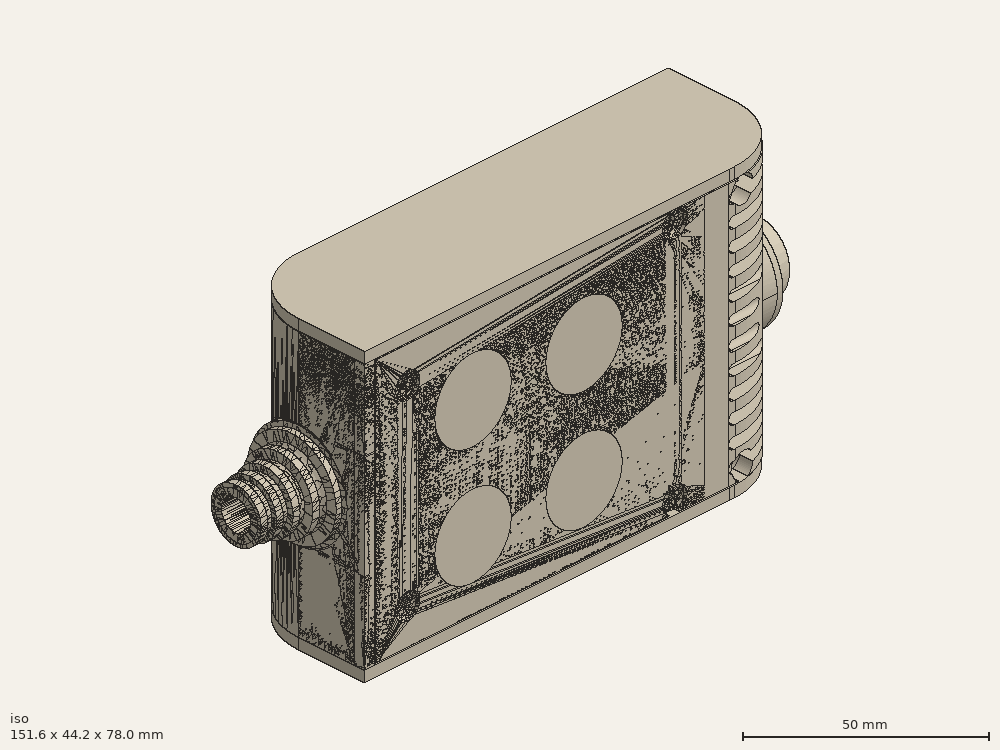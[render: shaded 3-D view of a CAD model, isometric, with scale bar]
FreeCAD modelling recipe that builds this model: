
FCSTD DOCUMENT  (FreeCAD 0.19R0.19.2)
Label: enclosure_187FCStd
License: All rights reserved
LicenseURL: http://en.wikipedia.org/wiki/All_rights_reserved
objects: Part::Revolution×152, Part::MultiFuse×146, Part::Feature×146, Sketcher::SketchObject×84, Part::Cut×70, Part::Cylinder×70, Part::Extrusion×67, Part::Fillet×58, Part::Box×36, App::MeasureDistance×4, PartDesign::Body×2, Image::ImagePlane×1
note: 831 computed .brp shape members not serialized (recipe doc carries the construction recipe); baked Part::Feature solids carry a one-line shape summary decoded from their .brp

FEATURE [Sketcher::SketchObject] Sketch  label="topSketch"
  FullyConstrained = true
  sketch-geometry (20):
    g0: LineSegment StartX=5.21097e-06 StartY=3 StartZ=0 EndX=5.21097e-06 EndY=19 EndZ=0
    g1: ArcOfCircle CenterX=19 CenterY=19 CenterZ=0 NormalX=0 NormalY=0 NormalZ=1 AngleXU=0 Radius=19 StartAngle=1.5708 EndAngle=3.14159
    g2: ArcOfCircle CenterX=19 CenterY=19 CenterZ=0 NormalX=0 NormalY=0 NormalZ=1 AngleXU=0 Radius=16 StartAngle=1.5708 EndAngle=3.14159
    g3: LineSegment StartX=114 StartY=35 StartZ=0 EndX=19 EndY=35 EndZ=0
    g4: LineSegment StartX=5.21097e-06 StartY=3 StartZ=0 EndX=5.21097e-06 EndY=0 EndZ=0
    g5: LineSegment StartX=3 StartY=0 StartZ=0 EndX=5.21097e-06 EndY=0 EndZ=0
    g6: LineSegment StartX=3 StartY=19 StartZ=0 EndX=3 EndY=0 EndZ=0
    g7: LineSegment StartX=19 StartY=38 StartZ=0 EndX=124 EndY=38 EndZ=0
    g8: Circle CenterX=119 CenterY=35 CenterZ=0 NormalX=0 NormalY=0 NormalZ=1 AngleXU=0 Radius=1
    g9: Circle CenterX=121 CenterY=35 CenterZ=0 NormalX=0 NormalY=0 NormalZ=1 AngleXU=0 Radius=1
    g10: Circle CenterX=121 CenterY=33 CenterZ=0 NormalX=0 NormalY=0 NormalZ=1 AngleXU=0 Radius=1
    g11: BSplineCurve PolesCount=3 KnotsCount=2 Degree=2 IsPeriodic=0
    g12: GeomPoint X=119 Y=35 Z=0
    g13: GeomPoint X=121 Y=33 Z=0
    g14: LineSegment StartX=119 StartY=35 StartZ=0 EndX=114 EndY=35 EndZ=0
    g15: ArcOfCircle CenterX=105 CenterY=19 CenterZ=0 NormalX=0 NormalY=0 NormalZ=1 AngleXU=0 Radius=19 StartAngle=5.7297 EndAngle=6.28319
    g16: ArcOfCircle CenterX=105 CenterY=19 CenterZ=0 NormalX=0 NormalY=0 NormalZ=1 AngleXU=0 Radius=16 StartAngle=5.60905 EndAngle=6.28319
    g17: LineSegment StartX=121 StartY=33 StartZ=0 EndX=121 EndY=19 EndZ=0
    g18: LineSegment StartX=124 StartY=38 StartZ=0 EndX=124 EndY=19 EndZ=0
    g19: LineSegment StartX=117.5 StartY=9.01251 StartZ=0 EndX=121.163 EndY=9.0125 EndZ=0
  constraints (46):
    c: Vertical(g0)
    c: Block(g0)
    c: Coincident(g1,g0)
    c: Block(g1)
    c: Coincident(g2,g1)
    c: Block(g2)
    c: Coincident(g3,g2)
    c: Horizontal(g3)
    c: Tangent(g3,g2)
    c: Coincident(g4,g0)
    c: Distance(g4) = 3
    c: Vertical(g4)
    c: Coincident(g5,g4)
    c: Horizontal(g5)
    c: Coincident(g6,g2)
    c: Coincident(g6,g5)
    c: Vertical(g6)
    c: Horizontal(g7)
    c: Distance(g7) = 105
    c: Coincident(g7,g1)
    c: Block(g3)
    c: Weight(g8) = 1
    c: Equal(g8,g9)
    c: Equal(g8,g10)
    c: InternalAlignment(g8,g11)
    c: InternalAlignment(g9,g11)
    c: InternalAlignment(g10,g11)
    c: InternalAlignment(g12,g11)
    c: InternalAlignment(g13,g11)
    c: Block(g11)
    c: Coincident(g14,g11)
    c: Coincident(g14,g3)
    c: Horizontal(g14)
    c: Block(g15)
    c: Coincident(g16,g15)
    c: Block(g16)
    c: Coincident(g17,g11)
    c: Coincident(g17,g16)
    c: Vertical(g17)
    c: Distance(g17) = 14
    c: Coincident(g18,g7)
    c: Coincident(g18,g15)
    c: Vertical(g18)
    c: Distance(g18) = 19
    c: Coincident(g19,g16)
    c: Coincident(g19,g15)
FEATURE [Sketcher::SketchObject] Sketch001  label="bottomSketch"
  FullyConstrained = true
  sketch-geometry (32):
    g0: LineSegment StartX=3.3 StartY=-6.03275e-07 StartZ=0 EndX=98 EndY=-6.03275e-07 EndZ=0
    g1: ArcOfCircle CenterX=98 CenterY=19 CenterZ=0 NormalX=0 NormalY=0 NormalZ=1 AngleXU=0 Radius=19 StartAngle=4.71239 EndAngle=5.71103
    g2: LineSegment StartX=6.3 StartY=8 StartZ=0 EndX=3.3 EndY=8 EndZ=0
    g3: LineSegment StartX=3.3 StartY=8 StartZ=0 EndX=3.3 EndY=-6.03275e-07 EndZ=0
    g4: ArcOfCircle CenterX=8.3 CenterY=5 CenterZ=0 NormalX=0 NormalY=0 NormalZ=1 AngleXU=0 Radius=2 StartAngle=3.14159 EndAngle=4.71239
    g5: LineSegment StartX=6.3 StartY=8 StartZ=0 EndX=6.3 EndY=5 EndZ=0
    g6: ArcOfCircle CenterX=98 CenterY=19 CenterZ=0 NormalX=0 NormalY=0 NormalZ=1 AngleXU=0 Radius=12.7 StartAngle=4.71239 EndAngle=6.28319
    g7: LineSegment StartX=94.7 StartY=3 StartZ=0 EndX=8.3 EndY=3 EndZ=0
    g8-g12: Circle x5 (B-spline internal-alignment scaffolding for g13; pole/knot coordinates omitted)
    g13: BSplineCurve PolesCount=5 KnotsCount=3 Degree=3 IsPeriodic=0
    g14: GeomPoint X=98 Y=6.3 Z=0
    g15: GeomPoint X=96.3938 Y=4.71946 Z=0
    g16: GeomPoint X=94.7 Y=3 Z=0
    g17-g23: Circle x7 (B-spline internal-alignment scaffolding for g24; pole/knot coordinates omitted)
    g24: BSplineCurve PolesCount=7 KnotsCount=5 Degree=3 IsPeriodic=0
    g25-g29: GeomPoint x5 (B-spline internal-alignment scaffolding for g24; pole/knot coordinates omitted)
    g30: ArcOfCircle CenterX=98 CenterY=19 CenterZ=0 NormalX=0 NormalY=0 NormalZ=1 AngleXU=0 Radius=15.7 StartAngle=5.81226 EndAngle=6.28319
    g31: LineSegment StartX=110.7 StartY=19 StartZ=0 EndX=113.7 EndY=19 EndZ=0
  constraints (41):
    c: Horizontal(g0)
    c: Coincident(g1,g0)
    c: Block(g1)
    c: Horizontal(g2)
    c: Distance(g2) = 3
    c: Coincident(g3,g2)
    c: Vertical(g3)
    c: Coincident(g3,g0)
    c: Block(g4)
    c: Block(g2)
    c: Coincident(g5,g2)
    c: Coincident(g5,g4)
    c: Vertical(g5)
    c: Coincident(g6,g1)
    c: Block(g6)
    c: Coincident(g7,g4)
    c: Horizontal(g7)
    c: Block(g0)
    c: Block(g7)
    c: Block(g3)
    c: Coincident(g13,g6)
    c: Weight(g8) = 1
    c: Equal(g8, g9-g12) x4
    c: Coincident(g13,g7)
    c: InternalAlignment(g8-g12 -> g13) x5
    c: InternalAlignment(g14,g13)
    c: InternalAlignment(g15,g13)
    c: InternalAlignment(g16,g13)
    c: Block(g13)
    c: Weight(g17) = 1
    c: Equal(g17, g18-g23) x6
    c: Coincident(g24,g1)
    c: InternalAlignment(g17-g23 -> g24) x7
    c: InternalAlignment(g25-g29 -> g24) x5
    c: Block(g24)
    c: Coincident(g30,g24)
    c: Coincident(g31,g6)
    c: Coincident(g31,g30)
    c: Horizontal(g31)
    c: Block(g31)
    c: Block(g30)
FEATURE [Part::Extrusion] Extrude  label="top"
  Base = -> Sketch
  Dir = (0,0,1)
  DirMode = 2
  FaceMakerClass = Part::FaceMakerBullseye
  LengthFwd = 72
  LengthRev = 0
  Solid = true
  Symmetric = false
FEATURE [Part::Extrusion] Extrude001  label="bottom"
  Base = -> Sketch001
  Dir = (0,0,1)
  DirMode = 2
  FaceMakerClass = Part::FaceMakerBullseye
  LengthFwd = 71.4
  LengthRev = 0
  Placement = pos=(0,0,0.3) rot=(0,0,1;0rad)
  Solid = true
  Symmetric = false
FEATURE [Sketcher::SketchObject] Sketch002  label="topSketch001"
  FullyConstrained = true
  sketch-geometry (8):
    g0: ArcOfCircle CenterX=19 CenterY=19.0975 CenterZ=0 NormalX=0 NormalY=0 NormalZ=1 AngleXU=0 Radius=18.9025 StartAngle=1.5708 EndAngle=3.14674
    g1: LineSegment StartX=0.0977805 StartY=19.0003 StartZ=0 EndX=0.0977805 EndY=0.000251602 EndZ=0
    g2: LineSegment StartX=19 StartY=38 StartZ=0 EndX=124 EndY=38 EndZ=0
    g3: LineSegment StartX=0.0977805 StartY=0.000251602 StartZ=0 EndX=105.098 EndY=0.000251602 EndZ=0
    g4: LineSegment StartX=124 StartY=38 StartZ=0 EndX=125.616 EndY=38 EndZ=0
    g5: LineSegment StartX=105.098 StartY=0.000251602 StartZ=0 EndX=106.713 EndY=0.000251602 EndZ=0
    g6: ArcOfCircle CenterX=106.616 CenterY=19 CenterZ=0 NormalX=0 NormalY=0 NormalZ=1 AngleXU=0 Radius=19 StartAngle=4.71754 EndAngle=6.28319
    g7: LineSegment StartX=125.616 StartY=38 StartZ=0 EndX=125.616 EndY=19 EndZ=0
  constraints (21):
    c: Block(g0)
    c: Coincident(g1,g0)
    c: Vertical(g1)
    c: Horizontal(g2)
    c: Distance(g2) = 105
    c: Coincident(g2,g0)
    c: Distance(g1) = 19
    c: Coincident(g3,g1)
    c: Horizontal(g3)
    c: Distance(g3) = 105
    c: Coincident(g4,g2)
    c: Horizontal(g4)
    c: Distance(g4) = 1.61553
    c: Horizontal(g5)
    c: Equal(g4,g5) = 1.61553
    c: Coincident(g5,g3)
    c: Block(g6)
    c: Coincident(g6,g5)
    c: Coincident(g7,g4)
    c: Coincident(g7,g6)
    c: Vertical(g7)
FEATURE [Part::Extrusion] Extrude002  label="sideA"
  Base = -> Sketch002
  Dir = (0,0,1)
  DirMode = 2
  FaceMakerClass = Part::FaceMakerBullseye
  LengthFwd = 3
  LengthRev = 0
  Placement = pos=(0,0,-3) rot=(0,0,1;0rad)
  Solid = true
  Symmetric = false
FEATURE [Sketcher::SketchObject] Sketch003  label="topSketch002"
  FullyConstrained = true
  sketch-geometry (6):
    g0: LineSegment StartX=19 StartY=38 StartZ=0 EndX=117 EndY=38 EndZ=0
    g1: ArcOfCircle CenterX=19 CenterY=19 CenterZ=0 NormalX=0 NormalY=0 NormalZ=1 AngleXU=0 Radius=19 StartAngle=1.5708 EndAngle=3.14159
    g2: LineSegment StartX=117 StartY=38 StartZ=0 EndX=117 EndY=19 EndZ=0
    g3: LineSegment StartX=98 StartY=1.0161e-12 StartZ=0 EndX=5.22862e-06 EndY=1.0161e-12 EndZ=0
    g4: LineSegment StartX=5.22862e-06 StartY=19 StartZ=0 EndX=5.22862e-06 EndY=1.0161e-12 EndZ=0
    g5: ArcOfCircle CenterX=98 CenterY=19 CenterZ=0 NormalX=0 NormalY=0 NormalZ=1 AngleXU=0 Radius=19 StartAngle=4.71239 EndAngle=6.28319
  constraints (16):
    c: Horizontal(g0)
    c: Distance(g0) = 98
    c: Coincident(g1,g0)
    c: Block(g1)
    c: Coincident(g2,g0)
    c: Vertical(g2)
    c: Distance(g2) = 19
    c: Horizontal(g3)
    c: Coincident(g4,g1)
    c: Vertical(g4)
    c: Coincident(g3,g4)
    c: Block(g3)
    c: Coincident(g5,g2)
    c: Coincident(g5,g3)
    c: Block(g0)
    c: Block(g5)
FEATURE [Sketcher::SketchObject] Sketch004
  FullyConstrained = true
  MapMode = 3
  Placement = pos=(0,0,0) rot=(1,0,0;1.5708rad)
  Support = -> [Extrude]
  sketch-geometry (8):
    g0: Circle CenterX=80.351 CenterY=-67.6202 CenterZ=0 NormalX=0 NormalY=0 NormalZ=1 AngleXU=0 Radius=2
    g1: Circle CenterX=80.351 CenterY=-67.6202 CenterZ=0 NormalX=0 NormalY=0 NormalZ=1 AngleXU=0 Radius=3
    g2: Circle CenterX=80.351 CenterY=-4.92017 CenterZ=0 NormalX=0 NormalY=0 NormalZ=1 AngleXU=0 Radius=2
    g3: Circle CenterX=80.351 CenterY=-4.92017 CenterZ=0 NormalX=0 NormalY=0 NormalZ=1 AngleXU=0 Radius=3
    g4: Circle CenterX=23.851 CenterY=-4.92017 CenterZ=0 NormalX=0 NormalY=0 NormalZ=1 AngleXU=0 Radius=2
    g5: Circle CenterX=23.851 CenterY=-4.92017 CenterZ=0 NormalX=0 NormalY=0 NormalZ=1 AngleXU=0 Radius=3
    g6: Circle CenterX=23.851 CenterY=-67.6202 CenterZ=0 NormalX=0 NormalY=0 NormalZ=1 AngleXU=0 Radius=2
    g7: Circle CenterX=23.851 CenterY=-67.6202 CenterZ=0 NormalX=0 NormalY=0 NormalZ=1 AngleXU=0 Radius=3
  constraints (8):
    c: Block(g3)
    c: Block(g2)
    c: Block(g1)
    c: Block(g0)
    c: Block(g6)
    c: Block(g7)
    c: Block(g4)
    c: Block(g5)
FEATURE [Part::Extrusion] Extrude004
  Base = -> Sketch004
  Dir = (0,-1,2e-16)
  DirMode = 2
  FaceMakerClass = Part::FaceMakerBullseye
  LengthFwd = 6
  LengthRev = 0
  Placement = pos=(0,9,0) rot=(0,0,1;0rad)
  Solid = true
  Symmetric = false
FEATURE [Sketcher::SketchObject] Sketch005
  FullyConstrained = true
  MapMode = 3
  Placement = pos=(0,0,0) rot=(1,0,0;1.5708rad)
  Support = -> [Extrude]
  sketch-geometry (8):
    g0: Circle CenterX=80.351 CenterY=-67.6202 CenterZ=0 NormalX=0 NormalY=0 NormalZ=1 AngleXU=0 Radius=3
    g1: Circle CenterX=80.351 CenterY=-4.92017 CenterZ=0 NormalX=0 NormalY=0 NormalZ=1 AngleXU=0 Radius=3
    g2: Circle CenterX=23.851 CenterY=-4.92017 CenterZ=0 NormalX=0 NormalY=0 NormalZ=1 AngleXU=0 Radius=3
    g3: Circle CenterX=23.851 CenterY=-67.6202 CenterZ=0 NormalX=0 NormalY=0 NormalZ=1 AngleXU=0 Radius=3
    g4: Circle CenterX=23.851 CenterY=-67.6202 CenterZ=0 NormalX=0 NormalY=0 NormalZ=1 AngleXU=0 Radius=5
    g5: Circle CenterX=80.351 CenterY=-67.6202 CenterZ=0 NormalX=0 NormalY=0 NormalZ=1 AngleXU=0 Radius=5
    g6: Circle CenterX=23.851 CenterY=-4.92017 CenterZ=0 NormalX=0 NormalY=0 NormalZ=1 AngleXU=0 Radius=5
    g7: Circle CenterX=80.351 CenterY=-4.92017 CenterZ=0 NormalX=0 NormalY=0 NormalZ=1 AngleXU=0 Radius=5
  constraints (8):
    c: Block(g1)
    c: Block(g0)
    c: Block(g3)
    c: Block(g2)
    c: Block(g5)
    c: Block(g4)
    c: Block(g6)
    c: Block(g7)
FEATURE [Part::Extrusion] Extrude005
  Base = -> Sketch005
  Dir = (0,-1,2e-16)
  DirMode = 2
  FaceMakerClass = Part::FaceMakerBullseye
  LengthFwd = 2
  LengthRev = 0
  Solid = true
  Symmetric = false
FEATURE [Sketcher::SketchObject] Sketch006
  FullyConstrained = true
  MapMode = 3
  Placement = pos=(0,0,0) rot=(1,0,0;1.5708rad)
  sketch-geometry (8):
    g0: Circle CenterX=80.351 CenterY=-67.6202 CenterZ=0 NormalX=0 NormalY=0 NormalZ=1 AngleXU=0 Radius=3
    g1: Circle CenterX=80.351 CenterY=-4.92017 CenterZ=0 NormalX=0 NormalY=0 NormalZ=1 AngleXU=0 Radius=3
    g2: Circle CenterX=23.851 CenterY=-4.92017 CenterZ=0 NormalX=0 NormalY=0 NormalZ=1 AngleXU=0 Radius=3
    g3: Circle CenterX=23.851 CenterY=-67.6202 CenterZ=0 NormalX=0 NormalY=0 NormalZ=1 AngleXU=0 Radius=3
    g4: Circle CenterX=23.851 CenterY=-67.6202 CenterZ=0 NormalX=0 NormalY=0 NormalZ=1 AngleXU=0 Radius=5
    g5: Circle CenterX=80.351 CenterY=-67.6202 CenterZ=0 NormalX=0 NormalY=0 NormalZ=1 AngleXU=0 Radius=5
    g6: Circle CenterX=23.851 CenterY=-4.92017 CenterZ=0 NormalX=0 NormalY=0 NormalZ=1 AngleXU=0 Radius=5
    g7: Circle CenterX=80.351 CenterY=-4.92017 CenterZ=0 NormalX=0 NormalY=0 NormalZ=1 AngleXU=0 Radius=5
  constraints (8):
    c: Block(g1)
    c: Block(g0)
    c: Block(g3)
    c: Block(g2)
    c: Block(g5)
    c: Block(g4)
    c: Block(g6)
    c: Block(g7)
FEATURE [Part::Extrusion] Extrude007
  Base = -> Sketch006
  Dir = (0,-1,2e-16)
  DirMode = 2
  FaceMakerClass = Part::FaceMakerBullseye
  LengthFwd = 2
  LengthRev = 0
  Solid = true
  Symmetric = false
FEATURE [Part::Fillet] Fillet
  Base = -> Extrude007
  Edges = 4 edges r=1.99: [Edge6,Edge12,Edge18,Edge24]
FEATURE [Part::Cut] Cut
  Base = -> Extrude005
  Placement = pos=(0,5,0) rot=(0,0,1;0rad)
  Tool = -> Fillet
FEATURE [Part::MultiFuse] Fusion  label="pCBScrews"
  Placement = pos=(-2.5,0,72.3) rot=(0,0,1;0rad)
  Shapes = -> [Extrude004,Cut]
FEATURE [App::MeasureDistance] Distance  label="Distance: 0.69 mm"
  Distance = 0.685967
  P1 = (24.0138,2.9647,0.3)
  P2 = (23.8901,3,-0.373787)
FEATURE [App::MeasureDistance] Distance001  label="Distance: 0.53 mm"
  Distance = 0.533607
  P1 = (80.2939,3,72.2334)
  P2 = (80.281,2.99661,71.7)
FEATURE [Part::Fillet] Fillet001
  Base = -> Extrude001
  Edges = 1 edges r=2.4: [Edge17]
FEATURE [Part::Fillet] Fillet002  label="bottom001"
  Base = -> Fillet001
  Edges = 1 edges r=2.4: [Edge36]
FEATURE [Part::Fillet] Fillet003  label="top001"
  Base = -> Extrude
  Edges = 1 edges r=2: [Edge1]
FEATURE [Sketcher::SketchObject] Sketch007
  FullyConstrained = true
  sketch-geometry (16):
    g0: LineSegment StartX=4 StartY=0 StartZ=0 EndX=4 EndY=2.4 EndZ=0
    g1: LineSegment StartX=4 StartY=2.4 StartZ=0 EndX=7 EndY=2.4 EndZ=0
    g2: LineSegment StartX=4 StartY=0 StartZ=0 EndX=5.7 EndY=0 EndZ=0
    g3: LineSegment StartX=5.7 StartY=0 StartZ=0 EndX=5.7 EndY=-5.6 EndZ=0
    g4-g8: Circle x5 (B-spline internal-alignment scaffolding for g9; pole/knot coordinates omitted)
    g9: BSplineCurve PolesCount=5 KnotsCount=3 Degree=3 IsPeriodic=0
    g10: GeomPoint X=7 Y=2.4 Z=0
    g11: GeomPoint X=10.4582 Y=-1.55472 Z=0
    g12: GeomPoint X=14 Y=-5.6 Z=0
    g13: LineSegment StartX=14 StartY=-5.6 StartZ=0 EndX=14 EndY=-14.1 EndZ=0
    g14: LineSegment StartX=14 StartY=-14.1 StartZ=0 EndX=6.5 EndY=-14.1 EndZ=0
    g15: LineSegment StartX=5.7 StartY=-5.6 StartZ=0 EndX=6.5 EndY=-14.1 EndZ=0
  constraints (28):
    c: Distance(g0) = 2.4
    c: Vertical(g0)
    c: Block(g0)
    c: Coincident(g1,g0)
    c: Horizontal(g1)
    c: Distance(g1) = 3
    c: Coincident(g2,g0)
    c: Horizontal(g2)
    c: Distance(g2) = 1.7
    c: Coincident(g3,g2)
    c: Vertical(g3)
    c: Distance(g3) = 5.6
    c: Coincident(g9,g1)
    c: Weight(g4) = 1
    c: Equal(g4, g5-g8) x4
    c: InternalAlignment(g4-g8 -> g9) x5
    c: InternalAlignment(g10,g9)
    c: InternalAlignment(g11,g9)
    c: InternalAlignment(g12,g9)
    c: Block(g9)
    c: Coincident(g13,g9)
    c: Vertical(g13)
    c: Distance(g13) = 8.5
    c: Coincident(g14,g13)
    c: Horizontal(g14)
    c: Distance(g14) = 7.5
    c: Coincident(g15,g3)
    c: Coincident(g15,g14)
FEATURE [Part::Feature] Face
  shape: bbox 10 x 16.5 x 2e-07 mm, 1 faces, 0 solids (baked)
FEATURE [Part::Revolution] Revolve  label="plugHousing"
  Angle = 360
  Axis = (0,1,0)
  Base = (0,0,0)
  FaceMakerClass = Part::FaceMakerBullseye
  Placement = pos=(0,0,36.15) rot=(0,0,1;0rad)
  Solid = false
  Source = -> Face
  Symmetric = false
FEATURE [Part::Feature] Face001
  shape: bbox 10 x 16.5 x 2e-07 mm, 1 faces, 0 solids (baked)
FEATURE [Part::Revolution] Revolve001  label="plugHousing001"
  Angle = 360
  Axis = (0,1,0)
  Base = (0,0,0)
  FaceMakerClass = Part::FaceMakerBullseye
  Placement = pos=(0,0,36.15) rot=(0,0,1;0rad)
  Solid = false
  Source = -> Face001
  Symmetric = false
FEATURE [Part::MultiFuse] Fusion001  label="plugHousing002"
  Placement = pos=(0,0,0) rot=(0,0,1;1.5708rad)
  Shapes = -> [Revolve001,Revolve]
FEATURE [Part::Feature] Face002
  shape: bbox 10 x 16.5 x 2e-07 mm, 1 faces, 0 solids (baked)
FEATURE [Part::Revolution] Revolve003  label="plugHousing005"
  Angle = 360
  Axis = (0,1,0)
  Base = (0,0,0)
  FaceMakerClass = Part::FaceMakerBullseye
  Placement = pos=(0,0,36.15) rot=(0,0,1;0rad)
  Solid = false
  Source = -> Face002
  Symmetric = false
FEATURE [Part::Feature] Face003
  shape: bbox 10 x 16.5 x 2e-07 mm, 1 faces, 0 solids (baked)
FEATURE [Part::Revolution] Revolve002  label="plugHousing003"
  Angle = 360
  Axis = (0,1,0)
  Base = (0,0,0)
  FaceMakerClass = Part::FaceMakerBullseye
  Placement = pos=(0,0,36.15) rot=(0,0,1;0rad)
  Solid = false
  Source = -> Face003
  Symmetric = false
FEATURE [Part::MultiFuse] Fusion002  label="plugHousing004"
  Placement = pos=(0,0,0) rot=(0,0,1;1.5708rad)
  Shapes = -> [Revolve002,Revolve003]
FEATURE [Part::MultiFuse] Fusion003  label="plugHousing006"
  Placement = pos=(0,19,0) rot=(0,0,1;3.14159rad)
  Shapes = -> [Fusion002,Fusion001]
FEATURE [Part::Feature] Face004
  shape: bbox 10 x 16.5 x 2e-07 mm, 1 faces, 0 solids (baked)
FEATURE [Part::Revolution] Revolve006  label="plugHousing010"
  Angle = 360
  Axis = (0,1,0)
  Base = (0,0,0)
  FaceMakerClass = Part::FaceMakerBullseye
  Placement = pos=(0,0,36.15) rot=(0,0,1;0rad)
  Solid = false
  Source = -> Face004
  Symmetric = false
FEATURE [Part::Feature] Face005
  shape: bbox 10 x 16.5 x 2e-07 mm, 1 faces, 0 solids (baked)
FEATURE [Part::Revolution] Revolve007  label="plugHousing011"
  Angle = 360
  Axis = (0,1,0)
  Base = (0,0,0)
  FaceMakerClass = Part::FaceMakerBullseye
  Placement = pos=(0,0,36.15) rot=(0,0,1;0rad)
  Solid = false
  Source = -> Face005
  Symmetric = false
FEATURE [Part::Feature] Face006
  shape: bbox 10 x 16.5 x 2e-07 mm, 1 faces, 0 solids (baked)
FEATURE [Part::Revolution] Revolve004  label="plugHousing007"
  Angle = 360
  Axis = (0,1,0)
  Base = (0,0,0)
  FaceMakerClass = Part::FaceMakerBullseye
  Placement = pos=(0,0,36.15) rot=(0,0,1;0rad)
  Solid = false
  Source = -> Face006
  Symmetric = false
FEATURE [Part::MultiFuse] Fusion004  label="plugHousing009"
  Placement = pos=(0,0,0) rot=(0,0,1;1.5708rad)
  Shapes = -> [Revolve004,Revolve007]
FEATURE [Part::Feature] Face007
  shape: bbox 10 x 16.5 x 2e-07 mm, 1 faces, 0 solids (baked)
FEATURE [Part::Revolution] Revolve005  label="plugHousing008"
  Angle = 360
  Axis = (0,1,0)
  Base = (0,0,0)
  FaceMakerClass = Part::FaceMakerBullseye
  Placement = pos=(0,0,36.15) rot=(0,0,1;0rad)
  Solid = false
  Source = -> Face007
  Symmetric = false
FEATURE [Part::MultiFuse] Fusion005  label="plugHousing012"
  Placement = pos=(0,0,0) rot=(0,0,1;1.5708rad)
  Shapes = -> [Revolve006,Revolve005]
FEATURE [Part::MultiFuse] Fusion006  label="plugHousing013"
  Placement = pos=(0,19,0) rot=(0,0,1;3.14159rad)
  Shapes = -> [Fusion005,Fusion004]
FEATURE [Part::MultiFuse] Fusion007  label="plugHousing014"
  Placement = pos=(122.621,0,-0.15) rot=(0,0,1;0rad)
  Shapes = -> [Fusion003,Fusion006]
FEATURE [Part::Cylinder] Cylinder002
  Angle = 360
  AttacherType = Attacher::AttachEngine3D
  Height = 20
  Placement = pos=(0,0,36.15) rot=(0,0,1;0rad)
  Radius = 4
FEATURE [Part::Cylinder] Cylinder003
  Angle = 360
  AttacherType = Attacher::AttachEngine3D
  Height = 10
  Placement = pos=(0,0,36.15) rot=(0,0,1;0rad)
  Radius = 4
FEATURE [Part::MultiFuse] Fusion009  label="removeToCreateHoleForPlugHousing"
  Placement = pos=(70,19,36.15) rot=(0,1,0;1.5708rad)
  Shapes = -> [Cylinder002,Cylinder003]
FEATURE [Part::Cylinder] Cylinder004
  Angle = 360
  AttacherType = Attacher::AttachEngine3D
  Height = 20
  Placement = pos=(0,0,36.15) rot=(0,0,1;0rad)
  Radius = 4
FEATURE [Part::Cylinder] Cylinder005
  Angle = 360
  AttacherType = Attacher::AttachEngine3D
  Height = 10
  Placement = pos=(0,0,36.15) rot=(0,0,1;0rad)
  Radius = 4
FEATURE [Part::MultiFuse] Fusion010  label="removeToCreateHoleForPlugHousing001"
  Placement = pos=(70,19,36.15) rot=(0,1,0;1.5708rad)
  Shapes = -> [Cylinder004,Cylinder005]
FEATURE [Part::Cut] Cut001
  Base = -> Fillet003
  Tool = -> Fusion010
FEATURE [Part::Cut] Cut002  label="Bottom"
  Base = -> Fillet002
  Tool = -> Fusion009
FEATURE [Part::Feature] Face008
  shape: bbox 10 x 16.5 x 2e-07 mm, 1 faces, 0 solids (baked)
FEATURE [Part::Revolution] Revolve011  label="plugHousing021"
  Angle = 360
  Axis = (0,1,0)
  Base = (0,0,0)
  FaceMakerClass = Part::FaceMakerBullseye
  Placement = pos=(0,0,36.15) rot=(0,0,1;0rad)
  Solid = false
  Source = -> Face008
  Symmetric = false
FEATURE [Part::Feature] Face009
  shape: bbox 10 x 16.5 x 2e-07 mm, 1 faces, 0 solids (baked)
FEATURE [Part::Revolution] Revolve012  label="plugHousing022"
  Angle = 360
  Axis = (0,1,0)
  Base = (0,0,0)
  FaceMakerClass = Part::FaceMakerBullseye
  Placement = pos=(0,0,36.15) rot=(0,0,1;0rad)
  Solid = false
  Source = -> Face009
  Symmetric = false
FEATURE [Part::Feature] Face010 .. Face013  x4 (patterned run collapsed; names and placements below)
  shape: bbox 10 x 16.5 x 2e-07 mm, 1 faces, 0 solids (baked)
FEATURE [Part::Revolution] Revolve015  label="plugHousing027"
  Angle = 360
  Axis = (0,1,0)
  Base = (0,0,0)
  FaceMakerClass = Part::FaceMakerBullseye
  Placement = pos=(0,0,36.15) rot=(0,0,1;0rad)
  Solid = false
  Source = -> Face013
  Symmetric = false
FEATURE [Part::Feature] Face014
  shape: bbox 10 x 16.5 x 2e-07 mm, 1 faces, 0 solids (baked)
FEATURE [Part::Feature] Face015
  shape: bbox 10 x 16.5 x 2e-07 mm, 1 faces, 0 solids (baked)
FEATURE [Part::Feature] Face016
  shape: bbox 10 x 16.5 x 2e-07 mm, 1 faces, 0 solids (baked)
FEATURE [Part::Revolution] Revolve019  label="plugHousing033"
  Angle = 360
  Axis = (0,1,0)
  Base = (0,0,0)
  FaceMakerClass = Part::FaceMakerBullseye
  Placement = pos=(0,0,36.15) rot=(0,0,1;0rad)
  Solid = false
  Source = -> Face016
  Symmetric = false
FEATURE [Part::Feature] Face017
  shape: bbox 10 x 16.5 x 2e-07 mm, 1 faces, 0 solids (baked)
FEATURE [Part::Revolution] Revolve020  label="plugHousing034"
  Angle = 360
  Axis = (0,1,0)
  Base = (0,0,0)
  FaceMakerClass = Part::FaceMakerBullseye
  Placement = pos=(0,0,36.15) rot=(0,0,1;0rad)
  Solid = false
  Source = -> Face017
  Symmetric = false
FEATURE [Part::Feature] Face018
  shape: bbox 10 x 16.5 x 2e-07 mm, 1 faces, 0 solids (baked)
FEATURE [Part::Revolution] Revolve016  label="plugHousing030"
  Angle = 360
  Axis = (0,1,0)
  Base = (0,0,0)
  FaceMakerClass = Part::FaceMakerBullseye
  Placement = pos=(0,0,36.15) rot=(0,0,1;0rad)
  Solid = false
  Source = -> Face018
  Symmetric = false
FEATURE [Part::MultiFuse] Fusion020  label="plugHousing038"
  Placement = pos=(0,0,0) rot=(0,0,1;1.5708rad)
  Shapes = -> [Revolve016,Revolve020]
FEATURE [Part::Feature] Face019
  shape: bbox 10 x 16.5 x 2e-07 mm, 1 faces, 0 solids (baked)
FEATURE [Part::Feature] Face020
  shape: bbox 10 x 16.5 x 2e-07 mm, 1 faces, 0 solids (baked)
FEATURE [Part::Revolution] Revolve017  label="plugHousing031"
  Angle = 360
  Axis = (0,1,0)
  Base = (0,0,0)
  FaceMakerClass = Part::FaceMakerBullseye
  Placement = pos=(0,0,36.15) rot=(0,0,1;0rad)
  Solid = false
  Source = -> Face020
  Symmetric = false
FEATURE [Part::MultiFuse] Fusion021  label="plugHousing039"
  Placement = pos=(0,0,0) rot=(0,0,1;1.5708rad)
  Shapes = -> [Revolve019,Revolve017]
FEATURE [Part::MultiFuse] Fusion023  label="plugHousing041"
  Placement = pos=(0,19,0) rot=(0,0,1;3.14159rad)
  Shapes = -> [Fusion021,Fusion020]
FEATURE [Part::Revolution] Revolve022  label="plugHousing043"
  Angle = 360
  Axis = (0,1,0)
  Base = (0,0,0)
  FaceMakerClass = Part::FaceMakerBullseye
  Placement = pos=(0,0,36.15) rot=(0,0,1;0rad)
  Solid = false
  Source = -> Face019
  Symmetric = false
FEATURE [Part::Feature] Face021
  shape: bbox 10 x 16.5 x 2e-07 mm, 1 faces, 0 solids (baked)
FEATURE [Part::Revolution] Revolve023  label="plugHousing044"
  Angle = 360
  Axis = (0,1,0)
  Base = (0,0,0)
  FaceMakerClass = Part::FaceMakerBullseye
  Placement = pos=(0,0,36.15) rot=(0,0,1;0rad)
  Solid = false
  Source = -> Face021
  Symmetric = false
FEATURE [Part::Feature] Face022
  shape: bbox 10 x 16.5 x 2e-07 mm, 1 faces, 0 solids (baked)
FEATURE [Part::Revolution] Revolve018  label="plugHousing032"
  Angle = 360
  Axis = (0,1,0)
  Base = (0,0,0)
  FaceMakerClass = Part::FaceMakerBullseye
  Placement = pos=(0,0,36.15) rot=(0,0,1;0rad)
  Solid = false
  Source = -> Face022
  Symmetric = false
FEATURE [Part::MultiFuse] Fusion022  label="plugHousing040"
  Placement = pos=(0,0,0) rot=(0,0,1;1.5708rad)
  Shapes = -> [Revolve018,Revolve023]
FEATURE [Part::Feature] Face023
  shape: bbox 10 x 16.5 x 2e-07 mm, 1 faces, 0 solids (baked)
FEATURE [Part::Revolution] Revolve021  label="plugHousing035"
  Angle = 360
  Axis = (0,1,0)
  Base = (0,0,0)
  FaceMakerClass = Part::FaceMakerBullseye
  Placement = pos=(0,0,36.15) rot=(0,0,1;0rad)
  Solid = false
  Source = -> Face023
  Symmetric = false
FEATURE [Part::MultiFuse] Fusion018  label="plugHousing036"
  Placement = pos=(0,0,0) rot=(0,0,1;1.5708rad)
  Shapes = -> [Revolve022,Revolve021]
FEATURE [Part::MultiFuse] Fusion019  label="plugHousing037"
  Placement = pos=(0,19,0) rot=(0,0,1;3.14159rad)
  Shapes = -> [Fusion018,Fusion022]
FEATURE [Part::MultiFuse] Fusion024  label="plugHousing042"
  Placement = pos=(122.621,0,-0.15) rot=(0,0,1;0rad)
  Shapes = -> [Fusion023,Fusion019]
FEATURE [Part::Cylinder] Cylinder006
  Angle = 360
  AttacherType = Attacher::AttachEngine3D
  Height = 20
  Placement = pos=(0,0,36.15) rot=(0,0,1;0rad)
  Radius = 14.3
FEATURE [Part::Cylinder] Cylinder007
  Angle = 360
  AttacherType = Attacher::AttachEngine3D
  Height = 10
  Placement = pos=(0,0,36.15) rot=(0,0,1;0rad)
  Radius = 4
FEATURE [Part::MultiFuse] Fusion026  label="removeToCreteHoleForPlugHousing"
  Placement = pos=(70,19,36) rot=(0,1,0;1.5708rad)
  Shapes = -> [Cylinder006,Cylinder007]
FEATURE [Part::Box] Box001  label="Cube001"
  AttacherType = Attacher::AttachEngine3D
  Height = 28
  Length = 3
  Placement = pos=(110.7,19,22) rot=(0,0,1;0rad)
  Width = 15.7
FEATURE [Part::Cut] Cut003  label="top002"
  Base = -> Cut001
  Tool = -> Fusion007
FEATURE [Part::Revolution] Revolve008  label="plugHousing015"
  Angle = 360
  Axis = (0,1,0)
  Base = (0,0,0)
  FaceMakerClass = Part::FaceMakerBullseye
  Placement = pos=(0,0,36.15) rot=(0,0,1;0rad)
  Solid = false
  Source = -> Face010
  Symmetric = false
FEATURE [Part::MultiFuse] Fusion013  label="plugHousing020"
  Placement = pos=(0,0,0) rot=(0,0,1;1.5708rad)
  Shapes = -> [Revolve008,Revolve012]
FEATURE [Part::Cut] Cut004  label="top003"
  Base = -> Cut003
  Placement = pos=(1,0,0) rot=(0,0,1;0rad)
  Tool = -> Fusion026
FEATURE [Part::Cylinder] Cylinder008
  Angle = 360
  AttacherType = Attacher::AttachEngine3D
  Height = 20
  Placement = pos=(0,0,36.15) rot=(0,0,1;0rad)
  Radius = 10.3
FEATURE [Part::Cylinder] Cylinder009
  Angle = 360
  AttacherType = Attacher::AttachEngine3D
  Height = 10
  Placement = pos=(0,0,36.15) rot=(0,0,1;0rad)
  Radius = 4
FEATURE [Part::MultiFuse] Fusion027  label="removeToCreteHoleForPlugHousing001"
  Placement = pos=(70,19,36) rot=(0,1,0;1.5708rad)
  Shapes = -> [Cylinder008,Cylinder009]
FEATURE [Part::Cut] Cut005  label="plugHousingTab"
  Base = -> Box001
  Tool = -> Fusion027
FEATURE [Part::MultiFuse] Fusion028  label="plugHousing045"
  Shapes = -> [Fusion024,Cut005]
FEATURE [Part::Box] Box002  label="Cube002"
  AttacherType = Attacher::AttachEngine3D
  Height = 28.8
  Length = 3
  Placement = pos=(107.3,28,21.6) rot=(0,0,1;0rad)
  Width = 7
FEATURE [Part::Box] Box003  label="Cube003"
  AttacherType = Attacher::AttachEngine3D
  Height = 3
  Length = 6.4
  Placement = pos=(107.3,28,18.6) rot=(0,0,1;0rad)
  Width = 7
FEATURE [Part::Box] Box004  label="Cube004"
  AttacherType = Attacher::AttachEngine3D
  Height = 3
  Length = 6.4
  Placement = pos=(107.3,28,50.4) rot=(0,0,1;0rad)
  Width = 7
FEATURE [Part::MultiFuse] Fusion029  label="plugHousingBracketHolder"
  Shapes = -> [Box004,Box002,Box003]
FEATURE [Part::Cylinder] Cylinder010
  Angle = 360
  AttacherType = Attacher::AttachEngine3D
  Height = 20
  Placement = pos=(0,0,36.15) rot=(0,0,1;0rad)
  Radius = 14.3
FEATURE [Part::Cylinder] Cylinder011
  Angle = 360
  AttacherType = Attacher::AttachEngine3D
  Height = 10
  Placement = pos=(0,0,36.15) rot=(0,0,1;0rad)
  Radius = 4
FEATURE [Part::MultiFuse] Fusion030  label="removeToCreteHoleForPlugHousing002"
  Placement = pos=(70,19,36) rot=(0,1,0;1.5708rad)
  Shapes = -> [Cylinder010,Cylinder011]
FEATURE [Part::Cut] Cut006  label="plugHousingBracketHolder001"
  Base = -> Fusion029
  Tool = -> Fusion030
FEATURE [Part::Cylinder] Cylinder012
  Angle = 360
  AttacherType = Attacher::AttachEngine3D
  Height = 20
  Placement = pos=(0,0,36.15) rot=(0,0,1;0rad)
  Radius = 7
FEATURE [Part::Cylinder] Cylinder013
  Angle = 360
  AttacherType = Attacher::AttachEngine3D
  Height = 10
  Placement = pos=(0,0,36.15) rot=(0,0,1;0rad)
  Radius = 4
FEATURE [Part::MultiFuse] Fusion032  label="removeToCreteHoleForPlugHousing003"
  Placement = pos=(70,19,36) rot=(0,1,0;1.5708rad)
  Shapes = -> [Cylinder012,Cylinder013]
FEATURE [Part::Cut] Cut007  label="bottom002"
  Base = -> Cut002
  Tool = -> Fusion032
FEATURE [Sketcher::SketchObject] Sketch008
  FullyConstrained = true
  sketch-geometry (54):
    g0: LineSegment StartX=-4.2 StartY=0 StartZ=0 EndX=-6.2 EndY=0 EndZ=0
    g1: LineSegment StartX=-14 StartY=-18 StartZ=0 EndX=-14 EndY=-26.5 EndZ=0
    g2: LineSegment StartX=-4.2 StartY=0 StartZ=0 EndX=-4.2 EndY=-13.4877 EndZ=0
    g3: Circle CenterX=-4.2 CenterY=-13.4877 CenterZ=0 NormalX=0 NormalY=0 NormalZ=1 AngleXU=0 Radius=1
    g4: Circle CenterX=-4.2 CenterY=-26.5 CenterZ=0 NormalX=0 NormalY=0 NormalZ=1 AngleXU=0 Radius=1
    g5: Circle CenterX=-8.2 CenterY=-26.5 CenterZ=0 NormalX=0 NormalY=0 NormalZ=1 AngleXU=0 Radius=1
    g6: BSplineCurve PolesCount=3 KnotsCount=2 Degree=2 IsPeriodic=0
    g7: GeomPoint X=-4.2 Y=-13.4877 Z=0
    g8: GeomPoint X=-8.2 Y=-26.5 Z=0
    g9: LineSegment StartX=-14 StartY=-26.5 StartZ=0 EndX=-8.2 EndY=-26.5 EndZ=0
    g10: LineSegment StartX=-10.15 StartY=-12 StartZ=0 EndX=-10.15 EndY=-14 EndZ=0
    g11: LineSegment StartX=-12.8401 StartY=-16 StartZ=0 EndX=-10.1571 EndY=-16 EndZ=0
    g12: LineSegment StartX=-10.15 StartY=-14 StartZ=0 EndX=-8.70761 EndY=-14 EndZ=0
    g13: LineSegment StartX=-12.8401 StartY=-16 StartZ=0 EndX=-12.8401 EndY=-17.6958 EndZ=0
    g14: LineSegment StartX=-10.15 StartY=-12 StartZ=0 EndX=-7.79258 EndY=-12 EndZ=0
    g15: Circle CenterX=-6.2215 CenterY=-2 CenterZ=0 NormalX=0 NormalY=0 NormalZ=1 AngleXU=0 Radius=1
    g16: Circle CenterX=-6.22762 CenterY=-2.58724 CenterZ=0 NormalX=0 NormalY=0 NormalZ=1 AngleXU=0 Radius=1
    g17: Circle CenterX=-6.32538 CenterY=-4 CenterZ=0 NormalX=0 NormalY=0 NormalZ=1 AngleXU=0 Radius=1
    g18: BSplineCurve PolesCount=3 KnotsCount=2 Degree=2 IsPeriodic=0
    g19: GeomPoint X=-6.2215 Y=-2 Z=0
    g20: GeomPoint X=-6.32538 Y=-4 Z=0
    g21: Circle CenterX=-6.48644 CenterY=-5.99526 CenterZ=0 NormalX=0 NormalY=0 NormalZ=1 AngleXU=0 Radius=1
    g22: Circle CenterX=-6.58486 CenterY=-6.99526 CenterZ=0 NormalX=0 NormalY=0 NormalZ=1 AngleXU=0 Radius=1
    g23: Circle CenterX=-6.77343 CenterY=-8 CenterZ=0 NormalX=0 NormalY=0 NormalZ=1 AngleXU=0 Radius=1
    g24: BSplineCurve PolesCount=3 KnotsCount=2 Degree=2 IsPeriodic=0
    g25: GeomPoint X=-6.48644 Y=-5.99526 Z=0
    g26: GeomPoint X=-6.77343 Y=-8 Z=0
    g27: Circle CenterX=-7.19003 CenterY=-10 CenterZ=0 NormalX=0 NormalY=0 NormalZ=1 AngleXU=0 Radius=1
    g28: Circle CenterX=-7.44407 CenterY=-11.0915 CenterZ=0 NormalX=0 NormalY=0 NormalZ=1 AngleXU=0 Radius=1
    g29: Circle CenterX=-7.79258 CenterY=-12 CenterZ=0 NormalX=0 NormalY=0 NormalZ=1 AngleXU=0 Radius=1
    g30: BSplineCurve PolesCount=3 KnotsCount=2 Degree=2 IsPeriodic=0
    g31: GeomPoint X=-7.19003 Y=-10 Z=0
    g32: GeomPoint X=-7.79258 Y=-12 Z=0
    g33: Circle CenterX=-8.70761 CenterY=-14 CenterZ=0 NormalX=0 NormalY=0 NormalZ=1 AngleXU=0 Radius=1
    g34: Circle CenterX=-9.33087 CenterY=-15.1837 CenterZ=0 NormalX=0 NormalY=0 NormalZ=1 AngleXU=0 Radius=1
    g35: Circle CenterX=-10.1571 CenterY=-16 CenterZ=0 NormalX=0 NormalY=0 NormalZ=1 AngleXU=0 Radius=1
    g36: BSplineCurve PolesCount=3 KnotsCount=2 Degree=2 IsPeriodic=0
    g37: GeomPoint X=-8.70761 Y=-14 Z=0
    g38: GeomPoint X=-10.1571 Y=-16 Z=0
    g39: Circle CenterX=-12.8401 CenterY=-17.6958 CenterZ=0 NormalX=0 NormalY=0 NormalZ=1 AngleXU=0 Radius=1
    g40: Circle CenterX=-13.3521 CenterY=-17.9027 CenterZ=0 NormalX=0 NormalY=0 NormalZ=1 AngleXU=0 Radius=1
    g41: Circle CenterX=-14 CenterY=-18 CenterZ=0 NormalX=0 NormalY=0 NormalZ=1 AngleXU=0 Radius=1
    g42: BSplineCurve PolesCount=3 KnotsCount=2 Degree=2 IsPeriodic=0
    g43: GeomPoint X=-12.8401 Y=-17.6958 Z=0
    g44: GeomPoint X=-14 Y=-18 Z=0
    g45: LineSegment StartX=-6.2 StartY=0 StartZ=0 EndX=-7.2 EndY=0 EndZ=0
    g46: LineSegment StartX=-7.2 StartY=0 StartZ=0 EndX=-7.2 EndY=-2 EndZ=0
    g47: LineSegment StartX=-7.2 StartY=-2 StartZ=0 EndX=-6.2215 EndY=-2 EndZ=0
    g48: LineSegment StartX=-6.32538 StartY=-4 StartZ=0 EndX=-7.65538 EndY=-4 EndZ=0
    g49: LineSegment StartX=-7.65538 StartY=-4 StartZ=0 EndX=-7.65538 EndY=-5.99526 EndZ=0
    g50: LineSegment StartX=-7.65538 StartY=-5.99526 StartZ=0 EndX=-6.48644 EndY=-5.99526 EndZ=0
    g51: LineSegment StartX=-6.77343 StartY=-8 StartZ=0 EndX=-8.43343 EndY=-8 EndZ=0
    g52: LineSegment StartX=-8.43343 StartY=-8 StartZ=0 EndX=-8.43343 EndY=-10 EndZ=0
    g53: LineSegment StartX=-8.43343 StartY=-10 StartZ=0 EndX=-7.19003 EndY=-10 EndZ=0
  constraints (112):
    c: Horizontal(g0)
    c: Distance(g0) = 2
    c: Block(g0)
    c: Vertical(g1)
    c: Coincident(g2,g0)
    c: Vertical(g2)
    c: Block(g2)
    c: Coincident(g6,g2)
    c: Weight(g3) = 1
    c: Equal(g3,g4)
    c: Equal(g3,g5)
    c: InternalAlignment(g3,g6)
    c: InternalAlignment(g4,g6)
    c: InternalAlignment(g5,g6)
    c: InternalAlignment(g7,g6)
    c: InternalAlignment(g8,g6)
    c: Block(g6)
    c: Coincident(g9,g1)
    c: Coincident(g9,g6)
    c: Horizontal(g9)
    c: Vertical(g10)
    c: Block(g10)
    c: Horizontal(g11)
    c: Block(g11)
    c: Coincident(g12,g10)
    c: Horizontal(g12)
    c: Block(g12)
    c: Coincident(g13,g11)
    c: Vertical(g13)
    c: Block(g13)
    c: Coincident(g14,g10)
    c: Horizontal(g14)
    c: Block(g14)
    c: Block(g9)
    c: Block(g1)
    c: Weight(g15) = 1
    c: Equal(g15,g16)
    c: Equal(g15,g17)
    c: InternalAlignment(g15,g18)
    c: InternalAlignment(g16,g18)
    c: InternalAlignment(g17,g18)
    c: InternalAlignment(g19,g18)
    c: InternalAlignment(g20,g18)
    c: Weight(g21) = 1
    c: Equal(g21,g22)
    c: Equal(g21,g23)
    c: InternalAlignment(g21,g24)
    c: InternalAlignment(g22,g24)
    c: InternalAlignment(g23,g24)
    c: InternalAlignment(g25,g24)
    c: InternalAlignment(g26,g24)
    c: Weight(g27) = 1
    c: Equal(g27,g28)
    c: Equal(g27,g29)
    c: Coincident(g30,g14)
    c: InternalAlignment(g27,g30)
    c: InternalAlignment(g28,g30)
    c: InternalAlignment(g29,g30)
    c: InternalAlignment(g31,g30)
    c: InternalAlignment(g32,g30)
    c: Coincident(g36,g12)
    c: Weight(g33) = 1
    c: Equal(g33,g34)
    c: Equal(g33,g35)
    c: Coincident(g36,g11)
    c: InternalAlignment(g33,g36)
    c: InternalAlignment(g34,g36)
    c: InternalAlignment(g35,g36)
    c: InternalAlignment(g37,g36)
    c: InternalAlignment(g38,g36)
    c: Coincident(g42,g13)
    c: Weight(g39) = 1
    c: Equal(g39,g40)
    c: Equal(g39,g41)
    c: Coincident(g42,g1)
    c: InternalAlignment(g39,g42)
    c: InternalAlignment(g40,g42)
    c: InternalAlignment(g41,g42)
    c: InternalAlignment(g43,g42)
    c: InternalAlignment(g44,g42)
    c: Block(g18)
    c: Block(g24)
    c: Block(g30)
    c: Block(g36)
    c: Block(g42)
    c: Horizontal(g45)
    c: Coincident(g45,g0)
    c: Vertical(g46)
    c: Coincident(g46,g45)
    c: Coincident(g47,g46)
    c: Coincident(g47,g18)
    c: Horizontal(g47)
    c: Block(g46)
    c: Coincident(g48,g18)
    c: Horizontal(g48)
    c: Distance(g48) = 1.33
    c: Vertical(g49)
    c: Coincident(g49,g48)
    c: Coincident(g50,g49)
    c: Coincident(g50,g24)
    c: Horizontal(g50)
    c: Tangent(g50,g22)
    c: Horizontal(g51)
    c: Coincident(g51,g24)
    c: Block(g51)
    c: Vertical(g52)
    c: Block(g52)
    c: Coincident(g52,g51)
    c: Coincident(g53,g52)
    c: Coincident(g53,g30)
    c: Horizontal(g53)
    c: Distance(g1) = 8.5
FEATURE [Part::Feature] Face024
  shape: bbox 9.8 x 26.5 x 2e-07 mm, 1 faces, 0 solids (baked)
FEATURE [Part::Revolution] Revolve024
  Angle = 360
  Axis = (0,1,0)
  Base = (0,0,0)
  FaceMakerClass = Part::FaceMakerBullseye
  Placement = pos=(0,0,0) rot=(0,0,1;1.5708rad)
  Solid = false
  Source = -> Face024
  Symmetric = false
FEATURE [Part::Feature] Face025
  shape: bbox 9.8 x 26.5 x 2e-07 mm, 1 faces, 0 solids (baked)
FEATURE [Part::Revolution] Revolve025
  Angle = 360
  Axis = (0,1,0)
  Base = (0,0,0)
  FaceMakerClass = Part::FaceMakerBullseye
  Placement = pos=(0,0,0) rot=(0,0,1;1.5708rad)
  Solid = false
  Source = -> Face025
  Symmetric = false
FEATURE [Part::MultiFuse] Fusion033
  Placement = pos=(-18,19,36) rot=(0,0,1;0rad)
  Shapes = -> [Revolve025,Revolve024]
FEATURE [Part::Cylinder] Cylinder014
  Angle = 360
  AttacherType = Attacher::AttachEngine3D
  Height = 20
  Placement = pos=(0,0,36.15) rot=(0,0,1;0rad)
  Radius = 14.3
FEATURE [Part::Cylinder] Cylinder015
  Angle = 360
  AttacherType = Attacher::AttachEngine3D
  Height = 10
  Placement = pos=(0,0,36.15) rot=(0,0,1;0rad)
  Radius = 4
FEATURE [Part::MultiFuse] Fusion034  label="removeToCreteHoleForPlugHousing004"
  Placement = pos=(-42,19,36) rot=(0,1,0;1.5708rad)
  Shapes = -> [Cylinder014,Cylinder015]
FEATURE [Part::Cut] Cut008  label="top004"
  Base = -> Cut004
  Placement = pos=(-1,0,0) rot=(0,0,1;0rad)
  Tool = -> Fusion034
FEATURE [Part::Box] Box005  label="Cube005"
  AttacherType = Attacher::AttachEngine3D
  Height = 28
  Length = 3
  Placement = pos=(110.7,19,22) rot=(0,0,1;0rad)
  Width = 15.7
FEATURE [Part::Cylinder] Cylinder016
  Angle = 360
  AttacherType = Attacher::AttachEngine3D
  Height = 10
  Placement = pos=(0,0,36.15) rot=(0,0,1;0rad)
  Radius = 4
FEATURE [Part::Cylinder] Cylinder017
  Angle = 360
  AttacherType = Attacher::AttachEngine3D
  Height = 20
  Placement = pos=(0,0,36.15) rot=(0,0,1;0rad)
  Radius = 10.3
FEATURE [Part::MultiFuse] Fusion035  label="removeToCreteHoleForPlugHousing005"
  Placement = pos=(70,19,36) rot=(0,1,0;1.5708rad)
  Shapes = -> [Cylinder017,Cylinder016]
FEATURE [Part::Cut] Cut009  label="plugHousingTab001"
  Base = -> Box005
  Placement = pos=(-107.4,-14,0) rot=(0,0,1;0rad)
  Tool = -> Fusion035
FEATURE [Part::Box] Box006  label="Cube006"
  AttacherType = Attacher::AttachEngine3D
  Height = 28
  Length = 3
  Placement = pos=(110.7,19,22) rot=(0,0,1;0rad)
  Width = 15.7
FEATURE [Part::Cylinder] Cylinder018
  Angle = 360
  AttacherType = Attacher::AttachEngine3D
  Height = 10
  Placement = pos=(0,0,36.15) rot=(0,0,1;0rad)
  Radius = 4
FEATURE [Part::Cylinder] Cylinder019
  Angle = 360
  AttacherType = Attacher::AttachEngine3D
  Height = 20
  Placement = pos=(0,0,36.15) rot=(0,0,1;0rad)
  Radius = 10.3
FEATURE [Part::MultiFuse] Fusion036  label="removeToCreteHoleForPlugHousing006"
  Placement = pos=(70,19,36) rot=(0,1,0;1.5708rad)
  Shapes = -> [Cylinder019,Cylinder018]
FEATURE [Part::Cut] Cut010  label="plugHousingTab002"
  Base = -> Box006
  Placement = pos=(-107.4,-14,0) rot=(0,0,1;0rad)
  Tool = -> Fusion036
FEATURE [Part::MultiFuse] Fusion037
  Placement = pos=(9.6,23,0) rot=(0,0,1;3.14159rad)
  Shapes = -> [Cut009,Cut010]
FEATURE [Part::Box] Box  label="Cube"
  AttacherType = Attacher::AttachEngine3D
  Height = 10
  Length = 3
  Placement = pos=(3.3,4,12) rot=(0,0,1;0rad)
  Width = 10
FEATURE [Part::Fillet] Fillet004
  Base = -> Fusion028
  Edges = 1 edges r=2: [Edge25]
FEATURE [Part::Fillet] Fillet005  label="plugHousing046"
  Base = -> Fillet004
  Edges = 1 edges r=2: [Edge8]
FEATURE [Part::Fillet] Fillet006
  Base = -> Box
  Edges = 1 edges r=2: [Edge11]
FEATURE [Part::Box] Box007  label="Cube007"
  AttacherType = Attacher::AttachEngine3D
  Height = 10
  Length = 3
  Placement = pos=(3.3,4,50) rot=(0,0,1;0rad)
  Width = 10
FEATURE [Part::Fillet] Fillet007
  Base = -> Box007
  Edges = 1 edges r=2: [Edge12]
FEATURE [Part::Box] Box008  label="Cube008"
  AttacherType = Attacher::AttachEngine3D
  Height = 28
  Length = 4
  Placement = pos=(5,0,22) rot=(0,0,1;0rad)
  Width = 10
FEATURE [Part::Fillet] Fillet008
  Base = -> Box008
  Edges = 1 edges r=1: [Edge7]
FEATURE [Part::Fillet] Fillet009
  Base = -> Fillet008
  Edges = 1 edges r=2: [Edge5]
FEATURE [Part::Fillet] Fillet010
  Base = -> Fillet009
  Edges = 1 edges r=2: [Edge2]
FEATURE [Sketcher::SketchObject] Sketch009  label="topSketch003"
  FullyConstrained = true
  sketch-geometry (4):
    g0: LineSegment StartX=16.8446 StartY=31.512 StartZ=0 EndX=16.3251 EndY=34.4666 EndZ=0
    g1: ArcOfCircle CenterX=19 CenterY=19.2524 CenterZ=0 NormalX=0 NormalY=0 NormalZ=1 AngleXU=0 Radius=15.4476 StartAngle=1.74483 EndAngle=2.72717
    g2: ArcOfCircle CenterX=19 CenterY=19.2524 CenterZ=0 NormalX=0 NormalY=0 NormalZ=1 AngleXU=0 Radius=12.4476 StartAngle=1.74483 EndAngle=2.73189
    g3: LineSegment StartX=4.86004 StartY=25.4725 StartZ=0 EndX=7.58253 EndY=24.2107 EndZ=0
  constraints (7):
    c: Block(g0)
    c: Coincident(g1,g0)
    c: Coincident(g2,g0)
    c: Coincident(g3,g1)
    c: Coincident(g3,g2)
    c: Block(g1)
    c: Block(g2)
FEATURE [Part::Extrusion] Extrude008
  Base = -> Sketch009
  Dir = (0,0,1)
  DirMode = 2
  FaceMakerClass = Part::FaceMakerBullseye
  LengthFwd = 10
  LengthRev = 0
  Placement = pos=(0,0,31) rot=(0,0,1;0rad)
  Solid = true
  Symmetric = false
FEATURE [Part::Cylinder] Cylinder020
  Angle = 360
  AttacherType = Attacher::AttachEngine3D
  Height = 20
  Placement = pos=(0,0,36.15) rot=(0,0,1;0rad)
  Radius = 8.2
FEATURE [Part::Cylinder] Cylinder021
  Angle = 360
  AttacherType = Attacher::AttachEngine3D
  Height = 10
  Placement = pos=(0,0,36.15) rot=(0,0,1;0rad)
  Radius = 4
FEATURE [Part::MultiFuse] Fusion038  label="removeToCreteHoleForPlugHousing007"
  Placement = pos=(-42,19,36) rot=(0,1,0;1.5708rad)
  Shapes = -> [Cylinder020,Cylinder021]
FEATURE [Part::Cut] Cut011
  Base = -> Extrude008
  Tool = -> Fusion038
FEATURE [Part::Fillet] Fillet011
  Base = -> Cut011
  Edges = 1 edges r=2: [Edge1]
FEATURE [Part::Fillet] Fillet012
  Base = -> Fillet011
  Edges = 1 edges r=2.5: [Edge1]
FEATURE [Part::Fillet] Fillet013
  Base = -> Fillet012
  Edges = 1 edges r=2.5: [Edge2]
FEATURE [Part::Box] Box010  label="Cube010"
  AttacherType = Attacher::AttachEngine3D
  Height = 16
  Length = 8
  Placement = pos=(12.7,31.52,28) rot=(0,0,1;0rad)
  Width = 4
FEATURE [Sketcher::SketchObject] Sketch010  label="topSketch004"
  FullyConstrained = true
  sketch-geometry (4):
    g0: LineSegment StartX=16.8446 StartY=31.512 StartZ=0 EndX=16.3251 EndY=34.4666 EndZ=0
    g1: ArcOfCircle CenterX=19 CenterY=19.2524 CenterZ=0 NormalX=0 NormalY=0 NormalZ=1 AngleXU=0 Radius=15.4476 StartAngle=1.74483 EndAngle=2.72717
    g2: ArcOfCircle CenterX=19 CenterY=19.2524 CenterZ=0 NormalX=0 NormalY=0 NormalZ=1 AngleXU=0 Radius=12.4476 StartAngle=1.74483 EndAngle=2.73189
    g3: LineSegment StartX=4.86004 StartY=25.4725 StartZ=0 EndX=7.58253 EndY=24.2107 EndZ=0
  constraints (7):
    c: Block(g0)
    c: Coincident(g1,g0)
    c: Coincident(g2,g0)
    c: Coincident(g3,g1)
    c: Coincident(g3,g2)
    c: Block(g1)
    c: Block(g2)
FEATURE [Part::Cylinder] Cylinder022
  Angle = 360
  AttacherType = Attacher::AttachEngine3D
  Height = 10
  Placement = pos=(0,0,36.15) rot=(0,0,1;0rad)
  Radius = 4
FEATURE [Sketcher::SketchObject] Sketch011  label="topSketch005"
  FullyConstrained = true
  sketch-geometry (4):
    g0: LineSegment StartX=16.8446 StartY=31.512 StartZ=0 EndX=16.3251 EndY=34.4666 EndZ=0
    g1: ArcOfCircle CenterX=19 CenterY=19.2524 CenterZ=0 NormalX=0 NormalY=0 NormalZ=1 AngleXU=0 Radius=15.4476 StartAngle=1.74483 EndAngle=2.72717
    g2: ArcOfCircle CenterX=19 CenterY=19.2524 CenterZ=0 NormalX=0 NormalY=0 NormalZ=1 AngleXU=0 Radius=12.4476 StartAngle=1.74483 EndAngle=2.73189
    g3: LineSegment StartX=4.86004 StartY=25.4725 StartZ=0 EndX=7.58253 EndY=24.2107 EndZ=0
  constraints (7):
    c: Block(g0)
    c: Coincident(g1,g0)
    c: Coincident(g2,g0)
    c: Coincident(g3,g1)
    c: Coincident(g3,g2)
    c: Block(g1)
    c: Block(g2)
FEATURE [Part::Extrusion] Extrude010
  Base = -> Sketch011
  Dir = (0,0,1)
  DirMode = 2
  FaceMakerClass = Part::FaceMakerBullseye
  LengthFwd = 10.6
  LengthRev = 0
  Placement = pos=(0,0,31) rot=(0,0,1;0rad)
  Solid = true
  Symmetric = false
FEATURE [Part::Cylinder] Cylinder023
  Angle = 360
  AttacherType = Attacher::AttachEngine3D
  Height = 20
  Placement = pos=(0,0,36.15) rot=(0,0,1;0rad)
  Radius = 8.2
FEATURE [Part::MultiFuse] Fusion039  label="removeToCreteHoleForPlugHousing008"
  Placement = pos=(-42,19,36) rot=(0,1,0;1.5708rad)
  Shapes = -> [Cylinder023,Cylinder022]
FEATURE [Part::Cut] Cut012
  Base = -> Extrude010
  Placement = pos=(0,0,-0.3) rot=(0,0,1;0rad)
  Tool = -> Fusion039
FEATURE [Part::Cut] Cut013
  Base = -> Box010
  Tool = -> Cut012
FEATURE [Part::Fillet] Fillet014
  Base = -> Cut013
  Edges = 1 edges r=0.7: [Edge13]
FEATURE [Part::Fillet] Fillet015
  Base = -> Fillet014
  Edges = 1 edges r=0.7: [Edge13]
FEATURE [Part::Fillet] Fillet016
  Base = -> Fillet015
  Edges = 1 edges r=0.7: [Edge16]
FEATURE [Part::Fillet] Fillet017
  Base = -> Fillet016
  Edges = 1 edges r=0.7: [Edge11]
FEATURE [Part::Fillet] Fillet018
  Base = -> Fillet017
  Edges = 1 edges r=0.7: [Edge10]
FEATURE [Part::Fillet] Fillet019
  Base = -> Fillet018
  Edges = 1 edges r=1.2: [Edge5]
FEATURE [Part::Fillet] Fillet020
  Base = -> Fillet019
  Edges = 1 edges r=1.2: [Edge12]
FEATURE [Part::Fillet] Fillet021
  Base = -> Fillet020
  Edges = 1 edges r=2: [Edge1]
  Placement = pos=(0.3,0,0) rot=(0,0,1;0rad)
FEATURE [Part::MultiFuse] Fusion040  label="top005"
  Shapes = -> [Cut008,Fillet021]
FEATURE [Part::MultiFuse] Fusion041  label="wireHolder"
  Shapes = -> [Fusion033,Fillet013]
FEATURE [Part::MultiFuse] Fusion042
  Shapes = -> [Fillet007,Fusion041]
FEATURE [Part::MultiFuse] Fusion043  label="wireHolder001"
  Shapes = -> [Fusion042,Fillet010]
FEATURE [Part::MultiFuse] Fusion044  label="wireHolder002"
  Shapes = -> [Fillet006,Fusion037,Fusion043]
FEATURE [Part::Feature] Face026
  shape: bbox 11 x 6 x 2e-07 mm, 1 faces, 0 solids (baked)
FEATURE [Part::Revolution] Revolve026
  Angle = 360
  Axis = (0,1,0)
  Base = (0,0,0)
  FaceMakerClass = Part::FaceMakerBullseye
  Placement = pos=(30.3,-1,19.7) rot=(0,0,1;0rad)
  Solid = false
  Source = -> Face026
  Symmetric = false
FEATURE [Sketcher::SketchObject] Sketch013  label="topSketch006"
  FullyConstrained = true
  sketch-geometry (13):
    g0: LineSegment StartX=117 StartY=19 StartZ=0 EndX=117 EndY=38 EndZ=0
    g1: ArcOfCircle CenterX=98 CenterY=19 CenterZ=0 NormalX=0 NormalY=0 NormalZ=1 AngleXU=0 Radius=19 StartAngle=5.7297 EndAngle=6.28319
    g2: LineSegment StartX=0 StartY=3 StartZ=0 EndX=0 EndY=19 EndZ=0
    g3: LineSegment StartX=19 StartY=38 StartZ=0 EndX=117 EndY=38 EndZ=0
    g4: ArcOfCircle CenterX=19 CenterY=19 CenterZ=0 NormalX=0 NormalY=0 NormalZ=1 AngleXU=0 Radius=19 StartAngle=1.5708 EndAngle=3.14159
    g5: ArcOfCircle CenterX=19 CenterY=19 CenterZ=0 NormalX=0 NormalY=0 NormalZ=1 AngleXU=0 Radius=16 StartAngle=1.5708 EndAngle=3.14159
    g6: ArcOfCircle CenterX=98 CenterY=19 CenterZ=0 NormalX=0 NormalY=0 NormalZ=1 AngleXU=0 Radius=16 StartAngle=5.60905 EndAngle=6.28319
    g7: LineSegment StartX=114 StartY=19 StartZ=0 EndX=114 EndY=35 EndZ=0
    g8: LineSegment StartX=110.5 StartY=9.01251 StartZ=0 EndX=114.163 EndY=9.01251 EndZ=0
    g9: LineSegment StartX=114 StartY=35 StartZ=0 EndX=19 EndY=35 EndZ=0
    g10: LineSegment StartX=0 StartY=3 StartZ=0 EndX=0 EndY=0 EndZ=0
    g11: LineSegment StartX=3 StartY=0 StartZ=0 EndX=0 EndY=0 EndZ=0
    g12: LineSegment StartX=3 StartY=19 StartZ=0 EndX=3 EndY=0 EndZ=0
  constraints (33):
    c: Vertical(g0)
    c: Distance(g0) = 19
    c: Block(g0)
    c: Coincident(g1,g0)
    c: Block(g1)
    c: Vertical(g2)
    c: Block(g2)
    c: Coincident(g3,g0)
    c: Horizontal(g3)
    c: Distance(g3) = 98
    c: Coincident(g4,g3)
    c: Coincident(g4,g2)
    c: Block(g4)
    c: Coincident(g5,g4)
    c: Coincident(g6,g1)
    c: Block(g6)
    c: Block(g5)
    c: Coincident(g7,g6)
    c: Vertical(g7)
    c: Coincident(g8,g6)
    c: Coincident(g8,g1)
    c: Coincident(g9,g7)
    c: Coincident(g9,g5)
    c: Horizontal(g9)
    c: Tangent(g9,g5)
    c: Coincident(g10,g2)
    c: Distance(g10) = 3
    c: Vertical(g10)
    c: Coincident(g11,g10)
    c: Horizontal(g11)
    c: Coincident(g12,g5)
    c: Coincident(g12,g11)
    c: Vertical(g12)
FEATURE [Part::Extrusion] Extrude011  label="top006"
  Base = -> Sketch013
  Dir = (0,0,1)
  DirMode = 2
  FaceMakerClass = Part::FaceMakerBullseye
  LengthFwd = 72
  LengthRev = 0
  Solid = true
  Symmetric = false
FEATURE [Sketcher::SketchObject] Sketch014
  FullyConstrained = true
  MapMode = 3
  Placement = pos=(0,0,0) rot=(1,0,0;1.5708rad)
  Support = -> [Extrude011]
  sketch-geometry (8):
    g0: Circle CenterX=80.351 CenterY=-67.6202 CenterZ=0 NormalX=0 NormalY=0 NormalZ=1 AngleXU=0 Radius=2
    g1: Circle CenterX=80.351 CenterY=-67.6202 CenterZ=0 NormalX=0 NormalY=0 NormalZ=1 AngleXU=0 Radius=3
    g2: Circle CenterX=80.351 CenterY=-4.92017 CenterZ=0 NormalX=0 NormalY=0 NormalZ=1 AngleXU=0 Radius=2
    g3: Circle CenterX=80.351 CenterY=-4.92017 CenterZ=0 NormalX=0 NormalY=0 NormalZ=1 AngleXU=0 Radius=3
    g4: Circle CenterX=23.851 CenterY=-4.92017 CenterZ=0 NormalX=0 NormalY=0 NormalZ=1 AngleXU=0 Radius=2
    g5: Circle CenterX=23.851 CenterY=-4.92017 CenterZ=0 NormalX=0 NormalY=0 NormalZ=1 AngleXU=0 Radius=3
    g6: Circle CenterX=23.851 CenterY=-67.6202 CenterZ=0 NormalX=0 NormalY=0 NormalZ=1 AngleXU=0 Radius=2
    g7: Circle CenterX=23.851 CenterY=-67.6202 CenterZ=0 NormalX=0 NormalY=0 NormalZ=1 AngleXU=0 Radius=3
  constraints (8):
    c: Block(g3)
    c: Block(g2)
    c: Block(g1)
    c: Block(g0)
    c: Block(g6)
    c: Block(g7)
    c: Block(g4)
    c: Block(g5)
FEATURE [Part::Feature] Face027
  shape: bbox 11 x 6 x 2e-07 mm, 1 faces, 0 solids (baked)
FEATURE [Part::Revolution] Revolve027
  Angle = 360
  Axis = (0,1,0)
  Base = (0,0,0)
  FaceMakerClass = Part::FaceMakerBullseye
  Placement = pos=(30.3,-1,51.7) rot=(0,0,1;0rad)
  Solid = false
  Source = -> Face027
  Symmetric = false
FEATURE [Part::Feature] Face028
  shape: bbox 11 x 6 x 2e-07 mm, 1 faces, 0 solids (baked)
FEATURE [Part::Revolution] Revolve028
  Angle = 360
  Axis = (0,1,0)
  Base = (0,0,0)
  FaceMakerClass = Part::FaceMakerBullseye
  Placement = pos=(62.3,-1,19.7) rot=(0,0,1;0rad)
  Solid = false
  Source = -> Face028
  Symmetric = false
FEATURE [Part::Feature] Face029
  shape: bbox 11 x 6 x 2e-07 mm, 1 faces, 0 solids (baked)
FEATURE [Part::Revolution] Revolve029
  Angle = 360
  Axis = (0,1,0)
  Base = (0,0,0)
  FaceMakerClass = Part::FaceMakerBullseye
  Placement = pos=(62.3,-1,51.7) rot=(0,0,1;0rad)
  Solid = false
  Source = -> Face029
  Symmetric = false
FEATURE [Part::Feature] Wire
  shape: bbox 11 x 5.2 x 2e-07 mm, 0 faces, 0 solids (baked)
FEATURE [Part::Revolution] Revolve030
  Angle = 360
  Axis = (0,1,0)
  Base = (0,0,0)
  FaceMakerClass = Part::FaceMakerBullseye
  Placement = pos=(30.3,38,19.7) rot=(0,0,1;0rad)
  Solid = true
  Source = -> Wire
  Symmetric = false
FEATURE [Part::Feature] Wire001
  shape: bbox 11 x 5.2 x 2e-07 mm, 0 faces, 0 solids (baked)
FEATURE [Part::Revolution] Revolve031
  Angle = 360
  Axis = (0,1,0)
  Base = (0,0,0)
  FaceMakerClass = Part::FaceMakerBullseye
  Placement = pos=(30.3,38,51.7) rot=(0,0,1;0rad)
  Solid = true
  Source = -> Wire001
  Symmetric = false
FEATURE [Part::Feature] Wire002
  shape: bbox 11 x 5.2 x 2e-07 mm, 0 faces, 0 solids (baked)
FEATURE [Part::Revolution] Revolve032
  Angle = 360
  Axis = (0,1,0)
  Base = (0,0,0)
  FaceMakerClass = Part::FaceMakerBullseye
  Placement = pos=(62.3,38,51.7) rot=(0,0,1;0rad)
  Solid = true
  Source = -> Wire002
  Symmetric = false
FEATURE [Part::Feature] Wire003
  shape: bbox 11 x 5.2 x 2e-07 mm, 0 faces, 0 solids (baked)
FEATURE [Part::Revolution] Revolve033
  Angle = 360
  Axis = (0,1,0)
  Base = (0,0,0)
  FaceMakerClass = Part::FaceMakerBullseye
  Placement = pos=(62.3,38,19.7) rot=(0,0,1;0rad)
  Solid = true
  Source = -> Wire003
  Symmetric = false
FEATURE [Part::MultiFuse] Fusion045  label="altRandScrewHousing"
  Shapes = -> [Revolve029,Revolve027,Revolve028,Revolve026]
FEATURE [Part::MultiFuse] Fusion046  label="fanScrewHousing"
  Shapes = -> [Revolve033,Revolve032,Revolve031,Revolve030]
FEATURE [Sketcher::SketchObject] Sketch015
  FullyConstrained = true
  sketch-geometry (17):
    g0: Circle CenterX=-3.5 CenterY=23.5 CenterZ=0 NormalX=0 NormalY=0 NormalZ=1 AngleXU=0 Radius=1
    g1: Circle CenterX=-1 CenterY=15.25 CenterZ=0 NormalX=0 NormalY=0 NormalZ=1 AngleXU=0 Radius=1
    g2: Circle CenterX=-3.5 CenterY=7 CenterZ=0 NormalX=0 NormalY=0 NormalZ=1 AngleXU=0 Radius=1
    g3: BSplineCurve PolesCount=3 KnotsCount=2 Degree=2 IsPeriodic=0
    g4: GeomPoint X=-3.5 Y=23.5 Z=0
    g5: GeomPoint X=-3.5 Y=7 Z=0
    g6: Circle CenterX=-4.8 CenterY=30.5 CenterZ=0 NormalX=0 NormalY=0 NormalZ=1 AngleXU=0 Radius=1
    g7: Circle CenterX=-3.5 CenterY=30.5 CenterZ=0 NormalX=0 NormalY=0 NormalZ=1 AngleXU=0 Radius=1
    g8: Circle CenterX=-3.5 CenterY=29.2 CenterZ=0 NormalX=0 NormalY=0 NormalZ=1 AngleXU=0 Radius=1
    g9: BSplineCurve PolesCount=3 KnotsCount=2 Degree=2 IsPeriodic=0
    g10: GeomPoint X=-4.8 Y=30.5 Z=0
    g11: GeomPoint X=-3.5 Y=29.2 Z=0
    g12: LineSegment StartX=-3.5 StartY=29.2 StartZ=0 EndX=-3.5 EndY=23.5 EndZ=0
    g13: LineSegment StartX=-4.8 StartY=30.5 StartZ=0 EndX=0 EndY=30.5 EndZ=0
    g14: LineSegment StartX=-3.5 StartY=0.3 StartZ=0 EndX=0 EndY=0.3 EndZ=0
    g15: LineSegment StartX=-3.5 StartY=0.3 StartZ=0 EndX=-3.5 EndY=7 EndZ=0
    g16: LineSegment StartX=0 StartY=0.3 StartZ=0 EndX=0 EndY=30.5 EndZ=0
  constraints (33):
    c: Weight(g0) = 1
    c: Equal(g0,g1)
    c: Equal(g0,g2)
    c: InternalAlignment(g0,g3)
    c: InternalAlignment(g1,g3)
    c: InternalAlignment(g2,g3)
    c: InternalAlignment(g4,g3)
    c: InternalAlignment(g5,g3)
    c: Block(g3)
    c: Weight(g6) = 1
    c: Equal(g6,g7)
    c: Equal(g6,g8)
    c: InternalAlignment(g6,g9)
    c: InternalAlignment(g7,g9)
    c: InternalAlignment(g8,g9)
    c: InternalAlignment(g10,g9)
    c: InternalAlignment(g11,g9)
    c: Block(g9)
    c: Coincident(g12,g9)
    c: Coincident(g12,g3)
    c: Vertical(g12)
    c: Coincident(g13,g9)
    c: Horizontal(g13)
    c: Distance(g13) = 4.8
    c: Horizontal(g14)
    c: Block(g14)
    c: Coincident(g15,g14)
    c: Coincident(g15,g3)
    c: Vertical(g15)
    c: Coincident(g16,g14)
    c: Coincident(g16,g13)
    c: Vertical(g16)
    c: Tangent(g16,g1)
FEATURE [Sketcher::SketchObject] Sketch016
  FullyConstrained = true
  sketch-geometry (16):
    g0: Circle CenterX=-3.5 CenterY=23.5 CenterZ=0 NormalX=0 NormalY=0 NormalZ=1 AngleXU=0 Radius=1
    g1: Circle CenterX=-1 CenterY=15.25 CenterZ=0 NormalX=0 NormalY=0 NormalZ=1 AngleXU=0 Radius=1
    g2: Circle CenterX=-3.5 CenterY=7 CenterZ=0 NormalX=0 NormalY=0 NormalZ=1 AngleXU=0 Radius=1
    g3: BSplineCurve PolesCount=3 KnotsCount=2 Degree=2 IsPeriodic=0
    g4: GeomPoint X=-3.5 Y=23.5 Z=0
    g5: GeomPoint X=-3.5 Y=7 Z=0
    g6: LineSegment StartX=-3.5 StartY=28.2 StartZ=0 EndX=-3.5 EndY=23.5 EndZ=0
    g7: LineSegment StartX=0 StartY=29.5 StartZ=0 EndX=0 EndY=30 EndZ=0
    g8: LineSegment StartX=-3.5 StartY=28.2 StartZ=0 EndX=-3.5 EndY=30 EndZ=0
    g9: LineSegment StartX=0 StartY=30 StartZ=0 EndX=0 EndY=30.5 EndZ=0
    g10: LineSegment StartX=0 StartY=30.5 StartZ=0 EndX=-3.5 EndY=30.5 EndZ=0
    g11: LineSegment StartX=-3.5 StartY=30.5 StartZ=0 EndX=-3.5 EndY=30 EndZ=0
    g12: LineSegment StartX=0 StartY=29.5 StartZ=0 EndX=0 EndY=5 EndZ=0
    g13: LineSegment StartX=-3.5 StartY=0.3 StartZ=0 EndX=-3.5 EndY=7 EndZ=0
    g14: LineSegment StartX=-3.5 StartY=0.3 StartZ=0 EndX=0 EndY=0.3 EndZ=0
    g15: LineSegment StartX=0 StartY=5 StartZ=0 EndX=0 EndY=0.3 EndZ=0
  constraints (39):
    c: Weight(g0) = 1
    c: Equal(g0,g1)
    c: Equal(g0,g2)
    c: InternalAlignment(g0,g3)
    c: InternalAlignment(g1,g3)
    c: InternalAlignment(g2,g3)
    c: InternalAlignment(g4,g3)
    c: InternalAlignment(g5,g3)
    c: Block(g3)
    c: Coincident(g6,g3)
    c: Vertical(g6)
    c: Vertical(g7)
    c: Distance(g7) = 0.5
    c: Coincident(g8,g6)
    c: Vertical(g8)
    c: Block(g6)
    c: Block(g7)
    c: Vertical(g9)
    c: Equal(g7,g9) = 0.5
    c: Block(g9)
    c: Coincident(g9,g7)
    c: Horizontal(g10)
    c: Coincident(g10,g9)
    c: Coincident(g11,g10)
    c: Coincident(g11,g8)
    c: Vertical(g11)
    c: Block(g11)
    c: Coincident(g12,g7)
    c: Vertical(g12)
    c: Coincident(g13,g3)
    c: Vertical(g13)
    c: Distance(g13) = 6.7
    c: Coincident(g14,g13)
    c: Horizontal(g14)
    c: Block(g14)
    c: Coincident(g15,g12)
    c: Coincident(g15,g14)
    c: Vertical(g15)
    c: Block(g15)
FEATURE [Sketcher::SketchObject] Sketch017
  FullyConstrained = true
  sketch-geometry (11):
    g0: LineSegment StartX=-3.5 StartY=1e-16 StartZ=0 EndX=-1.6 EndY=1e-16 EndZ=0
    g1: LineSegment StartX=-1.6 StartY=1e-16 StartZ=0 EndX=-1.6 EndY=1.5 EndZ=0
    g2: LineSegment StartX=-3.5 StartY=1.5 StartZ=0 EndX=-1.6 EndY=1.5 EndZ=0
    g3: LineSegment StartX=-3.5 StartY=1e-16 StartZ=0 EndX=-4.8 EndY=1e-16 EndZ=0
    g4: Circle CenterX=-3.5 CenterY=1.3 CenterZ=0 NormalX=0 NormalY=0 NormalZ=1 AngleXU=0 Radius=1
    g5: Circle CenterX=-3.5 CenterY=1e-16 CenterZ=0 NormalX=0 NormalY=0 NormalZ=1 AngleXU=0 Radius=1
    g6: Circle CenterX=-4.8 CenterY=1e-16 CenterZ=0 NormalX=0 NormalY=0 NormalZ=1 AngleXU=0 Radius=1
    g7: BSplineCurve PolesCount=3 KnotsCount=2 Degree=2 IsPeriodic=0
    g8: GeomPoint X=-3.5 Y=1.3 Z=0
    g9: GeomPoint X=-4.8 Y=1e-16 Z=0
    g10: LineSegment StartX=-3.5 StartY=1.3 StartZ=0 EndX=-3.5 EndY=1.5 EndZ=0
  constraints (24):
    c: Horizontal(g0)
    c: Distance(g0) = 1.9
    c: Block(g0)
    c: Coincident(g1,g0)
    c: Vertical(g1)
    c: Coincident(g2,g1)
    c: Horizontal(g2)
    c: Coincident(g3,g0)
    c: Horizontal(g3)
    c: Distance(g3) = 1.3
    c: Weight(g4) = 1
    c: Equal(g4,g5)
    c: Coincident(g5,g0)
    c: Equal(g4,g6)
    c: Coincident(g7,g3)
    c: InternalAlignment(g4,g7)
    c: InternalAlignment(g5,g7)
    c: InternalAlignment(g6,g7)
    c: InternalAlignment(g8,g7)
    c: InternalAlignment(g9,g7)
    c: Coincident(g10,g7)
    c: Coincident(g10,g2)
    c: Vertical(g10)
    c: Block(g10)
FEATURE [Part::Feature] Face035
  shape: bbox 3.2 x 1.5 x 2e-07 mm, 1 faces, 0 solids (baked)
FEATURE [Part::Revolution] Revolve039  label="backCaseScrewRetainer"
  Angle = 360
  Axis = (0,1,0)
  Base = (0,0,0)
  FaceMakerClass = Part::FaceMakerBullseye
  Placement = pos=(12.5,3,62) rot=(0,0,1;0rad)
  Solid = false
  Source = -> Face035
  Symmetric = false
FEATURE [Part::Feature] Face036
  shape: bbox 3.2 x 1.5 x 2e-07 mm, 1 faces, 0 solids (baked)
FEATURE [Part::Feature] Face039
  shape: bbox 4.8 x 30.2 x 2e-07 mm, 1 faces, 0 solids (baked)
FEATURE [Part::Revolution] Revolve043  label="frontCaseScrewPost002"
  Angle = 360
  Axis = (0,1,0)
  Base = (0,0,0)
  FaceMakerClass = Part::FaceMakerBullseye
  Placement = pos=(89.5,4.5,3.5) rot=(0,0,1;0rad)
  Solid = false
  Source = -> Face039
  Symmetric = false
FEATURE [Part::Feature] Face042
  shape: bbox 4.8 x 30.2 x 2e-07 mm, 1 faces, 0 solids (baked)
FEATURE [Part::Revolution] Revolve046  label="frontCaseScrewPost003"
  Angle = 360
  Axis = (0,1,0)
  Base = (0,0,0)
  FaceMakerClass = Part::FaceMakerBullseye
  Placement = pos=(89.5,4.5,68.5) rot=(0,0,1;0rad)
  Solid = false
  Source = -> Face042
  Symmetric = false
FEATURE [Part::Feature] Face043
  shape: bbox 3.2 x 1.5 x 2e-07 mm, 1 faces, 0 solids (baked)
FEATURE [Part::Revolution] Revolve047  label="frontCaseScrewRetainer002"
  Angle = 360
  Axis = (0,1,0)
  Base = (0,0,0)
  FaceMakerClass = Part::FaceMakerBullseye
  Placement = pos=(89.5,3,68.5) rot=(0,0,1;0rad)
  Solid = false
  Source = -> Face043
  Symmetric = false
FEATURE [Part::Feature] Face044
  shape: bbox 3.2 x 1.5 x 2e-07 mm, 1 faces, 0 solids (baked)
FEATURE [Part::Revolution] Revolve048  label="frontCaseScrewRetainer003"
  Angle = 360
  Axis = (0,1,0)
  Base = (0,0,0)
  FaceMakerClass = Part::FaceMakerBullseye
  Placement = pos=(89.5,3,3.5) rot=(0,0,1;0rad)
  Solid = false
  Source = -> Face044
  Symmetric = false
FEATURE [App::MeasureDistance] Distance002  label="Distance: 1.67 mm"
  Distance = 1.66921
  P1 = (99.2361,4.7524,71.7)
  P2 = (99.2347,6.42161,71.7)
FEATURE [Sketcher::SketchObject] Sketch018
  FullyConstrained = true
  sketch-geometry (7):
    g0: LineSegment StartX=0 StartY=0 StartZ=0 EndX=0 EndY=6 EndZ=0
    g1: Circle CenterX=0 CenterY=0 CenterZ=0 NormalX=0 NormalY=0 NormalZ=1 AngleXU=0 Radius=1
    g2: Circle CenterX=8 CenterY=6 CenterZ=0 NormalX=0 NormalY=0 NormalZ=1 AngleXU=0 Radius=1
    g3: BSplineCurve PolesCount=3 KnotsCount=2 Degree=2 IsPeriodic=0
    g4: GeomPoint X=0 Y=0 Z=0
    g5: GeomPoint X=8 Y=6 Z=0
    g6: LineSegment StartX=0 StartY=6 StartZ=0 EndX=8 EndY=6 EndZ=0
  constraints (14):
    c: Coincident(g0,g-1)
    c: Distance(g0) = 6
    c: Vertical(g0)
    c: Coincident(g3,g0)
    c: Weight(g1) = 1
    c: Equal(g1,g2)
    c: InternalAlignment(g1,g3)
    c: InternalAlignment(g2,g3)
    c: InternalAlignment(g4,g3)
    c: InternalAlignment(g5,g3)
    c: Block(g3)
    c: Coincident(g6,g0)
    c: Coincident(g6,g3)
    c: Horizontal(g6)
FEATURE [Part::Extrusion] Extrude012  label="caseScrewPillarBracket"
  Base = -> Sketch018
  Dir = (0,0,1)
  DirMode = 2
  FaceMakerClass = Part::FaceMakerBullseye
  LengthFwd = 2.4
  LengthRev = 0
  Placement = pos=(15.76,29,8.8) rot=(0,1,0;0rad)
  Solid = true
  Symmetric = false
FEATURE [Sketcher::SketchObject] Sketch019
  FullyConstrained = true
  sketch-geometry (7):
    g0: LineSegment StartX=0 StartY=0 StartZ=0 EndX=0 EndY=6 EndZ=0
    g1: Circle CenterX=0 CenterY=0 CenterZ=0 NormalX=0 NormalY=0 NormalZ=1 AngleXU=0 Radius=1
    g2: Circle CenterX=8 CenterY=6 CenterZ=0 NormalX=0 NormalY=0 NormalZ=1 AngleXU=0 Radius=1
    g3: BSplineCurve PolesCount=3 KnotsCount=2 Degree=2 IsPeriodic=0
    g4: GeomPoint X=0 Y=0 Z=0
    g5: GeomPoint X=8 Y=6 Z=0
    g6: LineSegment StartX=0 StartY=6 StartZ=0 EndX=8 EndY=6 EndZ=0
  constraints (14):
    c: Coincident(g0,g-1)
    c: Distance(g0) = 6
    c: Vertical(g0)
    c: Coincident(g3,g0)
    c: Weight(g1) = 1
    c: Equal(g1,g2)
    c: InternalAlignment(g1,g3)
    c: InternalAlignment(g2,g3)
    c: InternalAlignment(g4,g3)
    c: InternalAlignment(g5,g3)
    c: Block(g3)
    c: Coincident(g6,g0)
    c: Coincident(g6,g3)
    c: Horizontal(g6)
FEATURE [Part::Extrusion] Extrude013  label="caseScrewPillarBracket001"
  Base = -> Sketch019
  Dir = (0,0,1)
  DirMode = 2
  FaceMakerClass = Part::FaceMakerBullseye
  LengthFwd = 2.4
  LengthRev = 0
  Placement = pos=(15.76,29,60.8) rot=(0,0,1;0rad)
  Solid = true
  Symmetric = false
FEATURE [Sketcher::SketchObject] Sketch020
  FullyConstrained = true
  sketch-geometry (7):
    g0: LineSegment StartX=0 StartY=0 StartZ=0 EndX=0 EndY=6 EndZ=0
    g1: Circle CenterX=0 CenterY=0 CenterZ=0 NormalX=0 NormalY=0 NormalZ=1 AngleXU=0 Radius=1
    g2: Circle CenterX=8 CenterY=6 CenterZ=0 NormalX=0 NormalY=0 NormalZ=1 AngleXU=0 Radius=1
    g3: BSplineCurve PolesCount=3 KnotsCount=2 Degree=2 IsPeriodic=0
    g4: GeomPoint X=0 Y=0 Z=0
    g5: GeomPoint X=8 Y=6 Z=0
    g6: LineSegment StartX=0 StartY=6 StartZ=0 EndX=8 EndY=6 EndZ=0
  constraints (14):
    c: Coincident(g0,g-1)
    c: Distance(g0) = 6
    c: Vertical(g0)
    c: Coincident(g3,g0)
    c: Weight(g1) = 1
    c: Equal(g1,g2)
    c: InternalAlignment(g1,g3)
    c: InternalAlignment(g2,g3)
    c: InternalAlignment(g4,g3)
    c: InternalAlignment(g5,g3)
    c: Block(g3)
    c: Coincident(g6,g0)
    c: Coincident(g6,g3)
    c: Horizontal(g6)
FEATURE [Part::Extrusion] Extrude014  label="caseScrewPillarBracket002"
  Base = -> Sketch020
  Dir = (0,0,1)
  DirMode = 2
  FaceMakerClass = Part::FaceMakerBullseye
  LengthFwd = 2.4
  LengthRev = 0
  Placement = pos=(13.7,29,13.26) rot=(0,-1,0;1.5708rad)
  Solid = true
  Symmetric = false
FEATURE [Sketcher::SketchObject] Sketch021
  FullyConstrained = true
  sketch-geometry (7):
    g0: LineSegment StartX=0 StartY=0 StartZ=0 EndX=0 EndY=6 EndZ=0
    g1: Circle CenterX=0 CenterY=0 CenterZ=0 NormalX=0 NormalY=0 NormalZ=1 AngleXU=0 Radius=1
    g2: Circle CenterX=8 CenterY=6 CenterZ=0 NormalX=0 NormalY=0 NormalZ=1 AngleXU=0 Radius=1
    g3: BSplineCurve PolesCount=3 KnotsCount=2 Degree=2 IsPeriodic=0
    g4: GeomPoint X=0 Y=0 Z=0
    g5: GeomPoint X=8 Y=6 Z=0
    g6: LineSegment StartX=0 StartY=6 StartZ=0 EndX=8 EndY=6 EndZ=0
  constraints (14):
    c: Coincident(g0,g-1)
    c: Distance(g0) = 6
    c: Vertical(g0)
    c: Coincident(g3,g0)
    c: Weight(g1) = 1
    c: Equal(g1,g2)
    c: InternalAlignment(g1,g3)
    c: InternalAlignment(g2,g3)
    c: InternalAlignment(g4,g3)
    c: InternalAlignment(g5,g3)
    c: Block(g3)
    c: Coincident(g6,g0)
    c: Coincident(g6,g3)
    c: Horizontal(g6)
FEATURE [Part::Extrusion] Extrude015  label="caseScrewPillarBracket003"
  Base = -> Sketch021
  Dir = (0,0,1)
  DirMode = 2
  FaceMakerClass = Part::FaceMakerBullseye
  LengthFwd = 2.4
  LengthRev = 0
  Placement = pos=(11.3,29,58.74) rot=(0,1,0;1.5708rad)
  Solid = true
  Symmetric = false
FEATURE [Sketcher::SketchObject] Sketch022
  FullyConstrained = true
  sketch-geometry (7):
    g0: LineSegment StartX=0 StartY=0 StartZ=0 EndX=0 EndY=6 EndZ=0
    g1: Circle CenterX=0 CenterY=0 CenterZ=0 NormalX=0 NormalY=0 NormalZ=1 AngleXU=0 Radius=1
    g2: Circle CenterX=8 CenterY=6 CenterZ=0 NormalX=0 NormalY=0 NormalZ=1 AngleXU=0 Radius=1
    g3: BSplineCurve PolesCount=3 KnotsCount=2 Degree=2 IsPeriodic=0
    g4: GeomPoint X=0 Y=0 Z=0
    g5: GeomPoint X=8 Y=6 Z=0
    g6: LineSegment StartX=0 StartY=6 StartZ=0 EndX=8 EndY=6 EndZ=0
  constraints (14):
    c: Coincident(g0,g-1)
    c: Distance(g0) = 6
    c: Vertical(g0)
    c: Coincident(g3,g0)
    c: Weight(g1) = 1
    c: Equal(g1,g2)
    c: InternalAlignment(g1,g3)
    c: InternalAlignment(g2,g3)
    c: InternalAlignment(g4,g3)
    c: InternalAlignment(g5,g3)
    c: Block(g3)
    c: Coincident(g6,g0)
    c: Coincident(g6,g3)
    c: Horizontal(g6)
FEATURE [Part::Extrusion] Extrude016  label="caseScrewPillarBracket004"
  Base = -> Sketch022
  Dir = (0,0,1)
  DirMode = 2
  FaceMakerClass = Part::FaceMakerBullseye
  LengthFwd = 2.4
  LengthRev = 0
  Placement = pos=(88.3,29,65.23) rot=(0,1,0;1.5708rad)
  Solid = true
  Symmetric = false
FEATURE [Sketcher::SketchObject] Sketch023
  FullyConstrained = true
  sketch-geometry (7):
    g0: LineSegment StartX=0 StartY=0 StartZ=0 EndX=0 EndY=6 EndZ=0
    g1: Circle CenterX=0 CenterY=0 CenterZ=0 NormalX=0 NormalY=0 NormalZ=1 AngleXU=0 Radius=1
    g2: Circle CenterX=8 CenterY=6 CenterZ=0 NormalX=0 NormalY=0 NormalZ=1 AngleXU=0 Radius=1
    g3: BSplineCurve PolesCount=3 KnotsCount=2 Degree=2 IsPeriodic=0
    g4: GeomPoint X=0 Y=0 Z=0
    g5: GeomPoint X=8 Y=6 Z=0
    g6: LineSegment StartX=0 StartY=6 StartZ=0 EndX=8 EndY=6 EndZ=0
  constraints (14):
    c: Coincident(g0,g-1)
    c: Distance(g0) = 6
    c: Vertical(g0)
    c: Coincident(g3,g0)
    c: Weight(g1) = 1
    c: Equal(g1,g2)
    c: InternalAlignment(g1,g3)
    c: InternalAlignment(g2,g3)
    c: InternalAlignment(g4,g3)
    c: InternalAlignment(g5,g3)
    c: Block(g3)
    c: Coincident(g6,g0)
    c: Coincident(g6,g3)
    c: Horizontal(g6)
FEATURE [Part::Extrusion] Extrude017  label="caseScrewPillarBracket005"
  Base = -> Sketch023
  Dir = (0,0,1)
  DirMode = 2
  FaceMakerClass = Part::FaceMakerBullseye
  LengthFwd = 2.4
  LengthRev = 0
  Placement = pos=(90.7,29,6.77) rot=(0,-1,0;1.5708rad)
  Solid = true
  Symmetric = false
FEATURE [Sketcher::SketchObject] Sketch024
  FullyConstrained = true
  sketch-geometry (7):
    g0: LineSegment StartX=0 StartY=0 StartZ=0 EndX=0 EndY=6 EndZ=0
    g1: Circle CenterX=0 CenterY=0 CenterZ=0 NormalX=0 NormalY=0 NormalZ=1 AngleXU=0 Radius=1
    g2: Circle CenterX=8 CenterY=6 CenterZ=0 NormalX=0 NormalY=0 NormalZ=1 AngleXU=0 Radius=1
    g3: BSplineCurve PolesCount=3 KnotsCount=2 Degree=2 IsPeriodic=0
    g4: GeomPoint X=0 Y=0 Z=0
    g5: GeomPoint X=8 Y=6 Z=0
    g6: LineSegment StartX=0 StartY=6 StartZ=0 EndX=8 EndY=6 EndZ=0
  constraints (14):
    c: Coincident(g0,g-1)
    c: Distance(g0) = 6
    c: Vertical(g0)
    c: Coincident(g3,g0)
    c: Weight(g1) = 1
    c: Equal(g1,g2)
    c: InternalAlignment(g1,g3)
    c: InternalAlignment(g2,g3)
    c: InternalAlignment(g4,g3)
    c: InternalAlignment(g5,g3)
    c: Block(g3)
    c: Coincident(g6,g0)
    c: Coincident(g6,g3)
    c: Horizontal(g6)
FEATURE [Part::Extrusion] Extrude018  label="caseScrewPillarBracket006"
  Base = -> Sketch024
  Dir = (0,0,1)
  DirMode = 2
  FaceMakerClass = Part::FaceMakerBullseye
  LengthFwd = 2.4
  LengthRev = 0
  Placement = pos=(103.7,29,6.77) rot=(0,-1,0;1.5708rad)
  Solid = true
  Symmetric = false
FEATURE [Sketcher::SketchObject] Sketch025
  FullyConstrained = true
  sketch-geometry (7):
    g0: LineSegment StartX=0 StartY=0 StartZ=0 EndX=0 EndY=6 EndZ=0
    g1: Circle CenterX=0 CenterY=0 CenterZ=0 NormalX=0 NormalY=0 NormalZ=1 AngleXU=0 Radius=1
    g2: Circle CenterX=8 CenterY=6 CenterZ=0 NormalX=0 NormalY=0 NormalZ=1 AngleXU=0 Radius=1
    g3: BSplineCurve PolesCount=3 KnotsCount=2 Degree=2 IsPeriodic=0
    g4: GeomPoint X=0 Y=0 Z=0
    g5: GeomPoint X=8 Y=6 Z=0
    g6: LineSegment StartX=0 StartY=6 StartZ=0 EndX=8 EndY=6 EndZ=0
  constraints (14):
    c: Coincident(g0,g-1)
    c: Distance(g0) = 6
    c: Vertical(g0)
    c: Coincident(g3,g0)
    c: Weight(g1) = 1
    c: Equal(g1,g2)
    c: InternalAlignment(g1,g3)
    c: InternalAlignment(g2,g3)
    c: InternalAlignment(g4,g3)
    c: InternalAlignment(g5,g3)
    c: Block(g3)
    c: Coincident(g6,g0)
    c: Coincident(g6,g3)
    c: Horizontal(g6)
FEATURE [Part::Extrusion] Extrude019  label="caseScrewPillarBracket007"
  Base = -> Sketch025
  Dir = (0,0,1)
  DirMode = 2
  FaceMakerClass = Part::FaceMakerBullseye
  LengthFwd = 2.4
  LengthRev = 0
  Placement = pos=(101.3,29,65.23) rot=(0,1,0;1.5708rad)
  Solid = true
  Symmetric = false
FEATURE [Part::Box] Box011  label="frontCaseScrewPillarBracket"
  AttacherType = Attacher::AttachEngine3D
  Height = 2.4
  Length = 16
  Placement = pos=(87,28,2.3) rot=(0,0,1;0rad)
  Width = 7
FEATURE [Part::Box] Box012  label="frontCaseScrewPillarBracket001"
  AttacherType = Attacher::AttachEngine3D
  Height = 2.4
  Length = 16
  Placement = pos=(87,28,67.3) rot=(0,0,1;0rad)
  Width = 7
FEATURE [Sketcher::SketchObject] Sketch026
  FullyConstrained = true
  sketch-geometry (17):
    g0: Circle CenterX=-3.5 CenterY=23.5 CenterZ=0 NormalX=0 NormalY=0 NormalZ=1 AngleXU=0 Radius=1
    g1: Circle CenterX=-1 CenterY=15.25 CenterZ=0 NormalX=0 NormalY=0 NormalZ=1 AngleXU=0 Radius=1
    g2: Circle CenterX=-3.5 CenterY=7 CenterZ=0 NormalX=0 NormalY=0 NormalZ=1 AngleXU=0 Radius=1
    g3: BSplineCurve PolesCount=3 KnotsCount=2 Degree=2 IsPeriodic=0
    g4: GeomPoint X=-3.5 Y=23.5 Z=0
    g5: GeomPoint X=-3.5 Y=7 Z=0
    g6: Circle CenterX=-4.8 CenterY=30.5 CenterZ=0 NormalX=0 NormalY=0 NormalZ=1 AngleXU=0 Radius=1
    g7: Circle CenterX=-3.5 CenterY=30.5 CenterZ=0 NormalX=0 NormalY=0 NormalZ=1 AngleXU=0 Radius=1
    g8: Circle CenterX=-3.5 CenterY=29.2 CenterZ=0 NormalX=0 NormalY=0 NormalZ=1 AngleXU=0 Radius=1
    g9: BSplineCurve PolesCount=3 KnotsCount=2 Degree=2 IsPeriodic=0
    g10: GeomPoint X=-4.8 Y=30.5 Z=0
    g11: GeomPoint X=-3.5 Y=29.2 Z=0
    g12: LineSegment StartX=-3.5 StartY=29.2 StartZ=0 EndX=-3.5 EndY=23.5 EndZ=0
    g13: LineSegment StartX=-4.8 StartY=30.5 StartZ=0 EndX=0 EndY=30.5 EndZ=0
    g14: LineSegment StartX=-3.5 StartY=5 StartZ=0 EndX=-3.5 EndY=7 EndZ=0
    g15: LineSegment StartX=0 StartY=5 StartZ=0 EndX=0 EndY=30.5 EndZ=0
    g16: LineSegment StartX=-3.5 StartY=5 StartZ=0 EndX=0 EndY=5 EndZ=0
  constraints (33):
    c: Weight(g0) = 1
    c: Equal(g0,g1)
    c: Equal(g0,g2)
    c: InternalAlignment(g0,g3)
    c: InternalAlignment(g1,g3)
    c: InternalAlignment(g2,g3)
    c: InternalAlignment(g4,g3)
    c: InternalAlignment(g5,g3)
    c: Block(g3)
    c: Weight(g6) = 1
    c: Equal(g6,g7)
    c: Equal(g6,g8)
    c: InternalAlignment(g6,g9)
    c: InternalAlignment(g7,g9)
    c: InternalAlignment(g8,g9)
    c: InternalAlignment(g10,g9)
    c: InternalAlignment(g11,g9)
    c: Block(g9)
    c: Coincident(g12,g9)
    c: Coincident(g12,g3)
    c: Vertical(g12)
    c: Coincident(g13,g9)
    c: Horizontal(g13)
    c: Distance(g13) = 4.8
    c: Coincident(g14,g3)
    c: Vertical(g14)
    c: Coincident(g15,g13)
    c: Vertical(g15)
    c: Tangent(g15,g1)
    c: Distance(g14) = 2
    c: Coincident(g16,g14)
    c: Horizontal(g16)
    c: Coincident(g15,g16)
FEATURE [Part::Feature] Face050
  shape: bbox 4.8 x 25.5 x 2e-07 mm, 1 faces, 0 solids (baked)
FEATURE [Part::Revolution] Revolve054  label="moreFrontCaseScrewPost001"
  Angle = 360
  Axis = (0,1,0)
  Base = (0,0,0)
  FaceMakerClass = Part::FaceMakerBullseye
  Placement = pos=(102.5,4.5,3.5) rot=(0,0,1;0rad)
  Solid = false
  Source = -> Face050
  Symmetric = false
FEATURE [Part::Feature] Face051
  shape: bbox 4.8 x 25.5 x 2e-07 mm, 1 faces, 0 solids (baked)
FEATURE [Part::Revolution] Revolve055  label="moreFrontCaseScrewPost002"
  Angle = 360
  Axis = (0,1,0)
  Base = (0,0,0)
  FaceMakerClass = Part::FaceMakerBullseye
  Placement = pos=(102.5,4.5,68.5) rot=(0,0,1;0rad)
  Solid = false
  Source = -> Face051
  Symmetric = false
FEATURE [Sketcher::SketchObject] Sketch027
  FullyConstrained = true
  sketch-geometry (10):
    g0: LineSegment StartX=-1.6 StartY=4.7 StartZ=0 EndX=-1.6 EndY=1.7 EndZ=0
    g1: LineSegment StartX=-3.5 StartY=4.7 StartZ=0 EndX=-1.6 EndY=4.7 EndZ=0
    g2: LineSegment StartX=-1.6 StartY=1.7 StartZ=0 EndX=-1.6 EndY=1.5 EndZ=0
    g3: LineSegment StartX=-1.6 StartY=1.5 StartZ=0 EndX=-5.2 EndY=1.5 EndZ=0
    g4: Circle CenterX=-3.5 CenterY=4.7 CenterZ=0 NormalX=0 NormalY=0 NormalZ=1 AngleXU=0 Radius=1
    g5: Circle CenterX=-3.59627 CenterY=2.99743 CenterZ=0 NormalX=0 NormalY=0 NormalZ=1 AngleXU=0 Radius=1
    g6: Circle CenterX=-5.2 CenterY=1.5 CenterZ=0 NormalX=0 NormalY=0 NormalZ=1 AngleXU=0 Radius=1
    g7: BSplineCurve PolesCount=3 KnotsCount=2 Degree=2 IsPeriodic=0
    g8: GeomPoint X=-3.5 Y=4.7 Z=0
    g9: GeomPoint X=-5.2 Y=1.5 Z=0
  constraints (23):
    c: Vertical(g0)
    c: Distance(g0) = 3
    c: Coincident(g1,g0)
    c: Horizontal(g1)
    c: Block(g0)
    c: Block(g1)
    c: Coincident(g2,g0)
    c: Vertical(g2)
    c: Distance(g2) = 0.2
    c: Coincident(g3,g2)
    c: Horizontal(g3)
    c: Block(g3)
    c: Coincident(g7,g1)
    c: Weight(g4) = 1
    c: Equal(g4,g5)
    c: Equal(g4,g6)
    c: Coincident(g7,g3)
    c: InternalAlignment(g4,g7)
    c: InternalAlignment(g5,g7)
    c: InternalAlignment(g6,g7)
    c: InternalAlignment(g8,g7)
    c: InternalAlignment(g9,g7)
    c: Block(g7)
FEATURE [Sketcher::SketchObject] Sketch028
  FullyConstrained = true
  sketch-geometry (18):
    g0: LineSegment StartX=0 StartY=3e-16 StartZ=0 EndX=0 EndY=1.7 EndZ=0
    g1: LineSegment StartX=-3.5 StartY=0 StartZ=0 EndX=-3.5 EndY=0.9 EndZ=0
    g2: Circle CenterX=-2.7 CenterY=1.7 CenterZ=0 NormalX=0 NormalY=0 NormalZ=1 AngleXU=0 Radius=1
    g3: Circle CenterX=-3.5 CenterY=1.7 CenterZ=0 NormalX=0 NormalY=0 NormalZ=1 AngleXU=0 Radius=1
    g4: Circle CenterX=-3.5 CenterY=0.9 CenterZ=0 NormalX=0 NormalY=0 NormalZ=1 AngleXU=0 Radius=1
    g5: BSplineCurve PolesCount=3 KnotsCount=2 Degree=2 IsPeriodic=0
    g6: GeomPoint X=-2.7 Y=1.7 Z=0
    g7: GeomPoint X=-3.5 Y=0.9 Z=0
    g8: LineSegment StartX=-3.5 StartY=0 StartZ=0 EndX=-3.5 EndY=-7 EndZ=0
    g9: LineSegment StartX=0 StartY=3e-16 StartZ=0 EndX=0 EndY=-7 EndZ=0
    g10: LineSegment StartX=-3.5 StartY=-7 StartZ=0 EndX=0 EndY=-7 EndZ=0
    g11: LineSegment StartX=-2.7 StartY=1.7 StartZ=0 EndX=-1.6 EndY=1.7 EndZ=0
    g12: LineSegment StartX=0 StartY=1.7 StartZ=0 EndX=0 EndY=4.5 EndZ=0
    g13: LineSegment StartX=0 StartY=4.5 StartZ=0 EndX=0 EndY=10.8 EndZ=0
    g14: LineSegment StartX=0 StartY=10.8 StartZ=0 EndX=-2 EndY=10.8 EndZ=0
    g15: LineSegment StartX=-1.6 StartY=4.7 StartZ=0 EndX=-1.6 EndY=1.7 EndZ=0
    g16: LineSegment StartX=-1.6 StartY=4.7 StartZ=0 EndX=-2 EndY=4.7 EndZ=0
    g17: LineSegment StartX=-2 StartY=4.7 StartZ=0 EndX=-2 EndY=10.8 EndZ=0
  constraints (44):
    c: Vertical(g0)
    c: Vertical(g1)
    c: Distance(g1) = 0.9
    c: Block(g0)
    c: Distance(g0) = 1.7
    c: Weight(g2) = 1
    c: Equal(g2,g3)
    c: Equal(g2,g4)
    c: Coincident(g5,g1)
    c: InternalAlignment(g2,g5)
    c: InternalAlignment(g3,g5)
    c: InternalAlignment(g4,g5)
    c: InternalAlignment(g6,g5)
    c: InternalAlignment(g7,g5)
    c: Block(g5)
    c: Coincident(g8,g1)
    c: Vertical(g8)
    c: Distance(g8) = 7
    c: Vertical(g9)
    c: Equal(g8,g9) = 7
    c: Coincident(g9,g0)
    c: Coincident(g10,g8)
    c: Coincident(g10,g9)
    c: Horizontal(g10)
    c: Coincident(g11,g5)
    c: Horizontal(g11)
    c: Coincident(g12,g0)
    c: Vertical(g12)
    c: Distance(g12) = 2.8
    c: Coincident(g13,g12)
    c: Vertical(g13)
    c: Distance(g13) = 6.3
    c: Coincident(g14,g13)
    c: Horizontal(g14)
    c: Distance(g14) = 2
    c: Vertical(g15)
    c: Distance(g15) = 3
    c: Block(g11)
    c: Coincident(g15,g11)
    c: Coincident(g16,g15)
    c: Horizontal(g16)
    c: Coincident(g17,g16)
    c: Coincident(g17,g14)
    c: Vertical(g17)
FEATURE [Part::Revolution] Revolve040  label="backCaseScrewRetainer001"
  Angle = 360
  Axis = (0,1,0)
  Base = (0,0,0)
  FaceMakerClass = Part::FaceMakerBullseye
  Placement = pos=(12.5,3,10) rot=(0,0,1;0rad)
  Solid = false
  Source = -> Face036
  Symmetric = false
FEATURE [Part::Feature] Face055
  shape: bbox 3.5 x 30.2 x 2e-07 mm, 1 faces, 0 solids (baked)
FEATURE [Part::Revolution] Revolve059  label="backCaseScrewPost"
  Angle = 360
  Axis = (0,1,0)
  Base = (0,0,0)
  FaceMakerClass = Part::FaceMakerBullseye
  Placement = pos=(12.5,4.5,10) rot=(0,0,1;0rad)
  Solid = false
  Source = -> Face055
  Symmetric = false
FEATURE [Part::Feature] Face056
  shape: bbox 3.5 x 30.2 x 2e-07 mm, 1 faces, 0 solids (baked)
FEATURE [Part::Revolution] Revolve060  label="backCaseScrewPost001"
  Angle = 360
  Axis = (0,1,0)
  Base = (0,0,0)
  FaceMakerClass = Part::FaceMakerBullseye
  Placement = pos=(12.5,4.5,62) rot=(0,0,1;0rad)
  Solid = false
  Source = -> Face056
  Symmetric = false
FEATURE [Part::Feature] Face057
  shape: bbox 3.5 x 17.8 x 2e-07 mm, 1 faces, 0 solids (baked)
FEATURE [Part::Revolution] Revolve061  label="removeToCreateScrewAndThreadedInsertHole"
  Angle = 360
  Axis = (0,1,0)
  Base = (0,0,0)
  FaceMakerClass = Part::FaceMakerBullseye
  Placement = pos=(12.5,0,10) rot=(0,0,1;0rad)
  Solid = false
  Source = -> Face057
  Symmetric = false
FEATURE [Part::Feature] Face058
  shape: bbox 3.5 x 17.8 x 2e-07 mm, 1 faces, 0 solids (baked)
FEATURE [Part::Revolution] Revolve062  label="removeToCreateScrewAndThreadedInsertHole001"
  Angle = 360
  Axis = (0,1,0)
  Base = (0,0,0)
  FaceMakerClass = Part::FaceMakerBullseye
  Placement = pos=(12.5,0,62) rot=(0,0,1;0rad)
  Solid = false
  Source = -> Face058
  Symmetric = false
FEATURE [Part::Feature] Face059
  shape: bbox 3.5 x 17.8 x 2e-07 mm, 1 faces, 0 solids (baked)
FEATURE [Part::Revolution] Revolve063  label="removeToCreateScrewAndThreadedInsertHole002"
  Angle = 360
  Axis = (0,1,0)
  Base = (0,0,0)
  FaceMakerClass = Part::FaceMakerBullseye
  Placement = pos=(89.5,0,68.5) rot=(0,0,1;0rad)
  Solid = false
  Source = -> Face059
  Symmetric = false
FEATURE [Part::Feature] Face060
  shape: bbox 3.5 x 17.8 x 2e-07 mm, 1 faces, 0 solids (baked)
FEATURE [Part::Revolution] Revolve064  label="removeToCreateScrewAndThreadedInsertHole003"
  Angle = 360
  Axis = (0,1,0)
  Base = (0,0,0)
  FaceMakerClass = Part::FaceMakerBullseye
  Placement = pos=(89.5,0,3.5) rot=(0,0,1;0rad)
  Solid = false
  Source = -> Face060
  Symmetric = false
FEATURE [Part::Feature] Face061
  shape: bbox 3.5 x 17.8 x 2e-07 mm, 1 faces, 0 solids (baked)
FEATURE [Part::Revolution] Revolve065  label="removeToCreateScrewAndThreadedInsertHole004"
  Angle = 360
  Axis = (0,1,0)
  Base = (0,0,0)
  FaceMakerClass = Part::FaceMakerBullseye
  Placement = pos=(102.5,4.7,3.5) rot=(0,0,1;0rad)
  Solid = false
  Source = -> Face061
  Symmetric = false
FEATURE [Part::Feature] Face062
  shape: bbox 3.5 x 17.8 x 2e-07 mm, 1 faces, 0 solids (baked)
FEATURE [Part::Revolution] Revolve066  label="removeToCreateScrewAndThreadedInsertHole005"
  Angle = 360
  Axis = (0,1,0)
  Base = (0,0,0)
  FaceMakerClass = Part::FaceMakerBullseye
  Placement = pos=(102.5,4.7,68.5) rot=(0,0,1;0rad)
  Solid = false
  Source = -> Face062
  Symmetric = false
FEATURE [Part::MultiFuse] Fusion047  label="makeHoles"
  Shapes = -> [Revolve066,Revolve065,Revolve064,Revolve063,Revolve062,Revolve061]
FEATURE [Part::Feature] Face063
  shape: bbox 3.6 x 3.2 x 2e-07 mm, 1 faces, 0 solids (baked)
FEATURE [Part::Revolution] Revolve067  label="moreFrontCaseScrewRetainer002"
  Angle = 360
  Axis = (0,1,0)
  Base = (0,0,0)
  FaceMakerClass = Part::FaceMakerBullseye
  Placement = pos=(102.5,4.5,68.5) rot=(0,0,1;0rad)
  Solid = false
  Source = -> Face063
  Symmetric = false
FEATURE [Part::Feature] Face064
  shape: bbox 3.6 x 3.2 x 2e-07 mm, 1 faces, 0 solids (baked)
FEATURE [Part::Revolution] Revolve068  label="moreFrontCaseScrewRetainer003"
  Angle = 360
  Axis = (0,1,0)
  Base = (0,0,0)
  FaceMakerClass = Part::FaceMakerBullseye
  Placement = pos=(102.5,4.5,3.5) rot=(0,0,1;0rad)
  Solid = false
  Source = -> Face064
  Symmetric = false
FEATURE [Part::Feature] Face065
  shape: bbox 3.5 x 17.8 x 2e-07 mm, 1 faces, 0 solids (baked)
FEATURE [Part::Revolution] Revolve069  label="removeToCreateScrewAndThreadedInsertHole006"
  Angle = 360
  Axis = (0,1,0)
  Base = (0,0,0)
  FaceMakerClass = Part::FaceMakerBullseye
  Placement = pos=(12.5,0,10) rot=(0,0,1;0rad)
  Solid = false
  Source = -> Face065
  Symmetric = false
FEATURE [Part::Feature] Face066
  shape: bbox 3.5 x 17.8 x 2e-07 mm, 1 faces, 0 solids (baked)
FEATURE [Part::Revolution] Revolve070  label="removeToCreateScrewAndThreadedInsertHole007"
  Angle = 360
  Axis = (0,1,0)
  Base = (0,0,0)
  FaceMakerClass = Part::FaceMakerBullseye
  Placement = pos=(12.5,0,62) rot=(0,0,1;0rad)
  Solid = false
  Source = -> Face066
  Symmetric = false
FEATURE [Part::Feature] Face067
  shape: bbox 3.5 x 17.8 x 2e-07 mm, 1 faces, 0 solids (baked)
FEATURE [Part::Revolution] Revolve071  label="removeToCreateScrewAndThreadedInsertHole008"
  Angle = 360
  Axis = (0,1,0)
  Base = (0,0,0)
  FaceMakerClass = Part::FaceMakerBullseye
  Placement = pos=(89.5,0,68.5) rot=(0,0,1;0rad)
  Solid = false
  Source = -> Face067
  Symmetric = false
FEATURE [Part::Feature] Face068
  shape: bbox 3.5 x 17.8 x 2e-07 mm, 1 faces, 0 solids (baked)
FEATURE [Part::Revolution] Revolve072  label="removeToCreateScrewAndThreadedInsertHole009"
  Angle = 360
  Axis = (0,1,0)
  Base = (0,0,0)
  FaceMakerClass = Part::FaceMakerBullseye
  Placement = pos=(89.5,0,3.5) rot=(0,0,1;0rad)
  Solid = false
  Source = -> Face068
  Symmetric = false
FEATURE [Part::Feature] Face069
  shape: bbox 3.5 x 17.8 x 2e-07 mm, 1 faces, 0 solids (baked)
FEATURE [Part::Feature] Face070
  shape: bbox 3.5 x 17.8 x 2e-07 mm, 1 faces, 0 solids (baked)
FEATURE [Part::Revolution] Revolve073  label="removeToCreateScrewAndThreadedInsertHole010"
  Angle = 360
  Axis = (0,1,0)
  Base = (0,0,0)
  FaceMakerClass = Part::FaceMakerBullseye
  Placement = pos=(102.5,4.7,3.5) rot=(0,0,1;0rad)
  Solid = false
  Source = -> Face069
  Symmetric = false
FEATURE [Part::Revolution] Revolve074  label="removeToCreateScrewAndThreadedInsertHole011"
  Angle = 360
  Axis = (0,1,0)
  Base = (0,0,0)
  FaceMakerClass = Part::FaceMakerBullseye
  Placement = pos=(102.5,4.7,68.5) rot=(0,0,1;0rad)
  Solid = false
  Source = -> Face070
  Symmetric = false
FEATURE [Part::MultiFuse] Fusion048  label="makeHoles001"
  Shapes = -> [Revolve074,Revolve073,Revolve072,Revolve071,Revolve070,Revolve069]
FEATURE [Part::MultiFuse] Fusion049  label="caseScrewRetainers"
  Shapes = -> [Revolve067,Revolve068,Revolve048,Revolve047,Revolve039,Revolve040]
FEATURE [Part::Cut] Cut015  label="caseScrewRetainers001"
  Base = -> Fusion049
  Tool = -> Fusion048
FEATURE [Part::MultiFuse] Fusion050  label="casePillars"
  Shapes = -> [Revolve055,Revolve054,Revolve043,Revolve046,Revolve059,Revolve060]
FEATURE [Part::Feature] Face071 .. Face076  x6 (patterned run collapsed; names and placements below)
  shape: bbox 3.5 x 17.8 x 2e-07 mm, 1 faces, 0 solids (baked)
FEATURE [Part::Revolution] Revolve075  label="removeToCreateScrewAndThreadedInsertHole012"
  Angle = 360
  Axis = (0,1,0)
  Base = (0,0,0)
  FaceMakerClass = Part::FaceMakerBullseye
  Placement = pos=(12.5,0,10) rot=(0,0,1;0rad)
  Solid = false
  Source = -> Face071
  Symmetric = false
FEATURE [Part::Revolution] Revolve076  label="removeToCreateScrewAndThreadedInsertHole013"
  Angle = 360
  Axis = (0,1,0)
  Base = (0,0,0)
  FaceMakerClass = Part::FaceMakerBullseye
  Placement = pos=(12.5,0,62) rot=(0,0,1;0rad)
  Solid = false
  Source = -> Face072
  Symmetric = false
FEATURE [Part::Revolution] Revolve077  label="removeToCreateScrewAndThreadedInsertHole014"
  Angle = 360
  Axis = (0,1,0)
  Base = (0,0,0)
  FaceMakerClass = Part::FaceMakerBullseye
  Placement = pos=(89.5,0,68.5) rot=(0,0,1;0rad)
  Solid = false
  Source = -> Face073
  Symmetric = false
FEATURE [Part::Revolution] Revolve078  label="removeToCreateScrewAndThreadedInsertHole015"
  Angle = 360
  Axis = (0,1,0)
  Base = (0,0,0)
  FaceMakerClass = Part::FaceMakerBullseye
  Placement = pos=(89.5,0,3.5) rot=(0,0,1;0rad)
  Solid = false
  Source = -> Face074
  Symmetric = false
FEATURE [Part::Revolution] Revolve079  label="removeToCreateScrewAndThreadedInsertHole016"
  Angle = 360
  Axis = (0,1,0)
  Base = (0,0,0)
  FaceMakerClass = Part::FaceMakerBullseye
  Placement = pos=(102.5,4.7,3.5) rot=(0,0,1;0rad)
  Solid = false
  Source = -> Face075
  Symmetric = false
FEATURE [Part::Revolution] Revolve080  label="removeToCreateScrewAndThreadedInsertHole017"
  Angle = 360
  Axis = (0,1,0)
  Base = (0,0,0)
  FaceMakerClass = Part::FaceMakerBullseye
  Placement = pos=(102.5,4.7,68.5) rot=(0,0,1;0rad)
  Solid = false
  Source = -> Face076
  Symmetric = false
FEATURE [Part::MultiFuse] Fusion051  label="makeHoles002"
  Shapes = -> [Revolve080,Revolve079,Revolve078,Revolve077,Revolve076,Revolve075]
FEATURE [Part::Cut] Cut016  label="caesPillars"
  Base = -> Fusion050
  Tool = -> Fusion051
FEATURE [Part::Revolution] Revolve009  label="plugHousing016"
  Angle = 360
  Axis = (0,1,0)
  Base = (0,0,0)
  FaceMakerClass = Part::FaceMakerBullseye
  Placement = pos=(0,0,36.15) rot=(0,0,1;0rad)
  Solid = false
  Source = -> Face012
  Symmetric = false
FEATURE [Part::MultiFuse] Fusion014  label="plugHousing023"
  Placement = pos=(0,0,0) rot=(0,0,1;1.5708rad)
  Shapes = -> [Revolve011,Revolve009]
FEATURE [Part::Revolution] Revolve010  label="plugHousing017"
  Angle = 360
  Axis = (0,1,0)
  Base = (0,0,0)
  FaceMakerClass = Part::FaceMakerBullseye
  Placement = pos=(0,0,36.15) rot=(0,0,1;0rad)
  Solid = false
  Source = -> Face014
  Symmetric = false
FEATURE [Part::MultiFuse] Fusion015  label="plugHousing024"
  Placement = pos=(0,0,0) rot=(0,0,1;1.5708rad)
  Shapes = -> [Revolve010,Revolve015]
FEATURE [Part::Revolution] Revolve014  label="plugHousing026"
  Angle = 360
  Axis = (0,1,0)
  Base = (0,0,0)
  FaceMakerClass = Part::FaceMakerBullseye
  Placement = pos=(0,0,36.15) rot=(0,0,1;0rad)
  Solid = false
  Source = -> Face011
  Symmetric = false
FEATURE [Part::Revolution] Revolve013  label="plugHousing025"
  Angle = 360
  Axis = (0,1,0)
  Base = (0,0,0)
  FaceMakerClass = Part::FaceMakerBullseye
  Placement = pos=(0,0,36.15) rot=(0,0,1;0rad)
  Solid = false
  Source = -> Face015
  Symmetric = false
FEATURE [Part::MultiFuse] Fusion016  label="plugHousing028"
  Placement = pos=(0,19,0) rot=(0,0,1;3.14159rad)
  Shapes = -> [Fusion014,Fusion013]
FEATURE [Part::MultiFuse] Fusion011  label="plugHousing018"
  Placement = pos=(0,0,0) rot=(0,0,1;1.5708rad)
  Shapes = -> [Revolve014,Revolve013]
FEATURE [Part::MultiFuse] Fusion012  label="plugHousing019"
  Placement = pos=(0,19,0) rot=(0,0,1;3.14159rad)
  Shapes = -> [Fusion011,Fusion015]
FEATURE [Part::MultiFuse] Fusion017  label="plugHousing029"
  Placement = pos=(122.621,0,-0.15) rot=(0,0,1;0rad)
  Shapes = -> [Fusion016,Fusion012]
FEATURE [Part::MultiFuse] Fusion052  label="casePillarRetainers"
  Shapes = -> [Extrude012,Extrude013,Extrude014,Extrude015,Extrude016,Extrude017,Extrude018,Extrude019,Box011,Box012]
FEATURE [Part::Feature] Face077
  shape: bbox 3.5 x 17.8 x 2e-07 mm, 1 faces, 0 solids (baked)
FEATURE [Part::Revolution] Revolve081  label="removeToCreateScrewAndThreadedInsertHole018"
  Angle = 360
  Axis = (0,1,0)
  Base = (0,0,0)
  FaceMakerClass = Part::FaceMakerBullseye
  Placement = pos=(62.3,30.3,19.7) rot=(0,0,1;0rad)
  Solid = false
  Source = -> Face077
  Symmetric = false
FEATURE [Part::Feature] Face078
  shape: bbox 3.5 x 17.8 x 2e-07 mm, 1 faces, 0 solids (baked)
FEATURE [Part::Revolution] Revolve082  label="removeToCreateScrewAndThreadedInsertHole019"
  Angle = 360
  Axis = (0,1,0)
  Base = (0,0,0)
  FaceMakerClass = Part::FaceMakerBullseye
  Placement = pos=(62.3,30.3,51.7) rot=(0,0,1;0rad)
  Solid = false
  Source = -> Face078
  Symmetric = false
FEATURE [Part::Feature] Face079
  shape: bbox 3.5 x 17.8 x 2e-07 mm, 1 faces, 0 solids (baked)
FEATURE [Part::Revolution] Revolve083  label="removeToCreateScrewAndThreadedInsertHole020"
  Angle = 360
  Axis = (0,1,0)
  Base = (0,0,0)
  FaceMakerClass = Part::FaceMakerBullseye
  Placement = pos=(30.3,30.3,19.7) rot=(0,0,1;0rad)
  Solid = false
  Source = -> Face079
  Symmetric = false
FEATURE [Part::Feature] Face080
  shape: bbox 3.5 x 17.8 x 2e-07 mm, 1 faces, 0 solids (baked)
FEATURE [Part::Revolution] Revolve084  label="removeToCreateScrewAndThreadedInsertHole021"
  Angle = 360
  Axis = (0,1,0)
  Base = (0,0,0)
  FaceMakerClass = Part::FaceMakerBullseye
  Placement = pos=(30.3,30.3,51.7) rot=(0,0,1;0rad)
  Solid = false
  Source = -> Face080
  Symmetric = false
FEATURE [Part::MultiFuse] Fusion053  label="createThreadedInsertHolesForFan"
  Shapes = -> [Revolve081,Revolve082,Revolve083,Revolve084]
FEATURE [Part::Cut] Cut017  label="fanScrewHousing001"
  Base = -> Fusion046
  Tool = -> Fusion053
FEATURE [Part::Feature] Face081
  shape: bbox 3.5 x 17.8 x 2e-07 mm, 1 faces, 0 solids (baked)
FEATURE [Part::Revolution] Revolve085  label="removeToCreateScrewAndThreadedInsertHole022"
  Angle = 360
  Axis = (0,1,0)
  Base = (0,0,0)
  FaceMakerClass = Part::FaceMakerBullseye
  Placement = pos=(62.3,30.3,19.7) rot=(0,0,1;0rad)
  Solid = false
  Source = -> Face081
  Symmetric = false
FEATURE [Part::Feature] Face082
  shape: bbox 3.5 x 17.8 x 2e-07 mm, 1 faces, 0 solids (baked)
FEATURE [Part::Revolution] Revolve086  label="removeToCreateScrewAndThreadedInsertHole023"
  Angle = 360
  Axis = (0,1,0)
  Base = (0,0,0)
  FaceMakerClass = Part::FaceMakerBullseye
  Placement = pos=(62.3,30.3,51.7) rot=(0,0,1;0rad)
  Solid = false
  Source = -> Face082
  Symmetric = false
FEATURE [Part::Feature] Face083
  shape: bbox 3.5 x 17.8 x 2e-07 mm, 1 faces, 0 solids (baked)
FEATURE [Part::Revolution] Revolve087  label="removeToCreateScrewAndThreadedInsertHole024"
  Angle = 360
  Axis = (0,1,0)
  Base = (0,0,0)
  FaceMakerClass = Part::FaceMakerBullseye
  Placement = pos=(30.3,30.3,19.7) rot=(0,0,1;0rad)
  Solid = false
  Source = -> Face083
  Symmetric = false
FEATURE [Part::Feature] Face084
  shape: bbox 3.5 x 17.8 x 2e-07 mm, 1 faces, 0 solids (baked)
FEATURE [Part::Revolution] Revolve088  label="removeToCreateScrewAndThreadedInsertHole025"
  Angle = 360
  Axis = (0,1,0)
  Base = (0,0,0)
  FaceMakerClass = Part::FaceMakerBullseye
  Placement = pos=(30.3,30.3,51.7) rot=(0,0,1;0rad)
  Solid = false
  Source = -> Face084
  Symmetric = false
FEATURE [Part::MultiFuse] Fusion054  label="createThreadedInsertHolesForFan001"
  Shapes = -> [Revolve085,Revolve086,Revolve087,Revolve088]
FEATURE [Part::Cut] Cut018  label="top007"
  Base = -> Fusion040
  Tool = -> Fusion054
FEATURE [Sketcher::SketchObject] Sketch029
  FullyConstrained = false
  Placement = pos=(0,0,0) rot=(1,0,0;1.5708rad)
  sketch-geometry (24):
    g0: ArcOfCircle CenterX=-4 CenterY=-10.5 CenterZ=0 NormalX=0 NormalY=0 NormalZ=1 AngleXU=0 Radius=1.5 StartAngle=6e-16 EndAngle=3.14159
    g1: ArcOfCircle CenterX=-34.2 CenterY=-10.5 CenterZ=0 NormalX=0 NormalY=0 NormalZ=1 AngleXU=0 Radius=1.5 StartAngle=0 EndAngle=3.14159
    g2: ArcOfCircle CenterX=-34.2 CenterY=-27.7 CenterZ=0 NormalX=0 NormalY=0 NormalZ=1 AngleXU=0 Radius=1.5 StartAngle=3.14159 EndAngle=6.28319
    g3: ArcOfCircle CenterX=-4 CenterY=-27.7 CenterZ=0 NormalX=0 NormalY=0 NormalZ=1 AngleXU=0 Radius=1.5 StartAngle=3.1416 EndAngle=6.28319
    g4: ArcOfCircle CenterX=-10 CenterY=-4.3 CenterZ=0 NormalX=0 NormalY=0 NormalZ=1 AngleXU=0 Radius=1.5 StartAngle=2e-16 EndAngle=3.14159
    g5: ArcOfCircle CenterX=-16.1 CenterY=-1.8 CenterZ=0 NormalX=0 NormalY=0 NormalZ=1 AngleXU=0 Radius=1.5 StartAngle=5e-16 EndAngle=3.14159
    g6: ArcOfCircle CenterX=-22.1 CenterY=-1.8 CenterZ=0 NormalX=0 NormalY=0 NormalZ=1 AngleXU=0 Radius=1.5 StartAngle=5e-16 EndAngle=3.14159
    g7: ArcOfCircle CenterX=-28.2 CenterY=-4.3 CenterZ=0 NormalX=0 NormalY=0 NormalZ=1 AngleXU=0 Radius=1.5 StartAngle=2e-16 EndAngle=3.14159
    g8: ArcOfCircle CenterX=-10 CenterY=-33.9 CenterZ=0 NormalX=0 NormalY=0 NormalZ=1 AngleXU=0 Radius=1.5 StartAngle=3.14159 EndAngle=6.28319
    g9: ArcOfCircle CenterX=-16.1 CenterY=-36.4 CenterZ=0 NormalX=0 NormalY=0 NormalZ=1 AngleXU=0 Radius=1.5 StartAngle=3.14159 EndAngle=6.28319
    g10: ArcOfCircle CenterX=-22.1 CenterY=-36.4 CenterZ=0 NormalX=0 NormalY=0 NormalZ=1 AngleXU=0 Radius=1.5 StartAngle=3.14159 EndAngle=6.28319
    g11: ArcOfCircle CenterX=-28.2 CenterY=-33.9 CenterZ=0 NormalX=0 NormalY=0 NormalZ=1 AngleXU=0 Radius=1.5 StartAngle=3.14159 EndAngle=6.28319
    g12: LineSegment StartX=-35.7 StartY=-10.5 StartZ=0 EndX=-35.7 EndY=-27.7 EndZ=0
    g13: LineSegment StartX=-32.7 StartY=-10.5 StartZ=0 EndX=-32.7 EndY=-27.7 EndZ=0
    g14: LineSegment StartX=-29.7 StartY=-33.9 StartZ=0 EndX=-29.7 EndY=-4.3 EndZ=0
    g15: LineSegment StartX=-26.7 StartY=-33.9 StartZ=0 EndX=-26.7 EndY=-4.3 EndZ=0
    g16: LineSegment StartX=-2.5 StartY=-10.5 StartZ=0 EndX=-2.5 EndY=-27.7 EndZ=0
    g17: LineSegment StartX=-8.5 StartY=-4.3 StartZ=0 EndX=-8.5 EndY=-33.9 EndZ=0
    g18: LineSegment StartX=-5.5 StartY=-10.5 StartZ=0 EndX=-5.5 EndY=-27.7 EndZ=0
    g19: LineSegment StartX=-11.5 StartY=-4.3 StartZ=0 EndX=-11.5 EndY=-33.9 EndZ=0
    g20: LineSegment StartX=-14.6 StartY=-1.8 StartZ=0 EndX=-14.6 EndY=-36.4 EndZ=0
    g21: LineSegment StartX=-17.6 StartY=-1.8 StartZ=0 EndX=-17.6 EndY=-36.4 EndZ=0
    g22: LineSegment StartX=-20.6 StartY=-36.4 StartZ=0 EndX=-20.6 EndY=-1.8 EndZ=0
    g23: LineSegment StartX=-23.6 StartY=-1.8 StartZ=0 EndX=-23.6 EndY=-36.4 EndZ=0
  constraints (48):
    c: Block(g0)
    c: Block(g1)
    c: Block(g2)
    c: Block(g3)
    c: Block(g4)
    c: Block(g5)
    c: Block(g6)
    c: Block(g7)
    c: Block(g8)
    c: Block(g9)
    c: Block(g10)
    c: Block(g11)
    c: Coincident(g12,g1)
    c: Coincident(g12,g2)
    c: Vertical(g12)
    c: Coincident(g13,g1)
    c: Coincident(g13,g2)
    c: Vertical(g13)
    c: Coincident(g14,g11)
    c: Coincident(g14,g7)
    c: Vertical(g14)
    c: Coincident(g15,g11)
    c: Coincident(g15,g7)
    c: Vertical(g15)
    c: Coincident(g16,g0)
    c: Coincident(g16,g3)
    c: Vertical(g16)
    c: Coincident(g17,g4)
    c: Coincident(g17,g8)
    c: Vertical(g17)
    c: Coincident(g18,g0)
    c: Coincident(g18,g3)
    c: Vertical(g18)
    c: Coincident(g19,g4)
    c: Coincident(g19,g8)
    c: Vertical(g19)
    c: Coincident(g20,g5)
    c: Coincident(g20,g9)
    c: Vertical(g20)
    c: Coincident(g21,g5)
    c: Coincident(g21,g9)
    c: Vertical(g21)
    c: Coincident(g22,g10)
    c: Coincident(g22,g6)
    c: Vertical(g22)
    c: Coincident(g23,g6)
    c: Coincident(g23,g10)
    c: Vertical(g23)
FEATURE [Part::Extrusion] Extrude020  label="removeToCreateFanGrillHoles"
  Base = -> Sketch029
  Dir = (0,-1,6e-16)
  DirMode = 2
  FaceMakerClass = Part::FaceMakerBullseye
  LengthFwd = 10
  LengthRev = 0
  Placement = pos=(65.4,44,54.82) rot=(0,0,1;0rad)
  Solid = true
  Symmetric = false
FEATURE [Part::MultiFuse] Fusion055  label="top008"
  Shapes = -> [Cut017,Cut018]
FEATURE [Part::Cut] Cut019  label="top009"
  Base = -> Fusion055
  Tool = -> Extrude020
FEATURE [App::MeasureDistance] Distance003  label="Distance: 71.95 mm"
  Distance = 71.9513
  P1 = (117,38,72)
  P2 = (117,38,0.0487319)
FEATURE [Sketcher::SketchObject] Sketch030
  FullyConstrained = true
  Placement = pos=(117,19,0) rot=(0.57735,0.57735,0.57735;2.0944rad)
  sketch-geometry (48):
    g0: LineSegment StartX=-49.19 StartY=69.25 StartZ=0 EndX=-49.19 EndY=66.25 EndZ=0
    g1: LineSegment StartX=-49.19 StartY=63.5 StartZ=0 EndX=-49.19 EndY=60.5 EndZ=0
    g2: LineSegment StartX=-49.19 StartY=57.75 StartZ=0 EndX=-49.19 EndY=54.75 EndZ=0
    g3: LineSegment StartX=-49.19 StartY=52 StartZ=0 EndX=-49.19 EndY=49 EndZ=0
    g4: LineSegment StartX=-49.19 StartY=46.25 StartZ=0 EndX=-49.19 EndY=43.25 EndZ=0
    g5: LineSegment StartX=-49.19 StartY=40.5 StartZ=0 EndX=-49.19 EndY=37.5 EndZ=0
    g6: LineSegment StartX=-49.19 StartY=34.5 StartZ=0 EndX=-49.19 EndY=31.5 EndZ=0
    g7: LineSegment StartX=-49.19 StartY=28.75 StartZ=0 EndX=-49.19 EndY=25.75 EndZ=0
    g8: LineSegment StartX=-49.19 StartY=23 StartZ=0 EndX=-49.19 EndY=20 EndZ=0
    g9: LineSegment StartX=-49.19 StartY=17.25 StartZ=0 EndX=-49.19 EndY=14.25 EndZ=0
    g10: LineSegment StartX=-49.19 StartY=11.5 StartZ=0 EndX=-49.19 EndY=8.5 EndZ=0
    g11: LineSegment StartX=-49.19 StartY=5.75 StartZ=0 EndX=-49.19 EndY=2.75 EndZ=0
    g12: ArcOfCircle CenterX=-1.5 CenterY=67.75 CenterZ=0 NormalX=0 NormalY=0 NormalZ=1 AngleXU=0 Radius=1.5 StartAngle=4.71239 EndAngle=7.85398
    g13: ArcOfCircle CenterX=-1.5 CenterY=62 CenterZ=0 NormalX=0 NormalY=0 NormalZ=1 AngleXU=0 Radius=1.5 StartAngle=4.71239 EndAngle=7.85398
    g14: ArcOfCircle CenterX=-1.5 CenterY=56.25 CenterZ=0 NormalX=0 NormalY=0 NormalZ=1 AngleXU=0 Radius=1.5 StartAngle=4.71239 EndAngle=7.85398
    g15: ArcOfCircle CenterX=-11.49 CenterY=50.5 CenterZ=0 NormalX=0 NormalY=0 NormalZ=1 AngleXU=0 Radius=1.5 StartAngle=4.71239 EndAngle=7.85398
    g16: ArcOfCircle CenterX=-16.28 CenterY=44.75 CenterZ=0 NormalX=0 NormalY=0 NormalZ=1 AngleXU=0 Radius=1.5 StartAngle=4.71239 EndAngle=7.85398
    g17: ArcOfCircle CenterX=-18.2337 CenterY=39 CenterZ=0 NormalX=0 NormalY=0 NormalZ=1 AngleXU=0 Radius=1.5 StartAngle=4.71485 EndAngle=7.85398
    g18: ArcOfCircle CenterX=-16.2837 CenterY=27.25 CenterZ=0 NormalX=0 NormalY=0 NormalZ=1 AngleXU=0 Radius=1.5 StartAngle=4.71485 EndAngle=7.85398
    g19: ArcOfCircle CenterX=-18.2337 CenterY=33 CenterZ=0 NormalX=0 NormalY=0 NormalZ=1 AngleXU=0 Radius=1.5 StartAngle=4.71485 EndAngle=7.85398
    g20: ArcOfCircle CenterX=-11.49 CenterY=21.5 CenterZ=0 NormalX=0 NormalY=0 NormalZ=1 AngleXU=0 Radius=1.5 StartAngle=4.71239 EndAngle=7.85398
    g21: ArcOfCircle CenterX=-1.5 CenterY=4.25 CenterZ=0 NormalX=0 NormalY=0 NormalZ=1 AngleXU=0 Radius=1.5 StartAngle=4.71239 EndAngle=7.85398
    g22: ArcOfCircle CenterX=-1.5 CenterY=10 CenterZ=0 NormalX=0 NormalY=0 NormalZ=1 AngleXU=0 Radius=1.5 StartAngle=4.71239 EndAngle=7.85398
    g23: ArcOfCircle CenterX=-1.5 CenterY=15.75 CenterZ=0 NormalX=0 NormalY=0 NormalZ=1 AngleXU=0 Radius=1.5 StartAngle=4.71239 EndAngle=7.85398
    g24: LineSegment StartX=-49.19 StartY=69.25 StartZ=0 EndX=-1.5 EndY=69.25 EndZ=0
    g25: LineSegment StartX=-49.19 StartY=66.25 StartZ=0 EndX=-1.5 EndY=66.25 EndZ=0
    g26: LineSegment StartX=-49.19 StartY=63.5 StartZ=0 EndX=-1.5 EndY=63.5 EndZ=0
    g27: LineSegment StartX=-49.19 StartY=60.5 StartZ=0 EndX=-1.5 EndY=60.5 EndZ=0
    g28: LineSegment StartX=-49.19 StartY=57.75 StartZ=0 EndX=-1.5 EndY=57.75 EndZ=0
    g29: LineSegment StartX=-49.19 StartY=54.75 StartZ=0 EndX=-1.5 EndY=54.75 EndZ=0
    g30: LineSegment StartX=-49.19 StartY=52 StartZ=0 EndX=-11.49 EndY=52 EndZ=0
    g31: LineSegment StartX=-49.19 StartY=49 StartZ=0 EndX=-11.49 EndY=49 EndZ=0
    g32: LineSegment StartX=-49.19 StartY=46.25 StartZ=0 EndX=-16.28 EndY=46.25 EndZ=0
    g33: LineSegment StartX=-49.19 StartY=43.25 StartZ=0 EndX=-16.28 EndY=43.25 EndZ=0
    g34: LineSegment StartX=-49.19 StartY=40.5 StartZ=0 EndX=-18.2337 EndY=40.5 EndZ=0
    g35: LineSegment StartX=-49.19 StartY=37.5 StartZ=0 EndX=-18.23 EndY=37.5 EndZ=0
    g36: LineSegment StartX=-49.19 StartY=34.5 StartZ=0 EndX=-18.2337 EndY=34.5 EndZ=0
    g37: LineSegment StartX=-49.19 StartY=31.5 StartZ=0 EndX=-18.23 EndY=31.5 EndZ=0
    g38: LineSegment StartX=-49.19 StartY=28.75 StartZ=0 EndX=-16.2837 EndY=28.75 EndZ=0
    g39: LineSegment StartX=-49.19 StartY=25.75 StartZ=0 EndX=-16.28 EndY=25.75 EndZ=0
    g40: LineSegment StartX=-49.19 StartY=23 StartZ=0 EndX=-11.49 EndY=23 EndZ=0
    g41: LineSegment StartX=-49.19 StartY=20 StartZ=0 EndX=-11.49 EndY=20 EndZ=0
    g42: LineSegment StartX=-49.19 StartY=17.25 StartZ=0 EndX=-1.5 EndY=17.25 EndZ=0
    g43: LineSegment StartX=-49.19 StartY=14.25 StartZ=0 EndX=-1.5 EndY=14.25 EndZ=0
    g44: LineSegment StartX=-49.19 StartY=11.5 StartZ=0 EndX=-1.5 EndY=11.5 EndZ=0
    g45: LineSegment StartX=-49.19 StartY=8.5 StartZ=0 EndX=-1.5 EndY=8.5 EndZ=0
    g46: LineSegment StartX=-49.19 StartY=5.75 StartZ=0 EndX=-1.5 EndY=5.75 EndZ=0
    g47: LineSegment StartX=-49.19 StartY=2.75 StartZ=0 EndX=-1.5 EndY=2.75 EndZ=0
  constraints (120):
    c: Vertical(g0)
    c: Distance(g0) = 3
    c: Block(g0)
    c: Vertical(g1)
    c: Distance(g1) = 3
    c: Vertical(g2)
    c: Equal(g0,g2) = 3
    c: Block(g2)
    c: Vertical(g3)
    c: Equal(g1,g3) = 3
    c: Vertical(g4)
    c: Equal(g0,g4) = 3
    c: Block(g4)
    c: Vertical(g5)
    c: Equal(g1,g5) = 3
    c: Vertical(g6)
    c: Equal(g0,g6) = 3
    c: Block(g6)
    c: Vertical(g7)
    c: Equal(g1,g7) = 3
    c: Vertical(g8)
    c: Equal(g0,g8) = 3
    c: Block(g8)
    c: Vertical(g9)
    c: Equal(g1,g9) = 3
    c: Vertical(g10)
    c: Equal(g0,g10) = 3
    c: Block(g10)
    c: Vertical(g11)
    c: Equal(g1,g11) = 3
    c: Block(g12)
    c: Block(g13)
    c: Block(g14)
    c: Block(g15)
    c: Block(g16)
    c: Block(g17)
    c: Block(g18)
    c: Block(g19)
    c: Block(g20)
    c: Block(g21)
    c: Block(g22)
    c: Block(g23)
    c: Block(g11)
    c: Block(g9)
    c: Block(g7)
    c: Block(g5)
    c: Block(g3)
    c: Block(g1)
    c: Coincident(g24,g0)
    c: Coincident(g24,g12)
    c: Horizontal(g24)
    c: Coincident(g25,g0)
    c: Coincident(g25,g12)
    c: Horizontal(g25)
    c: Coincident(g26,g1)
    c: Coincident(g26,g13)
    c: Horizontal(g26)
    c: Coincident(g27,g1)
    c: Coincident(g27,g13)
    c: Horizontal(g27)
    c: Coincident(g28,g2)
    c: Coincident(g28,g14)
    c: Horizontal(g28)
    c: Coincident(g29,g2)
    c: Coincident(g29,g14)
    c: Horizontal(g29)
    c: Coincident(g30,g3)
    c: Coincident(g30,g15)
    c: Horizontal(g30)
    c: Coincident(g31,g3)
    c: Coincident(g31,g15)
    c: Horizontal(g31)
    c: Coincident(g32,g4)
    c: Coincident(g32,g16)
    c: Horizontal(g32)
    c: Coincident(g33,g4)
    c: Coincident(g33,g16)
    c: Horizontal(g33)
    c: Coincident(g34,g5)
    c: Coincident(g34,g17)
    c: Horizontal(g34)
    c: Coincident(g35,g5)
    c: Coincident(g35,g17)
    c: Horizontal(g35)
    c: Coincident(g36,g6)
    c: Coincident(g36,g19)
    c: Horizontal(g36)
    c: Coincident(g37,g6)
    c: Coincident(g37,g19)
    c: Horizontal(g37)
    c: Coincident(g38,g7)
    c: Coincident(g38,g18)
    c: Horizontal(g38)
    c: Coincident(g39,g7)
    c: Coincident(g39,g18)
    c: Horizontal(g39)
    c: Coincident(g40,g8)
    c: Coincident(g40,g20)
    c: Horizontal(g40)
    c: Coincident(g41,g8)
    c: Coincident(g41,g20)
    c: Horizontal(g41)
    c: Coincident(g42,g9)
    c: Coincident(g42,g23)
    c: Horizontal(g42)
    c: Coincident(g43,g9)
    c: Coincident(g43,g23)
    c: Horizontal(g43)
    c: Coincident(g44,g10)
    c: Coincident(g44,g22)
    c: Horizontal(g44)
    c: Coincident(g45,g10)
    c: Coincident(g45,g22)
    c: Horizontal(g45)
    c: Coincident(g46,g11)
    c: Coincident(g46,g21)
    c: Horizontal(g46)
    c: Coincident(g47,g11)
    c: Coincident(g47,g21)
    c: Horizontal(g47)
FEATURE [Sketcher::SketchObject] Sketch031
  FullyConstrained = true
  Placement = pos=(117,19,0) rot=(0.57735,0.57735,0.57735;2.0944rad)
  sketch-geometry (24):
    g0: ArcOfCircle CenterX=-49.19 CenterY=67.75 CenterZ=0 NormalX=0 NormalY=0 NormalZ=1 AngleXU=0 Radius=1.5 StartAngle=1.5708 EndAngle=4.71239
    g1: ArcOfCircle CenterX=-49.19 CenterY=62 CenterZ=0 NormalX=0 NormalY=0 NormalZ=1 AngleXU=0 Radius=1.5 StartAngle=1.5708 EndAngle=4.71239
    g2: ArcOfCircle CenterX=-49.19 CenterY=56.25 CenterZ=0 NormalX=0 NormalY=0 NormalZ=1 AngleXU=0 Radius=1.5 StartAngle=1.5708 EndAngle=4.71239
    g3: ArcOfCircle CenterX=-49.19 CenterY=50.5 CenterZ=0 NormalX=0 NormalY=0 NormalZ=1 AngleXU=0 Radius=1.5 StartAngle=1.5708 EndAngle=4.71239
    g4: ArcOfCircle CenterX=-49.19 CenterY=44.75 CenterZ=0 NormalX=0 NormalY=0 NormalZ=1 AngleXU=0 Radius=1.5 StartAngle=1.5708 EndAngle=4.71239
    g5: ArcOfCircle CenterX=-49.19 CenterY=39 CenterZ=0 NormalX=0 NormalY=0 NormalZ=1 AngleXU=0 Radius=1.5 StartAngle=1.5708 EndAngle=4.71239
    g6: ArcOfCircle CenterX=-49.19 CenterY=33 CenterZ=0 NormalX=0 NormalY=0 NormalZ=1 AngleXU=0 Radius=1.5 StartAngle=1.5708 EndAngle=4.71239
    g7: ArcOfCircle CenterX=-49.19 CenterY=27.25 CenterZ=0 NormalX=0 NormalY=0 NormalZ=1 AngleXU=0 Radius=1.5 StartAngle=1.5708 EndAngle=4.71239
    g8: ArcOfCircle CenterX=-49.19 CenterY=21.5 CenterZ=0 NormalX=0 NormalY=0 NormalZ=1 AngleXU=0 Radius=1.5 StartAngle=1.5708 EndAngle=4.71239
    g9: ArcOfCircle CenterX=-49.19 CenterY=15.75 CenterZ=0 NormalX=0 NormalY=0 NormalZ=1 AngleXU=0 Radius=1.5 StartAngle=1.5708 EndAngle=4.71239
    g10: ArcOfCircle CenterX=-49.19 CenterY=10 CenterZ=0 NormalX=0 NormalY=0 NormalZ=1 AngleXU=0 Radius=1.5 StartAngle=1.5708 EndAngle=4.71239
    g11: ArcOfCircle CenterX=-49.19 CenterY=4.25 CenterZ=0 NormalX=0 NormalY=0 NormalZ=1 AngleXU=0 Radius=1.5 StartAngle=1.5708 EndAngle=4.71239
    g12: LineSegment StartX=-49.19 StartY=69.25 StartZ=0 EndX=-49.19 EndY=66.25 EndZ=0
    g13: LineSegment StartX=-49.19 StartY=63.5 StartZ=0 EndX=-49.19 EndY=60.5 EndZ=0
    g14: LineSegment StartX=-49.19 StartY=57.75 StartZ=0 EndX=-49.19 EndY=54.75 EndZ=0
    g15: LineSegment StartX=-49.19 StartY=52 StartZ=0 EndX=-49.19 EndY=49 EndZ=0
    g16: LineSegment StartX=-49.19 StartY=46.25 StartZ=0 EndX=-49.19 EndY=43.25 EndZ=0
    g17: LineSegment StartX=-49.19 StartY=40.5 StartZ=0 EndX=-49.19 EndY=37.5 EndZ=0
    g18: LineSegment StartX=-49.19 StartY=34.5 StartZ=0 EndX=-49.19 EndY=31.5 EndZ=0
    g19: LineSegment StartX=-49.19 StartY=28.75 StartZ=0 EndX=-49.19 EndY=25.75 EndZ=0
    g20: LineSegment StartX=-49.19 StartY=23 StartZ=0 EndX=-49.19 EndY=20 EndZ=0
    g21: LineSegment StartX=-49.19 StartY=17.25 StartZ=0 EndX=-49.19 EndY=14.25 EndZ=0
    g22: LineSegment StartX=-49.19 StartY=11.5 StartZ=0 EndX=-49.19 EndY=8.5 EndZ=0
    g23: LineSegment StartX=-49.19 StartY=5.75 StartZ=0 EndX=-49.19 EndY=2.75 EndZ=0
  constraints (48):
    c: Block(g0)
    c: Block(g1)
    c: Block(g2)
    c: Block(g3)
    c: Block(g4)
    c: Block(g5)
    c: Block(g6)
    c: Block(g7)
    c: Block(g8)
    c: Block(g9)
    c: Block(g10)
    c: Block(g11)
    c: Coincident(g12,g0)
    c: Coincident(g12,g0)
    c: Vertical(g12)
    c: Vertical(g13)
    c: Coincident(g13,g1)
    c: Vertical(g14)
    c: Coincident(g14,g2)
    c: Vertical(g15)
    c: Coincident(g15,g3)
    c: Vertical(g16)
    c: Coincident(g16,g4)
    c: Vertical(g17)
    c: Coincident(g17,g5)
    c: Vertical(g18)
    c: Coincident(g18,g6)
    c: Vertical(g19)
    c: Coincident(g19,g7)
    c: Vertical(g20)
    c: Coincident(g20,g8)
    c: Vertical(g21)
    c: Coincident(g21,g9)
    c: Vertical(g22)
    c: Coincident(g22,g10)
    c: Vertical(g23)
    c: Coincident(g23,g11)
    c: Block(g23)
    c: Block(g22)
    c: Block(g21)
    c: Block(g20)
    c: Block(g13)
    c: Block(g14)
    c: Block(g15)
    c: Block(g16)
    c: Block(g17)
    c: Block(g18)
    c: Block(g19)
FEATURE [Part::Extrusion] Extrude022
  Base = -> Sketch030
  Dir = (1,-2e-16,2e-16)
  DirMode = 2
  FaceMakerClass = Part::FaceMakerBullseye
  LengthFwd = 19
  LengthRev = 0
  Placement = pos=(-19,0,0) rot=(0,0,1;0rad)
  Solid = true
  Symmetric = false
FEATURE [Part::Fillet] Fillet022
  Base = -> Extrude022
  Edges = 24 edges r=1.49: [Edge6,Edge11,Edge18,Edge23,Edge30,Edge35,Edge42,Edge47,Edge54,Edge59,Edge66,Edge71,Edge78,Edge83,Edge90,Edge95,Edge102,Edge107,Edge114,Edge119,Edge126,Edge131,Edge138,Edge143]
FEATURE [Part::Cut] Cut020  label="top010"
  Base = -> Cut019
  Tool = -> Fillet022
FEATURE [Sketcher::SketchObject] Sketch032
  FullyConstrained = true
  Placement = pos=(117,19,0) rot=(0.57735,0.57735,0.57735;2.0944rad)
  sketch-geometry (48):
    g0: LineSegment StartX=-49.19 StartY=69.25 StartZ=0 EndX=-49.19 EndY=66.25 EndZ=0
    g1: LineSegment StartX=-49.19 StartY=63.5 StartZ=0 EndX=-49.19 EndY=60.5 EndZ=0
    g2: LineSegment StartX=-49.19 StartY=57.75 StartZ=0 EndX=-49.19 EndY=54.75 EndZ=0
    g3: LineSegment StartX=-49.19 StartY=52 StartZ=0 EndX=-49.19 EndY=49 EndZ=0
    g4: LineSegment StartX=-49.19 StartY=46.25 StartZ=0 EndX=-49.19 EndY=43.25 EndZ=0
    g5: LineSegment StartX=-49.19 StartY=40.5 StartZ=0 EndX=-49.19 EndY=37.5 EndZ=0
    g6: LineSegment StartX=-49.19 StartY=34.5 StartZ=0 EndX=-49.19 EndY=31.5 EndZ=0
    g7: LineSegment StartX=-49.19 StartY=28.75 StartZ=0 EndX=-49.19 EndY=25.75 EndZ=0
    g8: LineSegment StartX=-49.19 StartY=23 StartZ=0 EndX=-49.19 EndY=20 EndZ=0
    g9: LineSegment StartX=-49.19 StartY=17.25 StartZ=0 EndX=-49.19 EndY=14.25 EndZ=0
    g10: LineSegment StartX=-49.19 StartY=11.5 StartZ=0 EndX=-49.19 EndY=8.5 EndZ=0
    g11: LineSegment StartX=-49.19 StartY=5.75 StartZ=0 EndX=-49.19 EndY=2.75 EndZ=0
    g12: ArcOfCircle CenterX=-1.5 CenterY=67.75 CenterZ=0 NormalX=0 NormalY=0 NormalZ=1 AngleXU=0 Radius=1.5 StartAngle=4.71239 EndAngle=7.85398
    g13: ArcOfCircle CenterX=-1.5 CenterY=62 CenterZ=0 NormalX=0 NormalY=0 NormalZ=1 AngleXU=0 Radius=1.5 StartAngle=4.71239 EndAngle=7.85398
    g14: ArcOfCircle CenterX=-1.5 CenterY=56.25 CenterZ=0 NormalX=0 NormalY=0 NormalZ=1 AngleXU=0 Radius=1.5 StartAngle=4.71239 EndAngle=7.85398
    g15: ArcOfCircle CenterX=-11.49 CenterY=50.5 CenterZ=0 NormalX=0 NormalY=0 NormalZ=1 AngleXU=0 Radius=1.5 StartAngle=4.71239 EndAngle=7.85398
    g16: ArcOfCircle CenterX=-16.28 CenterY=44.75 CenterZ=0 NormalX=0 NormalY=0 NormalZ=1 AngleXU=0 Radius=1.5 StartAngle=4.71239 EndAngle=7.85398
    g17: ArcOfCircle CenterX=-18.2337 CenterY=39 CenterZ=0 NormalX=0 NormalY=0 NormalZ=1 AngleXU=0 Radius=1.5 StartAngle=4.71485 EndAngle=7.85398
    g18: ArcOfCircle CenterX=-16.2837 CenterY=27.25 CenterZ=0 NormalX=0 NormalY=0 NormalZ=1 AngleXU=0 Radius=1.5 StartAngle=4.71485 EndAngle=7.85398
    g19: ArcOfCircle CenterX=-18.2337 CenterY=33 CenterZ=0 NormalX=0 NormalY=0 NormalZ=1 AngleXU=0 Radius=1.5 StartAngle=4.71485 EndAngle=7.85398
    g20: ArcOfCircle CenterX=-11.49 CenterY=21.5 CenterZ=0 NormalX=0 NormalY=0 NormalZ=1 AngleXU=0 Radius=1.5 StartAngle=4.71239 EndAngle=7.85398
    g21: ArcOfCircle CenterX=-1.5 CenterY=4.25 CenterZ=0 NormalX=0 NormalY=0 NormalZ=1 AngleXU=0 Radius=1.5 StartAngle=4.71239 EndAngle=7.85398
    g22: ArcOfCircle CenterX=-1.5 CenterY=10 CenterZ=0 NormalX=0 NormalY=0 NormalZ=1 AngleXU=0 Radius=1.5 StartAngle=4.71239 EndAngle=7.85398
    g23: ArcOfCircle CenterX=-1.5 CenterY=15.75 CenterZ=0 NormalX=0 NormalY=0 NormalZ=1 AngleXU=0 Radius=1.5 StartAngle=4.71239 EndAngle=7.85398
    g24: LineSegment StartX=-49.19 StartY=69.25 StartZ=0 EndX=-1.5 EndY=69.25 EndZ=0
    g25: LineSegment StartX=-49.19 StartY=66.25 StartZ=0 EndX=-1.5 EndY=66.25 EndZ=0
    g26: LineSegment StartX=-49.19 StartY=63.5 StartZ=0 EndX=-1.5 EndY=63.5 EndZ=0
    g27: LineSegment StartX=-49.19 StartY=60.5 StartZ=0 EndX=-1.5 EndY=60.5 EndZ=0
    g28: LineSegment StartX=-49.19 StartY=57.75 StartZ=0 EndX=-1.5 EndY=57.75 EndZ=0
    g29: LineSegment StartX=-49.19 StartY=54.75 StartZ=0 EndX=-1.5 EndY=54.75 EndZ=0
    g30: LineSegment StartX=-49.19 StartY=52 StartZ=0 EndX=-11.49 EndY=52 EndZ=0
    g31: LineSegment StartX=-49.19 StartY=49 StartZ=0 EndX=-11.49 EndY=49 EndZ=0
    g32: LineSegment StartX=-49.19 StartY=46.25 StartZ=0 EndX=-16.28 EndY=46.25 EndZ=0
    g33: LineSegment StartX=-49.19 StartY=43.25 StartZ=0 EndX=-16.28 EndY=43.25 EndZ=0
    g34: LineSegment StartX=-49.19 StartY=40.5 StartZ=0 EndX=-18.2337 EndY=40.5 EndZ=0
    g35: LineSegment StartX=-49.19 StartY=37.5 StartZ=0 EndX=-18.23 EndY=37.5 EndZ=0
    g36: LineSegment StartX=-49.19 StartY=34.5 StartZ=0 EndX=-18.2337 EndY=34.5 EndZ=0
    g37: LineSegment StartX=-49.19 StartY=31.5 StartZ=0 EndX=-18.23 EndY=31.5 EndZ=0
    g38: LineSegment StartX=-49.19 StartY=28.75 StartZ=0 EndX=-16.2837 EndY=28.75 EndZ=0
    g39: LineSegment StartX=-49.19 StartY=25.75 StartZ=0 EndX=-16.28 EndY=25.75 EndZ=0
    g40: LineSegment StartX=-49.19 StartY=23 StartZ=0 EndX=-11.49 EndY=23 EndZ=0
    g41: LineSegment StartX=-49.19 StartY=20 StartZ=0 EndX=-11.49 EndY=20 EndZ=0
    g42: LineSegment StartX=-49.19 StartY=17.25 StartZ=0 EndX=-1.5 EndY=17.25 EndZ=0
    g43: LineSegment StartX=-49.19 StartY=14.25 StartZ=0 EndX=-1.5 EndY=14.25 EndZ=0
    g44: LineSegment StartX=-49.19 StartY=11.5 StartZ=0 EndX=-1.5 EndY=11.5 EndZ=0
    g45: LineSegment StartX=-49.19 StartY=8.5 StartZ=0 EndX=-1.5 EndY=8.5 EndZ=0
    g46: LineSegment StartX=-49.19 StartY=5.75 StartZ=0 EndX=-1.5 EndY=5.75 EndZ=0
    g47: LineSegment StartX=-49.19 StartY=2.75 StartZ=0 EndX=-1.5 EndY=2.75 EndZ=0
  constraints (120):
    c: Vertical(g0)
    c: Distance(g0) = 3
    c: Block(g0)
    c: Vertical(g1)
    c: Distance(g1) = 3
    c: Vertical(g2)
    c: Equal(g0,g2) = 3
    c: Block(g2)
    c: Vertical(g3)
    c: Equal(g1,g3) = 3
    c: Vertical(g4)
    c: Equal(g0,g4) = 3
    c: Block(g4)
    c: Vertical(g5)
    c: Equal(g1,g5) = 3
    c: Vertical(g6)
    c: Equal(g0,g6) = 3
    c: Block(g6)
    c: Vertical(g7)
    c: Equal(g1,g7) = 3
    c: Vertical(g8)
    c: Equal(g0,g8) = 3
    c: Block(g8)
    c: Vertical(g9)
    c: Equal(g1,g9) = 3
    c: Vertical(g10)
    c: Equal(g0,g10) = 3
    c: Block(g10)
    c: Vertical(g11)
    c: Equal(g1,g11) = 3
    c: Block(g12)
    c: Block(g13)
    c: Block(g14)
    c: Block(g15)
    c: Block(g16)
    c: Block(g17)
    c: Block(g18)
    c: Block(g19)
    c: Block(g20)
    c: Block(g21)
    c: Block(g22)
    c: Block(g23)
    c: Block(g11)
    c: Block(g9)
    c: Block(g7)
    c: Block(g5)
    c: Block(g3)
    c: Block(g1)
    c: Coincident(g24,g0)
    c: Coincident(g24,g12)
    c: Horizontal(g24)
    c: Coincident(g25,g0)
    c: Coincident(g25,g12)
    c: Horizontal(g25)
    c: Coincident(g26,g1)
    c: Coincident(g26,g13)
    c: Horizontal(g26)
    c: Coincident(g27,g1)
    c: Coincident(g27,g13)
    c: Horizontal(g27)
    c: Coincident(g28,g2)
    c: Coincident(g28,g14)
    c: Horizontal(g28)
    c: Coincident(g29,g2)
    c: Coincident(g29,g14)
    c: Horizontal(g29)
    c: Coincident(g30,g3)
    c: Coincident(g30,g15)
    c: Horizontal(g30)
    c: Coincident(g31,g3)
    c: Coincident(g31,g15)
    c: Horizontal(g31)
    c: Coincident(g32,g4)
    c: Coincident(g32,g16)
    c: Horizontal(g32)
    c: Coincident(g33,g4)
    c: Coincident(g33,g16)
    c: Horizontal(g33)
    c: Coincident(g34,g5)
    c: Coincident(g34,g17)
    c: Horizontal(g34)
    c: Coincident(g35,g5)
    c: Coincident(g35,g17)
    c: Horizontal(g35)
    c: Coincident(g36,g6)
    c: Coincident(g36,g19)
    c: Horizontal(g36)
    c: Coincident(g37,g6)
    c: Coincident(g37,g19)
    c: Horizontal(g37)
    c: Coincident(g38,g7)
    c: Coincident(g38,g18)
    c: Horizontal(g38)
    c: Coincident(g39,g7)
    c: Coincident(g39,g18)
    c: Horizontal(g39)
    c: Coincident(g40,g8)
    c: Coincident(g40,g20)
    c: Horizontal(g40)
    c: Coincident(g41,g8)
    c: Coincident(g41,g20)
    c: Horizontal(g41)
    c: Coincident(g42,g9)
    c: Coincident(g42,g23)
    c: Horizontal(g42)
    c: Coincident(g43,g9)
    c: Coincident(g43,g23)
    c: Horizontal(g43)
    c: Coincident(g44,g10)
    c: Coincident(g44,g22)
    c: Horizontal(g44)
    c: Coincident(g45,g10)
    c: Coincident(g45,g22)
    c: Horizontal(g45)
    c: Coincident(g46,g11)
    c: Coincident(g46,g21)
    c: Horizontal(g46)
    c: Coincident(g47,g11)
    c: Coincident(g47,g21)
    c: Horizontal(g47)
FEATURE [Part::Extrusion] Extrude023
  Base = -> Sketch032
  Dir = (1,-2e-16,2e-16)
  DirMode = 2
  FaceMakerClass = Part::FaceMakerBullseye
  LengthFwd = 19
  LengthRev = 0
  Placement = pos=(-19,0,0) rot=(0,0,1;0rad)
  Solid = true
  Symmetric = false
FEATURE [Part::Fillet] Fillet023
  Base = -> Extrude023
  Edges = <same value as first occurrence — deduplicated (x6 in doc)>
  Placement = pos=(0,0.05,0) rot=(0,0,1;0rad)
FEATURE [Part::Cut] Cut014  label="bottom003"
  Base = -> Cut007
  Tool = -> Fusion047
FEATURE [Part::Cut] Cut021  label="bottom004"
  Base = -> Cut014
  Tool = -> Fillet023
FEATURE [Sketcher::SketchObject] Sketch033
  FullyConstrained = true
  Placement = pos=(117,19,0) rot=(0.57735,0.57735,0.57735;2.0944rad)
  sketch-geometry (8):
    g0: LineSegment StartX=-49.19 StartY=69.25 StartZ=0 EndX=-49.19 EndY=66.25 EndZ=0
    g1: LineSegment StartX=-49.19 StartY=5.75 StartZ=0 EndX=-49.19 EndY=2.75 EndZ=0
    g2: ArcOfCircle CenterX=-1.5 CenterY=67.75 CenterZ=0 NormalX=0 NormalY=0 NormalZ=1 AngleXU=0 Radius=1.5 StartAngle=4.71239 EndAngle=7.85398
    g3: ArcOfCircle CenterX=-1.5 CenterY=4.25 CenterZ=0 NormalX=0 NormalY=0 NormalZ=1 AngleXU=0 Radius=1.5 StartAngle=4.71239 EndAngle=7.85398
    g4: LineSegment StartX=-49.19 StartY=69.25 StartZ=0 EndX=-1.5 EndY=69.25 EndZ=0
    g5: LineSegment StartX=-49.19 StartY=66.25 StartZ=0 EndX=-1.5 EndY=66.25 EndZ=0
    g6: LineSegment StartX=-49.19 StartY=5.75 StartZ=0 EndX=-1.5 EndY=5.75 EndZ=0
    g7: LineSegment StartX=-49.19 StartY=2.75 StartZ=0 EndX=-1.5 EndY=2.75 EndZ=0
  constraints (19):
    c: Vertical(g0)
    c: Distance(g0) = 3
    c: Block(g0)
    c: Vertical(g1)
    c: Block(g2)
    c: Block(g3)
    c: Block(g1)
    c: Coincident(g4,g0)
    c: Coincident(g4,g2)
    c: Horizontal(g4)
    c: Coincident(g5,g0)
    c: Coincident(g5,g2)
    c: Horizontal(g5)
    c: Coincident(g6,g1)
    c: Coincident(g6,g3)
    c: Horizontal(g6)
    c: Coincident(g7,g1)
    c: Coincident(g7,g3)
    c: Horizontal(g7)
FEATURE [Sketcher::SketchObject] Sketch034
  FullyConstrained = true
  Placement = pos=(117,19,0) rot=(0.57735,0.57735,0.57735;2.0944rad)
  sketch-geometry (8):
    g0: LineSegment StartX=-49.19 StartY=63.5 StartZ=0 EndX=-49.19 EndY=60.5 EndZ=0
    g1: LineSegment StartX=-49.19 StartY=11.5 StartZ=0 EndX=-49.19 EndY=8.5 EndZ=0
    g2: ArcOfCircle CenterX=-1.5 CenterY=62 CenterZ=0 NormalX=0 NormalY=0 NormalZ=1 AngleXU=0 Radius=1.5 StartAngle=4.71239 EndAngle=7.85398
    g3: ArcOfCircle CenterX=-1.5 CenterY=10 CenterZ=0 NormalX=0 NormalY=0 NormalZ=1 AngleXU=0 Radius=1.5 StartAngle=4.71239 EndAngle=7.85398
    g4: LineSegment StartX=-49.19 StartY=63.5 StartZ=0 EndX=-1.5 EndY=63.5 EndZ=0
    g5: LineSegment StartX=-49.19 StartY=60.5 StartZ=0 EndX=-1.5 EndY=60.5 EndZ=0
    g6: LineSegment StartX=-49.19 StartY=11.5 StartZ=0 EndX=-1.5 EndY=11.5 EndZ=0
    g7: LineSegment StartX=-49.19 StartY=8.5 StartZ=0 EndX=-1.5 EndY=8.5 EndZ=0
  constraints (19):
    c: Vertical(g0)
    c: Distance(g0) = 3
    c: Vertical(g1)
    c: Block(g1)
    c: Block(g2)
    c: Block(g3)
    c: Block(g0)
    c: Coincident(g4,g0)
    c: Coincident(g4,g2)
    c: Horizontal(g4)
    c: Coincident(g5,g0)
    c: Coincident(g5,g2)
    c: Horizontal(g5)
    c: Coincident(g6,g1)
    c: Coincident(g6,g3)
    c: Horizontal(g6)
    c: Coincident(g7,g1)
    c: Coincident(g7,g3)
    c: Horizontal(g7)
FEATURE [Part::Extrusion] Extrude024
  Base = -> Sketch033
  Dir = (1,0,0)
  DirMode = 2
  FaceMakerClass = Part::FaceMakerBullseye
  LengthFwd = 10
  LengthRev = 0
  Solid = true
  Symmetric = false
FEATURE [Part::Extrusion] Extrude025
  Base = -> Sketch034
  Dir = (1,0,0)
  DirMode = 2
  FaceMakerClass = Part::FaceMakerBullseye
  LengthFwd = 10
  LengthRev = 0
  Solid = true
  Symmetric = false
FEATURE [Part::Fillet] Fillet024  label="removeFromtMoreFrontCaseScrewRetainers"
  Base = -> Extrude024
  Edges = 4 edges r=1.49: [Edge6,Edge11,Edge18,Edge23]
  Placement = pos=(-11,0,0) rot=(0,0,1;0rad)
FEATURE [Part::Fillet] Fillet025  label="removeFromtMoreFrontCaseScrewRetainers001"
  Base = -> Extrude025
  Edges = 4 edges r=1.49: [Edge6,Edge11,Edge18,Edge23]
  Placement = pos=(-19,0,0) rot=(0,0,1;0rad)
FEATURE [Part::Cut] Cut022
  Base = -> Cut015
  Tool = -> Fillet025
FEATURE [Part::Cut] Cut023  label="screwRetainers"
  Base = -> Cut022
  Tool = -> Fillet024
FEATURE [Part::MultiFuse] Fusion056  label="bottom005"
  Shapes = -> [Fusion044,Cut021]
FEATURE [Part::MultiFuse] Fusion057  label="casePillars001"
  Shapes = -> [Cut016,Fusion052]
FEATURE [Part::MultiFuse] Fusion058  label="bottom006"
  Shapes = -> [Fusion056,Cut023]
FEATURE [Part::MultiFuse] Fusion059  label="bottom007"
  Shapes = -> [Fusion058,Fillet005]
FEATURE [Part::MultiFuse] Fusion060  label="bottom008"
  Shapes = -> [Fusion059,Fusion]
FEATURE [Part::MultiFuse] Fusion061  label="top011"
  Shapes = -> [Cut006,Cut020]
FEATURE [Part::MultiFuse] Fusion062  label="top012"
  Shapes = -> [Fusion057,Fusion061]
FEATURE [Sketcher::SketchObject] Sketch035  label="topSketch007"
  FullyConstrained = true
  sketch-geometry (6):
    g0: LineSegment StartX=19 StartY=38 StartZ=0 EndX=117 EndY=38 EndZ=0
    g1: ArcOfCircle CenterX=19 CenterY=19 CenterZ=0 NormalX=0 NormalY=0 NormalZ=1 AngleXU=0 Radius=19 StartAngle=1.5708 EndAngle=3.14159
    g2: LineSegment StartX=117 StartY=38 StartZ=0 EndX=117 EndY=19 EndZ=0
    g3: LineSegment StartX=98 StartY=1.0161e-12 StartZ=0 EndX=5.22862e-06 EndY=1.0161e-12 EndZ=0
    g4: LineSegment StartX=5.22862e-06 StartY=19 StartZ=0 EndX=5.22862e-06 EndY=1.0161e-12 EndZ=0
    g5: ArcOfCircle CenterX=98 CenterY=19 CenterZ=0 NormalX=0 NormalY=0 NormalZ=1 AngleXU=0 Radius=19 StartAngle=4.71239 EndAngle=6.28319
  constraints (16):
    c: Horizontal(g0)
    c: Distance(g0) = 98
    c: Coincident(g1,g0)
    c: Block(g1)
    c: Coincident(g2,g0)
    c: Vertical(g2)
    c: Distance(g2) = 19
    c: Horizontal(g3)
    c: Coincident(g4,g1)
    c: Vertical(g4)
    c: Coincident(g3,g4)
    c: Block(g3)
    c: Coincident(g5,g2)
    c: Coincident(g5,g3)
    c: Block(g0)
    c: Block(g5)
FEATURE [Part::Extrusion] Extrude026  label="sideA001"
  Base = -> Sketch035
  Dir = (0,0,1)
  DirMode = 2
  FaceMakerClass = Part::FaceMakerBullseye
  LengthFwd = 3
  LengthRev = 0
  Placement = pos=(0,0,-2.7) rot=(0,0,1;0rad)
  Solid = true
  Symmetric = false
FEATURE [Sketcher::SketchObject] Sketch036  label="topSketch008"
  FullyConstrained = true
  sketch-geometry (6):
    g0: LineSegment StartX=19 StartY=38 StartZ=0 EndX=117 EndY=38 EndZ=0
    g1: ArcOfCircle CenterX=19 CenterY=19 CenterZ=0 NormalX=0 NormalY=0 NormalZ=1 AngleXU=0 Radius=19 StartAngle=1.5708 EndAngle=3.14159
    g2: LineSegment StartX=117 StartY=38 StartZ=0 EndX=117 EndY=19 EndZ=0
    g3: LineSegment StartX=98 StartY=1.0161e-12 StartZ=0 EndX=5.22862e-06 EndY=1.0161e-12 EndZ=0
    g4: LineSegment StartX=5.22862e-06 StartY=19 StartZ=0 EndX=5.22862e-06 EndY=1.0161e-12 EndZ=0
    g5: ArcOfCircle CenterX=98 CenterY=19 CenterZ=0 NormalX=0 NormalY=0 NormalZ=1 AngleXU=0 Radius=19 StartAngle=4.71239 EndAngle=6.28319
  constraints (16):
    c: Horizontal(g0)
    c: Distance(g0) = 98
    c: Coincident(g1,g0)
    c: Block(g1)
    c: Coincident(g2,g0)
    c: Vertical(g2)
    c: Distance(g2) = 19
    c: Horizontal(g3)
    c: Coincident(g4,g1)
    c: Vertical(g4)
    c: Coincident(g3,g4)
    c: Block(g3)
    c: Coincident(g5,g2)
    c: Coincident(g5,g3)
    c: Block(g0)
    c: Block(g5)
FEATURE [Part::Extrusion] Extrude027  label="sideB001"
  Base = -> Sketch036
  Dir = (0,0,1)
  DirMode = 2
  FaceMakerClass = Part::FaceMakerBullseye
  LengthFwd = 3
  LengthRev = 0
  Placement = pos=(0,0,71.7) rot=(0,0,1;0rad)
  Solid = true
  Symmetric = false
FEATURE [Part::MultiFuse] Fusion064  label="removeFromBottom"
  Shapes = -> [Extrude026,Extrude027]
FEATURE [Part::Cut] Cut024  label="bottom009"
  Base = -> Fusion060
  Tool = -> Fusion064
FEATURE [Sketcher::SketchObject] Sketch037  label="topSketch009"
  FullyConstrained = true
  sketch-geometry (8):
    g0: ArcOfCircle CenterX=19 CenterY=19.1201 CenterZ=0 NormalX=0 NormalY=0 NormalZ=1 AngleXU=0 Radius=18.8799 StartAngle=1.5708 EndAngle=3.14793
    g1: LineSegment StartX=0.120501 StartY=19.0004 StartZ=0 EndX=0.120501 EndY=0.000382114 EndZ=0
    g2: LineSegment StartX=19 StartY=38 StartZ=0 EndX=124 EndY=38 EndZ=0
    g3: LineSegment StartX=0.120501 StartY=0.000382114 StartZ=0 EndX=105.121 EndY=0.000382114 EndZ=0
    g4: LineSegment StartX=124 StartY=38 StartZ=0 EndX=125.616 EndY=38 EndZ=0
    g5: LineSegment StartX=105.121 StartY=0.000382114 StartZ=0 EndX=106.736 EndY=0.000382114 EndZ=0
    g6: ArcOfCircle CenterX=106.616 CenterY=19 CenterZ=0 NormalX=0 NormalY=0 NormalZ=1 AngleXU=0 Radius=19 StartAngle=4.71873 EndAngle=6.28319
    g7: LineSegment StartX=125.616 StartY=38 StartZ=0 EndX=125.616 EndY=19 EndZ=0
  constraints (21):
    c: Block(g0)
    c: Coincident(g1,g0)
    c: Vertical(g1)
    c: Horizontal(g2)
    c: Distance(g2) = 105
    c: Coincident(g2,g0)
    c: Distance(g1) = 19
    c: Coincident(g3,g1)
    c: Horizontal(g3)
    c: Distance(g3) = 105
    c: Coincident(g4,g2)
    c: Horizontal(g4)
    c: Distance(g4) = 1.61553
    c: Horizontal(g5)
    c: Equal(g4,g5) = 1.61553
    c: Coincident(g5,g3)
    c: Block(g6)
    c: Coincident(g6,g5)
    c: Coincident(g7,g4)
    c: Coincident(g7,g6)
    c: Vertical(g7)
FEATURE [Part::Extrusion] Extrude028  label="sideB"
  Base = -> Sketch037
  Dir = (0,0,1)
  DirMode = 2
  FaceMakerClass = Part::FaceMakerBullseye
  LengthFwd = 3
  LengthRev = 0
  Placement = pos=(0,0,72) rot=(0,0,1;0rad)
  Solid = true
  Symmetric = false
FEATURE [Sketcher::SketchObject] Sketch038  label="topSketch010"
  FullyConstrained = true
  sketch-geometry (22):
    g0: LineSegment StartX=5.21097e-06 StartY=3 StartZ=0 EndX=5.21097e-06 EndY=19 EndZ=0
    g1: ArcOfCircle CenterX=19 CenterY=19 CenterZ=0 NormalX=0 NormalY=0 NormalZ=1 AngleXU=0 Radius=19 StartAngle=1.5708 EndAngle=3.14159
    g2: ArcOfCircle CenterX=19 CenterY=19 CenterZ=0 NormalX=0 NormalY=0 NormalZ=1 AngleXU=0 Radius=16 StartAngle=1.5708 EndAngle=3.14159
    g3: LineSegment StartX=114 StartY=35 StartZ=0 EndX=19 EndY=35 EndZ=0
    g4: LineSegment StartX=5.21097e-06 StartY=3 StartZ=0 EndX=5.21097e-06 EndY=0 EndZ=0
    g5: LineSegment StartX=3 StartY=0 StartZ=0 EndX=5.21097e-06 EndY=0 EndZ=0
    g6: LineSegment StartX=3 StartY=19 StartZ=0 EndX=3 EndY=0 EndZ=0
    g7: LineSegment StartX=19 StartY=38 StartZ=0 EndX=124 EndY=38 EndZ=0
    g8: Circle CenterX=119 CenterY=35 CenterZ=0 NormalX=0 NormalY=0 NormalZ=1 AngleXU=0 Radius=1
    g9: Circle CenterX=121 CenterY=35 CenterZ=0 NormalX=0 NormalY=0 NormalZ=1 AngleXU=0 Radius=1
    g10: Circle CenterX=121 CenterY=33 CenterZ=0 NormalX=0 NormalY=0 NormalZ=1 AngleXU=0 Radius=1
    g11: BSplineCurve PolesCount=3 KnotsCount=2 Degree=2 IsPeriodic=0
    g12: GeomPoint X=119 Y=35 Z=0
    g13: GeomPoint X=121 Y=33 Z=0
    g14: LineSegment StartX=119 StartY=35 StartZ=0 EndX=114 EndY=35 EndZ=0
    g15: ArcOfCircle CenterX=105 CenterY=19 CenterZ=0 NormalX=0 NormalY=0 NormalZ=1 AngleXU=0 Radius=16 StartAngle=5.60905 EndAngle=6.28319
    g16: LineSegment StartX=121 StartY=33 StartZ=0 EndX=121 EndY=19 EndZ=0
    g17: LineSegment StartX=117.5 StartY=9.01251 StartZ=0 EndX=121.163 EndY=9.0125 EndZ=0
    g18: ArcOfCircle CenterX=105 CenterY=19 CenterZ=0 NormalX=0 NormalY=0 NormalZ=1 AngleXU=0 Radius=20.6155 StartAngle=5.7297 EndAngle=6.28319
    g19: LineSegment StartX=121.163 StartY=9.0125 StartZ=0 EndX=122.538 EndY=8.16329 EndZ=0
    g20: LineSegment StartX=124 StartY=38 StartZ=0 EndX=125.616 EndY=38 EndZ=0
    g21: LineSegment StartX=125.616 StartY=19 StartZ=0 EndX=125.616 EndY=38 EndZ=0
  constraints (49):
    c: Vertical(g0)
    c: Block(g0)
    c: Coincident(g1,g0)
    c: Block(g1)
    c: Coincident(g2,g1)
    c: Block(g2)
    c: Coincident(g3,g2)
    c: Horizontal(g3)
    c: Tangent(g3,g2)
    c: Coincident(g4,g0)
    c: Distance(g4) = 3
    c: Vertical(g4)
    c: Coincident(g5,g4)
    c: Horizontal(g5)
    c: Coincident(g6,g2)
    c: Coincident(g6,g5)
    c: Vertical(g6)
    c: Horizontal(g7)
    c: Distance(g7) = 105
    c: Coincident(g7,g1)
    c: Block(g3)
    c: Weight(g8) = 1
    c: Equal(g8,g9)
    c: Equal(g8,g10)
    c: InternalAlignment(g8,g11)
    c: InternalAlignment(g9,g11)
    c: InternalAlignment(g10,g11)
    c: InternalAlignment(g12,g11)
    c: InternalAlignment(g13,g11)
    c: Block(g11)
    c: Coincident(g14,g11)
    c: Coincident(g14,g3)
    c: Horizontal(g14)
    c: Block(g15)
    c: Coincident(g16,g11)
    c: Coincident(g16,g15)
    c: Vertical(g16)
    c: Distance(g16) = 14
    c: Coincident(g17,g15)
    c: Block(g18)
    c: Coincident(g19,g18)
    c: Coincident(g20,g7)
    c: Horizontal(g20)
    c: Vertical(g21)
    c: Coincident(g20,g21)
    c: Block(g20)
    c: Block(g21)
    c: Block(g19)
    c: Block(g17)
FEATURE [Part::Extrusion] Extrude029
  Base = -> Sketch038
  Dir = (0,0,1)
  DirMode = 2
  FaceMakerClass = Part::FaceMakerBullseye
  LengthFwd = 72
  LengthRev = 0
  Solid = true
  Symmetric = false
FEATURE [Part::Feature] Face085
  shape: bbox 4.8 x 25.5 x 2e-07 mm, 1 faces, 0 solids (baked)
FEATURE [Part::Revolution] Revolve089  label="moreFrontCaseScrewPost003"
  Angle = 360
  Axis = (0,1,0)
  Base = (0,0,0)
  FaceMakerClass = Part::FaceMakerBullseye
  Placement = pos=(109.5,4.5,3.5) rot=(0,0,1;0rad)
  Solid = false
  Source = -> Face085
  Symmetric = false
FEATURE [Part::Feature] Face086
  shape: bbox 4.8 x 25.5 x 2e-07 mm, 1 faces, 0 solids (baked)
FEATURE [Part::Revolution] Revolve090  label="moreFrontCaseScrewPost004"
  Angle = 360
  Axis = (0,1,0)
  Base = (0,0,0)
  FaceMakerClass = Part::FaceMakerBullseye
  Placement = pos=(109.5,4.5,68.5) rot=(0,0,1;0rad)
  Solid = false
  Source = -> Face086
  Symmetric = false
FEATURE [Part::Fillet] Fillet026  label="top013"
  Base = -> Extrude029
  Edges = 1 edges r=2: [Edge35]
FEATURE [Sketcher::SketchObject] Sketch039
  FullyConstrained = true
  sketch-geometry (7):
    g0: LineSegment StartX=0 StartY=0 StartZ=0 EndX=0 EndY=6 EndZ=0
    g1: Circle CenterX=0 CenterY=0 CenterZ=0 NormalX=0 NormalY=0 NormalZ=1 AngleXU=0 Radius=1
    g2: Circle CenterX=8 CenterY=6 CenterZ=0 NormalX=0 NormalY=0 NormalZ=1 AngleXU=0 Radius=1
    g3: BSplineCurve PolesCount=3 KnotsCount=2 Degree=2 IsPeriodic=0
    g4: GeomPoint X=0 Y=0 Z=0
    g5: GeomPoint X=8 Y=6 Z=0
    g6: LineSegment StartX=0 StartY=6 StartZ=0 EndX=8 EndY=6 EndZ=0
  constraints (14):
    c: Coincident(g0,g-1)
    c: Distance(g0) = 6
    c: Vertical(g0)
    c: Coincident(g3,g0)
    c: Weight(g1) = 1
    c: Equal(g1,g2)
    c: InternalAlignment(g1,g3)
    c: InternalAlignment(g2,g3)
    c: InternalAlignment(g4,g3)
    c: InternalAlignment(g5,g3)
    c: Block(g3)
    c: Coincident(g6,g0)
    c: Coincident(g6,g3)
    c: Horizontal(g6)
FEATURE [Sketcher::SketchObject] Sketch040
  FullyConstrained = true
  sketch-geometry (7):
    g0: LineSegment StartX=0 StartY=0 StartZ=0 EndX=0 EndY=6 EndZ=0
    g1: Circle CenterX=0 CenterY=0 CenterZ=0 NormalX=0 NormalY=0 NormalZ=1 AngleXU=0 Radius=1
    g2: Circle CenterX=8 CenterY=6 CenterZ=0 NormalX=0 NormalY=0 NormalZ=1 AngleXU=0 Radius=1
    g3: BSplineCurve PolesCount=3 KnotsCount=2 Degree=2 IsPeriodic=0
    g4: GeomPoint X=0 Y=0 Z=0
    g5: GeomPoint X=8 Y=6 Z=0
    g6: LineSegment StartX=0 StartY=6 StartZ=0 EndX=8 EndY=6 EndZ=0
  constraints (14):
    c: Coincident(g0,g-1)
    c: Distance(g0) = 6
    c: Vertical(g0)
    c: Coincident(g3,g0)
    c: Weight(g1) = 1
    c: Equal(g1,g2)
    c: InternalAlignment(g1,g3)
    c: InternalAlignment(g2,g3)
    c: InternalAlignment(g4,g3)
    c: InternalAlignment(g5,g3)
    c: Block(g3)
    c: Coincident(g6,g0)
    c: Coincident(g6,g3)
    c: Horizontal(g6)
FEATURE [Sketcher::SketchObject] Sketch041
  FullyConstrained = true
  sketch-geometry (7):
    g0: LineSegment StartX=0 StartY=0 StartZ=0 EndX=0 EndY=6 EndZ=0
    g1: Circle CenterX=0 CenterY=0 CenterZ=0 NormalX=0 NormalY=0 NormalZ=1 AngleXU=0 Radius=1
    g2: Circle CenterX=8 CenterY=6 CenterZ=0 NormalX=0 NormalY=0 NormalZ=1 AngleXU=0 Radius=1
    g3: BSplineCurve PolesCount=3 KnotsCount=2 Degree=2 IsPeriodic=0
    g4: GeomPoint X=0 Y=0 Z=0
    g5: GeomPoint X=8 Y=6 Z=0
    g6: LineSegment StartX=0 StartY=6 StartZ=0 EndX=8 EndY=6 EndZ=0
  constraints (14):
    c: Coincident(g0,g-1)
    c: Distance(g0) = 6
    c: Vertical(g0)
    c: Coincident(g3,g0)
    c: Weight(g1) = 1
    c: Equal(g1,g2)
    c: InternalAlignment(g1,g3)
    c: InternalAlignment(g2,g3)
    c: InternalAlignment(g4,g3)
    c: InternalAlignment(g5,g3)
    c: Block(g3)
    c: Coincident(g6,g0)
    c: Coincident(g6,g3)
    c: Horizontal(g6)
FEATURE [Sketcher::SketchObject] Sketch042
  FullyConstrained = true
  sketch-geometry (7):
    g0: LineSegment StartX=0 StartY=0 StartZ=0 EndX=0 EndY=6 EndZ=0
    g1: Circle CenterX=0 CenterY=0 CenterZ=0 NormalX=0 NormalY=0 NormalZ=1 AngleXU=0 Radius=1
    g2: Circle CenterX=8 CenterY=6 CenterZ=0 NormalX=0 NormalY=0 NormalZ=1 AngleXU=0 Radius=1
    g3: BSplineCurve PolesCount=3 KnotsCount=2 Degree=2 IsPeriodic=0
    g4: GeomPoint X=0 Y=0 Z=0
    g5: GeomPoint X=8 Y=6 Z=0
    g6: LineSegment StartX=0 StartY=6 StartZ=0 EndX=8 EndY=6 EndZ=0
  constraints (14):
    c: Coincident(g0,g-1)
    c: Distance(g0) = 6
    c: Vertical(g0)
    c: Coincident(g3,g0)
    c: Weight(g1) = 1
    c: Equal(g1,g2)
    c: InternalAlignment(g1,g3)
    c: InternalAlignment(g2,g3)
    c: InternalAlignment(g4,g3)
    c: InternalAlignment(g5,g3)
    c: Block(g3)
    c: Coincident(g6,g0)
    c: Coincident(g6,g3)
    c: Horizontal(g6)
FEATURE [Part::Extrusion] Extrude030  label="caseScrewPillarBracket008"
  Base = -> Sketch039
  Dir = (0,0,1)
  DirMode = 2
  FaceMakerClass = Part::FaceMakerBullseye
  LengthFwd = 2.4
  LengthRev = 0
  Placement = pos=(15.76,29,8.8) rot=(0,1,0;0rad)
  Solid = true
  Symmetric = false
FEATURE [Part::Extrusion] Extrude031  label="caseScrewPillarBracket009"
  Base = -> Sketch040
  Dir = (0,0,1)
  DirMode = 2
  FaceMakerClass = Part::FaceMakerBullseye
  LengthFwd = 2.4
  LengthRev = 0
  Placement = pos=(15.76,29,60.8) rot=(0,0,1;0rad)
  Solid = true
  Symmetric = false
FEATURE [Part::Extrusion] Extrude032  label="caseScrewPillarBracket010"
  Base = -> Sketch041
  Dir = (0,0,1)
  DirMode = 2
  FaceMakerClass = Part::FaceMakerBullseye
  LengthFwd = 2.4
  LengthRev = 0
  Placement = pos=(13.7,29,13.26) rot=(0,-1,0;1.5708rad)
  Solid = true
  Symmetric = false
FEATURE [Part::Extrusion] Extrude033  label="caseScrewPillarBracket011"
  Base = -> Sketch042
  Dir = (0,0,1)
  DirMode = 2
  FaceMakerClass = Part::FaceMakerBullseye
  LengthFwd = 2.4
  LengthRev = 0
  Placement = pos=(11.3,29,58.74) rot=(0,1,0;1.5708rad)
  Solid = true
  Symmetric = false
FEATURE [Sketcher::SketchObject] Sketch043
  FullyConstrained = true
  sketch-geometry (7):
    g0: LineSegment StartX=0 StartY=0 StartZ=0 EndX=0 EndY=6 EndZ=0
    g1: Circle CenterX=0 CenterY=0 CenterZ=0 NormalX=0 NormalY=0 NormalZ=1 AngleXU=0 Radius=1
    g2: Circle CenterX=8 CenterY=6 CenterZ=0 NormalX=0 NormalY=0 NormalZ=1 AngleXU=0 Radius=1
    g3: BSplineCurve PolesCount=3 KnotsCount=2 Degree=2 IsPeriodic=0
    g4: GeomPoint X=0 Y=0 Z=0
    g5: GeomPoint X=8 Y=6 Z=0
    g6: LineSegment StartX=0 StartY=6 StartZ=0 EndX=8 EndY=6 EndZ=0
  constraints (14):
    c: Coincident(g0,g-1)
    c: Distance(g0) = 6
    c: Vertical(g0)
    c: Coincident(g3,g0)
    c: Weight(g1) = 1
    c: Equal(g1,g2)
    c: InternalAlignment(g1,g3)
    c: InternalAlignment(g2,g3)
    c: InternalAlignment(g4,g3)
    c: InternalAlignment(g5,g3)
    c: Block(g3)
    c: Coincident(g6,g0)
    c: Coincident(g6,g3)
    c: Horizontal(g6)
FEATURE [Part::Extrusion] Extrude034  label="caseScrewPillarBracket012"
  Base = -> Sketch043
  Dir = (0,0,1)
  DirMode = 2
  FaceMakerClass = Part::FaceMakerBullseye
  LengthFwd = 2.4
  LengthRev = 0
  Placement = pos=(88.3,29,65.23) rot=(0,1,0;1.5708rad)
  Solid = true
  Symmetric = false
FEATURE [Sketcher::SketchObject] Sketch044
  FullyConstrained = true
  sketch-geometry (7):
    g0: LineSegment StartX=0 StartY=0 StartZ=0 EndX=0 EndY=6 EndZ=0
    g1: Circle CenterX=0 CenterY=0 CenterZ=0 NormalX=0 NormalY=0 NormalZ=1 AngleXU=0 Radius=1
    g2: Circle CenterX=8 CenterY=6 CenterZ=0 NormalX=0 NormalY=0 NormalZ=1 AngleXU=0 Radius=1
    g3: BSplineCurve PolesCount=3 KnotsCount=2 Degree=2 IsPeriodic=0
    g4: GeomPoint X=0 Y=0 Z=0
    g5: GeomPoint X=8 Y=6 Z=0
    g6: LineSegment StartX=0 StartY=6 StartZ=0 EndX=8 EndY=6 EndZ=0
  constraints (14):
    c: Coincident(g0,g-1)
    c: Distance(g0) = 6
    c: Vertical(g0)
    c: Coincident(g3,g0)
    c: Weight(g1) = 1
    c: Equal(g1,g2)
    c: InternalAlignment(g1,g3)
    c: InternalAlignment(g2,g3)
    c: InternalAlignment(g4,g3)
    c: InternalAlignment(g5,g3)
    c: Block(g3)
    c: Coincident(g6,g0)
    c: Coincident(g6,g3)
    c: Horizontal(g6)
FEATURE [Part::Extrusion] Extrude035  label="caseScrewPillarBracket013"
  Base = -> Sketch044
  Dir = (0,0,1)
  DirMode = 2
  FaceMakerClass = Part::FaceMakerBullseye
  LengthFwd = 2.4
  LengthRev = 0
  Placement = pos=(90.7,29,6.77) rot=(0,-1,0;1.5708rad)
  Solid = true
  Symmetric = false
FEATURE [Sketcher::SketchObject] Sketch045
  FullyConstrained = true
  sketch-geometry (7):
    g0: LineSegment StartX=0 StartY=0 StartZ=0 EndX=0 EndY=6 EndZ=0
    g1: Circle CenterX=0 CenterY=0 CenterZ=0 NormalX=0 NormalY=0 NormalZ=1 AngleXU=0 Radius=1
    g2: Circle CenterX=8 CenterY=6 CenterZ=0 NormalX=0 NormalY=0 NormalZ=1 AngleXU=0 Radius=1
    g3: BSplineCurve PolesCount=3 KnotsCount=2 Degree=2 IsPeriodic=0
    g4: GeomPoint X=0 Y=0 Z=0
    g5: GeomPoint X=8 Y=6 Z=0
    g6: LineSegment StartX=0 StartY=6 StartZ=0 EndX=8 EndY=6 EndZ=0
  constraints (14):
    c: Coincident(g0,g-1)
    c: Distance(g0) = 6
    c: Vertical(g0)
    c: Coincident(g3,g0)
    c: Weight(g1) = 1
    c: Equal(g1,g2)
    c: InternalAlignment(g1,g3)
    c: InternalAlignment(g2,g3)
    c: InternalAlignment(g4,g3)
    c: InternalAlignment(g5,g3)
    c: Block(g3)
    c: Coincident(g6,g0)
    c: Coincident(g6,g3)
    c: Horizontal(g6)
FEATURE [Sketcher::SketchObject] Sketch046
  FullyConstrained = true
  sketch-geometry (7):
    g0: LineSegment StartX=0 StartY=0 StartZ=0 EndX=0 EndY=6 EndZ=0
    g1: Circle CenterX=0 CenterY=0 CenterZ=0 NormalX=0 NormalY=0 NormalZ=1 AngleXU=0 Radius=1
    g2: Circle CenterX=8 CenterY=6 CenterZ=0 NormalX=0 NormalY=0 NormalZ=1 AngleXU=0 Radius=1
    g3: BSplineCurve PolesCount=3 KnotsCount=2 Degree=2 IsPeriodic=0
    g4: GeomPoint X=0 Y=0 Z=0
    g5: GeomPoint X=8 Y=6 Z=0
    g6: LineSegment StartX=0 StartY=6 StartZ=0 EndX=8 EndY=6 EndZ=0
  constraints (14):
    c: Coincident(g0,g-1)
    c: Distance(g0) = 6
    c: Vertical(g0)
    c: Coincident(g3,g0)
    c: Weight(g1) = 1
    c: Equal(g1,g2)
    c: InternalAlignment(g1,g3)
    c: InternalAlignment(g2,g3)
    c: InternalAlignment(g4,g3)
    c: InternalAlignment(g5,g3)
    c: Block(g3)
    c: Coincident(g6,g0)
    c: Coincident(g6,g3)
    c: Horizontal(g6)
FEATURE [Part::Extrusion] Extrude036  label="caseScrewPillarBracket014"
  Base = -> Sketch045
  Dir = (0,0,1)
  DirMode = 2
  FaceMakerClass = Part::FaceMakerBullseye
  LengthFwd = 2.4
  LengthRev = 0
  Placement = pos=(110.7,29,6.77) rot=(0,-1,0;1.5708rad)
  Solid = true
  Symmetric = false
FEATURE [Part::Extrusion] Extrude037  label="caseScrewPillarBracket015"
  Base = -> Sketch046
  Dir = (0,0,1)
  DirMode = 2
  FaceMakerClass = Part::FaceMakerBullseye
  LengthFwd = 2.4
  LengthRev = 0
  Placement = pos=(108.3,29,65.23) rot=(0,1,0;1.5708rad)
  Solid = true
  Symmetric = false
FEATURE [Part::Box] Box013  label="frontCaseScrewPillarBracket002"
  AttacherType = Attacher::AttachEngine3D
  Height = 2.4
  Length = 22
  Placement = pos=(87,28,2.3) rot=(0,0,1;0rad)
  Width = 7
FEATURE [Part::Box] Box014  label="frontCaseScrewPillarBracket003"
  AttacherType = Attacher::AttachEngine3D
  Height = 2.4
  Length = 22
  Placement = pos=(87,28,67.3) rot=(0,0,1;0rad)
  Width = 7
FEATURE [Part::Feature] Face087
  shape: bbox 4.8 x 30.2 x 2e-07 mm, 1 faces, 0 solids (baked)
FEATURE [Part::Revolution] Revolve091  label="frontCaseScrewPost004"
  Angle = 360
  Axis = (0,1,0)
  Base = (0,0,0)
  FaceMakerClass = Part::FaceMakerBullseye
  Placement = pos=(89.5,4.5,3.5) rot=(0,0,1;0rad)
  Solid = false
  Source = -> Face087
  Symmetric = false
FEATURE [Part::Feature] Face088
  shape: bbox 4.8 x 30.2 x 2e-07 mm, 1 faces, 0 solids (baked)
FEATURE [Part::Revolution] Revolve092  label="frontCaseScrewPost005"
  Angle = 360
  Axis = (0,1,0)
  Base = (0,0,0)
  FaceMakerClass = Part::FaceMakerBullseye
  Placement = pos=(89.5,4.5,68.5) rot=(0,0,1;0rad)
  Solid = false
  Source = -> Face088
  Symmetric = false
FEATURE [Part::Feature] Face089
  shape: bbox 3.5 x 30.2 x 2e-07 mm, 1 faces, 0 solids (baked)
FEATURE [Part::Revolution] Revolve093  label="backCaseScrewPost002"
  Angle = 360
  Axis = (0,1,0)
  Base = (0,0,0)
  FaceMakerClass = Part::FaceMakerBullseye
  Placement = pos=(12.5,4.5,10) rot=(0,0,1;0rad)
  Solid = false
  Source = -> Face089
  Symmetric = false
FEATURE [Part::Feature] Face090
  shape: bbox 3.5 x 30.2 x 2e-07 mm, 1 faces, 0 solids (baked)
FEATURE [Part::Revolution] Revolve094  label="backCaseScrewPost003"
  Angle = 360
  Axis = (0,1,0)
  Base = (0,0,0)
  FaceMakerClass = Part::FaceMakerBullseye
  Placement = pos=(12.5,4.5,62) rot=(0,0,1;0rad)
  Solid = false
  Source = -> Face090
  Symmetric = false
FEATURE [Part::Box] Box015  label="Cube011"
  AttacherType = Attacher::AttachEngine3D
  Height = 28.8
  Length = 3
  Placement = pos=(107.3,28,21.6) rot=(0,0,1;0rad)
  Width = 7
FEATURE [Part::Box] Box016  label="Cube012"
  AttacherType = Attacher::AttachEngine3D
  Height = 3
  Length = 7.4
  Placement = pos=(107.3,28,18.6) rot=(0,0,1;0rad)
  Width = 7
FEATURE [Part::Box] Box017  label="Cube013"
  AttacherType = Attacher::AttachEngine3D
  Height = 3
  Length = 7.4
  Placement = pos=(107.3,28,50.4) rot=(0,0,1;0rad)
  Width = 7
FEATURE [Part::Cylinder] Cylinder024
  Angle = 360
  AttacherType = Attacher::AttachEngine3D
  Height = 20
  Placement = pos=(0,0,36.15) rot=(0,0,1;0rad)
  Radius = 14.3
FEATURE [Part::Cylinder] Cylinder025
  Angle = 360
  AttacherType = Attacher::AttachEngine3D
  Height = 10
  Placement = pos=(0,0,36.15) rot=(0,0,1;0rad)
  Radius = 4
FEATURE [Part::MultiFuse] Fusion066  label="removeToCreteHoleForPlugHousing009"
  Placement = pos=(70,19,36) rot=(0,1,0;1.5708rad)
  Shapes = -> [Cylinder024,Cylinder025]
FEATURE [Part::MultiFuse] Fusion065  label="plugHousingBracketHolder002"
  Shapes = -> [Box017,Box015,Box016]
FEATURE [Part::Cut] Cut025  label="plugHousingBracketHolder003"
  Base = -> Fusion065
  Placement = pos=(7,0,0) rot=(0,0,1;0rad)
  Tool = -> Fusion066
FEATURE [Sketcher::SketchObject] Sketch047
  FullyConstrained = false
  Placement = pos=(0,0,0) rot=(1,0,0;1.5708rad)
  sketch-geometry (24):
    g0: ArcOfCircle CenterX=-4 CenterY=-10.5 CenterZ=0 NormalX=0 NormalY=0 NormalZ=1 AngleXU=0 Radius=1.5 StartAngle=6e-16 EndAngle=3.14159
    g1: ArcOfCircle CenterX=-34.2 CenterY=-10.5 CenterZ=0 NormalX=0 NormalY=0 NormalZ=1 AngleXU=0 Radius=1.5 StartAngle=0 EndAngle=3.14159
    g2: ArcOfCircle CenterX=-34.2 CenterY=-27.7 CenterZ=0 NormalX=0 NormalY=0 NormalZ=1 AngleXU=0 Radius=1.5 StartAngle=3.14159 EndAngle=6.28319
    g3: ArcOfCircle CenterX=-4 CenterY=-27.7 CenterZ=0 NormalX=0 NormalY=0 NormalZ=1 AngleXU=0 Radius=1.5 StartAngle=3.1416 EndAngle=6.28319
    g4: ArcOfCircle CenterX=-10 CenterY=-4.3 CenterZ=0 NormalX=0 NormalY=0 NormalZ=1 AngleXU=0 Radius=1.5 StartAngle=2e-16 EndAngle=3.14159
    g5: ArcOfCircle CenterX=-16.1 CenterY=-1.8 CenterZ=0 NormalX=0 NormalY=0 NormalZ=1 AngleXU=0 Radius=1.5 StartAngle=5e-16 EndAngle=3.14159
    g6: ArcOfCircle CenterX=-22.1 CenterY=-1.8 CenterZ=0 NormalX=0 NormalY=0 NormalZ=1 AngleXU=0 Radius=1.5 StartAngle=5e-16 EndAngle=3.14159
    g7: ArcOfCircle CenterX=-28.2 CenterY=-4.3 CenterZ=0 NormalX=0 NormalY=0 NormalZ=1 AngleXU=0 Radius=1.5 StartAngle=2e-16 EndAngle=3.14159
    g8: ArcOfCircle CenterX=-10 CenterY=-33.9 CenterZ=0 NormalX=0 NormalY=0 NormalZ=1 AngleXU=0 Radius=1.5 StartAngle=3.14159 EndAngle=6.28319
    g9: ArcOfCircle CenterX=-16.1 CenterY=-36.4 CenterZ=0 NormalX=0 NormalY=0 NormalZ=1 AngleXU=0 Radius=1.5 StartAngle=3.14159 EndAngle=6.28319
    g10: ArcOfCircle CenterX=-22.1 CenterY=-36.4 CenterZ=0 NormalX=0 NormalY=0 NormalZ=1 AngleXU=0 Radius=1.5 StartAngle=3.14159 EndAngle=6.28319
    g11: ArcOfCircle CenterX=-28.2 CenterY=-33.9 CenterZ=0 NormalX=0 NormalY=0 NormalZ=1 AngleXU=0 Radius=1.5 StartAngle=3.14159 EndAngle=6.28319
    g12: LineSegment StartX=-35.7 StartY=-10.5 StartZ=0 EndX=-35.7 EndY=-27.7 EndZ=0
    g13: LineSegment StartX=-32.7 StartY=-10.5 StartZ=0 EndX=-32.7 EndY=-27.7 EndZ=0
    g14: LineSegment StartX=-29.7 StartY=-33.9 StartZ=0 EndX=-29.7 EndY=-4.3 EndZ=0
    g15: LineSegment StartX=-26.7 StartY=-33.9 StartZ=0 EndX=-26.7 EndY=-4.3 EndZ=0
    g16: LineSegment StartX=-2.5 StartY=-10.5 StartZ=0 EndX=-2.5 EndY=-27.7 EndZ=0
    g17: LineSegment StartX=-8.5 StartY=-4.3 StartZ=0 EndX=-8.5 EndY=-33.9 EndZ=0
    g18: LineSegment StartX=-5.5 StartY=-10.5 StartZ=0 EndX=-5.5 EndY=-27.7 EndZ=0
    g19: LineSegment StartX=-11.5 StartY=-4.3 StartZ=0 EndX=-11.5 EndY=-33.9 EndZ=0
    g20: LineSegment StartX=-14.6 StartY=-1.8 StartZ=0 EndX=-14.6 EndY=-36.4 EndZ=0
    g21: LineSegment StartX=-17.6 StartY=-1.8 StartZ=0 EndX=-17.6 EndY=-36.4 EndZ=0
    g22: LineSegment StartX=-20.6 StartY=-36.4 StartZ=0 EndX=-20.6 EndY=-1.8 EndZ=0
    g23: LineSegment StartX=-23.6 StartY=-1.8 StartZ=0 EndX=-23.6 EndY=-36.4 EndZ=0
  constraints (48):
    c: Block(g0)
    c: Block(g1)
    c: Block(g2)
    c: Block(g3)
    c: Block(g4)
    c: Block(g5)
    c: Block(g6)
    c: Block(g7)
    c: Block(g8)
    c: Block(g9)
    c: Block(g10)
    c: Block(g11)
    c: Coincident(g12,g1)
    c: Coincident(g12,g2)
    c: Vertical(g12)
    c: Coincident(g13,g1)
    c: Coincident(g13,g2)
    c: Vertical(g13)
    c: Coincident(g14,g11)
    c: Coincident(g14,g7)
    c: Vertical(g14)
    c: Coincident(g15,g11)
    c: Coincident(g15,g7)
    c: Vertical(g15)
    c: Coincident(g16,g0)
    c: Coincident(g16,g3)
    c: Vertical(g16)
    c: Coincident(g17,g4)
    c: Coincident(g17,g8)
    c: Vertical(g17)
    c: Coincident(g18,g0)
    c: Coincident(g18,g3)
    c: Vertical(g18)
    c: Coincident(g19,g4)
    c: Coincident(g19,g8)
    c: Vertical(g19)
    c: Coincident(g20,g5)
    c: Coincident(g20,g9)
    c: Vertical(g20)
    c: Coincident(g21,g5)
    c: Coincident(g21,g9)
    c: Vertical(g21)
    c: Coincident(g22,g10)
    c: Coincident(g22,g6)
    c: Vertical(g22)
    c: Coincident(g23,g6)
    c: Coincident(g23,g10)
    c: Vertical(g23)
FEATURE [Part::Extrusion] Extrude038  label="removeToCreateFanGrillHoles001"
  Base = -> Sketch047
  Dir = (0,-1,6e-16)
  DirMode = 2
  FaceMakerClass = Part::FaceMakerBullseye
  LengthFwd = 10
  LengthRev = 0
  Placement = pos=(65.4,44,54.82) rot=(0,0,1;0rad)
  Solid = true
  Symmetric = false
FEATURE [Part::Feature] Wire004
  shape: bbox 11 x 5.2 x 2e-07 mm, 0 faces, 0 solids (baked)
FEATURE [Part::Revolution] Revolve095
  Angle = 360
  Axis = (0,1,0)
  Base = (0,0,0)
  FaceMakerClass = Part::FaceMakerBullseye
  Placement = pos=(30.3,38,19.7) rot=(0,0,1;0rad)
  Solid = true
  Source = -> Wire004
  Symmetric = false
FEATURE [Part::Feature] Wire005
  shape: bbox 11 x 5.2 x 2e-07 mm, 0 faces, 0 solids (baked)
FEATURE [Part::Revolution] Revolve096
  Angle = 360
  Axis = (0,1,0)
  Base = (0,0,0)
  FaceMakerClass = Part::FaceMakerBullseye
  Placement = pos=(30.3,38,51.7) rot=(0,0,1;0rad)
  Solid = true
  Source = -> Wire005
  Symmetric = false
FEATURE [Part::Feature] Wire006
  shape: bbox 11 x 5.2 x 2e-07 mm, 0 faces, 0 solids (baked)
FEATURE [Part::Revolution] Revolve097
  Angle = 360
  Axis = (0,1,0)
  Base = (0,0,0)
  FaceMakerClass = Part::FaceMakerBullseye
  Placement = pos=(62.3,38,51.7) rot=(0,0,1;0rad)
  Solid = true
  Source = -> Wire006
  Symmetric = false
FEATURE [Part::Feature] Wire007
  shape: bbox 11 x 5.2 x 2e-07 mm, 0 faces, 0 solids (baked)
FEATURE [Part::Revolution] Revolve098
  Angle = 360
  Axis = (0,1,0)
  Base = (0,0,0)
  FaceMakerClass = Part::FaceMakerBullseye
  Placement = pos=(62.3,38,19.7) rot=(0,0,1;0rad)
  Solid = true
  Source = -> Wire007
  Symmetric = false
FEATURE [Part::MultiFuse] Fusion067  label="fanScrewHousing002"
  Shapes = -> [Revolve098,Revolve097,Revolve096,Revolve095]
FEATURE [Part::Feature] Face091 .. Face094  x4 (patterned run collapsed; names and placements below)
  shape: bbox 3.5 x 17.8 x 2e-07 mm, 1 faces, 0 solids (baked)
FEATURE [Part::Revolution] Revolve099  label="removeToCreateScrewAndThreadedInsertHole026"
  Angle = 360
  Axis = (0,1,0)
  Base = (0,0,0)
  FaceMakerClass = Part::FaceMakerBullseye
  Placement = pos=(62.3,30.3,19.7) rot=(0,0,1;0rad)
  Solid = false
  Source = -> Face091
  Symmetric = false
FEATURE [Part::Revolution] Revolve100  label="removeToCreateScrewAndThreadedInsertHole027"
  Angle = 360
  Axis = (0,1,0)
  Base = (0,0,0)
  FaceMakerClass = Part::FaceMakerBullseye
  Placement = pos=(62.3,30.3,51.7) rot=(0,0,1;0rad)
  Solid = false
  Source = -> Face092
  Symmetric = false
FEATURE [Part::Revolution] Revolve101  label="removeToCreateScrewAndThreadedInsertHole028"
  Angle = 360
  Axis = (0,1,0)
  Base = (0,0,0)
  FaceMakerClass = Part::FaceMakerBullseye
  Placement = pos=(30.3,30.3,19.7) rot=(0,0,1;0rad)
  Solid = false
  Source = -> Face093
  Symmetric = false
FEATURE [Part::Revolution] Revolve102  label="removeToCreateScrewAndThreadedInsertHole029"
  Angle = 360
  Axis = (0,1,0)
  Base = (0,0,0)
  FaceMakerClass = Part::FaceMakerBullseye
  Placement = pos=(30.3,30.3,51.7) rot=(0,0,1;0rad)
  Solid = false
  Source = -> Face094
  Symmetric = false
FEATURE [Part::MultiFuse] Fusion068  label="createThreadedInsertHolesForFan002"
  Shapes = -> [Revolve099,Revolve100,Revolve101,Revolve102]
FEATURE [Part::Cut] Cut026  label="fanScrewHousing003"
  Base = -> Fusion067
  Tool = -> Fusion068
FEATURE [Sketcher::SketchObject] Sketch048
  FullyConstrained = false
  Placement = pos=(0,0,0) rot=(1,0,0;1.5708rad)
  sketch-geometry (24):
    g0: ArcOfCircle CenterX=-4 CenterY=-10.5 CenterZ=0 NormalX=0 NormalY=0 NormalZ=1 AngleXU=0 Radius=1.5 StartAngle=6e-16 EndAngle=3.14159
    g1: ArcOfCircle CenterX=-34.2 CenterY=-10.5 CenterZ=0 NormalX=0 NormalY=0 NormalZ=1 AngleXU=0 Radius=1.5 StartAngle=0 EndAngle=3.14159
    g2: ArcOfCircle CenterX=-34.2 CenterY=-27.7 CenterZ=0 NormalX=0 NormalY=0 NormalZ=1 AngleXU=0 Radius=1.5 StartAngle=3.14159 EndAngle=6.28319
    g3: ArcOfCircle CenterX=-4 CenterY=-27.7 CenterZ=0 NormalX=0 NormalY=0 NormalZ=1 AngleXU=0 Radius=1.5 StartAngle=3.1416 EndAngle=6.28319
    g4: ArcOfCircle CenterX=-10 CenterY=-4.3 CenterZ=0 NormalX=0 NormalY=0 NormalZ=1 AngleXU=0 Radius=1.5 StartAngle=2e-16 EndAngle=3.14159
    g5: ArcOfCircle CenterX=-16.1 CenterY=-1.8 CenterZ=0 NormalX=0 NormalY=0 NormalZ=1 AngleXU=0 Radius=1.5 StartAngle=5e-16 EndAngle=3.14159
    g6: ArcOfCircle CenterX=-22.1 CenterY=-1.8 CenterZ=0 NormalX=0 NormalY=0 NormalZ=1 AngleXU=0 Radius=1.5 StartAngle=5e-16 EndAngle=3.14159
    g7: ArcOfCircle CenterX=-28.2 CenterY=-4.3 CenterZ=0 NormalX=0 NormalY=0 NormalZ=1 AngleXU=0 Radius=1.5 StartAngle=2e-16 EndAngle=3.14159
    g8: ArcOfCircle CenterX=-10 CenterY=-33.9 CenterZ=0 NormalX=0 NormalY=0 NormalZ=1 AngleXU=0 Radius=1.5 StartAngle=3.14159 EndAngle=6.28319
    g9: ArcOfCircle CenterX=-16.1 CenterY=-36.4 CenterZ=0 NormalX=0 NormalY=0 NormalZ=1 AngleXU=0 Radius=1.5 StartAngle=3.14159 EndAngle=6.28319
    g10: ArcOfCircle CenterX=-22.1 CenterY=-36.4 CenterZ=0 NormalX=0 NormalY=0 NormalZ=1 AngleXU=0 Radius=1.5 StartAngle=3.14159 EndAngle=6.28319
    g11: ArcOfCircle CenterX=-28.2 CenterY=-33.9 CenterZ=0 NormalX=0 NormalY=0 NormalZ=1 AngleXU=0 Radius=1.5 StartAngle=3.14159 EndAngle=6.28319
    g12: LineSegment StartX=-35.7 StartY=-10.5 StartZ=0 EndX=-35.7 EndY=-27.7 EndZ=0
    g13: LineSegment StartX=-32.7 StartY=-10.5 StartZ=0 EndX=-32.7 EndY=-27.7 EndZ=0
    g14: LineSegment StartX=-29.7 StartY=-33.9 StartZ=0 EndX=-29.7 EndY=-4.3 EndZ=0
    g15: LineSegment StartX=-26.7 StartY=-33.9 StartZ=0 EndX=-26.7 EndY=-4.3 EndZ=0
    g16: LineSegment StartX=-2.5 StartY=-10.5 StartZ=0 EndX=-2.5 EndY=-27.7 EndZ=0
    g17: LineSegment StartX=-8.5 StartY=-4.3 StartZ=0 EndX=-8.5 EndY=-33.9 EndZ=0
    g18: LineSegment StartX=-5.5 StartY=-10.5 StartZ=0 EndX=-5.5 EndY=-27.7 EndZ=0
    g19: LineSegment StartX=-11.5 StartY=-4.3 StartZ=0 EndX=-11.5 EndY=-33.9 EndZ=0
    g20: LineSegment StartX=-14.6 StartY=-1.8 StartZ=0 EndX=-14.6 EndY=-36.4 EndZ=0
    g21: LineSegment StartX=-17.6 StartY=-1.8 StartZ=0 EndX=-17.6 EndY=-36.4 EndZ=0
    g22: LineSegment StartX=-20.6 StartY=-36.4 StartZ=0 EndX=-20.6 EndY=-1.8 EndZ=0
    g23: LineSegment StartX=-23.6 StartY=-1.8 StartZ=0 EndX=-23.6 EndY=-36.4 EndZ=0
  constraints (48):
    c: Block(g0)
    c: Block(g1)
    c: Block(g2)
    c: Block(g3)
    c: Block(g4)
    c: Block(g5)
    c: Block(g6)
    c: Block(g7)
    c: Block(g8)
    c: Block(g9)
    c: Block(g10)
    c: Block(g11)
    c: Coincident(g12,g1)
    c: Coincident(g12,g2)
    c: Vertical(g12)
    c: Coincident(g13,g1)
    c: Coincident(g13,g2)
    c: Vertical(g13)
    c: Coincident(g14,g11)
    c: Coincident(g14,g7)
    c: Vertical(g14)
    c: Coincident(g15,g11)
    c: Coincident(g15,g7)
    c: Vertical(g15)
    c: Coincident(g16,g0)
    c: Coincident(g16,g3)
    c: Vertical(g16)
    c: Coincident(g17,g4)
    c: Coincident(g17,g8)
    c: Vertical(g17)
    c: Coincident(g18,g0)
    c: Coincident(g18,g3)
    c: Vertical(g18)
    c: Coincident(g19,g4)
    c: Coincident(g19,g8)
    c: Vertical(g19)
    c: Coincident(g20,g5)
    c: Coincident(g20,g9)
    c: Vertical(g20)
    c: Coincident(g21,g5)
    c: Coincident(g21,g9)
    c: Vertical(g21)
    c: Coincident(g22,g10)
    c: Coincident(g22,g6)
    c: Vertical(g22)
    c: Coincident(g23,g6)
    c: Coincident(g23,g10)
    c: Vertical(g23)
FEATURE [Part::Extrusion] Extrude039  label="removeToCreateFanGrillHoles002"
  Base = -> Sketch048
  Dir = (0,-1,6e-16)
  DirMode = 2
  FaceMakerClass = Part::FaceMakerBullseye
  LengthFwd = 10
  LengthRev = 0
  Placement = pos=(65.4,44,54.82) rot=(0,0,1;0rad)
  Solid = true
  Symmetric = false
FEATURE [Part::Cut] Cut027  label="fanScrewHousing004"
  Base = -> Cut026
  Tool = -> Extrude038
FEATURE [Part::Cut] Cut028  label="top014"
  Base = -> Fillet026
  Tool = -> Extrude039
FEATURE [Part::Feature] Face095 .. Face098  x4 (patterned run collapsed; names and placements below)
  shape: bbox 3.5 x 17.8 x 2e-07 mm, 1 faces, 0 solids (baked)
FEATURE [Part::Revolution] Revolve103  label="removeToCreateScrewAndThreadedInsertHole030"
  Angle = 360
  Axis = (0,1,0)
  Base = (0,0,0)
  FaceMakerClass = Part::FaceMakerBullseye
  Placement = pos=(62.3,30.3,19.7) rot=(0,0,1;0rad)
  Solid = false
  Source = -> Face095
  Symmetric = false
FEATURE [Part::Revolution] Revolve104  label="removeToCreateScrewAndThreadedInsertHole031"
  Angle = 360
  Axis = (0,1,0)
  Base = (0,0,0)
  FaceMakerClass = Part::FaceMakerBullseye
  Placement = pos=(62.3,30.3,51.7) rot=(0,0,1;0rad)
  Solid = false
  Source = -> Face096
  Symmetric = false
FEATURE [Part::Revolution] Revolve105  label="removeToCreateScrewAndThreadedInsertHole032"
  Angle = 360
  Axis = (0,1,0)
  Base = (0,0,0)
  FaceMakerClass = Part::FaceMakerBullseye
  Placement = pos=(30.3,30.3,19.7) rot=(0,0,1;0rad)
  Solid = false
  Source = -> Face097
  Symmetric = false
FEATURE [Part::Revolution] Revolve106  label="removeToCreateScrewAndThreadedInsertHole033"
  Angle = 360
  Axis = (0,1,0)
  Base = (0,0,0)
  FaceMakerClass = Part::FaceMakerBullseye
  Placement = pos=(30.3,30.3,51.7) rot=(0,0,1;0rad)
  Solid = false
  Source = -> Face098
  Symmetric = false
FEATURE [Part::MultiFuse] Fusion069  label="createThreadedInsertHolesForFan003"
  Shapes = -> [Revolve103,Revolve104,Revolve105,Revolve106]
FEATURE [Part::Cut] Cut029  label="top015"
  Base = -> Cut028
  Tool = -> Fusion054
FEATURE [Part::Cut] Cut030  label="fanScrewHousing005"
  Base = -> Cut027
  Tool = -> Fusion069
FEATURE [Part::Cylinder] Cylinder026  label="removeToCreteHoleForPlugHousing010"
  Angle = 360
  AttacherType = Attacher::AttachEngine3D
  Height = 20
  Placement = pos=(-2,19,36) rot=(0,1,0;1.5708rad)
  Radius = 14.3
FEATURE [Part::Box] Box018  label="removeToCreteHoleForPlugHousing011"
  AttacherType = Attacher::AttachEngine3D
  Height = 28.6
  Length = 10
  Placement = pos=(-2,0,21.7) rot=(0,0,1;0rad)
  Width = 19
FEATURE [Part::Box] Box019  label="wireHolderBottomCaseBit"
  AttacherType = Attacher::AttachEngine3D
  Height = 28
  Length = 3
  Placement = pos=(0,0,22) rot=(0,0,1;0rad)
  Width = 21
FEATURE [Part::Cylinder] Cylinder027  label="removeToCreteHoleForPlugHousing012"
  Angle = 360
  AttacherType = Attacher::AttachEngine3D
  Height = 20
  Placement = pos=(-2,19,36) rot=(0,1,0;1.5708rad)
  Radius = 14.3
FEATURE [Part::Cut] Cut031  label="wireHolderBottomCaseBit001"
  Base = -> Box019
  Tool = -> Cylinder027
FEATURE [Part::MultiFuse] Fusion070  label="removeToCreteHoleForPlugHousing013"
  Shapes = -> [Box018,Cylinder026]
FEATURE [Part::Cut] Cut032  label="top016"
  Base = -> Cut029
  Tool = -> Fusion070
FEATURE [Part::Cylinder] Cylinder028
  Angle = 360
  AttacherType = Attacher::AttachEngine3D
  Height = 20
  Placement = pos=(0,0,36.15) rot=(0,0,1;0rad)
  Radius = 14.3
FEATURE [Part::Cylinder] Cylinder029
  Angle = 360
  AttacherType = Attacher::AttachEngine3D
  Height = 10
  Placement = pos=(0,0,36.15) rot=(0,0,1;0rad)
  Radius = 4
FEATURE [Part::MultiFuse] Fusion071  label="removeToCreteHoleForPlugHousing014"
  Placement = pos=(70,19,36) rot=(0,1,0;1.5708rad)
  Shapes = -> [Cylinder028,Cylinder029]
FEATURE [Sketcher::SketchObject] Sketch049  label="topSketch011"
  FullyConstrained = true
  sketch-geometry (4):
    g0: ArcOfCircle CenterX=105 CenterY=19 CenterZ=0 NormalX=0 NormalY=0 NormalZ=1 AngleXU=0 Radius=20.6155 StartAngle=5.54125 EndAngle=6.28319
    g1: ArcOfCircle CenterX=105 CenterY=19 CenterZ=0 NormalX=0 NormalY=0 NormalZ=1 AngleXU=0 Radius=13 StartAngle=5.54125 EndAngle=6.28319
    g2: LineSegment StartX=118 StartY=19 StartZ=0 EndX=125.616 EndY=19 EndZ=0
    g3: LineSegment StartX=114.583 StartY=10.2157 StartZ=0 EndX=120.197 EndY=5.06982 EndZ=0
  constraints (7):
    c: Block(g0)
    c: Block(g1)
    c: Coincident(g2,g1)
    c: Coincident(g2,g0)
    c: Horizontal(g2)
    c: Coincident(g3,g1)
    c: Coincident(g3,g0)
FEATURE [Part::Box] Box020  label="removeToCreteHoleForPlugHousing015"
  AttacherType = Attacher::AttachEngine3D
  Height = 28.6
  Length = 20
  Placement = pos=(106.15,0,21.7) rot=(0,0,1;0rad)
  Width = 19
FEATURE [Part::MultiFuse] Fusion072  label="removeToCreteHoleForPlugHousing016"
  Shapes = -> [Box020,Fusion071]
FEATURE [Part::Cut] Cut033  label="removeToCreteHoleForPlugHousing017"
  Base = -> Cut032
  Tool = -> Fusion072
FEATURE [Part::Cylinder] Cylinder030
  Angle = 360
  AttacherType = Attacher::AttachEngine3D
  Height = 20
  Placement = pos=(0,0,36.15) rot=(0,0,1;0rad)
  Radius = 14.3
FEATURE [Part::Cylinder] Cylinder031
  Angle = 360
  AttacherType = Attacher::AttachEngine3D
  Height = 10
  Placement = pos=(0,0,36.15) rot=(0,0,1;0rad)
  Radius = 4
FEATURE [Part::Box] Box021  label="removeToCreteHoleForPlugHousing019"
  AttacherType = Attacher::AttachEngine3D
  Height = 28.6
  Length = 20
  Placement = pos=(106.15,0,21.7) rot=(0,0,1;0rad)
  Width = 19
FEATURE [Part::MultiFuse] Fusion074  label="removeToCreteHoleForPlugHousing020"
  Placement = pos=(70,19,36) rot=(0,1,0;1.5708rad)
  Shapes = -> [Cylinder030,Cylinder031]
FEATURE [Part::MultiFuse] Fusion073  label="removeToCreteHoleForPlugHousing018"
  Placement = pos=(0,0,28.3) rot=(0,0,1;0rad)
  Shapes = -> [Box021,Fusion074]
FEATURE [Part::Cylinder] Cylinder032
  Angle = 360
  AttacherType = Attacher::AttachEngine3D
  Height = 20
  Placement = pos=(0,0,36.15) rot=(0,0,1;0rad)
  Radius = 14.3
FEATURE [Part::Cylinder] Cylinder033
  Angle = 360
  AttacherType = Attacher::AttachEngine3D
  Height = 10
  Placement = pos=(0,0,36.15) rot=(0,0,1;0rad)
  Radius = 4
FEATURE [Part::Box] Box022  label="removeToCreteHoleForPlugHousing021"
  AttacherType = Attacher::AttachEngine3D
  Height = 28.6
  Length = 20
  Placement = pos=(106.15,0,21.7) rot=(0,0,1;0rad)
  Width = 19
FEATURE [Part::MultiFuse] Fusion076  label="removeToCreteHoleForPlugHousing023"
  Placement = pos=(70,19,36) rot=(0,1,0;1.5708rad)
  Shapes = -> [Cylinder032,Cylinder033]
FEATURE [Part::MultiFuse] Fusion075  label="removeToCreteHoleForPlugHousing022"
  Placement = pos=(0,0,-28.3) rot=(0,0,1;0rad)
  Shapes = -> [Box022,Fusion076]
FEATURE [Part::MultiFuse] Fusion077  label="removeToCreatePlugHousingBottomBit"
  Shapes = -> [Fusion075,Fusion073]
FEATURE [Part::Cylinder] Cylinder034
  Angle = 360
  AttacherType = Attacher::AttachEngine3D
  Height = 20
  Placement = pos=(0,0,36.15) rot=(0,0,1;0rad)
  Radius = 14
FEATURE [Part::Cylinder] Cylinder035
  Angle = 360
  AttacherType = Attacher::AttachEngine3D
  Height = 10
  Placement = pos=(0,0,36.15) rot=(0,0,1;0rad)
  Radius = 4
FEATURE [Part::MultiFuse] Fusion078  label="removeToCreteHoleForPlugHousing024"
  Placement = pos=(70,19,36) rot=(0,1,0;1.5708rad)
  Shapes = -> [Cylinder034,Cylinder035]
FEATURE [Part::MultiFuse] Fusion079  label="removeToCreatePlugHousingBottomBit001"
  Shapes = -> [Fusion078,Fusion077]
FEATURE [Part::Extrusion] Extrude040  label="bottomPlugHousingBit"
  Base = -> Sketch049
  Dir = (0,0,1)
  DirMode = 2
  FaceMakerClass = Part::FaceMakerBullseye
  LengthFwd = 72
  LengthRev = 0
  Solid = true
  Symmetric = false
FEATURE [Part::Cut] Cut034  label="bottomPlugHousingBit001"
  Base = -> Extrude040
  Placement = pos=(-0.09,0,0) rot=(0,0,1;0rad)
  Tool = -> Fusion079
FEATURE [Part::Box] Box023  label="Cube014"
  AttacherType = Attacher::AttachEngine3D
  Height = 16
  Length = 8
  Placement = pos=(12.7,31.52,28) rot=(0,0,1;0rad)
  Width = 4
FEATURE [Part::Cylinder] Cylinder036
  Angle = 360
  AttacherType = Attacher::AttachEngine3D
  Height = 10
  Placement = pos=(0,0,36.15) rot=(0,0,1;0rad)
  Radius = 4
FEATURE [Part::Cylinder] Cylinder037
  Angle = 360
  AttacherType = Attacher::AttachEngine3D
  Height = 20
  Placement = pos=(0,0,36.15) rot=(0,0,1;0rad)
  Radius = 8.2
FEATURE [Part::MultiFuse] Fusion080  label="removeToCreteHoleForPlugHousing025"
  Placement = pos=(-42,19,36) rot=(0,1,0;1.5708rad)
  Shapes = -> [Cylinder037,Cylinder036]
FEATURE [Sketcher::SketchObject] Sketch050  label="topSketch012"
  FullyConstrained = true
  sketch-geometry (4):
    g0: LineSegment StartX=16.8446 StartY=31.512 StartZ=0 EndX=16.3251 EndY=34.4666 EndZ=0
    g1: ArcOfCircle CenterX=19 CenterY=19.2524 CenterZ=0 NormalX=0 NormalY=0 NormalZ=1 AngleXU=0 Radius=15.4476 StartAngle=1.74483 EndAngle=2.72717
    g2: ArcOfCircle CenterX=19 CenterY=19.2524 CenterZ=0 NormalX=0 NormalY=0 NormalZ=1 AngleXU=0 Radius=12.4476 StartAngle=1.74483 EndAngle=2.73189
    g3: LineSegment StartX=4.86004 StartY=25.4725 StartZ=0 EndX=7.58253 EndY=24.2107 EndZ=0
  constraints (7):
    c: Block(g0)
    c: Coincident(g1,g0)
    c: Coincident(g2,g0)
    c: Coincident(g3,g1)
    c: Coincident(g3,g2)
    c: Block(g1)
    c: Block(g2)
FEATURE [Part::Extrusion] Extrude041
  Base = -> Sketch050
  Dir = (0,0,1)
  DirMode = 2
  FaceMakerClass = Part::FaceMakerBullseye
  LengthFwd = 10.6
  LengthRev = 0
  Placement = pos=(0,0,31) rot=(0,0,1;0rad)
  Solid = true
  Symmetric = false
FEATURE [Part::Cut] Cut035
  Base = -> Extrude041
  Placement = pos=(0,0,-0.3) rot=(0,0,1;0rad)
  Tool = -> Fusion080
FEATURE [Part::Cut] Cut036
  Base = -> Box023
  Tool = -> Cut035
FEATURE [Part::Fillet] Fillet027
  Base = -> Cut036
  Edges = 1 edges r=0.7: [Edge13]
FEATURE [Part::Fillet] Fillet028
  Base = -> Fillet027
  Edges = 1 edges r=0.7: [Edge13]
FEATURE [Part::Fillet] Fillet029
  Base = -> Fillet028
  Edges = 1 edges r=0.7: [Edge16]
FEATURE [Part::Fillet] Fillet030
  Base = -> Fillet029
  Edges = 1 edges r=0.7: [Edge11]
FEATURE [Part::Fillet] Fillet031
  Base = -> Fillet030
  Edges = 1 edges r=0.7: [Edge10]
FEATURE [Part::Fillet] Fillet032
  Base = -> Fillet031
  Edges = 1 edges r=1.2: [Edge5]
FEATURE [Part::Fillet] Fillet033
  Base = -> Fillet032
  Edges = 1 edges r=1.2: [Edge12]
FEATURE [Part::Fillet] Fillet034  label="wireHousingRetainer"
  Base = -> Fillet033
  Edges = 1 edges r=2: [Edge1]
  Placement = pos=(0.3,0,0) rot=(0,0,1;0rad)
FEATURE [Part::Feature] Face099
  shape: bbox 3.5 x 17.8 x 2e-07 mm, 1 faces, 0 solids (baked)
FEATURE [Part::Revolution] Revolve107  label="removeToCreateScrewAndThreadedInsertHole034"
  Angle = 360
  Axis = (0,1,0)
  Base = (0,0,0)
  FaceMakerClass = Part::FaceMakerBullseye
  Placement = pos=(12.5,0,10) rot=(0,0,1;0rad)
  Solid = false
  Source = -> Face099
  Symmetric = false
FEATURE [Part::Feature] Face100
  shape: bbox 3.5 x 17.8 x 2e-07 mm, 1 faces, 0 solids (baked)
FEATURE [Part::Revolution] Revolve108  label="removeToCreateScrewAndThreadedInsertHole035"
  Angle = 360
  Axis = (0,1,0)
  Base = (0,0,0)
  FaceMakerClass = Part::FaceMakerBullseye
  Placement = pos=(12.5,0,62) rot=(0,0,1;0rad)
  Solid = false
  Source = -> Face100
  Symmetric = false
FEATURE [Part::Feature] Face101
  shape: bbox 3.5 x 17.8 x 2e-07 mm, 1 faces, 0 solids (baked)
FEATURE [Part::Revolution] Revolve109  label="removeToCreateScrewAndThreadedInsertHole036"
  Angle = 360
  Axis = (0,1,0)
  Base = (0,0,0)
  FaceMakerClass = Part::FaceMakerBullseye
  Placement = pos=(89.5,0,68.5) rot=(0,0,1;0rad)
  Solid = false
  Source = -> Face101
  Symmetric = false
FEATURE [Part::Feature] Face102
  shape: bbox 3.5 x 17.8 x 2e-07 mm, 1 faces, 0 solids (baked)
FEATURE [Part::Revolution] Revolve110  label="removeToCreateScrewAndThreadedInsertHole037"
  Angle = 360
  Axis = (0,1,0)
  Base = (0,0,0)
  FaceMakerClass = Part::FaceMakerBullseye
  Placement = pos=(89.5,0,3.5) rot=(0,0,1;0rad)
  Solid = false
  Source = -> Face102
  Symmetric = false
FEATURE [Part::Feature] Face103
  shape: bbox 3.5 x 17.8 x 2e-07 mm, 1 faces, 0 solids (baked)
FEATURE [Part::Revolution] Revolve111  label="removeToCreateScrewAndThreadedInsertHole038"
  Angle = 360
  Axis = (0,1,0)
  Base = (0,0,0)
  FaceMakerClass = Part::FaceMakerBullseye
  Placement = pos=(109.5,4.7,3.5) rot=(0,0,1;0rad)
  Solid = false
  Source = -> Face103
  Symmetric = false
FEATURE [Part::Feature] Face104
  shape: bbox 3.5 x 17.8 x 2e-07 mm, 1 faces, 0 solids (baked)
FEATURE [Part::Revolution] Revolve112  label="removeToCreateScrewAndThreadedInsertHole039"
  Angle = 360
  Axis = (0,1,0)
  Base = (0,0,0)
  FaceMakerClass = Part::FaceMakerBullseye
  Placement = pos=(109.5,4.7,68.5) rot=(0,0,1;0rad)
  Solid = false
  Source = -> Face104
  Symmetric = false
FEATURE [Part::MultiFuse] Fusion081  label="removeToCreateScrewAndThreadedInsertHole040"
  Shapes = -> [Revolve107,Revolve108,Revolve109,Revolve110,Revolve111,Revolve112]
FEATURE [Part::MultiFuse] Fusion082  label="casePillars002"
  Shapes = -> [Revolve094,Revolve092,Revolve090,Revolve089,Revolve091,Revolve093]
FEATURE [Part::Cut] Cut037  label="casePillars003"
  Base = -> Fusion082
  Tool = -> Fusion081
FEATURE [Sketcher::SketchObject] Sketch051
  FullyConstrained = true
  Placement = pos=(117,19,0) rot=(0.57735,0.57735,0.57735;2.0944rad)
  sketch-geometry (48):
    g0: LineSegment StartX=-49.19 StartY=69.25 StartZ=0 EndX=-49.19 EndY=66.25 EndZ=0
    g1: LineSegment StartX=-49.19 StartY=63.5 StartZ=0 EndX=-49.19 EndY=60.5 EndZ=0
    g2: LineSegment StartX=-49.19 StartY=57.75 StartZ=0 EndX=-49.19 EndY=54.75 EndZ=0
    g3: LineSegment StartX=-49.19 StartY=52 StartZ=0 EndX=-49.19 EndY=49 EndZ=0
    g4: LineSegment StartX=-49.19 StartY=46.25 StartZ=0 EndX=-49.19 EndY=43.25 EndZ=0
    g5: LineSegment StartX=-49.19 StartY=40.5 StartZ=0 EndX=-49.19 EndY=37.5 EndZ=0
    g6: LineSegment StartX=-49.19 StartY=34.5 StartZ=0 EndX=-49.19 EndY=31.5 EndZ=0
    g7: LineSegment StartX=-49.19 StartY=28.75 StartZ=0 EndX=-49.19 EndY=25.75 EndZ=0
    g8: LineSegment StartX=-49.19 StartY=23 StartZ=0 EndX=-49.19 EndY=20 EndZ=0
    g9: LineSegment StartX=-49.19 StartY=17.25 StartZ=0 EndX=-49.19 EndY=14.25 EndZ=0
    g10: LineSegment StartX=-49.19 StartY=11.5 StartZ=0 EndX=-49.19 EndY=8.5 EndZ=0
    g11: LineSegment StartX=-49.19 StartY=5.75 StartZ=0 EndX=-49.19 EndY=2.75 EndZ=0
    g12: ArcOfCircle CenterX=-1.5 CenterY=67.75 CenterZ=0 NormalX=0 NormalY=0 NormalZ=1 AngleXU=0 Radius=1.5 StartAngle=4.71239 EndAngle=7.85398
    g13: ArcOfCircle CenterX=-1.5 CenterY=62 CenterZ=0 NormalX=0 NormalY=0 NormalZ=1 AngleXU=0 Radius=1.5 StartAngle=4.71239 EndAngle=7.85398
    g14: ArcOfCircle CenterX=-1.5 CenterY=56.25 CenterZ=0 NormalX=0 NormalY=0 NormalZ=1 AngleXU=0 Radius=1.5 StartAngle=4.71239 EndAngle=7.85398
    g15: ArcOfCircle CenterX=-11.49 CenterY=50.5 CenterZ=0 NormalX=0 NormalY=0 NormalZ=1 AngleXU=0 Radius=1.5 StartAngle=4.71239 EndAngle=7.85398
    g16: ArcOfCircle CenterX=-16.28 CenterY=44.75 CenterZ=0 NormalX=0 NormalY=0 NormalZ=1 AngleXU=0 Radius=1.5 StartAngle=4.71239 EndAngle=7.85398
    g17: ArcOfCircle CenterX=-18.2337 CenterY=39 CenterZ=0 NormalX=0 NormalY=0 NormalZ=1 AngleXU=0 Radius=1.5 StartAngle=4.71485 EndAngle=7.85398
    g18: ArcOfCircle CenterX=-16.2837 CenterY=27.25 CenterZ=0 NormalX=0 NormalY=0 NormalZ=1 AngleXU=0 Radius=1.5 StartAngle=4.71485 EndAngle=7.85398
    g19: ArcOfCircle CenterX=-18.2337 CenterY=33 CenterZ=0 NormalX=0 NormalY=0 NormalZ=1 AngleXU=0 Radius=1.5 StartAngle=4.71485 EndAngle=7.85398
    g20: ArcOfCircle CenterX=-11.49 CenterY=21.5 CenterZ=0 NormalX=0 NormalY=0 NormalZ=1 AngleXU=0 Radius=1.5 StartAngle=4.71239 EndAngle=7.85398
    g21: ArcOfCircle CenterX=-1.5 CenterY=4.25 CenterZ=0 NormalX=0 NormalY=0 NormalZ=1 AngleXU=0 Radius=1.5 StartAngle=4.71239 EndAngle=7.85398
    g22: ArcOfCircle CenterX=-1.5 CenterY=10 CenterZ=0 NormalX=0 NormalY=0 NormalZ=1 AngleXU=0 Radius=1.5 StartAngle=4.71239 EndAngle=7.85398
    g23: ArcOfCircle CenterX=-1.5 CenterY=15.75 CenterZ=0 NormalX=0 NormalY=0 NormalZ=1 AngleXU=0 Radius=1.5 StartAngle=4.71239 EndAngle=7.85398
    g24: LineSegment StartX=-49.19 StartY=69.25 StartZ=0 EndX=-1.5 EndY=69.25 EndZ=0
    g25: LineSegment StartX=-49.19 StartY=66.25 StartZ=0 EndX=-1.5 EndY=66.25 EndZ=0
    g26: LineSegment StartX=-49.19 StartY=63.5 StartZ=0 EndX=-1.5 EndY=63.5 EndZ=0
    g27: LineSegment StartX=-49.19 StartY=60.5 StartZ=0 EndX=-1.5 EndY=60.5 EndZ=0
    g28: LineSegment StartX=-49.19 StartY=57.75 StartZ=0 EndX=-1.5 EndY=57.75 EndZ=0
    g29: LineSegment StartX=-49.19 StartY=54.75 StartZ=0 EndX=-1.5 EndY=54.75 EndZ=0
    g30: LineSegment StartX=-49.19 StartY=52 StartZ=0 EndX=-11.49 EndY=52 EndZ=0
    g31: LineSegment StartX=-49.19 StartY=49 StartZ=0 EndX=-11.49 EndY=49 EndZ=0
    g32: LineSegment StartX=-49.19 StartY=46.25 StartZ=0 EndX=-16.28 EndY=46.25 EndZ=0
    g33: LineSegment StartX=-49.19 StartY=43.25 StartZ=0 EndX=-16.28 EndY=43.25 EndZ=0
    g34: LineSegment StartX=-49.19 StartY=40.5 StartZ=0 EndX=-18.2337 EndY=40.5 EndZ=0
    g35: LineSegment StartX=-49.19 StartY=37.5 StartZ=0 EndX=-18.23 EndY=37.5 EndZ=0
    g36: LineSegment StartX=-49.19 StartY=34.5 StartZ=0 EndX=-18.2337 EndY=34.5 EndZ=0
    g37: LineSegment StartX=-49.19 StartY=31.5 StartZ=0 EndX=-18.23 EndY=31.5 EndZ=0
    g38: LineSegment StartX=-49.19 StartY=28.75 StartZ=0 EndX=-16.2837 EndY=28.75 EndZ=0
    g39: LineSegment StartX=-49.19 StartY=25.75 StartZ=0 EndX=-16.28 EndY=25.75 EndZ=0
    g40: LineSegment StartX=-49.19 StartY=23 StartZ=0 EndX=-11.49 EndY=23 EndZ=0
    g41: LineSegment StartX=-49.19 StartY=20 StartZ=0 EndX=-11.49 EndY=20 EndZ=0
    g42: LineSegment StartX=-49.19 StartY=17.25 StartZ=0 EndX=-1.5 EndY=17.25 EndZ=0
    g43: LineSegment StartX=-49.19 StartY=14.25 StartZ=0 EndX=-1.5 EndY=14.25 EndZ=0
    g44: LineSegment StartX=-49.19 StartY=11.5 StartZ=0 EndX=-1.5 EndY=11.5 EndZ=0
    g45: LineSegment StartX=-49.19 StartY=8.5 StartZ=0 EndX=-1.5 EndY=8.5 EndZ=0
    g46: LineSegment StartX=-49.19 StartY=5.75 StartZ=0 EndX=-1.5 EndY=5.75 EndZ=0
    g47: LineSegment StartX=-49.19 StartY=2.75 StartZ=0 EndX=-1.5 EndY=2.75 EndZ=0
  constraints (120):
    c: Vertical(g0)
    c: Distance(g0) = 3
    c: Block(g0)
    c: Vertical(g1)
    c: Distance(g1) = 3
    c: Vertical(g2)
    c: Equal(g0,g2) = 3
    c: Block(g2)
    c: Vertical(g3)
    c: Equal(g1,g3) = 3
    c: Vertical(g4)
    c: Equal(g0,g4) = 3
    c: Block(g4)
    c: Vertical(g5)
    c: Equal(g1,g5) = 3
    c: Vertical(g6)
    c: Equal(g0,g6) = 3
    c: Block(g6)
    c: Vertical(g7)
    c: Equal(g1,g7) = 3
    c: Vertical(g8)
    c: Equal(g0,g8) = 3
    c: Block(g8)
    c: Vertical(g9)
    c: Equal(g1,g9) = 3
    c: Vertical(g10)
    c: Equal(g0,g10) = 3
    c: Block(g10)
    c: Vertical(g11)
    c: Equal(g1,g11) = 3
    c: Block(g12)
    c: Block(g13)
    c: Block(g14)
    c: Block(g15)
    c: Block(g16)
    c: Block(g17)
    c: Block(g18)
    c: Block(g19)
    c: Block(g20)
    c: Block(g21)
    c: Block(g22)
    c: Block(g23)
    c: Block(g11)
    c: Block(g9)
    c: Block(g7)
    c: Block(g5)
    c: Block(g3)
    c: Block(g1)
    c: Coincident(g24,g0)
    c: Coincident(g24,g12)
    c: Horizontal(g24)
    c: Coincident(g25,g0)
    c: Coincident(g25,g12)
    c: Horizontal(g25)
    c: Coincident(g26,g1)
    c: Coincident(g26,g13)
    c: Horizontal(g26)
    c: Coincident(g27,g1)
    c: Coincident(g27,g13)
    c: Horizontal(g27)
    c: Coincident(g28,g2)
    c: Coincident(g28,g14)
    c: Horizontal(g28)
    c: Coincident(g29,g2)
    c: Coincident(g29,g14)
    c: Horizontal(g29)
    c: Coincident(g30,g3)
    c: Coincident(g30,g15)
    c: Horizontal(g30)
    c: Coincident(g31,g3)
    c: Coincident(g31,g15)
    c: Horizontal(g31)
    c: Coincident(g32,g4)
    c: Coincident(g32,g16)
    c: Horizontal(g32)
    c: Coincident(g33,g4)
    c: Coincident(g33,g16)
    c: Horizontal(g33)
    c: Coincident(g34,g5)
    c: Coincident(g34,g17)
    c: Horizontal(g34)
    c: Coincident(g35,g5)
    c: Coincident(g35,g17)
    c: Horizontal(g35)
    c: Coincident(g36,g6)
    c: Coincident(g36,g19)
    c: Horizontal(g36)
    c: Coincident(g37,g6)
    c: Coincident(g37,g19)
    c: Horizontal(g37)
    c: Coincident(g38,g7)
    c: Coincident(g38,g18)
    c: Horizontal(g38)
    c: Coincident(g39,g7)
    c: Coincident(g39,g18)
    c: Horizontal(g39)
    c: Coincident(g40,g8)
    c: Coincident(g40,g20)
    c: Horizontal(g40)
    c: Coincident(g41,g8)
    c: Coincident(g41,g20)
    c: Horizontal(g41)
    c: Coincident(g42,g9)
    c: Coincident(g42,g23)
    c: Horizontal(g42)
    c: Coincident(g43,g9)
    c: Coincident(g43,g23)
    c: Horizontal(g43)
    c: Coincident(g44,g10)
    c: Coincident(g44,g22)
    c: Horizontal(g44)
    c: Coincident(g45,g10)
    c: Coincident(g45,g22)
    c: Horizontal(g45)
    c: Coincident(g46,g11)
    c: Coincident(g46,g21)
    c: Horizontal(g46)
    c: Coincident(g47,g11)
    c: Coincident(g47,g21)
    c: Horizontal(g47)
FEATURE [Part::Extrusion] Extrude042
  Base = -> Sketch051
  Dir = (1,-2e-16,2e-16)
  DirMode = 2
  FaceMakerClass = Part::FaceMakerBullseye
  LengthFwd = 19
  LengthRev = 0
  Placement = pos=(-19,0,0) rot=(0,0,1;0rad)
  Solid = true
  Symmetric = false
FEATURE [Part::Fillet] Fillet035  label="removeToCreateVentalationHoles"
  Base = -> Extrude042
  Edges = <same value as first occurrence — deduplicated (x6 in doc)>
  Placement = pos=(7,0,0) rot=(0,0,1;0rad)
FEATURE [Part::Cut] Cut038  label="top017"
  Base = -> Cut033
  Tool = -> Fillet035
FEATURE [Sketcher::SketchObject] Sketch052  label="bottomSketch001"
  FullyConstrained = true
  sketch-geometry (45):
    g0: LineSegment StartX=6.29999 StartY=8 StartZ=0 EndX=3.29999 EndY=8 EndZ=0
    g1: LineSegment StartX=3.29999 StartY=8 StartZ=0 EndX=3.29999 EndY=-6.03275e-07 EndZ=0
    g2: ArcOfCircle CenterX=8.29999 CenterY=5 CenterZ=0 NormalX=0 NormalY=0 NormalZ=1 AngleXU=0 Radius=2 StartAngle=3.14159 EndAngle=4.71239
    g3: LineSegment StartX=6.29999 StartY=8 StartZ=0 EndX=6.29999 EndY=5 EndZ=0
    g4: ArcOfCircle CenterX=105 CenterY=19 CenterZ=0 NormalX=0 NormalY=0 NormalZ=1 AngleXU=0 Radius=12.7 StartAngle=4.71239 EndAngle=5.94289
    g5-g11: Circle x7 (B-spline internal-alignment scaffolding for g12; pole/knot coordinates omitted)
    g12: BSplineCurve PolesCount=7 KnotsCount=5 Degree=3 IsPeriodic=0
    g13-g17: GeomPoint x5 (B-spline internal-alignment scaffolding for g12; pole/knot coordinates omitted)
    g18: ArcOfCircle CenterX=105 CenterY=19 CenterZ=0 NormalX=0 NormalY=0 NormalZ=1 AngleXU=0 Radius=15.7 StartAngle=5.81226 EndAngle=6.28319
    g19: BSplineCurve PolesCount=5 KnotsCount=3 Degree=3 IsPeriodic=0
    g20: LineSegment StartX=8.29999 StartY=3 StartZ=0 EndX=101.7 EndY=3 EndZ=0
    g21: LineSegment StartX=3.29999 StartY=-6.03275e-07 StartZ=0 EndX=105 EndY=-6.03275e-07 EndZ=0
    g22: LineSegment StartX=120.974 StartY=8.71251 StartZ=0 EndX=122.332 EndY=7.83778 EndZ=0
    g23: LineSegment StartX=105 StartY=-6.03274e-07 StartZ=0 EndX=113 EndY=-6.03274e-07 EndZ=0
    g24: ArcOfCircle CenterX=105 CenterY=19 CenterZ=0 NormalX=0 NormalY=0 NormalZ=1 AngleXU=0 Radius=20.6155 StartAngle=5.11091 EndAngle=5.71103
    g25: ArcOfCircle CenterX=117.7 CenterY=19 CenterZ=0 NormalX=0 NormalY=0 NormalZ=1 AngleXU=0 Radius=3 StartAngle=1.2e-15 EndAngle=2.10468
    g26: Circle CenterX=116.345 CenterY=16.3232 CenterZ=0 NormalX=0 NormalY=0 NormalZ=1 AngleXU=0 Radius=1
    g27: Circle CenterX=117.24 CenterY=15.7584 CenterZ=0 NormalX=0 NormalY=0 NormalZ=1 AngleXU=0 Radius=1
    g28: Circle CenterX=116.972 CenterY=14.7612 CenterZ=0 NormalX=0 NormalY=0 NormalZ=1 AngleXU=0 Radius=1
    g29: BSplineCurve PolesCount=3 KnotsCount=2 Degree=2 IsPeriodic=0
    g30: GeomPoint X=116.345 Y=16.3232 Z=0
    g31: GeomPoint X=116.972 Y=14.7612 Z=0
    g32: Circle CenterX=115.828 CenterY=17.157 CenterZ=0 NormalX=0 NormalY=0 NormalZ=1 AngleXU=0 Radius=1
    g33: Circle CenterX=115.841 CenterY=16.639 CenterZ=0 NormalX=0 NormalY=0 NormalZ=1 AngleXU=0 Radius=1
    g34: Circle CenterX=116.345 CenterY=16.3232 CenterZ=0 NormalX=0 NormalY=0 NormalZ=1 AngleXU=0 Radius=1
    g35: BSplineCurve PolesCount=3 KnotsCount=2 Degree=2 IsPeriodic=0
    g36: GeomPoint X=115.828 Y=17.157 Z=0
    g37: GeomPoint X=116.345 Y=16.3232 Z=0
    g38: LineSegment StartX=115.828 StartY=17.157 StartZ=0 EndX=115.828 EndY=20.8307 EndZ=0
    g39: Circle CenterX=115.828 CenterY=20.8307 CenterZ=0 NormalX=0 NormalY=0 NormalZ=1 AngleXU=0 Radius=1
    g40: Circle CenterX=115.831 CenterY=21.3396 CenterZ=0 NormalX=0 NormalY=0 NormalZ=1 AngleXU=0 Radius=1
    g41: Circle CenterX=116.173 CenterY=21.5825 CenterZ=0 NormalX=0 NormalY=0 NormalZ=1 AngleXU=0 Radius=1
    g42: BSplineCurve PolesCount=3 KnotsCount=2 Degree=2 IsPeriodic=0
    g43: GeomPoint X=115.828 Y=20.8307 Z=0
    g44: GeomPoint X=116.173 Y=21.5825 Z=0
  constraints (70):
    c: Horizontal(g0)
    c: Distance(g0) = 3
    c: Coincident(g1,g0)
    c: Vertical(g1)
    c: Block(g2)
    c: Block(g0)
    c: Coincident(g3,g0)
    c: Coincident(g3,g2)
    c: Vertical(g3)
    c: Block(g1)
    c: Block(g4)
    c: Coincident(g19,g4)
    c: Block(g19)
    c: Equal(g5, g6-g11) x6
    c: InternalAlignment(g5-g11 -> g12) x7
    c: InternalAlignment(g13-g17 -> g12) x5
    c: Block(g12)
    c: Coincident(g18,g12)
    c: Block(g18)
    c: Coincident(g20,g2)
    c: Coincident(g20,g19)
    c: Horizontal(g20)
    c: Distance(g20) = 93.4
    c: Coincident(g21,g1)
    c: Horizontal(g21)
    c: Distance(g21) = 101.7
    c: Horizontal(g23)
    c: Distance(g23) = 8
    c: Coincident(g24,g23)
    c: Block(g23)
    c: Coincident(g22,g24)
    c: Block(g24)
    c: Block(g22)
    c: Distance(g22) = 1.61553
    c: Coincident(g25,g18)
    c: Block(g25)
    c: Weight(g26) = 1
    c: Equal(g26,g27)
    c: Equal(g26,g28)
    c: Coincident(g29,g4)
    c: InternalAlignment(g26,g29)
    c: InternalAlignment(g27,g29)
    c: InternalAlignment(g28,g29)
    c: InternalAlignment(g30,g29)
    c: InternalAlignment(g31,g29)
    c: Block(g29)
    c: Weight(g32) = 1
    c: Equal(g32,g33)
    c: Equal(g32,g34)
    c: Coincident(g35,g29)
    c: InternalAlignment(g32,g35)
    c: InternalAlignment(g33,g35)
    c: InternalAlignment(g34,g35)
    c: InternalAlignment(g36,g35)
    c: InternalAlignment(g37,g35)
    c: Block(g35)
    c: Coincident(g38,g35)
    c: Vertical(g38)
    c: Block(g38)
    c: Coincident(g42,g38)
    c: Weight(g39) = 1
    c: Equal(g39,g40)
    c: Equal(g39,g41)
    c: Coincident(g42,g25)
    c: InternalAlignment(g39,g42)
    c: InternalAlignment(g40,g42)
    c: InternalAlignment(g41,g42)
    c: InternalAlignment(g43,g42)
    c: InternalAlignment(g44,g42)
    c: Block(g42)
FEATURE [Part::Extrusion] Extrude043  label="bottom010"
  Base = -> Sketch052
  Dir = (0,0,1)
  DirMode = 2
  FaceMakerClass = Part::FaceMakerBullseye
  LengthFwd = 71.4
  LengthRev = 0
  Placement = pos=(0,0,0.3) rot=(0,0,1;0rad)
  Solid = true
  Symmetric = false
FEATURE [Sketcher::SketchObject] Sketch053  label="topSketch013"
  FullyConstrained = true
  sketch-geometry (22):
    g0: LineSegment StartX=5.21097e-06 StartY=3 StartZ=0 EndX=5.21097e-06 EndY=19 EndZ=0
    g1: ArcOfCircle CenterX=19 CenterY=19 CenterZ=0 NormalX=0 NormalY=0 NormalZ=1 AngleXU=0 Radius=19 StartAngle=1.5708 EndAngle=3.14159
    g2: ArcOfCircle CenterX=19 CenterY=19 CenterZ=0 NormalX=0 NormalY=0 NormalZ=1 AngleXU=0 Radius=16 StartAngle=1.5708 EndAngle=3.14159
    g3: LineSegment StartX=114 StartY=35 StartZ=0 EndX=19 EndY=35 EndZ=0
    g4: LineSegment StartX=5.21097e-06 StartY=3 StartZ=0 EndX=5.21097e-06 EndY=0 EndZ=0
    g5: LineSegment StartX=3 StartY=0 StartZ=0 EndX=5.21097e-06 EndY=0 EndZ=0
    g6: LineSegment StartX=3 StartY=19 StartZ=0 EndX=3 EndY=0 EndZ=0
    g7: LineSegment StartX=19 StartY=38 StartZ=0 EndX=124 EndY=38 EndZ=0
    g8: Circle CenterX=119 CenterY=35 CenterZ=0 NormalX=0 NormalY=0 NormalZ=1 AngleXU=0 Radius=1
    g9: Circle CenterX=121 CenterY=35 CenterZ=0 NormalX=0 NormalY=0 NormalZ=1 AngleXU=0 Radius=1
    g10: Circle CenterX=121 CenterY=33 CenterZ=0 NormalX=0 NormalY=0 NormalZ=1 AngleXU=0 Radius=1
    g11: BSplineCurve PolesCount=3 KnotsCount=2 Degree=2 IsPeriodic=0
    g12: GeomPoint X=119 Y=35 Z=0
    g13: GeomPoint X=121 Y=33 Z=0
    g14: LineSegment StartX=119 StartY=35 StartZ=0 EndX=114 EndY=35 EndZ=0
    g15: ArcOfCircle CenterX=105 CenterY=19 CenterZ=0 NormalX=0 NormalY=0 NormalZ=1 AngleXU=0 Radius=16 StartAngle=5.60905 EndAngle=6.28319
    g16: LineSegment StartX=121 StartY=33 StartZ=0 EndX=121 EndY=19 EndZ=0
    g17: LineSegment StartX=117.5 StartY=9.01251 StartZ=0 EndX=121.163 EndY=9.0125 EndZ=0
    g18: ArcOfCircle CenterX=105 CenterY=19 CenterZ=0 NormalX=0 NormalY=0 NormalZ=1 AngleXU=0 Radius=20.6155 StartAngle=5.7297 EndAngle=6.28319
    g19: LineSegment StartX=121.163 StartY=9.0125 StartZ=0 EndX=122.538 EndY=8.16329 EndZ=0
    g20: LineSegment StartX=124 StartY=38 StartZ=0 EndX=125.616 EndY=38 EndZ=0
    g21: LineSegment StartX=125.616 StartY=19 StartZ=0 EndX=125.616 EndY=38 EndZ=0
  constraints (50):
    c: Vertical(g0)
    c: Block(g0)
    c: Coincident(g1,g0)
    c: Block(g1)
    c: Coincident(g2,g1)
    c: Block(g2)
    c: Coincident(g3,g2)
    c: Horizontal(g3)
    c: Tangent(g3,g2)
    c: Coincident(g4,g0)
    c: Distance(g4) = 3
    c: Vertical(g4)
    c: Coincident(g5,g4)
    c: Horizontal(g5)
    c: Coincident(g6,g2)
    c: Coincident(g6,g5)
    c: Vertical(g6)
    c: Horizontal(g7)
    c: Distance(g7) = 105
    c: Coincident(g7,g1)
    c: Block(g3)
    c: Weight(g8) = 1
    c: Equal(g8,g9)
    c: Equal(g8,g10)
    c: InternalAlignment(g8,g11)
    c: InternalAlignment(g9,g11)
    c: InternalAlignment(g10,g11)
    c: InternalAlignment(g12,g11)
    c: InternalAlignment(g13,g11)
    c: Block(g11)
    c: Coincident(g14,g11)
    c: Coincident(g14,g3)
    c: Horizontal(g14)
    c: Block(g15)
    c: Coincident(g16,g11)
    c: Coincident(g16,g15)
    c: Vertical(g16)
    c: Distance(g16) = 14
    c: Coincident(g17,g15)
    c: Block(g18)
    c: Coincident(g19,g18)
    c: Coincident(g20,g7)
    c: Horizontal(g20)
    c: Vertical(g21)
    c: Coincident(g20,g21)
    c: Block(g20)
    c: Block(g21)
    c: Block(g19)
    c: Block(g17)
    c: Distance(g20) = 1.61553
FEATURE [Part::Extrusion] Extrude044
  Base = -> Sketch053
  Dir = (0,0,1)
  DirMode = 2
  FaceMakerClass = Part::FaceMakerBullseye
  LengthFwd = 72
  LengthRev = 0
  Solid = true
  Symmetric = false
FEATURE [Part::Fillet] Fillet036  label="top018"
  Base = -> Extrude044
  Edges = 1 edges r=2: [Edge41]
FEATURE [Sketcher::SketchObject] Sketch054
  FullyConstrained = false
  Placement = pos=(0,0,0) rot=(1,0,0;1.5708rad)
  sketch-geometry (24):
    g0: ArcOfCircle CenterX=-4 CenterY=-10.5 CenterZ=0 NormalX=0 NormalY=0 NormalZ=1 AngleXU=0 Radius=1.5 StartAngle=6e-16 EndAngle=3.14159
    g1: ArcOfCircle CenterX=-34.2 CenterY=-10.5 CenterZ=0 NormalX=0 NormalY=0 NormalZ=1 AngleXU=0 Radius=1.5 StartAngle=0 EndAngle=3.14159
    g2: ArcOfCircle CenterX=-34.2 CenterY=-27.7 CenterZ=0 NormalX=0 NormalY=0 NormalZ=1 AngleXU=0 Radius=1.5 StartAngle=3.14159 EndAngle=6.28319
    g3: ArcOfCircle CenterX=-4 CenterY=-27.7 CenterZ=0 NormalX=0 NormalY=0 NormalZ=1 AngleXU=0 Radius=1.5 StartAngle=3.1416 EndAngle=6.28319
    g4: ArcOfCircle CenterX=-10 CenterY=-4.3 CenterZ=0 NormalX=0 NormalY=0 NormalZ=1 AngleXU=0 Radius=1.5 StartAngle=2e-16 EndAngle=3.14159
    g5: ArcOfCircle CenterX=-16.1 CenterY=-1.8 CenterZ=0 NormalX=0 NormalY=0 NormalZ=1 AngleXU=0 Radius=1.5 StartAngle=5e-16 EndAngle=3.14159
    g6: ArcOfCircle CenterX=-22.1 CenterY=-1.8 CenterZ=0 NormalX=0 NormalY=0 NormalZ=1 AngleXU=0 Radius=1.5 StartAngle=5e-16 EndAngle=3.14159
    g7: ArcOfCircle CenterX=-28.2 CenterY=-4.3 CenterZ=0 NormalX=0 NormalY=0 NormalZ=1 AngleXU=0 Radius=1.5 StartAngle=2e-16 EndAngle=3.14159
    g8: ArcOfCircle CenterX=-10 CenterY=-33.9 CenterZ=0 NormalX=0 NormalY=0 NormalZ=1 AngleXU=0 Radius=1.5 StartAngle=3.14159 EndAngle=6.28319
    g9: ArcOfCircle CenterX=-16.1 CenterY=-36.4 CenterZ=0 NormalX=0 NormalY=0 NormalZ=1 AngleXU=0 Radius=1.5 StartAngle=3.14159 EndAngle=6.28319
    g10: ArcOfCircle CenterX=-22.1 CenterY=-36.4 CenterZ=0 NormalX=0 NormalY=0 NormalZ=1 AngleXU=0 Radius=1.5 StartAngle=3.14159 EndAngle=6.28319
    g11: ArcOfCircle CenterX=-28.2 CenterY=-33.9 CenterZ=0 NormalX=0 NormalY=0 NormalZ=1 AngleXU=0 Radius=1.5 StartAngle=3.14159 EndAngle=6.28319
    g12: LineSegment StartX=-35.7 StartY=-10.5 StartZ=0 EndX=-35.7 EndY=-27.7 EndZ=0
    g13: LineSegment StartX=-32.7 StartY=-10.5 StartZ=0 EndX=-32.7 EndY=-27.7 EndZ=0
    g14: LineSegment StartX=-29.7 StartY=-33.9 StartZ=0 EndX=-29.7 EndY=-4.3 EndZ=0
    g15: LineSegment StartX=-26.7 StartY=-33.9 StartZ=0 EndX=-26.7 EndY=-4.3 EndZ=0
    g16: LineSegment StartX=-2.5 StartY=-10.5 StartZ=0 EndX=-2.5 EndY=-27.7 EndZ=0
    g17: LineSegment StartX=-8.5 StartY=-4.3 StartZ=0 EndX=-8.5 EndY=-33.9 EndZ=0
    g18: LineSegment StartX=-5.5 StartY=-10.5 StartZ=0 EndX=-5.5 EndY=-27.7 EndZ=0
    g19: LineSegment StartX=-11.5 StartY=-4.3 StartZ=0 EndX=-11.5 EndY=-33.9 EndZ=0
    g20: LineSegment StartX=-14.6 StartY=-1.8 StartZ=0 EndX=-14.6 EndY=-36.4 EndZ=0
    g21: LineSegment StartX=-17.6 StartY=-1.8 StartZ=0 EndX=-17.6 EndY=-36.4 EndZ=0
    g22: LineSegment StartX=-20.6 StartY=-36.4 StartZ=0 EndX=-20.6 EndY=-1.8 EndZ=0
    g23: LineSegment StartX=-23.6 StartY=-1.8 StartZ=0 EndX=-23.6 EndY=-36.4 EndZ=0
  constraints (48):
    c: Block(g0)
    c: Block(g1)
    c: Block(g2)
    c: Block(g3)
    c: Block(g4)
    c: Block(g5)
    c: Block(g6)
    c: Block(g7)
    c: Block(g8)
    c: Block(g9)
    c: Block(g10)
    c: Block(g11)
    c: Coincident(g12,g1)
    c: Coincident(g12,g2)
    c: Vertical(g12)
    c: Coincident(g13,g1)
    c: Coincident(g13,g2)
    c: Vertical(g13)
    c: Coincident(g14,g11)
    c: Coincident(g14,g7)
    c: Vertical(g14)
    c: Coincident(g15,g11)
    c: Coincident(g15,g7)
    c: Vertical(g15)
    c: Coincident(g16,g0)
    c: Coincident(g16,g3)
    c: Vertical(g16)
    c: Coincident(g17,g4)
    c: Coincident(g17,g8)
    c: Vertical(g17)
    c: Coincident(g18,g0)
    c: Coincident(g18,g3)
    c: Vertical(g18)
    c: Coincident(g19,g4)
    c: Coincident(g19,g8)
    c: Vertical(g19)
    c: Coincident(g20,g5)
    c: Coincident(g20,g9)
    c: Vertical(g20)
    c: Coincident(g21,g5)
    c: Coincident(g21,g9)
    c: Vertical(g21)
    c: Coincident(g22,g10)
    c: Coincident(g22,g6)
    c: Vertical(g22)
    c: Coincident(g23,g6)
    c: Coincident(g23,g10)
    c: Vertical(g23)
FEATURE [Part::Extrusion] Extrude045  label="removeToCreateFanGrillHoles003"
  Base = -> Sketch054
  Dir = (0,-1,6e-16)
  DirMode = 2
  FaceMakerClass = Part::FaceMakerBullseye
  LengthFwd = 10
  LengthRev = 0
  Placement = pos=(65.4,44,54.82) rot=(0,0,1;0rad)
  Solid = true
  Symmetric = false
FEATURE [Part::Feature] Face105 .. Face108  x4 (patterned run collapsed; names and placements below)
  shape: bbox 3.5 x 17.8 x 2e-07 mm, 1 faces, 0 solids (baked)
FEATURE [Part::Revolution] Revolve113  label="removeToCreateScrewAndThreadedInsertHole041"
  Angle = 360
  Axis = (0,1,0)
  Base = (0,0,0)
  FaceMakerClass = Part::FaceMakerBullseye
  Placement = pos=(62.3,30.3,19.7) rot=(0,0,1;0rad)
  Solid = false
  Source = -> Face105
  Symmetric = false
FEATURE [Part::Revolution] Revolve114  label="removeToCreateScrewAndThreadedInsertHole042"
  Angle = 360
  Axis = (0,1,0)
  Base = (0,0,0)
  FaceMakerClass = Part::FaceMakerBullseye
  Placement = pos=(62.3,30.3,51.7) rot=(0,0,1;0rad)
  Solid = false
  Source = -> Face106
  Symmetric = false
FEATURE [Part::Revolution] Revolve115  label="removeToCreateScrewAndThreadedInsertHole043"
  Angle = 360
  Axis = (0,1,0)
  Base = (0,0,0)
  FaceMakerClass = Part::FaceMakerBullseye
  Placement = pos=(30.3,30.3,19.7) rot=(0,0,1;0rad)
  Solid = false
  Source = -> Face107
  Symmetric = false
FEATURE [Part::Revolution] Revolve116  label="removeToCreateScrewAndThreadedInsertHole044"
  Angle = 360
  Axis = (0,1,0)
  Base = (0,0,0)
  FaceMakerClass = Part::FaceMakerBullseye
  Placement = pos=(30.3,30.3,51.7) rot=(0,0,1;0rad)
  Solid = false
  Source = -> Face108
  Symmetric = false
FEATURE [Part::MultiFuse] Fusion083  label="createThreadedInsertHolesForFan004"
  Shapes = -> [Revolve113,Revolve114,Revolve115,Revolve116]
FEATURE [Part::Box] Box024  label="removeToCreteHoleForPlugHousing026"
  AttacherType = Attacher::AttachEngine3D
  Height = 28.6
  Length = 10
  Placement = pos=(-2,0,21.7) rot=(0,0,1;0rad)
  Width = 19
FEATURE [Part::Cylinder] Cylinder038  label="removeToCreteHoleForPlugHousing027"
  Angle = 360
  AttacherType = Attacher::AttachEngine3D
  Height = 20
  Placement = pos=(-2,19,36) rot=(0,1,0;1.5708rad)
  Radius = 14.3
FEATURE [Part::MultiFuse] Fusion084  label="removeToCreteHoleForPlugHousing028"
  Shapes = -> [Box024,Cylinder038]
FEATURE [Part::Cylinder] Cylinder039
  Angle = 360
  AttacherType = Attacher::AttachEngine3D
  Height = 20
  Placement = pos=(0,0,36.15) rot=(0,0,1;0rad)
  Radius = 14.3
FEATURE [Part::Cylinder] Cylinder040
  Angle = 360
  AttacherType = Attacher::AttachEngine3D
  Height = 10
  Placement = pos=(0,0,36.15) rot=(0,0,1;0rad)
  Radius = 4
FEATURE [Part::Box] Box025  label="removeToCreteHoleForPlugHousing030"
  AttacherType = Attacher::AttachEngine3D
  Height = 28.6
  Length = 20
  Placement = pos=(106.15,0,21.7) rot=(0,0,1;0rad)
  Width = 19
FEATURE [Part::MultiFuse] Fusion086  label="removeToCreteHoleForPlugHousing031"
  Placement = pos=(70,19,36) rot=(0,1,0;1.5708rad)
  Shapes = -> [Cylinder039,Cylinder040]
FEATURE [Part::MultiFuse] Fusion085  label="removeToCreteHoleForPlugHousing029"
  Shapes = -> [Box025,Fusion086]
FEATURE [Sketcher::SketchObject] Sketch055
  FullyConstrained = true
  Placement = pos=(117,19,0) rot=(0.57735,0.57735,0.57735;2.0944rad)
  sketch-geometry (48):
    g0: LineSegment StartX=-49.19 StartY=69.25 StartZ=0 EndX=-49.19 EndY=66.25 EndZ=0
    g1: LineSegment StartX=-49.19 StartY=63.5 StartZ=0 EndX=-49.19 EndY=60.5 EndZ=0
    g2: LineSegment StartX=-49.19 StartY=57.75 StartZ=0 EndX=-49.19 EndY=54.75 EndZ=0
    g3: LineSegment StartX=-49.19 StartY=52 StartZ=0 EndX=-49.19 EndY=49 EndZ=0
    g4: LineSegment StartX=-49.19 StartY=46.25 StartZ=0 EndX=-49.19 EndY=43.25 EndZ=0
    g5: LineSegment StartX=-49.19 StartY=40.5 StartZ=0 EndX=-49.19 EndY=37.5 EndZ=0
    g6: LineSegment StartX=-49.19 StartY=34.5 StartZ=0 EndX=-49.19 EndY=31.5 EndZ=0
    g7: LineSegment StartX=-49.19 StartY=28.75 StartZ=0 EndX=-49.19 EndY=25.75 EndZ=0
    g8: LineSegment StartX=-49.19 StartY=23 StartZ=0 EndX=-49.19 EndY=20 EndZ=0
    g9: LineSegment StartX=-49.19 StartY=17.25 StartZ=0 EndX=-49.19 EndY=14.25 EndZ=0
    g10: LineSegment StartX=-49.19 StartY=11.5 StartZ=0 EndX=-49.19 EndY=8.5 EndZ=0
    g11: LineSegment StartX=-49.19 StartY=5.75 StartZ=0 EndX=-49.19 EndY=2.75 EndZ=0
    g12: ArcOfCircle CenterX=-1.5 CenterY=67.75 CenterZ=0 NormalX=0 NormalY=0 NormalZ=1 AngleXU=0 Radius=1.5 StartAngle=4.71239 EndAngle=7.85398
    g13: ArcOfCircle CenterX=-1.5 CenterY=62 CenterZ=0 NormalX=0 NormalY=0 NormalZ=1 AngleXU=0 Radius=1.5 StartAngle=4.71239 EndAngle=7.85398
    g14: ArcOfCircle CenterX=-1.5 CenterY=56.25 CenterZ=0 NormalX=0 NormalY=0 NormalZ=1 AngleXU=0 Radius=1.5 StartAngle=4.71239 EndAngle=7.85398
    g15: ArcOfCircle CenterX=-11.49 CenterY=50.5 CenterZ=0 NormalX=0 NormalY=0 NormalZ=1 AngleXU=0 Radius=1.5 StartAngle=4.71239 EndAngle=7.85398
    g16: ArcOfCircle CenterX=-16.28 CenterY=44.75 CenterZ=0 NormalX=0 NormalY=0 NormalZ=1 AngleXU=0 Radius=1.5 StartAngle=4.71239 EndAngle=7.85398
    g17: ArcOfCircle CenterX=-18.2337 CenterY=39 CenterZ=0 NormalX=0 NormalY=0 NormalZ=1 AngleXU=0 Radius=1.5 StartAngle=4.71485 EndAngle=7.85398
    g18: ArcOfCircle CenterX=-16.2837 CenterY=27.25 CenterZ=0 NormalX=0 NormalY=0 NormalZ=1 AngleXU=0 Radius=1.5 StartAngle=4.71485 EndAngle=7.85398
    g19: ArcOfCircle CenterX=-18.2337 CenterY=33 CenterZ=0 NormalX=0 NormalY=0 NormalZ=1 AngleXU=0 Radius=1.5 StartAngle=4.71485 EndAngle=7.85398
    g20: ArcOfCircle CenterX=-11.49 CenterY=21.5 CenterZ=0 NormalX=0 NormalY=0 NormalZ=1 AngleXU=0 Radius=1.5 StartAngle=4.71239 EndAngle=7.85398
    g21: ArcOfCircle CenterX=-1.5 CenterY=4.25 CenterZ=0 NormalX=0 NormalY=0 NormalZ=1 AngleXU=0 Radius=1.5 StartAngle=4.71239 EndAngle=7.85398
    g22: ArcOfCircle CenterX=-1.5 CenterY=10 CenterZ=0 NormalX=0 NormalY=0 NormalZ=1 AngleXU=0 Radius=1.5 StartAngle=4.71239 EndAngle=7.85398
    g23: ArcOfCircle CenterX=-1.5 CenterY=15.75 CenterZ=0 NormalX=0 NormalY=0 NormalZ=1 AngleXU=0 Radius=1.5 StartAngle=4.71239 EndAngle=7.85398
    g24: LineSegment StartX=-49.19 StartY=69.25 StartZ=0 EndX=-1.5 EndY=69.25 EndZ=0
    g25: LineSegment StartX=-49.19 StartY=66.25 StartZ=0 EndX=-1.5 EndY=66.25 EndZ=0
    g26: LineSegment StartX=-49.19 StartY=63.5 StartZ=0 EndX=-1.5 EndY=63.5 EndZ=0
    g27: LineSegment StartX=-49.19 StartY=60.5 StartZ=0 EndX=-1.5 EndY=60.5 EndZ=0
    g28: LineSegment StartX=-49.19 StartY=57.75 StartZ=0 EndX=-1.5 EndY=57.75 EndZ=0
    g29: LineSegment StartX=-49.19 StartY=54.75 StartZ=0 EndX=-1.5 EndY=54.75 EndZ=0
    g30: LineSegment StartX=-49.19 StartY=52 StartZ=0 EndX=-11.49 EndY=52 EndZ=0
    g31: LineSegment StartX=-49.19 StartY=49 StartZ=0 EndX=-11.49 EndY=49 EndZ=0
    g32: LineSegment StartX=-49.19 StartY=46.25 StartZ=0 EndX=-16.28 EndY=46.25 EndZ=0
    g33: LineSegment StartX=-49.19 StartY=43.25 StartZ=0 EndX=-16.28 EndY=43.25 EndZ=0
    g34: LineSegment StartX=-49.19 StartY=40.5 StartZ=0 EndX=-18.2337 EndY=40.5 EndZ=0
    g35: LineSegment StartX=-49.19 StartY=37.5 StartZ=0 EndX=-18.23 EndY=37.5 EndZ=0
    g36: LineSegment StartX=-49.19 StartY=34.5 StartZ=0 EndX=-18.2337 EndY=34.5 EndZ=0
    g37: LineSegment StartX=-49.19 StartY=31.5 StartZ=0 EndX=-18.23 EndY=31.5 EndZ=0
    g38: LineSegment StartX=-49.19 StartY=28.75 StartZ=0 EndX=-16.2837 EndY=28.75 EndZ=0
    g39: LineSegment StartX=-49.19 StartY=25.75 StartZ=0 EndX=-16.28 EndY=25.75 EndZ=0
    g40: LineSegment StartX=-49.19 StartY=23 StartZ=0 EndX=-11.49 EndY=23 EndZ=0
    g41: LineSegment StartX=-49.19 StartY=20 StartZ=0 EndX=-11.49 EndY=20 EndZ=0
    g42: LineSegment StartX=-49.19 StartY=17.25 StartZ=0 EndX=-1.5 EndY=17.25 EndZ=0
    g43: LineSegment StartX=-49.19 StartY=14.25 StartZ=0 EndX=-1.5 EndY=14.25 EndZ=0
    g44: LineSegment StartX=-49.19 StartY=11.5 StartZ=0 EndX=-1.5 EndY=11.5 EndZ=0
    g45: LineSegment StartX=-49.19 StartY=8.5 StartZ=0 EndX=-1.5 EndY=8.5 EndZ=0
    g46: LineSegment StartX=-49.19 StartY=5.75 StartZ=0 EndX=-1.5 EndY=5.75 EndZ=0
    g47: LineSegment StartX=-49.19 StartY=2.75 StartZ=0 EndX=-1.5 EndY=2.75 EndZ=0
  constraints (120):
    c: Vertical(g0)
    c: Distance(g0) = 3
    c: Block(g0)
    c: Vertical(g1)
    c: Distance(g1) = 3
    c: Vertical(g2)
    c: Equal(g0,g2) = 3
    c: Block(g2)
    c: Vertical(g3)
    c: Equal(g1,g3) = 3
    c: Vertical(g4)
    c: Equal(g0,g4) = 3
    c: Block(g4)
    c: Vertical(g5)
    c: Equal(g1,g5) = 3
    c: Vertical(g6)
    c: Equal(g0,g6) = 3
    c: Block(g6)
    c: Vertical(g7)
    c: Equal(g1,g7) = 3
    c: Vertical(g8)
    c: Equal(g0,g8) = 3
    c: Block(g8)
    c: Vertical(g9)
    c: Equal(g1,g9) = 3
    c: Vertical(g10)
    c: Equal(g0,g10) = 3
    c: Block(g10)
    c: Vertical(g11)
    c: Equal(g1,g11) = 3
    c: Block(g12)
    c: Block(g13)
    c: Block(g14)
    c: Block(g15)
    c: Block(g16)
    c: Block(g17)
    c: Block(g18)
    c: Block(g19)
    c: Block(g20)
    c: Block(g21)
    c: Block(g22)
    c: Block(g23)
    c: Block(g11)
    c: Block(g9)
    c: Block(g7)
    c: Block(g5)
    c: Block(g3)
    c: Block(g1)
    c: Coincident(g24,g0)
    c: Coincident(g24,g12)
    c: Horizontal(g24)
    c: Coincident(g25,g0)
    c: Coincident(g25,g12)
    c: Horizontal(g25)
    c: Coincident(g26,g1)
    c: Coincident(g26,g13)
    c: Horizontal(g26)
    c: Coincident(g27,g1)
    c: Coincident(g27,g13)
    c: Horizontal(g27)
    c: Coincident(g28,g2)
    c: Coincident(g28,g14)
    c: Horizontal(g28)
    c: Coincident(g29,g2)
    c: Coincident(g29,g14)
    c: Horizontal(g29)
    c: Coincident(g30,g3)
    c: Coincident(g30,g15)
    c: Horizontal(g30)
    c: Coincident(g31,g3)
    c: Coincident(g31,g15)
    c: Horizontal(g31)
    c: Coincident(g32,g4)
    c: Coincident(g32,g16)
    c: Horizontal(g32)
    c: Coincident(g33,g4)
    c: Coincident(g33,g16)
    c: Horizontal(g33)
    c: Coincident(g34,g5)
    c: Coincident(g34,g17)
    c: Horizontal(g34)
    c: Coincident(g35,g5)
    c: Coincident(g35,g17)
    c: Horizontal(g35)
    c: Coincident(g36,g6)
    c: Coincident(g36,g19)
    c: Horizontal(g36)
    c: Coincident(g37,g6)
    c: Coincident(g37,g19)
    c: Horizontal(g37)
    c: Coincident(g38,g7)
    c: Coincident(g38,g18)
    c: Horizontal(g38)
    c: Coincident(g39,g7)
    c: Coincident(g39,g18)
    c: Horizontal(g39)
    c: Coincident(g40,g8)
    c: Coincident(g40,g20)
    c: Horizontal(g40)
    c: Coincident(g41,g8)
    c: Coincident(g41,g20)
    c: Horizontal(g41)
    c: Coincident(g42,g9)
    c: Coincident(g42,g23)
    c: Horizontal(g42)
    c: Coincident(g43,g9)
    c: Coincident(g43,g23)
    c: Horizontal(g43)
    c: Coincident(g44,g10)
    c: Coincident(g44,g22)
    c: Horizontal(g44)
    c: Coincident(g45,g10)
    c: Coincident(g45,g22)
    c: Horizontal(g45)
    c: Coincident(g46,g11)
    c: Coincident(g46,g21)
    c: Horizontal(g46)
    c: Coincident(g47,g11)
    c: Coincident(g47,g21)
    c: Horizontal(g47)
FEATURE [Part::Extrusion] Extrude046
  Base = -> Sketch055
  Dir = (1,0,0)
  DirMode = 2
  FaceMakerClass = Part::FaceMakerBullseye
  LengthFwd = 23
  LengthRev = 0
  Placement = pos=(-19,0,0) rot=(0,0,1;0rad)
  Solid = true
  Symmetric = false
FEATURE [Part::Fillet] Fillet038  label="removeToCreateVentalationHoles001"
  Base = -> Extrude046
  Edges = <same value as first occurrence — deduplicated (x6 in doc)>
  Placement = pos=(7,0,0) rot=(0,0,1;0rad)
FEATURE [Sketcher::SketchObject] Sketch056  label="topSketch014"
  FullyConstrained = true
  sketch-geometry (22):
    g0: LineSegment StartX=5.21097e-06 StartY=3 StartZ=0 EndX=5.21097e-06 EndY=19 EndZ=0
    g1: ArcOfCircle CenterX=19 CenterY=19 CenterZ=0 NormalX=0 NormalY=0 NormalZ=1 AngleXU=0 Radius=19 StartAngle=1.5708 EndAngle=3.14159
    g2: ArcOfCircle CenterX=19 CenterY=19 CenterZ=0 NormalX=0 NormalY=0 NormalZ=1 AngleXU=0 Radius=16 StartAngle=1.5708 EndAngle=3.14159
    g3: LineSegment StartX=114 StartY=35 StartZ=0 EndX=19 EndY=35 EndZ=0
    g4: LineSegment StartX=5.21097e-06 StartY=3 StartZ=0 EndX=5.21097e-06 EndY=0 EndZ=0
    g5: LineSegment StartX=3 StartY=0 StartZ=0 EndX=5.21097e-06 EndY=0 EndZ=0
    g6: LineSegment StartX=3 StartY=19 StartZ=0 EndX=3 EndY=0 EndZ=0
    g7: LineSegment StartX=19 StartY=38 StartZ=0 EndX=124 EndY=38 EndZ=0
    g8: Circle CenterX=119 CenterY=35 CenterZ=0 NormalX=0 NormalY=0 NormalZ=1 AngleXU=0 Radius=1
    g9: Circle CenterX=121 CenterY=35 CenterZ=0 NormalX=0 NormalY=0 NormalZ=1 AngleXU=0 Radius=1
    g10: Circle CenterX=121 CenterY=33 CenterZ=0 NormalX=0 NormalY=0 NormalZ=1 AngleXU=0 Radius=1
    g11: BSplineCurve PolesCount=3 KnotsCount=2 Degree=2 IsPeriodic=0
    g12: GeomPoint X=119 Y=35 Z=0
    g13: GeomPoint X=121 Y=33 Z=0
    g14: LineSegment StartX=119 StartY=35 StartZ=0 EndX=114 EndY=35 EndZ=0
    g15: ArcOfCircle CenterX=105 CenterY=19 CenterZ=0 NormalX=0 NormalY=0 NormalZ=1 AngleXU=0 Radius=16 StartAngle=5.60905 EndAngle=6.28319
    g16: LineSegment StartX=121 StartY=33 StartZ=0 EndX=121 EndY=19 EndZ=0
    g17: LineSegment StartX=117.5 StartY=9.01251 StartZ=0 EndX=121.163 EndY=9.0125 EndZ=0
    g18: ArcOfCircle CenterX=105 CenterY=19 CenterZ=0 NormalX=0 NormalY=0 NormalZ=1 AngleXU=0 Radius=20.6155 StartAngle=5.7297 EndAngle=6.28319
    g19: LineSegment StartX=121.163 StartY=9.0125 StartZ=0 EndX=122.538 EndY=8.16329 EndZ=0
    g20: LineSegment StartX=124 StartY=38 StartZ=0 EndX=125.616 EndY=38 EndZ=0
    g21: LineSegment StartX=125.616 StartY=19 StartZ=0 EndX=125.616 EndY=38 EndZ=0
  constraints (49):
    c: Vertical(g0)
    c: Block(g0)
    c: Coincident(g1,g0)
    c: Block(g1)
    c: Coincident(g2,g1)
    c: Block(g2)
    c: Coincident(g3,g2)
    c: Horizontal(g3)
    c: Tangent(g3,g2)
    c: Coincident(g4,g0)
    c: Distance(g4) = 3
    c: Vertical(g4)
    c: Coincident(g5,g4)
    c: Horizontal(g5)
    c: Coincident(g6,g2)
    c: Coincident(g6,g5)
    c: Vertical(g6)
    c: Horizontal(g7)
    c: Distance(g7) = 105
    c: Coincident(g7,g1)
    c: Block(g3)
    c: Weight(g8) = 1
    c: Equal(g8,g9)
    c: Equal(g8,g10)
    c: InternalAlignment(g8,g11)
    c: InternalAlignment(g9,g11)
    c: InternalAlignment(g10,g11)
    c: InternalAlignment(g12,g11)
    c: InternalAlignment(g13,g11)
    c: Block(g11)
    c: Coincident(g14,g11)
    c: Coincident(g14,g3)
    c: Horizontal(g14)
    c: Block(g15)
    c: Coincident(g16,g11)
    c: Coincident(g16,g15)
    c: Vertical(g16)
    c: Distance(g16) = 14
    c: Coincident(g17,g15)
    c: Block(g18)
    c: Coincident(g19,g18)
    c: Coincident(g20,g7)
    c: Horizontal(g20)
    c: Vertical(g21)
    c: Coincident(g20,g21)
    c: Block(g20)
    c: Block(g21)
    c: Block(g19)
    c: Block(g17)
FEATURE [Part::Box] Box026  label="removeToCreteHoleForPlugHousing032"
  AttacherType = Attacher::AttachEngine3D
  Height = 28.6
  Length = 10
  Placement = pos=(-2,0,21.7) rot=(0,0,1;0rad)
  Width = 19
FEATURE [Part::Feature] Face109 .. Face112  x4 (patterned run collapsed; names and placements below)
  shape: bbox 3.5 x 17.8 x 2e-07 mm, 1 faces, 0 solids (baked)
FEATURE [Part::Revolution] Revolve117  label="removeToCreateScrewAndThreadedInsertHole045"
  Angle = 360
  Axis = (0,1,0)
  Base = (0,0,0)
  FaceMakerClass = Part::FaceMakerBullseye
  Placement = pos=(62.3,30.3,19.7) rot=(0,0,1;0rad)
  Solid = false
  Source = -> Face109
  Symmetric = false
FEATURE [Part::Revolution] Revolve118  label="removeToCreateScrewAndThreadedInsertHole046"
  Angle = 360
  Axis = (0,1,0)
  Base = (0,0,0)
  FaceMakerClass = Part::FaceMakerBullseye
  Placement = pos=(62.3,30.3,51.7) rot=(0,0,1;0rad)
  Solid = false
  Source = -> Face110
  Symmetric = false
FEATURE [Part::Revolution] Revolve119  label="removeToCreateScrewAndThreadedInsertHole047"
  Angle = 360
  Axis = (0,1,0)
  Base = (0,0,0)
  FaceMakerClass = Part::FaceMakerBullseye
  Placement = pos=(30.3,30.3,19.7) rot=(0,0,1;0rad)
  Solid = false
  Source = -> Face111
  Symmetric = false
FEATURE [Part::Revolution] Revolve120  label="removeToCreateScrewAndThreadedInsertHole048"
  Angle = 360
  Axis = (0,1,0)
  Base = (0,0,0)
  FaceMakerClass = Part::FaceMakerBullseye
  Placement = pos=(30.3,30.3,51.7) rot=(0,0,1;0rad)
  Solid = false
  Source = -> Face112
  Symmetric = false
FEATURE [Part::MultiFuse] Fusion087  label="createThreadedInsertHolesForFan005"
  Shapes = -> [Revolve117,Revolve118,Revolve119,Revolve120]
FEATURE [Part::Extrusion] Extrude047
  Base = -> Sketch056
  Dir = (0,0,1)
  DirMode = 2
  FaceMakerClass = Part::FaceMakerBullseye
  LengthFwd = 72
  LengthRev = 0
  Solid = true
  Symmetric = false
FEATURE [Part::Fillet] Fillet039  label="top019"
  Base = -> Extrude047
  Edges = 1 edges r=2: [Edge35]
FEATURE [Sketcher::SketchObject] Sketch057
  FullyConstrained = false
  Placement = pos=(0,0,0) rot=(1,0,0;1.5708rad)
  sketch-geometry (24):
    g0: ArcOfCircle CenterX=-4 CenterY=-10.5 CenterZ=0 NormalX=0 NormalY=0 NormalZ=1 AngleXU=0 Radius=1.5 StartAngle=6e-16 EndAngle=3.14159
    g1: ArcOfCircle CenterX=-34.2 CenterY=-10.5 CenterZ=0 NormalX=0 NormalY=0 NormalZ=1 AngleXU=0 Radius=1.5 StartAngle=0 EndAngle=3.14159
    g2: ArcOfCircle CenterX=-34.2 CenterY=-27.7 CenterZ=0 NormalX=0 NormalY=0 NormalZ=1 AngleXU=0 Radius=1.5 StartAngle=3.14159 EndAngle=6.28319
    g3: ArcOfCircle CenterX=-4 CenterY=-27.7 CenterZ=0 NormalX=0 NormalY=0 NormalZ=1 AngleXU=0 Radius=1.5 StartAngle=3.1416 EndAngle=6.28319
    g4: ArcOfCircle CenterX=-10 CenterY=-4.3 CenterZ=0 NormalX=0 NormalY=0 NormalZ=1 AngleXU=0 Radius=1.5 StartAngle=2e-16 EndAngle=3.14159
    g5: ArcOfCircle CenterX=-16.1 CenterY=-1.8 CenterZ=0 NormalX=0 NormalY=0 NormalZ=1 AngleXU=0 Radius=1.5 StartAngle=5e-16 EndAngle=3.14159
    g6: ArcOfCircle CenterX=-22.1 CenterY=-1.8 CenterZ=0 NormalX=0 NormalY=0 NormalZ=1 AngleXU=0 Radius=1.5 StartAngle=5e-16 EndAngle=3.14159
    g7: ArcOfCircle CenterX=-28.2 CenterY=-4.3 CenterZ=0 NormalX=0 NormalY=0 NormalZ=1 AngleXU=0 Radius=1.5 StartAngle=2e-16 EndAngle=3.14159
    g8: ArcOfCircle CenterX=-10 CenterY=-33.9 CenterZ=0 NormalX=0 NormalY=0 NormalZ=1 AngleXU=0 Radius=1.5 StartAngle=3.14159 EndAngle=6.28319
    g9: ArcOfCircle CenterX=-16.1 CenterY=-36.4 CenterZ=0 NormalX=0 NormalY=0 NormalZ=1 AngleXU=0 Radius=1.5 StartAngle=3.14159 EndAngle=6.28319
    g10: ArcOfCircle CenterX=-22.1 CenterY=-36.4 CenterZ=0 NormalX=0 NormalY=0 NormalZ=1 AngleXU=0 Radius=1.5 StartAngle=3.14159 EndAngle=6.28319
    g11: ArcOfCircle CenterX=-28.2 CenterY=-33.9 CenterZ=0 NormalX=0 NormalY=0 NormalZ=1 AngleXU=0 Radius=1.5 StartAngle=3.14159 EndAngle=6.28319
    g12: LineSegment StartX=-35.7 StartY=-10.5 StartZ=0 EndX=-35.7 EndY=-27.7 EndZ=0
    g13: LineSegment StartX=-32.7 StartY=-10.5 StartZ=0 EndX=-32.7 EndY=-27.7 EndZ=0
    g14: LineSegment StartX=-29.7 StartY=-33.9 StartZ=0 EndX=-29.7 EndY=-4.3 EndZ=0
    g15: LineSegment StartX=-26.7 StartY=-33.9 StartZ=0 EndX=-26.7 EndY=-4.3 EndZ=0
    g16: LineSegment StartX=-2.5 StartY=-10.5 StartZ=0 EndX=-2.5 EndY=-27.7 EndZ=0
    g17: LineSegment StartX=-8.5 StartY=-4.3 StartZ=0 EndX=-8.5 EndY=-33.9 EndZ=0
    g18: LineSegment StartX=-5.5 StartY=-10.5 StartZ=0 EndX=-5.5 EndY=-27.7 EndZ=0
    g19: LineSegment StartX=-11.5 StartY=-4.3 StartZ=0 EndX=-11.5 EndY=-33.9 EndZ=0
    g20: LineSegment StartX=-14.6 StartY=-1.8 StartZ=0 EndX=-14.6 EndY=-36.4 EndZ=0
    g21: LineSegment StartX=-17.6 StartY=-1.8 StartZ=0 EndX=-17.6 EndY=-36.4 EndZ=0
    g22: LineSegment StartX=-20.6 StartY=-36.4 StartZ=0 EndX=-20.6 EndY=-1.8 EndZ=0
    g23: LineSegment StartX=-23.6 StartY=-1.8 StartZ=0 EndX=-23.6 EndY=-36.4 EndZ=0
  constraints (48):
    c: Block(g0)
    c: Block(g1)
    c: Block(g2)
    c: Block(g3)
    c: Block(g4)
    c: Block(g5)
    c: Block(g6)
    c: Block(g7)
    c: Block(g8)
    c: Block(g9)
    c: Block(g10)
    c: Block(g11)
    c: Coincident(g12,g1)
    c: Coincident(g12,g2)
    c: Vertical(g12)
    c: Coincident(g13,g1)
    c: Coincident(g13,g2)
    c: Vertical(g13)
    c: Coincident(g14,g11)
    c: Coincident(g14,g7)
    c: Vertical(g14)
    c: Coincident(g15,g11)
    c: Coincident(g15,g7)
    c: Vertical(g15)
    c: Coincident(g16,g0)
    c: Coincident(g16,g3)
    c: Vertical(g16)
    c: Coincident(g17,g4)
    c: Coincident(g17,g8)
    c: Vertical(g17)
    c: Coincident(g18,g0)
    c: Coincident(g18,g3)
    c: Vertical(g18)
    c: Coincident(g19,g4)
    c: Coincident(g19,g8)
    c: Vertical(g19)
    c: Coincident(g20,g5)
    c: Coincident(g20,g9)
    c: Vertical(g20)
    c: Coincident(g21,g5)
    c: Coincident(g21,g9)
    c: Vertical(g21)
    c: Coincident(g22,g10)
    c: Coincident(g22,g6)
    c: Vertical(g22)
    c: Coincident(g23,g6)
    c: Coincident(g23,g10)
    c: Vertical(g23)
FEATURE [Part::Extrusion] Extrude048  label="removeToCreateFanGrillHoles004"
  Base = -> Sketch057
  Dir = (0,-1,6e-16)
  DirMode = 2
  FaceMakerClass = Part::FaceMakerBullseye
  LengthFwd = 10
  LengthRev = 0
  Placement = pos=(65.4,44,54.82) rot=(0,0,1;0rad)
  Solid = true
  Symmetric = false
FEATURE [Part::Cut] Cut040  label="top021"
  Base = -> Fillet039
  Tool = -> Extrude048
FEATURE [Part::Cylinder] Cylinder041  label="removeToCreteHoleForPlugHousing034"
  Angle = 360
  AttacherType = Attacher::AttachEngine3D
  Height = 20
  Placement = pos=(-2,19,36) rot=(0,1,0;1.5708rad)
  Radius = 14.3
FEATURE [Part::MultiFuse] Fusion089  label="removeToCreteHoleForPlugHousing035"
  Shapes = -> [Box026,Cylinder041]
FEATURE [Part::Cylinder] Cylinder042
  Angle = 360
  AttacherType = Attacher::AttachEngine3D
  Height = 20
  Placement = pos=(0,0,36.15) rot=(0,0,1;0rad)
  Radius = 14.3
FEATURE [Part::Cylinder] Cylinder043
  Angle = 360
  AttacherType = Attacher::AttachEngine3D
  Height = 10
  Placement = pos=(0,0,36.15) rot=(0,0,1;0rad)
  Radius = 4
FEATURE [Part::Box] Box027  label="removeToCreteHoleForPlugHousing036"
  AttacherType = Attacher::AttachEngine3D
  Height = 28.6
  Length = 20
  Placement = pos=(106.15,0,21.7) rot=(0,0,1;0rad)
  Width = 19
FEATURE [Part::Cut] Cut041  label="top022"
  Base = -> Cut040
  Tool = -> Fusion087
FEATURE [Part::Cut] Cut039  label="top020"
  Base = -> Cut041
  Tool = -> Fusion089
FEATURE [Part::MultiFuse] Fusion090  label="removeToCreteHoleForPlugHousing037"
  Placement = pos=(70,19,36) rot=(0,1,0;1.5708rad)
  Shapes = -> [Cylinder042,Cylinder043]
FEATURE [Part::MultiFuse] Fusion088  label="removeToCreteHoleForPlugHousing033"
  Shapes = -> [Box027,Fusion090]
FEATURE [Part::Cut] Cut042  label="removeToCreteHoleForPlugHousing038"
  Base = -> Cut039
  Tool = -> Fusion088
FEATURE [Part::MultiFuse] Fusion091  label="removeFromTop"
  Shapes = -> [Fillet038,Fusion085,Fusion084,Fusion083,Extrude045]
FEATURE [Part::Cut] Cut043  label="REAL TOP ====="
  Base = -> Fillet036
  Tool = -> Fusion091
FEATURE [Part::MultiFuse] Fusion092  label="caseScrewPillarBracket016"
  Shapes = -> [Extrude030,Extrude031,Extrude032,Extrude033,Extrude034,Extrude035,Extrude036,Extrude037,Box013,Box014]
FEATURE [Sketcher::SketchObject] Sketch058  label="topSketch015"
  FullyConstrained = true
  sketch-geometry (20):
    g0: LineSegment StartX=5.21097e-06 StartY=3 StartZ=0 EndX=5.21097e-06 EndY=19 EndZ=0
    g1: ArcOfCircle CenterX=19 CenterY=19 CenterZ=0 NormalX=0 NormalY=0 NormalZ=1 AngleXU=0 Radius=19 StartAngle=1.5708 EndAngle=3.14159
    g2: ArcOfCircle CenterX=19 CenterY=19 CenterZ=0 NormalX=0 NormalY=0 NormalZ=1 AngleXU=0 Radius=16 StartAngle=1.5708 EndAngle=3.14159
    g3: LineSegment StartX=114 StartY=35 StartZ=0 EndX=19 EndY=35 EndZ=0
    g4: LineSegment StartX=5.21097e-06 StartY=3 StartZ=0 EndX=5.21097e-06 EndY=0 EndZ=0
    g5: LineSegment StartX=3 StartY=0 StartZ=0 EndX=5.21097e-06 EndY=0 EndZ=0
    g6: LineSegment StartX=3 StartY=19 StartZ=0 EndX=3 EndY=0 EndZ=0
    g7: LineSegment StartX=19 StartY=38 StartZ=0 EndX=124 EndY=38 EndZ=0
    g8: Circle CenterX=119 CenterY=35 CenterZ=0 NormalX=0 NormalY=0 NormalZ=1 AngleXU=0 Radius=1
    g9: Circle CenterX=121 CenterY=35 CenterZ=0 NormalX=0 NormalY=0 NormalZ=1 AngleXU=0 Radius=1
    g10: Circle CenterX=121 CenterY=33 CenterZ=0 NormalX=0 NormalY=0 NormalZ=1 AngleXU=0 Radius=1
    g11: BSplineCurve PolesCount=3 KnotsCount=2 Degree=2 IsPeriodic=0
    g12: GeomPoint X=119 Y=35 Z=0
    g13: GeomPoint X=121 Y=33 Z=0
    g14: LineSegment StartX=119 StartY=35 StartZ=0 EndX=114 EndY=35 EndZ=0
    g15: ArcOfCircle CenterX=105 CenterY=19 CenterZ=0 NormalX=0 NormalY=0 NormalZ=1 AngleXU=0 Radius=19 StartAngle=5.7297 EndAngle=6.28319
    g16: ArcOfCircle CenterX=105 CenterY=19 CenterZ=0 NormalX=0 NormalY=0 NormalZ=1 AngleXU=0 Radius=16 StartAngle=5.60905 EndAngle=6.28319
    g17: LineSegment StartX=121 StartY=33 StartZ=0 EndX=121 EndY=19 EndZ=0
    g18: LineSegment StartX=124 StartY=38 StartZ=0 EndX=124 EndY=19 EndZ=0
    g19: LineSegment StartX=117.5 StartY=9.01251 StartZ=0 EndX=121.163 EndY=9.0125 EndZ=0
  constraints (46):
    c: Vertical(g0)
    c: Block(g0)
    c: Coincident(g1,g0)
    c: Block(g1)
    c: Coincident(g2,g1)
    c: Block(g2)
    c: Coincident(g3,g2)
    c: Horizontal(g3)
    c: Tangent(g3,g2)
    c: Coincident(g4,g0)
    c: Distance(g4) = 3
    c: Vertical(g4)
    c: Coincident(g5,g4)
    c: Horizontal(g5)
    c: Coincident(g6,g2)
    c: Coincident(g6,g5)
    c: Vertical(g6)
    c: Horizontal(g7)
    c: Distance(g7) = 105
    c: Coincident(g7,g1)
    c: Block(g3)
    c: Weight(g8) = 1
    c: Equal(g8,g9)
    c: Equal(g8,g10)
    c: InternalAlignment(g8,g11)
    c: InternalAlignment(g9,g11)
    c: InternalAlignment(g10,g11)
    c: InternalAlignment(g12,g11)
    c: InternalAlignment(g13,g11)
    c: Block(g11)
    c: Coincident(g14,g11)
    c: Coincident(g14,g3)
    c: Horizontal(g14)
    c: Block(g15)
    c: Coincident(g16,g15)
    c: Block(g16)
    c: Coincident(g17,g11)
    c: Coincident(g17,g16)
    c: Vertical(g17)
    c: Distance(g17) = 14
    c: Coincident(g18,g7)
    c: Coincident(g18,g15)
    c: Vertical(g18)
    c: Distance(g18) = 19
    c: Coincident(g19,g16)
    c: Coincident(g19,g15)
FEATURE [Part::Extrusion] Extrude049  label="top023"
  Base = -> Sketch058
  Dir = (0,0,1)
  DirMode = 2
  FaceMakerClass = Part::FaceMakerBullseye
  LengthFwd = 72
  LengthRev = 0
  Solid = true
  Symmetric = false
FEATURE [Sketcher::SketchObject] Sketch059
  FullyConstrained = true
  MapMode = 3
  Placement = pos=(0,0,0) rot=(1,0,0;1.5708rad)
  Support = -> [Extrude049]
  sketch-geometry (8):
    g0: Circle CenterX=80.351 CenterY=-67.6202 CenterZ=0 NormalX=0 NormalY=0 NormalZ=1 AngleXU=0 Radius=2
    g1: Circle CenterX=80.351 CenterY=-67.6202 CenterZ=0 NormalX=0 NormalY=0 NormalZ=1 AngleXU=0 Radius=3
    g2: Circle CenterX=80.351 CenterY=-4.92017 CenterZ=0 NormalX=0 NormalY=0 NormalZ=1 AngleXU=0 Radius=2
    g3: Circle CenterX=80.351 CenterY=-4.92017 CenterZ=0 NormalX=0 NormalY=0 NormalZ=1 AngleXU=0 Radius=3
    g4: Circle CenterX=23.851 CenterY=-4.92017 CenterZ=0 NormalX=0 NormalY=0 NormalZ=1 AngleXU=0 Radius=2
    g5: Circle CenterX=23.851 CenterY=-4.92017 CenterZ=0 NormalX=0 NormalY=0 NormalZ=1 AngleXU=0 Radius=3
    g6: Circle CenterX=23.851 CenterY=-67.6202 CenterZ=0 NormalX=0 NormalY=0 NormalZ=1 AngleXU=0 Radius=2
    g7: Circle CenterX=23.851 CenterY=-67.6202 CenterZ=0 NormalX=0 NormalY=0 NormalZ=1 AngleXU=0 Radius=3
  constraints (8):
    c: Block(g3)
    c: Block(g2)
    c: Block(g1)
    c: Block(g0)
    c: Block(g6)
    c: Block(g7)
    c: Block(g4)
    c: Block(g5)
FEATURE [Sketcher::SketchObject] Sketch060
  FullyConstrained = true
  MapMode = 3
  Placement = pos=(0,0,0) rot=(1,0,0;1.5708rad)
  Support = -> [Extrude049]
  sketch-geometry (8):
    g0: Circle CenterX=80.351 CenterY=-67.6202 CenterZ=0 NormalX=0 NormalY=0 NormalZ=1 AngleXU=0 Radius=3
    g1: Circle CenterX=80.351 CenterY=-4.92017 CenterZ=0 NormalX=0 NormalY=0 NormalZ=1 AngleXU=0 Radius=3
    g2: Circle CenterX=23.851 CenterY=-4.92017 CenterZ=0 NormalX=0 NormalY=0 NormalZ=1 AngleXU=0 Radius=3
    g3: Circle CenterX=23.851 CenterY=-67.6202 CenterZ=0 NormalX=0 NormalY=0 NormalZ=1 AngleXU=0 Radius=3
    g4: Circle CenterX=23.851 CenterY=-67.6202 CenterZ=0 NormalX=0 NormalY=0 NormalZ=1 AngleXU=0 Radius=5
    g5: Circle CenterX=80.351 CenterY=-67.6202 CenterZ=0 NormalX=0 NormalY=0 NormalZ=1 AngleXU=0 Radius=5
    g6: Circle CenterX=23.851 CenterY=-4.92017 CenterZ=0 NormalX=0 NormalY=0 NormalZ=1 AngleXU=0 Radius=5
    g7: Circle CenterX=80.351 CenterY=-4.92017 CenterZ=0 NormalX=0 NormalY=0 NormalZ=1 AngleXU=0 Radius=5
  constraints (8):
    c: Block(g1)
    c: Block(g0)
    c: Block(g3)
    c: Block(g2)
    c: Block(g5)
    c: Block(g4)
    c: Block(g6)
    c: Block(g7)
FEATURE [Sketcher::SketchObject] Sketch061
  FullyConstrained = true
  MapMode = 3
  Placement = pos=(0,0,0) rot=(1,0,0;1.5708rad)
  sketch-geometry (8):
    g0: Circle CenterX=80.351 CenterY=-67.6202 CenterZ=0 NormalX=0 NormalY=0 NormalZ=1 AngleXU=0 Radius=3
    g1: Circle CenterX=80.351 CenterY=-4.92017 CenterZ=0 NormalX=0 NormalY=0 NormalZ=1 AngleXU=0 Radius=3
    g2: Circle CenterX=23.851 CenterY=-4.92017 CenterZ=0 NormalX=0 NormalY=0 NormalZ=1 AngleXU=0 Radius=3
    g3: Circle CenterX=23.851 CenterY=-67.6202 CenterZ=0 NormalX=0 NormalY=0 NormalZ=1 AngleXU=0 Radius=3
    g4: Circle CenterX=23.851 CenterY=-67.6202 CenterZ=0 NormalX=0 NormalY=0 NormalZ=1 AngleXU=0 Radius=5
    g5: Circle CenterX=80.351 CenterY=-67.6202 CenterZ=0 NormalX=0 NormalY=0 NormalZ=1 AngleXU=0 Radius=5
    g6: Circle CenterX=23.851 CenterY=-4.92017 CenterZ=0 NormalX=0 NormalY=0 NormalZ=1 AngleXU=0 Radius=5
    g7: Circle CenterX=80.351 CenterY=-4.92017 CenterZ=0 NormalX=0 NormalY=0 NormalZ=1 AngleXU=0 Radius=5
  constraints (8):
    c: Block(g1)
    c: Block(g0)
    c: Block(g3)
    c: Block(g2)
    c: Block(g5)
    c: Block(g4)
    c: Block(g6)
    c: Block(g7)
FEATURE [Sketcher::SketchObject] Sketch062  label="topSketch016"
  FullyConstrained = true
  sketch-geometry (20):
    g0: LineSegment StartX=5.21097e-06 StartY=3 StartZ=0 EndX=5.21097e-06 EndY=19 EndZ=0
    g1: ArcOfCircle CenterX=19 CenterY=19 CenterZ=0 NormalX=0 NormalY=0 NormalZ=1 AngleXU=0 Radius=19 StartAngle=1.5708 EndAngle=3.14159
    g2: ArcOfCircle CenterX=19 CenterY=19 CenterZ=0 NormalX=0 NormalY=0 NormalZ=1 AngleXU=0 Radius=16 StartAngle=1.5708 EndAngle=3.14159
    g3: LineSegment StartX=114 StartY=35 StartZ=0 EndX=19 EndY=35 EndZ=0
    g4: LineSegment StartX=5.21097e-06 StartY=3 StartZ=0 EndX=5.21097e-06 EndY=0 EndZ=0
    g5: LineSegment StartX=3 StartY=0 StartZ=0 EndX=5.21097e-06 EndY=0 EndZ=0
    g6: LineSegment StartX=3 StartY=19 StartZ=0 EndX=3 EndY=0 EndZ=0
    g7: LineSegment StartX=19 StartY=38 StartZ=0 EndX=124 EndY=38 EndZ=0
    g8: Circle CenterX=119 CenterY=35 CenterZ=0 NormalX=0 NormalY=0 NormalZ=1 AngleXU=0 Radius=1
    g9: Circle CenterX=121 CenterY=35 CenterZ=0 NormalX=0 NormalY=0 NormalZ=1 AngleXU=0 Radius=1
    g10: Circle CenterX=121 CenterY=33 CenterZ=0 NormalX=0 NormalY=0 NormalZ=1 AngleXU=0 Radius=1
    g11: BSplineCurve PolesCount=3 KnotsCount=2 Degree=2 IsPeriodic=0
    g12: GeomPoint X=119 Y=35 Z=0
    g13: GeomPoint X=121 Y=33 Z=0
    g14: LineSegment StartX=119 StartY=35 StartZ=0 EndX=114 EndY=35 EndZ=0
    g15: ArcOfCircle CenterX=105 CenterY=19 CenterZ=0 NormalX=0 NormalY=0 NormalZ=1 AngleXU=0 Radius=19 StartAngle=5.7297 EndAngle=6.28319
    g16: ArcOfCircle CenterX=105 CenterY=19 CenterZ=0 NormalX=0 NormalY=0 NormalZ=1 AngleXU=0 Radius=16 StartAngle=5.60905 EndAngle=6.28319
    g17: LineSegment StartX=121 StartY=33 StartZ=0 EndX=121 EndY=19 EndZ=0
    g18: LineSegment StartX=124 StartY=38 StartZ=0 EndX=124 EndY=19 EndZ=0
    g19: LineSegment StartX=117.5 StartY=9.01251 StartZ=0 EndX=121.163 EndY=9.0125 EndZ=0
  constraints (46):
    c: Vertical(g0)
    c: Block(g0)
    c: Coincident(g1,g0)
    c: Block(g1)
    c: Coincident(g2,g1)
    c: Block(g2)
    c: Coincident(g3,g2)
    c: Horizontal(g3)
    c: Tangent(g3,g2)
    c: Coincident(g4,g0)
    c: Distance(g4) = 3
    c: Vertical(g4)
    c: Coincident(g5,g4)
    c: Horizontal(g5)
    c: Coincident(g6,g2)
    c: Coincident(g6,g5)
    c: Vertical(g6)
    c: Horizontal(g7)
    c: Distance(g7) = 105
    c: Coincident(g7,g1)
    c: Block(g3)
    c: Weight(g8) = 1
    c: Equal(g8,g9)
    c: Equal(g8,g10)
    c: InternalAlignment(g8,g11)
    c: InternalAlignment(g9,g11)
    c: InternalAlignment(g10,g11)
    c: InternalAlignment(g12,g11)
    c: InternalAlignment(g13,g11)
    c: Block(g11)
    c: Coincident(g14,g11)
    c: Coincident(g14,g3)
    c: Horizontal(g14)
    c: Block(g15)
    c: Coincident(g16,g15)
    c: Block(g16)
    c: Coincident(g17,g11)
    c: Coincident(g17,g16)
    c: Vertical(g17)
    c: Distance(g17) = 14
    c: Coincident(g18,g7)
    c: Coincident(g18,g15)
    c: Vertical(g18)
    c: Distance(g18) = 19
    c: Coincident(g19,g16)
    c: Coincident(g19,g15)
FEATURE [Part::Extrusion] Extrude053  label="top024"
  Base = -> Sketch062
  Dir = (0,0,1)
  DirMode = 2
  FaceMakerClass = Part::FaceMakerBullseye
  LengthFwd = 72
  LengthRev = 0
  Solid = true
  Symmetric = false
FEATURE [Sketcher::SketchObject] Sketch063
  FullyConstrained = true
  MapMode = 3
  Placement = pos=(0,0,0) rot=(1,0,0;1.5708rad)
  Support = -> [Extrude053]
  sketch-geometry (8):
    g0: Circle CenterX=80.351 CenterY=-67.6202 CenterZ=0 NormalX=0 NormalY=0 NormalZ=1 AngleXU=0 Radius=2
    g1: Circle CenterX=80.351 CenterY=-67.6202 CenterZ=0 NormalX=0 NormalY=0 NormalZ=1 AngleXU=0 Radius=3
    g2: Circle CenterX=80.351 CenterY=-4.92017 CenterZ=0 NormalX=0 NormalY=0 NormalZ=1 AngleXU=0 Radius=2
    g3: Circle CenterX=80.351 CenterY=-4.92017 CenterZ=0 NormalX=0 NormalY=0 NormalZ=1 AngleXU=0 Radius=3
    g4: Circle CenterX=23.851 CenterY=-4.92017 CenterZ=0 NormalX=0 NormalY=0 NormalZ=1 AngleXU=0 Radius=2
    g5: Circle CenterX=23.851 CenterY=-4.92017 CenterZ=0 NormalX=0 NormalY=0 NormalZ=1 AngleXU=0 Radius=3
    g6: Circle CenterX=23.851 CenterY=-67.6202 CenterZ=0 NormalX=0 NormalY=0 NormalZ=1 AngleXU=0 Radius=2
    g7: Circle CenterX=23.851 CenterY=-67.6202 CenterZ=0 NormalX=0 NormalY=0 NormalZ=1 AngleXU=0 Radius=3
  constraints (8):
    c: Block(g3)
    c: Block(g2)
    c: Block(g1)
    c: Block(g0)
    c: Block(g6)
    c: Block(g7)
    c: Block(g4)
    c: Block(g5)
FEATURE [Part::Extrusion] Extrude054
  Base = -> Sketch063
  Dir = (0,-1,2e-16)
  DirMode = 2
  FaceMakerClass = Part::FaceMakerBullseye
  LengthFwd = 6
  LengthRev = 0
  Placement = pos=(0,9,0) rot=(0,0,1;0rad)
  Solid = true
  Symmetric = false
FEATURE [Sketcher::SketchObject] Sketch064  label="topSketch017"
  FullyConstrained = true
  sketch-geometry (20):
    g0: LineSegment StartX=5.21097e-06 StartY=3 StartZ=0 EndX=5.21097e-06 EndY=19 EndZ=0
    g1: ArcOfCircle CenterX=19 CenterY=19 CenterZ=0 NormalX=0 NormalY=0 NormalZ=1 AngleXU=0 Radius=19 StartAngle=1.5708 EndAngle=3.14159
    g2: ArcOfCircle CenterX=19 CenterY=19 CenterZ=0 NormalX=0 NormalY=0 NormalZ=1 AngleXU=0 Radius=16 StartAngle=1.5708 EndAngle=3.14159
    g3: LineSegment StartX=114 StartY=35 StartZ=0 EndX=19 EndY=35 EndZ=0
    g4: LineSegment StartX=5.21097e-06 StartY=3 StartZ=0 EndX=5.21097e-06 EndY=0 EndZ=0
    g5: LineSegment StartX=3 StartY=0 StartZ=0 EndX=5.21097e-06 EndY=0 EndZ=0
    g6: LineSegment StartX=3 StartY=19 StartZ=0 EndX=3 EndY=0 EndZ=0
    g7: LineSegment StartX=19 StartY=38 StartZ=0 EndX=124 EndY=38 EndZ=0
    g8: Circle CenterX=119 CenterY=35 CenterZ=0 NormalX=0 NormalY=0 NormalZ=1 AngleXU=0 Radius=1
    g9: Circle CenterX=121 CenterY=35 CenterZ=0 NormalX=0 NormalY=0 NormalZ=1 AngleXU=0 Radius=1
    g10: Circle CenterX=121 CenterY=33 CenterZ=0 NormalX=0 NormalY=0 NormalZ=1 AngleXU=0 Radius=1
    g11: BSplineCurve PolesCount=3 KnotsCount=2 Degree=2 IsPeriodic=0
    g12: GeomPoint X=119 Y=35 Z=0
    g13: GeomPoint X=121 Y=33 Z=0
    g14: LineSegment StartX=119 StartY=35 StartZ=0 EndX=114 EndY=35 EndZ=0
    g15: ArcOfCircle CenterX=105 CenterY=19 CenterZ=0 NormalX=0 NormalY=0 NormalZ=1 AngleXU=0 Radius=19 StartAngle=5.7297 EndAngle=6.28319
    g16: ArcOfCircle CenterX=105 CenterY=19 CenterZ=0 NormalX=0 NormalY=0 NormalZ=1 AngleXU=0 Radius=16 StartAngle=5.60905 EndAngle=6.28319
    g17: LineSegment StartX=121 StartY=33 StartZ=0 EndX=121 EndY=19 EndZ=0
    g18: LineSegment StartX=124 StartY=38 StartZ=0 EndX=124 EndY=19 EndZ=0
    g19: LineSegment StartX=117.5 StartY=9.01251 StartZ=0 EndX=121.163 EndY=9.0125 EndZ=0
  constraints (46):
    c: Vertical(g0)
    c: Block(g0)
    c: Coincident(g1,g0)
    c: Block(g1)
    c: Coincident(g2,g1)
    c: Block(g2)
    c: Coincident(g3,g2)
    c: Horizontal(g3)
    c: Tangent(g3,g2)
    c: Coincident(g4,g0)
    c: Distance(g4) = 3
    c: Vertical(g4)
    c: Coincident(g5,g4)
    c: Horizontal(g5)
    c: Coincident(g6,g2)
    c: Coincident(g6,g5)
    c: Vertical(g6)
    c: Horizontal(g7)
    c: Distance(g7) = 105
    c: Coincident(g7,g1)
    c: Block(g3)
    c: Weight(g8) = 1
    c: Equal(g8,g9)
    c: Equal(g8,g10)
    c: InternalAlignment(g8,g11)
    c: InternalAlignment(g9,g11)
    c: InternalAlignment(g10,g11)
    c: InternalAlignment(g12,g11)
    c: InternalAlignment(g13,g11)
    c: Block(g11)
    c: Coincident(g14,g11)
    c: Coincident(g14,g3)
    c: Horizontal(g14)
    c: Block(g15)
    c: Coincident(g16,g15)
    c: Block(g16)
    c: Coincident(g17,g11)
    c: Coincident(g17,g16)
    c: Vertical(g17)
    c: Distance(g17) = 14
    c: Coincident(g18,g7)
    c: Coincident(g18,g15)
    c: Vertical(g18)
    c: Distance(g18) = 19
    c: Coincident(g19,g16)
    c: Coincident(g19,g15)
FEATURE [Sketcher::SketchObject] Sketch065
  FullyConstrained = true
  MapMode = 3
  Placement = pos=(0,0,0) rot=(1,0,0;1.5708rad)
  sketch-geometry (8):
    g0: Circle CenterX=80.351 CenterY=-67.6202 CenterZ=0 NormalX=0 NormalY=0 NormalZ=1 AngleXU=0 Radius=3
    g1: Circle CenterX=80.351 CenterY=-4.92017 CenterZ=0 NormalX=0 NormalY=0 NormalZ=1 AngleXU=0 Radius=3
    g2: Circle CenterX=23.851 CenterY=-4.92017 CenterZ=0 NormalX=0 NormalY=0 NormalZ=1 AngleXU=0 Radius=3
    g3: Circle CenterX=23.851 CenterY=-67.6202 CenterZ=0 NormalX=0 NormalY=0 NormalZ=1 AngleXU=0 Radius=3
    g4: Circle CenterX=23.851 CenterY=-67.6202 CenterZ=0 NormalX=0 NormalY=0 NormalZ=1 AngleXU=0 Radius=5
    g5: Circle CenterX=80.351 CenterY=-67.6202 CenterZ=0 NormalX=0 NormalY=0 NormalZ=1 AngleXU=0 Radius=5
    g6: Circle CenterX=23.851 CenterY=-4.92017 CenterZ=0 NormalX=0 NormalY=0 NormalZ=1 AngleXU=0 Radius=5
    g7: Circle CenterX=80.351 CenterY=-4.92017 CenterZ=0 NormalX=0 NormalY=0 NormalZ=1 AngleXU=0 Radius=5
  constraints (8):
    c: Block(g1)
    c: Block(g0)
    c: Block(g3)
    c: Block(g2)
    c: Block(g5)
    c: Block(g4)
    c: Block(g6)
    c: Block(g7)
FEATURE [Part::Extrusion] Extrude056
  Base = -> Sketch065
  Dir = (0,-1,2e-16)
  DirMode = 2
  FaceMakerClass = Part::FaceMakerBullseye
  LengthFwd = 2
  LengthRev = 0
  Solid = true
  Symmetric = false
FEATURE [Part::Extrusion] Extrude057  label="top025"
  Base = -> Sketch064
  Dir = (0,0,1)
  DirMode = 2
  FaceMakerClass = Part::FaceMakerBullseye
  LengthFwd = 72
  LengthRev = 0
  Solid = true
  Symmetric = false
FEATURE [Sketcher::SketchObject] Sketch066
  FullyConstrained = true
  MapMode = 3
  Placement = pos=(0,0,0) rot=(1,0,0;1.5708rad)
  Support = -> [Extrude057]
  sketch-geometry (8):
    g0: Circle CenterX=80.351 CenterY=-67.6202 CenterZ=0 NormalX=0 NormalY=0 NormalZ=1 AngleXU=0 Radius=3
    g1: Circle CenterX=80.351 CenterY=-4.92017 CenterZ=0 NormalX=0 NormalY=0 NormalZ=1 AngleXU=0 Radius=3
    g2: Circle CenterX=23.851 CenterY=-4.92017 CenterZ=0 NormalX=0 NormalY=0 NormalZ=1 AngleXU=0 Radius=3
    g3: Circle CenterX=23.851 CenterY=-67.6202 CenterZ=0 NormalX=0 NormalY=0 NormalZ=1 AngleXU=0 Radius=3
    g4: Circle CenterX=23.851 CenterY=-67.6202 CenterZ=0 NormalX=0 NormalY=0 NormalZ=1 AngleXU=0 Radius=5
    g5: Circle CenterX=80.351 CenterY=-67.6202 CenterZ=0 NormalX=0 NormalY=0 NormalZ=1 AngleXU=0 Radius=5
    g6: Circle CenterX=23.851 CenterY=-4.92017 CenterZ=0 NormalX=0 NormalY=0 NormalZ=1 AngleXU=0 Radius=5
    g7: Circle CenterX=80.351 CenterY=-4.92017 CenterZ=0 NormalX=0 NormalY=0 NormalZ=1 AngleXU=0 Radius=5
  constraints (8):
    c: Block(g1)
    c: Block(g0)
    c: Block(g3)
    c: Block(g2)
    c: Block(g5)
    c: Block(g4)
    c: Block(g6)
    c: Block(g7)
FEATURE [Part::Extrusion] Extrude055
  Base = -> Sketch066
  Dir = (0,-1,2e-16)
  DirMode = 2
  FaceMakerClass = Part::FaceMakerBullseye
  LengthFwd = 2
  LengthRev = 0
  Solid = true
  Symmetric = false
FEATURE [Part::Fillet] Fillet041
  Base = -> Extrude056
  Edges = 4 edges r=1.99: [Edge6,Edge12,Edge18,Edge24]
FEATURE [Part::Cut] Cut045
  Base = -> Extrude055
  Placement = pos=(0,6,0) rot=(0,0,1;0rad)
  Tool = -> Fillet041
FEATURE [Part::MultiFuse] Fusion095  label="pcbScrewPillars"
  Placement = pos=(-3.2,-1,72.3) rot=(0,0,1;0rad)
  Shapes = -> [Cut045,Extrude054]
FEATURE [Part::Feature] Face113
  shape: bbox 3.2 x 1.5 x 2e-07 mm, 1 faces, 0 solids (baked)
FEATURE [Part::Revolution] Revolve121  label="backCaseScrewRetainer002"
  Angle = 360
  Axis = (0,1,0)
  Base = (0,0,0)
  FaceMakerClass = Part::FaceMakerBullseye
  Placement = pos=(12.5,3,62) rot=(0,0,1;0rad)
  Solid = false
  Source = -> Face113
  Symmetric = false
FEATURE [Part::Feature] Face114
  shape: bbox 3.2 x 1.5 x 2e-07 mm, 1 faces, 0 solids (baked)
FEATURE [Part::Feature] Face115
  shape: bbox 3.2 x 1.5 x 2e-07 mm, 1 faces, 0 solids (baked)
FEATURE [Part::Feature] Face116
  shape: bbox 3.2 x 1.5 x 2e-07 mm, 1 faces, 0 solids (baked)
FEATURE [Part::Revolution] Revolve122  label="frontCaseScrewRetainer004"
  Angle = 360
  Axis = (0,1,0)
  Base = (0,0,0)
  FaceMakerClass = Part::FaceMakerBullseye
  Placement = pos=(89.5,3,68.5) rot=(0,0,1;0rad)
  Solid = false
  Source = -> Face115
  Symmetric = false
FEATURE [Part::Revolution] Revolve123  label="frontCaseScrewRetainer005"
  Angle = 360
  Axis = (0,1,0)
  Base = (0,0,0)
  FaceMakerClass = Part::FaceMakerBullseye
  Placement = pos=(89.5,3,3.5) rot=(0,0,1;0rad)
  Solid = false
  Source = -> Face116
  Symmetric = false
FEATURE [Part::Revolution] Revolve124  label="backCaseScrewRetainer003"
  Angle = 360
  Axis = (0,1,0)
  Base = (0,0,0)
  FaceMakerClass = Part::FaceMakerBullseye
  Placement = pos=(12.5,3,10) rot=(0,0,1;0rad)
  Solid = false
  Source = -> Face114
  Symmetric = false
FEATURE [Part::Feature] Face117
  shape: bbox 3.6 x 3.2 x 2e-07 mm, 1 faces, 0 solids (baked)
FEATURE [Part::Revolution] Revolve125  label="moreFrontCaseScrewRetainer004"
  Angle = 360
  Axis = (0,1,0)
  Base = (0,0,0)
  FaceMakerClass = Part::FaceMakerBullseye
  Placement = pos=(109.5,4.5,68.5) rot=(0,0,1;0rad)
  Solid = false
  Source = -> Face117
  Symmetric = false
FEATURE [Part::Feature] Face118
  shape: bbox 3.6 x 3.2 x 2e-07 mm, 1 faces, 0 solids (baked)
FEATURE [Part::Revolution] Revolve126  label="moreFrontCaseScrewRetainer005"
  Angle = 360
  Axis = (0,1,0)
  Base = (0,0,0)
  FaceMakerClass = Part::FaceMakerBullseye
  Placement = pos=(109.5,4.5,3.5) rot=(0,0,1;0rad)
  Solid = false
  Source = -> Face118
  Symmetric = false
FEATURE [Part::MultiFuse] Fusion096  label="screwRetainers001"
  Shapes = -> [Revolve126,Revolve125,Revolve124,Revolve123,Revolve122,Revolve121]
FEATURE [Part::Feature] Face119
  shape: bbox 10 x 16.5 x 2e-07 mm, 1 faces, 0 solids (baked)
FEATURE [Part::Revolution] Revolve130  label="plugHousing050"
  Angle = 360
  Axis = (0,1,0)
  Base = (0,0,0)
  FaceMakerClass = Part::FaceMakerBullseye
  Placement = pos=(0,0,36.15) rot=(0,0,1;0rad)
  Solid = false
  Source = -> Face119
  Symmetric = false
FEATURE [Part::Feature] Face120
  shape: bbox 10 x 16.5 x 2e-07 mm, 1 faces, 0 solids (baked)
FEATURE [Part::Feature] Face121
  shape: bbox 10 x 16.5 x 2e-07 mm, 1 faces, 0 solids (baked)
FEATURE [Part::Revolution] Revolve127  label="plugHousing047"
  Angle = 360
  Axis = (0,1,0)
  Base = (0,0,0)
  FaceMakerClass = Part::FaceMakerBullseye
  Placement = pos=(0,0,36.15) rot=(0,0,1;0rad)
  Solid = false
  Source = -> Face121
  Symmetric = false
FEATURE [Part::Feature] Face122
  shape: bbox 10 x 16.5 x 2e-07 mm, 1 faces, 0 solids (baked)
FEATURE [Part::Feature] Face123
  shape: bbox 10 x 16.5 x 2e-07 mm, 1 faces, 0 solids (baked)
FEATURE [Part::Revolution] Revolve128  label="plugHousing048"
  Angle = 360
  Axis = (0,1,0)
  Base = (0,0,0)
  FaceMakerClass = Part::FaceMakerBullseye
  Placement = pos=(0,0,36.15) rot=(0,0,1;0rad)
  Solid = false
  Source = -> Face123
  Symmetric = false
FEATURE [Part::MultiFuse] Fusion100  label="plugHousing054"
  Placement = pos=(0,0,0) rot=(0,0,1;1.5708rad)
  Shapes = -> [Revolve130,Revolve128]
FEATURE [Part::Feature] Face124
  shape: bbox 10 x 16.5 x 2e-07 mm, 1 faces, 0 solids (baked)
FEATURE [Part::Feature] Face125
  shape: bbox 10 x 16.5 x 2e-07 mm, 1 faces, 0 solids (baked)
FEATURE [Part::Revolution] Revolve129  label="plugHousing049"
  Angle = 360
  Axis = (0,1,0)
  Base = (0,0,0)
  FaceMakerClass = Part::FaceMakerBullseye
  Placement = pos=(0,0,36.15) rot=(0,0,1;0rad)
  Solid = false
  Source = -> Face125
  Symmetric = false
FEATURE [Part::Feature] Face126
  shape: bbox 10 x 16.5 x 2e-07 mm, 1 faces, 0 solids (baked)
FEATURE [Part::Revolution] Revolve131  label="plugHousing058"
  Angle = 360
  Axis = (0,1,0)
  Base = (0,0,0)
  FaceMakerClass = Part::FaceMakerBullseye
  Placement = pos=(0,0,36.15) rot=(0,0,1;0rad)
  Solid = false
  Source = -> Face120
  Symmetric = false
FEATURE [Part::MultiFuse] Fusion099  label="plugHousing053"
  Placement = pos=(0,0,0) rot=(0,0,1;1.5708rad)
  Shapes = -> [Revolve127,Revolve131]
FEATURE [Part::MultiFuse] Fusion102  label="plugHousing056"
  Placement = pos=(0,19,0) rot=(0,0,1;3.14159rad)
  Shapes = -> [Fusion100,Fusion099]
FEATURE [Part::Revolution] Revolve132  label="plugHousing059"
  Angle = 360
  Axis = (0,1,0)
  Base = (0,0,0)
  FaceMakerClass = Part::FaceMakerBullseye
  Placement = pos=(0,0,36.15) rot=(0,0,1;0rad)
  Solid = false
  Source = -> Face126
  Symmetric = false
FEATURE [Part::Revolution] Revolve133  label="plugHousing060"
  Angle = 360
  Axis = (0,1,0)
  Base = (0,0,0)
  FaceMakerClass = Part::FaceMakerBullseye
  Placement = pos=(0,0,36.15) rot=(0,0,1;0rad)
  Solid = false
  Source = -> Face122
  Symmetric = false
FEATURE [Part::MultiFuse] Fusion097  label="plugHousing051"
  Placement = pos=(0,0,0) rot=(0,0,1;1.5708rad)
  Shapes = -> [Revolve133,Revolve132]
FEATURE [Part::Revolution] Revolve134  label="plugHousing061"
  Angle = 360
  Axis = (0,1,0)
  Base = (0,0,0)
  FaceMakerClass = Part::FaceMakerBullseye
  Placement = pos=(0,0,36.15) rot=(0,0,1;0rad)
  Solid = false
  Source = -> Face124
  Symmetric = false
FEATURE [Part::MultiFuse] Fusion101  label="plugHousing055"
  Placement = pos=(0,0,0) rot=(0,0,1;1.5708rad)
  Shapes = -> [Revolve129,Revolve134]
FEATURE [Part::MultiFuse] Fusion098  label="plugHousing052"
  Placement = pos=(0,19,0) rot=(0,0,1;3.14159rad)
  Shapes = -> [Fusion097,Fusion101]
FEATURE [Part::MultiFuse] Fusion103  label="plugHousing057"
  Placement = pos=(122.621,0,-0.15) rot=(0,0,1;0rad)
  Shapes = -> [Fusion102,Fusion098]
FEATURE [Part::Box] Box028  label="Cube015"
  AttacherType = Attacher::AttachEngine3D
  Height = 28
  Length = 3
  Placement = pos=(110.7,19,22) rot=(0,0,1;0rad)
  Width = 15.7
FEATURE [Part::Cylinder] Cylinder044
  Angle = 360
  AttacherType = Attacher::AttachEngine3D
  Height = 20
  Placement = pos=(0,0,36.15) rot=(0,0,1;0rad)
  Radius = 10.3
FEATURE [Part::Cylinder] Cylinder045
  Angle = 360
  AttacherType = Attacher::AttachEngine3D
  Height = 10
  Placement = pos=(0,0,36.15) rot=(0,0,1;0rad)
  Radius = 4
FEATURE [Part::MultiFuse] Fusion104  label="removeToCreteHoleForPlugHousing040"
  Placement = pos=(70,19,36) rot=(0,1,0;1.5708rad)
  Shapes = -> [Cylinder044,Cylinder045]
FEATURE [Part::Cut] Cut046  label="plugHousingTab003"
  Base = -> Box028
  Tool = -> Fusion104
FEATURE [Part::MultiFuse] Fusion105  label="plugHousing062"
  Shapes = -> [Fusion103,Cut046]
FEATURE [Part::Fillet] Fillet042
  Base = -> Fusion105
  Edges = 1 edges r=2: [Edge25]
FEATURE [Part::Fillet] Fillet043  label="plugHousing063"
  Base = -> Fillet042
  Edges = 1 edges r=2: [Edge8]
  Placement = pos=(7,0,0) rot=(0,0,1;0rad)
FEATURE [Part::Feature] Face127
  shape: bbox 10 x 16.5 x 2e-07 mm, 1 faces, 0 solids (baked)
FEATURE [Part::Feature] Face128
  shape: bbox 10 x 16.5 x 2e-07 mm, 1 faces, 0 solids (baked)
FEATURE [Part::Revolution] Revolve137  label="plugHousing070"
  Angle = 360
  Axis = (0,1,0)
  Base = (0,0,0)
  FaceMakerClass = Part::FaceMakerBullseye
  Placement = pos=(0,0,36.15) rot=(0,0,1;0rad)
  Solid = false
  Source = -> Face127
  Symmetric = false
FEATURE [Part::Revolution] Revolve140  label="plugHousing073"
  Angle = 360
  Axis = (0,1,0)
  Base = (0,0,0)
  FaceMakerClass = Part::FaceMakerBullseye
  Placement = pos=(0,0,36.15) rot=(0,0,1;0rad)
  Solid = false
  Source = -> Face128
  Symmetric = false
FEATURE [Part::Feature] Face129
  shape: bbox 10 x 16.5 x 2e-07 mm, 1 faces, 0 solids (baked)
FEATURE [Part::Revolution] Revolve138  label="plugHousing071"
  Angle = 360
  Axis = (0,1,0)
  Base = (0,0,0)
  FaceMakerClass = Part::FaceMakerBullseye
  Placement = pos=(0,0,36.15) rot=(0,0,1;0rad)
  Solid = false
  Source = -> Face129
  Symmetric = false
FEATURE [Part::Feature] Face130
  shape: bbox 10 x 16.5 x 2e-07 mm, 1 faces, 0 solids (baked)
FEATURE [Part::Revolution] Revolve139  label="plugHousing072"
  Angle = 360
  Axis = (0,1,0)
  Base = (0,0,0)
  FaceMakerClass = Part::FaceMakerBullseye
  Placement = pos=(0,0,36.15) rot=(0,0,1;0rad)
  Solid = false
  Source = -> Face130
  Symmetric = false
FEATURE [Part::Feature] Face131
  shape: bbox 10 x 16.5 x 2e-07 mm, 1 faces, 0 solids (baked)
FEATURE [Part::Revolution] Revolve135  label="plugHousing068"
  Angle = 360
  Axis = (0,1,0)
  Base = (0,0,0)
  FaceMakerClass = Part::FaceMakerBullseye
  Placement = pos=(0,0,36.15) rot=(0,0,1;0rad)
  Solid = false
  Source = -> Face131
  Symmetric = false
FEATURE [Part::MultiFuse] Fusion112  label="plugHousing078"
  Placement = pos=(0,0,0) rot=(0,0,1;1.5708rad)
  Shapes = -> [Revolve135,Revolve139]
FEATURE [Part::Feature] Face132
  shape: bbox 10 x 16.5 x 2e-07 mm, 1 faces, 0 solids (baked)
FEATURE [Part::Revolution] Revolve141  label="plugHousing074"
  Angle = 360
  Axis = (0,1,0)
  Base = (0,0,0)
  FaceMakerClass = Part::FaceMakerBullseye
  Placement = pos=(0,0,36.15) rot=(0,0,1;0rad)
  Solid = false
  Source = -> Face132
  Symmetric = false
FEATURE [Part::MultiFuse] Fusion110  label="plugHousing076"
  Placement = pos=(0,0,0) rot=(0,0,1;1.5708rad)
  Shapes = -> [Revolve141,Revolve140]
FEATURE [Part::Feature] Face133
  shape: bbox 10 x 16.5 x 2e-07 mm, 1 faces, 0 solids (baked)
FEATURE [Part::Revolution] Revolve136  label="plugHousing069"
  Angle = 360
  Axis = (0,1,0)
  Base = (0,0,0)
  FaceMakerClass = Part::FaceMakerBullseye
  Placement = pos=(0,0,36.15) rot=(0,0,1;0rad)
  Solid = false
  Source = -> Face133
  Symmetric = false
FEATURE [Part::MultiFuse] Fusion106  label="plugHousing064"
  Placement = pos=(0,0,0) rot=(0,0,1;1.5708rad)
  Shapes = -> [Revolve138,Revolve136]
FEATURE [Part::MultiFuse] Fusion108  label="plugHousing066"
  Placement = pos=(0,19,0) rot=(0,0,1;3.14159rad)
  Shapes = -> [Fusion106,Fusion112]
FEATURE [Part::Feature] Face134
  shape: bbox 10 x 16.5 x 2e-07 mm, 1 faces, 0 solids (baked)
FEATURE [Part::Revolution] Revolve142  label="plugHousing075"
  Angle = 360
  Axis = (0,1,0)
  Base = (0,0,0)
  FaceMakerClass = Part::FaceMakerBullseye
  Placement = pos=(0,0,36.15) rot=(0,0,1;0rad)
  Solid = false
  Source = -> Face134
  Symmetric = false
FEATURE [Part::MultiFuse] Fusion107  label="plugHousing065"
  Placement = pos=(0,0,0) rot=(0,0,1;1.5708rad)
  Shapes = -> [Revolve137,Revolve142]
FEATURE [Part::MultiFuse] Fusion111  label="plugHousing077"
  Placement = pos=(0,19,0) rot=(0,0,1;3.14159rad)
  Shapes = -> [Fusion110,Fusion107]
FEATURE [Part::MultiFuse] Fusion109  label="plugHousing067"
  Placement = pos=(131.236,0,-0.15) rot=(0,0,1;0rad)
  Shapes = -> [Fusion108,Fusion111]
FEATURE [Part::MultiFuse] Fusion113  label="plugHousing079"
  Shapes = -> [Fillet043,Fusion109]
FEATURE [Part::Feature] Face135
  shape: bbox 3.5 x 17.8 x 2e-07 mm, 1 faces, 0 solids (baked)
FEATURE [Part::Revolution] Revolve143  label="removeToCreateScrewAndThreadedInsertHole049"
  Angle = 360
  Axis = (0,1,0)
  Base = (0,0,0)
  FaceMakerClass = Part::FaceMakerBullseye
  Placement = pos=(12.5,0,10) rot=(0,0,1;0rad)
  Solid = false
  Source = -> Face135
  Symmetric = false
FEATURE [Part::Feature] Face136
  shape: bbox 3.5 x 17.8 x 2e-07 mm, 1 faces, 0 solids (baked)
FEATURE [Part::Revolution] Revolve144  label="removeToCreateScrewAndThreadedInsertHole050"
  Angle = 360
  Axis = (0,1,0)
  Base = (0,0,0)
  FaceMakerClass = Part::FaceMakerBullseye
  Placement = pos=(12.5,0,62) rot=(0,0,1;0rad)
  Solid = false
  Source = -> Face136
  Symmetric = false
FEATURE [Part::Feature] Face137
  shape: bbox 3.5 x 17.8 x 2e-07 mm, 1 faces, 0 solids (baked)
FEATURE [Part::Revolution] Revolve145  label="removeToCreateScrewAndThreadedInsertHole051"
  Angle = 360
  Axis = (0,1,0)
  Base = (0,0,0)
  FaceMakerClass = Part::FaceMakerBullseye
  Placement = pos=(89.5,0,68.5) rot=(0,0,1;0rad)
  Solid = false
  Source = -> Face137
  Symmetric = false
FEATURE [Part::Feature] Face138
  shape: bbox 3.5 x 17.8 x 2e-07 mm, 1 faces, 0 solids (baked)
FEATURE [Part::Revolution] Revolve146  label="removeToCreateScrewAndThreadedInsertHole052"
  Angle = 360
  Axis = (0,1,0)
  Base = (0,0,0)
  FaceMakerClass = Part::FaceMakerBullseye
  Placement = pos=(89.5,0,3.5) rot=(0,0,1;0rad)
  Solid = false
  Source = -> Face138
  Symmetric = false
FEATURE [Part::Feature] Face139
  shape: bbox 3.5 x 17.8 x 2e-07 mm, 1 faces, 0 solids (baked)
FEATURE [Part::Revolution] Revolve147  label="removeToCreateScrewAndThreadedInsertHole053"
  Angle = 360
  Axis = (0,1,0)
  Base = (0,0,0)
  FaceMakerClass = Part::FaceMakerBullseye
  Placement = pos=(109.5,4.7,3.5) rot=(0,0,1;0rad)
  Solid = false
  Source = -> Face139
  Symmetric = false
FEATURE [Part::Feature] Face140
  shape: bbox 3.5 x 17.8 x 2e-07 mm, 1 faces, 0 solids (baked)
FEATURE [Part::Revolution] Revolve148  label="removeToCreateScrewAndThreadedInsertHole054"
  Angle = 360
  Axis = (0,1,0)
  Base = (0,0,0)
  FaceMakerClass = Part::FaceMakerBullseye
  Placement = pos=(109.5,4.7,68.5) rot=(0,0,1;0rad)
  Solid = false
  Source = -> Face140
  Symmetric = false
FEATURE [Part::MultiFuse] Fusion114  label="removeToCreateScrewAndThreadedInsertHole055"
  Shapes = -> [Revolve148,Revolve147,Revolve146,Revolve145,Revolve144,Revolve143]
FEATURE [Part::Cut] Cut047  label="casePillars004"
  Base = -> Cut037
  Tool = -> Fusion114
FEATURE [Part::Feature] Face141
  shape: bbox 3.5 x 17.8 x 2e-07 mm, 1 faces, 0 solids (baked)
FEATURE [Part::Feature] Face142
  shape: bbox 3.5 x 17.8 x 2e-07 mm, 1 faces, 0 solids (baked)
FEATURE [Part::Feature] Face143
  shape: bbox 3.5 x 17.8 x 2e-07 mm, 1 faces, 0 solids (baked)
FEATURE [Part::Revolution] Revolve149  label="removeToCreateScrewAndThreadedInsertHole057"
  Angle = 360
  Axis = (0,1,0)
  Base = (0,0,0)
  FaceMakerClass = Part::FaceMakerBullseye
  Placement = pos=(12.5,0,10) rot=(0,0,1;0rad)
  Solid = false
  Source = -> Face141
  Symmetric = false
FEATURE [Part::Feature] Face144
  shape: bbox 3.5 x 17.8 x 2e-07 mm, 1 faces, 0 solids (baked)
FEATURE [Part::Feature] Face145
  shape: bbox 3.5 x 17.8 x 2e-07 mm, 1 faces, 0 solids (baked)
FEATURE [Part::Feature] Face146
  shape: bbox 3.5 x 17.8 x 2e-07 mm, 1 faces, 0 solids (baked)
FEATURE [Part::Revolution] Revolve150  label="removeToCreateScrewAndThreadedInsertHole058"
  Angle = 360
  Axis = (0,1,0)
  Base = (0,0,0)
  FaceMakerClass = Part::FaceMakerBullseye
  Placement = pos=(12.5,0,62) rot=(0,0,1;0rad)
  Solid = false
  Source = -> Face146
  Symmetric = false
FEATURE [Part::Revolution] Revolve151  label="removeToCreateScrewAndThreadedInsertHole059"
  Angle = 360
  Axis = (0,1,0)
  Base = (0,0,0)
  FaceMakerClass = Part::FaceMakerBullseye
  Placement = pos=(89.5,0,68.5) rot=(0,0,1;0rad)
  Solid = false
  Source = -> Face143
  Symmetric = false
FEATURE [Part::Revolution] Revolve152  label="removeToCreateScrewAndThreadedInsertHole060"
  Angle = 360
  Axis = (0,1,0)
  Base = (0,0,0)
  FaceMakerClass = Part::FaceMakerBullseye
  Placement = pos=(89.5,0,3.5) rot=(0,0,1;0rad)
  Solid = false
  Source = -> Face142
  Symmetric = false
FEATURE [Part::Revolution] Revolve153  label="removeToCreateScrewAndThreadedInsertHole061"
  Angle = 360
  Axis = (0,1,0)
  Base = (0,0,0)
  FaceMakerClass = Part::FaceMakerBullseye
  Placement = pos=(109.5,4.7,3.5) rot=(0,0,1;0rad)
  Solid = false
  Source = -> Face145
  Symmetric = false
FEATURE [Part::Revolution] Revolve154  label="removeToCreateScrewAndThreadedInsertHole062"
  Angle = 360
  Axis = (0,1,0)
  Base = (0,0,0)
  FaceMakerClass = Part::FaceMakerBullseye
  Placement = pos=(109.5,4.7,68.5) rot=(0,0,1;0rad)
  Solid = false
  Source = -> Face144
  Symmetric = false
FEATURE [Part::MultiFuse] Fusion115  label="removeToCreateScrewAndThreadedInsertHole056"
  Shapes = -> [Revolve154,Revolve153,Revolve152,Revolve151,Revolve150,Revolve149]
FEATURE [Part::Feature] Face147
  shape: bbox 9.8 x 26.5 x 2e-07 mm, 1 faces, 0 solids (baked)
FEATURE [Part::Revolution] Revolve155
  Angle = 360
  Axis = (0,1,0)
  Base = (0,0,0)
  FaceMakerClass = Part::FaceMakerBullseye
  Placement = pos=(0,0,0) rot=(0,0,1;1.5708rad)
  Solid = false
  Source = -> Face147
  Symmetric = false
FEATURE [Part::Feature] Face148
  shape: bbox 9.8 x 26.5 x 2e-07 mm, 1 faces, 0 solids (baked)
FEATURE [Part::Revolution] Revolve156
  Angle = 360
  Axis = (0,1,0)
  Base = (0,0,0)
  FaceMakerClass = Part::FaceMakerBullseye
  Placement = pos=(0,0,0) rot=(0,0,1;1.5708rad)
  Solid = false
  Source = -> Face148
  Symmetric = false
FEATURE [Part::MultiFuse] Fusion116
  Placement = pos=(-18,19,36) rot=(0,0,1;0rad)
  Shapes = -> [Revolve156,Revolve155]
FEATURE [Part::Box] Box029  label="Cube016"
  AttacherType = Attacher::AttachEngine3D
  Height = 28
  Length = 3
  Placement = pos=(110.7,19,22) rot=(0,0,1;0rad)
  Width = 15.7
FEATURE [Part::Cylinder] Cylinder046
  Angle = 360
  AttacherType = Attacher::AttachEngine3D
  Height = 10
  Placement = pos=(0,0,36.15) rot=(0,0,1;0rad)
  Radius = 4
FEATURE [Part::Cylinder] Cylinder047
  Angle = 360
  AttacherType = Attacher::AttachEngine3D
  Height = 20
  Placement = pos=(0,0,36.15) rot=(0,0,1;0rad)
  Radius = 10.3
FEATURE [Part::MultiFuse] Fusion117  label="removeToCreteHoleForPlugHousing041"
  Placement = pos=(70,19,36) rot=(0,1,0;1.5708rad)
  Shapes = -> [Cylinder047,Cylinder046]
FEATURE [Part::Cut] Cut049  label="plugHousingTab004"
  Base = -> Box029
  Placement = pos=(-107.4,-14,0) rot=(0,0,1;0rad)
  Tool = -> Fusion117
FEATURE [Part::Box] Box030  label="Cube017"
  AttacherType = Attacher::AttachEngine3D
  Height = 28
  Length = 3
  Placement = pos=(110.7,19,22) rot=(0,0,1;0rad)
  Width = 15.7
FEATURE [Part::Cylinder] Cylinder048
  Angle = 360
  AttacherType = Attacher::AttachEngine3D
  Height = 10
  Placement = pos=(0,0,36.15) rot=(0,0,1;0rad)
  Radius = 4
FEATURE [Part::Cylinder] Cylinder049
  Angle = 360
  AttacherType = Attacher::AttachEngine3D
  Height = 20
  Placement = pos=(0,0,36.15) rot=(0,0,1;0rad)
  Radius = 10.3
FEATURE [Part::MultiFuse] Fusion118  label="removeToCreteHoleForPlugHousing042"
  Placement = pos=(70,19,36) rot=(0,1,0;1.5708rad)
  Shapes = -> [Cylinder049,Cylinder048]
FEATURE [Part::Cut] Cut050  label="plugHousingTab005"
  Base = -> Box030
  Placement = pos=(-107.4,-14,0) rot=(0,0,1;0rad)
  Tool = -> Fusion118
FEATURE [Part::MultiFuse] Fusion119
  Placement = pos=(9.6,23,0) rot=(0,0,1;3.14159rad)
  Shapes = -> [Cut049,Cut050]
FEATURE [Part::Box] Box031  label="Cube018"
  AttacherType = Attacher::AttachEngine3D
  Height = 10
  Length = 3
  Placement = pos=(3.3,4,12) rot=(0,0,1;0rad)
  Width = 10
FEATURE [Part::Fillet] Fillet044
  Base = -> Box031
  Edges = 1 edges r=2: [Edge11]
FEATURE [Part::Box] Box032  label="Cube019"
  AttacherType = Attacher::AttachEngine3D
  Height = 10
  Length = 3
  Placement = pos=(3.3,4,50) rot=(0,0,1;0rad)
  Width = 10
FEATURE [Part::Fillet] Fillet045
  Base = -> Box032
  Edges = 1 edges r=2: [Edge12]
FEATURE [Part::Box] Box033  label="Cube020"
  AttacherType = Attacher::AttachEngine3D
  Height = 28
  Length = 4
  Placement = pos=(5,0,22) rot=(0,0,1;0rad)
  Width = 10
FEATURE [Part::Fillet] Fillet046
  Base = -> Box033
  Edges = 1 edges r=1: [Edge7]
FEATURE [Part::Fillet] Fillet047
  Base = -> Fillet046
  Edges = 1 edges r=2: [Edge5]
FEATURE [Part::Fillet] Fillet048
  Base = -> Fillet047
  Edges = 1 edges r=2: [Edge2]
FEATURE [Part::Cylinder] Cylinder050
  Angle = 360
  AttacherType = Attacher::AttachEngine3D
  Height = 20
  Placement = pos=(0,0,36.15) rot=(0,0,1;0rad)
  Radius = 8.2
FEATURE [Part::Cylinder] Cylinder051
  Angle = 360
  AttacherType = Attacher::AttachEngine3D
  Height = 10
  Placement = pos=(0,0,36.15) rot=(0,0,1;0rad)
  Radius = 4
FEATURE [Part::MultiFuse] Fusion120  label="removeToCreteHoleForPlugHousing043"
  Placement = pos=(-42,19,36) rot=(0,1,0;1.5708rad)
  Shapes = -> [Cylinder050,Cylinder051]
FEATURE [Sketcher::SketchObject] Sketch067  label="topSketch018"
  FullyConstrained = true
  sketch-geometry (4):
    g0: LineSegment StartX=16.8446 StartY=31.512 StartZ=0 EndX=16.3251 EndY=34.4666 EndZ=0
    g1: ArcOfCircle CenterX=19 CenterY=19.2524 CenterZ=0 NormalX=0 NormalY=0 NormalZ=1 AngleXU=0 Radius=15.4476 StartAngle=1.74483 EndAngle=2.72717
    g2: ArcOfCircle CenterX=19 CenterY=19.2524 CenterZ=0 NormalX=0 NormalY=0 NormalZ=1 AngleXU=0 Radius=12.4476 StartAngle=1.74483 EndAngle=2.73189
    g3: LineSegment StartX=4.86004 StartY=25.4725 StartZ=0 EndX=7.58253 EndY=24.2107 EndZ=0
  constraints (7):
    c: Block(g0)
    c: Coincident(g1,g0)
    c: Coincident(g2,g0)
    c: Coincident(g3,g1)
    c: Coincident(g3,g2)
    c: Block(g1)
    c: Block(g2)
FEATURE [Part::Extrusion] Extrude058
  Base = -> Sketch067
  Dir = (0,0,1)
  DirMode = 2
  FaceMakerClass = Part::FaceMakerBullseye
  LengthFwd = 10
  LengthRev = 0
  Placement = pos=(0,0,31) rot=(0,0,1;0rad)
  Solid = true
  Symmetric = false
FEATURE [Part::Cut] Cut051
  Base = -> Extrude058
  Tool = -> Fusion120
FEATURE [Part::Fillet] Fillet049
  Base = -> Cut051
  Edges = 1 edges r=2: [Edge1]
FEATURE [Part::Fillet] Fillet050
  Base = -> Fillet049
  Edges = 1 edges r=2.5: [Edge1]
FEATURE [Part::Fillet] Fillet051
  Base = -> Fillet050
  Edges = 1 edges r=2.5: [Edge2]
FEATURE [Part::MultiFuse] Fusion121  label="wireHolder003"
  Shapes = -> [Fusion116,Fillet051]
FEATURE [Part::MultiFuse] Fusion122
  Shapes = -> [Fillet045,Fusion121]
FEATURE [Part::MultiFuse] Fusion123  label="wireHolder004"
  Shapes = -> [Fusion122,Fillet048]
FEATURE [Part::MultiFuse] Fusion124  label="wireHolder005"
  Shapes = -> [Fillet044,Fusion119,Fusion123]
FEATURE [Sketcher::SketchObject] Sketch068  label="topSketch019"
  FullyConstrained = true
  sketch-geometry (6):
    g0: LineSegment StartX=19 StartY=38 StartZ=0 EndX=117 EndY=38 EndZ=0
    g1: ArcOfCircle CenterX=19 CenterY=19 CenterZ=0 NormalX=0 NormalY=0 NormalZ=1 AngleXU=0 Radius=19 StartAngle=1.5708 EndAngle=3.14159
    g2: LineSegment StartX=117 StartY=38 StartZ=0 EndX=117 EndY=19 EndZ=0
    g3: LineSegment StartX=98 StartY=1.0161e-12 StartZ=0 EndX=5.22862e-06 EndY=1.0161e-12 EndZ=0
    g4: LineSegment StartX=5.22862e-06 StartY=19 StartZ=0 EndX=5.22862e-06 EndY=1.0161e-12 EndZ=0
    g5: ArcOfCircle CenterX=98 CenterY=19 CenterZ=0 NormalX=0 NormalY=0 NormalZ=1 AngleXU=0 Radius=19 StartAngle=4.71239 EndAngle=6.28319
  constraints (16):
    c: Horizontal(g0)
    c: Distance(g0) = 98
    c: Coincident(g1,g0)
    c: Block(g1)
    c: Coincident(g2,g0)
    c: Vertical(g2)
    c: Distance(g2) = 19
    c: Horizontal(g3)
    c: Coincident(g4,g1)
    c: Vertical(g4)
    c: Coincident(g3,g4)
    c: Block(g3)
    c: Coincident(g5,g2)
    c: Coincident(g5,g3)
    c: Block(g0)
    c: Block(g5)
FEATURE [Part::Extrusion] Extrude059  label="sideA002"
  Base = -> Sketch068
  Dir = (0,0,1)
  DirMode = 2
  FaceMakerClass = Part::FaceMakerBullseye
  LengthFwd = 3
  LengthRev = 0
  Placement = pos=(0,0,-2.7) rot=(0,0,1;0rad)
  Solid = true
  Symmetric = false
FEATURE [Sketcher::SketchObject] Sketch069  label="topSketch020"
  FullyConstrained = true
  sketch-geometry (6):
    g0: LineSegment StartX=19 StartY=38 StartZ=0 EndX=117 EndY=38 EndZ=0
    g1: ArcOfCircle CenterX=19 CenterY=19 CenterZ=0 NormalX=0 NormalY=0 NormalZ=1 AngleXU=0 Radius=19 StartAngle=1.5708 EndAngle=3.14159
    g2: LineSegment StartX=117 StartY=38 StartZ=0 EndX=117 EndY=19 EndZ=0
    g3: LineSegment StartX=98 StartY=1.0161e-12 StartZ=0 EndX=5.22862e-06 EndY=1.0161e-12 EndZ=0
    g4: LineSegment StartX=5.22862e-06 StartY=19 StartZ=0 EndX=5.22862e-06 EndY=1.0161e-12 EndZ=0
    g5: ArcOfCircle CenterX=98 CenterY=19 CenterZ=0 NormalX=0 NormalY=0 NormalZ=1 AngleXU=0 Radius=19 StartAngle=4.71239 EndAngle=6.28319
  constraints (16):
    c: Horizontal(g0)
    c: Distance(g0) = 98
    c: Coincident(g1,g0)
    c: Block(g1)
    c: Coincident(g2,g0)
    c: Vertical(g2)
    c: Distance(g2) = 19
    c: Horizontal(g3)
    c: Coincident(g4,g1)
    c: Vertical(g4)
    c: Coincident(g3,g4)
    c: Block(g3)
    c: Coincident(g5,g2)
    c: Coincident(g5,g3)
    c: Block(g0)
    c: Block(g5)
FEATURE [Part::Extrusion] Extrude060  label="sideB002"
  Base = -> Sketch069
  Dir = (0,0,1)
  DirMode = 2
  FaceMakerClass = Part::FaceMakerBullseye
  LengthFwd = 3
  LengthRev = 0
  Placement = pos=(0,0,71.7) rot=(0,0,1;0rad)
  Solid = true
  Symmetric = false
FEATURE [Part::MultiFuse] Fusion127  label="removeFromBottom001"
  Placement = pos=(2,0,0) rot=(0,0,1;0rad)
  Shapes = -> [Extrude059,Extrude060]
FEATURE [Part::Cylinder] Cylinder052
  Angle = 360
  AttacherType = Attacher::AttachEngine3D
  Height = 20
  Placement = pos=(0,0,36.15) rot=(0,0,1;0rad)
  Radius = 14
FEATURE [Part::Cylinder] Cylinder053
  Angle = 360
  AttacherType = Attacher::AttachEngine3D
  Height = 10
  Placement = pos=(0,0,36.15) rot=(0,0,1;0rad)
  Radius = 4
FEATURE [Part::MultiFuse] Fusion128  label="removeToCreteHoleForPlugHousing044"
  Placement = pos=(70,19,36) rot=(0,1,0;1.5708rad)
  Shapes = -> [Cylinder052,Cylinder053]
FEATURE [Part::Cut] Cut052  label="bottom011"
  Base = -> Extrude043
  Tool = -> Fusion128
FEATURE [Part::Cut] Cut054  label="bottom012"
  Base = -> Cut052
  Tool = -> Fusion115
FEATURE [Sketcher::SketchObject] Sketch070
  FullyConstrained = true
  Placement = pos=(117,19,0) rot=(0.57735,0.57735,0.57735;2.0944rad)
  sketch-geometry (48):
    g0: LineSegment StartX=-49.19 StartY=69.25 StartZ=0 EndX=-49.19 EndY=66.25 EndZ=0
    g1: LineSegment StartX=-49.19 StartY=63.5 StartZ=0 EndX=-49.19 EndY=60.5 EndZ=0
    g2: LineSegment StartX=-49.19 StartY=57.75 StartZ=0 EndX=-49.19 EndY=54.75 EndZ=0
    g3: LineSegment StartX=-49.19 StartY=52 StartZ=0 EndX=-49.19 EndY=49 EndZ=0
    g4: LineSegment StartX=-49.19 StartY=46.25 StartZ=0 EndX=-49.19 EndY=43.25 EndZ=0
    g5: LineSegment StartX=-49.19 StartY=40.5 StartZ=0 EndX=-49.19 EndY=37.5 EndZ=0
    g6: LineSegment StartX=-49.19 StartY=34.5 StartZ=0 EndX=-49.19 EndY=31.5 EndZ=0
    g7: LineSegment StartX=-49.19 StartY=28.75 StartZ=0 EndX=-49.19 EndY=25.75 EndZ=0
    g8: LineSegment StartX=-49.19 StartY=23 StartZ=0 EndX=-49.19 EndY=20 EndZ=0
    g9: LineSegment StartX=-49.19 StartY=17.25 StartZ=0 EndX=-49.19 EndY=14.25 EndZ=0
    g10: LineSegment StartX=-49.19 StartY=11.5 StartZ=0 EndX=-49.19 EndY=8.5 EndZ=0
    g11: LineSegment StartX=-49.19 StartY=5.75 StartZ=0 EndX=-49.19 EndY=2.75 EndZ=0
    g12: ArcOfCircle CenterX=-1.5 CenterY=67.75 CenterZ=0 NormalX=0 NormalY=0 NormalZ=1 AngleXU=0 Radius=1.5 StartAngle=4.71239 EndAngle=7.85398
    g13: ArcOfCircle CenterX=-1.5 CenterY=62 CenterZ=0 NormalX=0 NormalY=0 NormalZ=1 AngleXU=0 Radius=1.5 StartAngle=4.71239 EndAngle=7.85398
    g14: ArcOfCircle CenterX=-1.5 CenterY=56.25 CenterZ=0 NormalX=0 NormalY=0 NormalZ=1 AngleXU=0 Radius=1.5 StartAngle=4.71239 EndAngle=7.85398
    g15: ArcOfCircle CenterX=-11.49 CenterY=50.5 CenterZ=0 NormalX=0 NormalY=0 NormalZ=1 AngleXU=0 Radius=1.5 StartAngle=4.71239 EndAngle=7.85398
    g16: ArcOfCircle CenterX=-16.28 CenterY=44.75 CenterZ=0 NormalX=0 NormalY=0 NormalZ=1 AngleXU=0 Radius=1.5 StartAngle=4.71239 EndAngle=7.85398
    g17: ArcOfCircle CenterX=-18.2337 CenterY=39 CenterZ=0 NormalX=0 NormalY=0 NormalZ=1 AngleXU=0 Radius=1.5 StartAngle=4.71485 EndAngle=7.85398
    g18: ArcOfCircle CenterX=-16.2837 CenterY=27.25 CenterZ=0 NormalX=0 NormalY=0 NormalZ=1 AngleXU=0 Radius=1.5 StartAngle=4.71485 EndAngle=7.85398
    g19: ArcOfCircle CenterX=-18.2337 CenterY=33 CenterZ=0 NormalX=0 NormalY=0 NormalZ=1 AngleXU=0 Radius=1.5 StartAngle=4.71485 EndAngle=7.85398
    g20: ArcOfCircle CenterX=-11.49 CenterY=21.5 CenterZ=0 NormalX=0 NormalY=0 NormalZ=1 AngleXU=0 Radius=1.5 StartAngle=4.71239 EndAngle=7.85398
    g21: ArcOfCircle CenterX=-1.5 CenterY=4.25 CenterZ=0 NormalX=0 NormalY=0 NormalZ=1 AngleXU=0 Radius=1.5 StartAngle=4.71239 EndAngle=7.85398
    g22: ArcOfCircle CenterX=-1.5 CenterY=10 CenterZ=0 NormalX=0 NormalY=0 NormalZ=1 AngleXU=0 Radius=1.5 StartAngle=4.71239 EndAngle=7.85398
    g23: ArcOfCircle CenterX=-1.5 CenterY=15.75 CenterZ=0 NormalX=0 NormalY=0 NormalZ=1 AngleXU=0 Radius=1.5 StartAngle=4.71239 EndAngle=7.85398
    g24: LineSegment StartX=-49.19 StartY=69.25 StartZ=0 EndX=-1.5 EndY=69.25 EndZ=0
    g25: LineSegment StartX=-49.19 StartY=66.25 StartZ=0 EndX=-1.5 EndY=66.25 EndZ=0
    g26: LineSegment StartX=-49.19 StartY=63.5 StartZ=0 EndX=-1.5 EndY=63.5 EndZ=0
    g27: LineSegment StartX=-49.19 StartY=60.5 StartZ=0 EndX=-1.5 EndY=60.5 EndZ=0
    g28: LineSegment StartX=-49.19 StartY=57.75 StartZ=0 EndX=-1.5 EndY=57.75 EndZ=0
    g29: LineSegment StartX=-49.19 StartY=54.75 StartZ=0 EndX=-1.5 EndY=54.75 EndZ=0
    g30: LineSegment StartX=-49.19 StartY=52 StartZ=0 EndX=-11.49 EndY=52 EndZ=0
    g31: LineSegment StartX=-49.19 StartY=49 StartZ=0 EndX=-11.49 EndY=49 EndZ=0
    g32: LineSegment StartX=-49.19 StartY=46.25 StartZ=0 EndX=-16.28 EndY=46.25 EndZ=0
    g33: LineSegment StartX=-49.19 StartY=43.25 StartZ=0 EndX=-16.28 EndY=43.25 EndZ=0
    g34: LineSegment StartX=-49.19 StartY=40.5 StartZ=0 EndX=-18.2337 EndY=40.5 EndZ=0
    g35: LineSegment StartX=-49.19 StartY=37.5 StartZ=0 EndX=-18.23 EndY=37.5 EndZ=0
    g36: LineSegment StartX=-49.19 StartY=34.5 StartZ=0 EndX=-18.2337 EndY=34.5 EndZ=0
    g37: LineSegment StartX=-49.19 StartY=31.5 StartZ=0 EndX=-18.23 EndY=31.5 EndZ=0
    g38: LineSegment StartX=-49.19 StartY=28.75 StartZ=0 EndX=-16.2837 EndY=28.75 EndZ=0
    g39: LineSegment StartX=-49.19 StartY=25.75 StartZ=0 EndX=-16.28 EndY=25.75 EndZ=0
    g40: LineSegment StartX=-49.19 StartY=23 StartZ=0 EndX=-11.49 EndY=23 EndZ=0
    g41: LineSegment StartX=-49.19 StartY=20 StartZ=0 EndX=-11.49 EndY=20 EndZ=0
    g42: LineSegment StartX=-49.19 StartY=17.25 StartZ=0 EndX=-1.5 EndY=17.25 EndZ=0
    g43: LineSegment StartX=-49.19 StartY=14.25 StartZ=0 EndX=-1.5 EndY=14.25 EndZ=0
    g44: LineSegment StartX=-49.19 StartY=11.5 StartZ=0 EndX=-1.5 EndY=11.5 EndZ=0
    g45: LineSegment StartX=-49.19 StartY=8.5 StartZ=0 EndX=-1.5 EndY=8.5 EndZ=0
    g46: LineSegment StartX=-49.19 StartY=5.75 StartZ=0 EndX=-1.5 EndY=5.75 EndZ=0
    g47: LineSegment StartX=-49.19 StartY=2.75 StartZ=0 EndX=-1.5 EndY=2.75 EndZ=0
  constraints (120):
    c: Vertical(g0)
    c: Distance(g0) = 3
    c: Block(g0)
    c: Vertical(g1)
    c: Distance(g1) = 3
    c: Vertical(g2)
    c: Equal(g0,g2) = 3
    c: Block(g2)
    c: Vertical(g3)
    c: Equal(g1,g3) = 3
    c: Vertical(g4)
    c: Equal(g0,g4) = 3
    c: Block(g4)
    c: Vertical(g5)
    c: Equal(g1,g5) = 3
    c: Vertical(g6)
    c: Equal(g0,g6) = 3
    c: Block(g6)
    c: Vertical(g7)
    c: Equal(g1,g7) = 3
    c: Vertical(g8)
    c: Equal(g0,g8) = 3
    c: Block(g8)
    c: Vertical(g9)
    c: Equal(g1,g9) = 3
    c: Vertical(g10)
    c: Equal(g0,g10) = 3
    c: Block(g10)
    c: Vertical(g11)
    c: Equal(g1,g11) = 3
    c: Block(g12)
    c: Block(g13)
    c: Block(g14)
    c: Block(g15)
    c: Block(g16)
    c: Block(g17)
    c: Block(g18)
    c: Block(g19)
    c: Block(g20)
    c: Block(g21)
    c: Block(g22)
    c: Block(g23)
    c: Block(g11)
    c: Block(g9)
    c: Block(g7)
    c: Block(g5)
    c: Block(g3)
    c: Block(g1)
    c: Coincident(g24,g0)
    c: Coincident(g24,g12)
    c: Horizontal(g24)
    c: Coincident(g25,g0)
    c: Coincident(g25,g12)
    c: Horizontal(g25)
    c: Coincident(g26,g1)
    c: Coincident(g26,g13)
    c: Horizontal(g26)
    c: Coincident(g27,g1)
    c: Coincident(g27,g13)
    c: Horizontal(g27)
    c: Coincident(g28,g2)
    c: Coincident(g28,g14)
    c: Horizontal(g28)
    c: Coincident(g29,g2)
    c: Coincident(g29,g14)
    c: Horizontal(g29)
    c: Coincident(g30,g3)
    c: Coincident(g30,g15)
    c: Horizontal(g30)
    c: Coincident(g31,g3)
    c: Coincident(g31,g15)
    c: Horizontal(g31)
    c: Coincident(g32,g4)
    c: Coincident(g32,g16)
    c: Horizontal(g32)
    c: Coincident(g33,g4)
    c: Coincident(g33,g16)
    c: Horizontal(g33)
    c: Coincident(g34,g5)
    c: Coincident(g34,g17)
    c: Horizontal(g34)
    c: Coincident(g35,g5)
    c: Coincident(g35,g17)
    c: Horizontal(g35)
    c: Coincident(g36,g6)
    c: Coincident(g36,g19)
    c: Horizontal(g36)
    c: Coincident(g37,g6)
    c: Coincident(g37,g19)
    c: Horizontal(g37)
    c: Coincident(g38,g7)
    c: Coincident(g38,g18)
    c: Horizontal(g38)
    c: Coincident(g39,g7)
    c: Coincident(g39,g18)
    c: Horizontal(g39)
    c: Coincident(g40,g8)
    c: Coincident(g40,g20)
    c: Horizontal(g40)
    c: Coincident(g41,g8)
    c: Coincident(g41,g20)
    c: Horizontal(g41)
    c: Coincident(g42,g9)
    c: Coincident(g42,g23)
    c: Horizontal(g42)
    c: Coincident(g43,g9)
    c: Coincident(g43,g23)
    c: Horizontal(g43)
    c: Coincident(g44,g10)
    c: Coincident(g44,g22)
    c: Horizontal(g44)
    c: Coincident(g45,g10)
    c: Coincident(g45,g22)
    c: Horizontal(g45)
    c: Coincident(g46,g11)
    c: Coincident(g46,g21)
    c: Horizontal(g46)
    c: Coincident(g47,g11)
    c: Coincident(g47,g21)
    c: Horizontal(g47)
FEATURE [Part::Extrusion] Extrude061
  Base = -> Sketch070
  Dir = (1,0,0)
  DirMode = 2
  FaceMakerClass = Part::FaceMakerBullseye
  LengthFwd = 23
  LengthRev = 0
  Placement = pos=(-19,0,0) rot=(0,0,1;0rad)
  Solid = true
  Symmetric = false
FEATURE [Part::Fillet] Fillet052  label="removeToCreateVentalationHoles002"
  Base = -> Extrude061
  Edges = <same value as first occurrence — deduplicated (x6 in doc)>
  Placement = pos=(7,0.02,0) rot=(0,0,1;0rad)
FEATURE [Part::MultiFuse] Fusion130  label="bottom013"
  Shapes = -> [Cut054,Cut034]
FEATURE [Part::Cut] Cut055
  Base = -> Fusion130
  Tool = -> Fillet052
FEATURE [Part::Cylinder] Cylinder054
  Angle = 360
  AttacherType = Attacher::AttachEngine3D
  Height = 20
  Placement = pos=(0,0,36.15) rot=(0,0,1;0rad)
  Radius = 4
FEATURE [Sketcher::SketchObject] Sketch071  label="bottomSketch002"
  FullyConstrained = true
  sketch-geometry (32):
    g0: LineSegment StartX=3.3 StartY=-6.03275e-07 StartZ=0 EndX=98 EndY=-6.03275e-07 EndZ=0
    g1: ArcOfCircle CenterX=98 CenterY=19 CenterZ=0 NormalX=0 NormalY=0 NormalZ=1 AngleXU=0 Radius=19 StartAngle=4.71239 EndAngle=5.71103
    g2: LineSegment StartX=6.3 StartY=8 StartZ=0 EndX=3.3 EndY=8 EndZ=0
    g3: LineSegment StartX=3.3 StartY=8 StartZ=0 EndX=3.3 EndY=-6.03275e-07 EndZ=0
    g4: ArcOfCircle CenterX=8.3 CenterY=5 CenterZ=0 NormalX=0 NormalY=0 NormalZ=1 AngleXU=0 Radius=2 StartAngle=3.14159 EndAngle=4.71239
    g5: LineSegment StartX=6.3 StartY=8 StartZ=0 EndX=6.3 EndY=5 EndZ=0
    g6: ArcOfCircle CenterX=98 CenterY=19 CenterZ=0 NormalX=0 NormalY=0 NormalZ=1 AngleXU=0 Radius=12.7 StartAngle=4.71239 EndAngle=6.28319
    g7: LineSegment StartX=94.7 StartY=3 StartZ=0 EndX=8.3 EndY=3 EndZ=0
    g8-g12: Circle x5 (B-spline internal-alignment scaffolding for g13; pole/knot coordinates omitted)
    g13: BSplineCurve PolesCount=5 KnotsCount=3 Degree=3 IsPeriodic=0
    g14: GeomPoint X=98 Y=6.3 Z=0
    g15: GeomPoint X=96.3938 Y=4.71946 Z=0
    g16: GeomPoint X=94.7 Y=3 Z=0
    g17-g23: Circle x7 (B-spline internal-alignment scaffolding for g24; pole/knot coordinates omitted)
    g24: BSplineCurve PolesCount=7 KnotsCount=5 Degree=3 IsPeriodic=0
    g25-g29: GeomPoint x5 (B-spline internal-alignment scaffolding for g24; pole/knot coordinates omitted)
    g30: ArcOfCircle CenterX=98 CenterY=19 CenterZ=0 NormalX=0 NormalY=0 NormalZ=1 AngleXU=0 Radius=15.7 StartAngle=5.81226 EndAngle=6.28319
    g31: LineSegment StartX=110.7 StartY=19 StartZ=0 EndX=113.7 EndY=19 EndZ=0
  constraints (41):
    c: Horizontal(g0)
    c: Coincident(g1,g0)
    c: Block(g1)
    c: Horizontal(g2)
    c: Distance(g2) = 3
    c: Coincident(g3,g2)
    c: Vertical(g3)
    c: Coincident(g3,g0)
    c: Block(g4)
    c: Block(g2)
    c: Coincident(g5,g2)
    c: Coincident(g5,g4)
    c: Vertical(g5)
    c: Coincident(g6,g1)
    c: Block(g6)
    c: Coincident(g7,g4)
    c: Horizontal(g7)
    c: Block(g0)
    c: Block(g7)
    c: Block(g3)
    c: Coincident(g13,g6)
    c: Weight(g8) = 1
    c: Equal(g8, g9-g12) x4
    c: Coincident(g13,g7)
    c: InternalAlignment(g8-g12 -> g13) x5
    c: InternalAlignment(g14,g13)
    c: InternalAlignment(g15,g13)
    c: InternalAlignment(g16,g13)
    c: Block(g13)
    c: Weight(g17) = 1
    c: Equal(g17, g18-g23) x6
    c: Coincident(g24,g1)
    c: InternalAlignment(g17-g23 -> g24) x7
    c: InternalAlignment(g25-g29 -> g24) x5
    c: Block(g24)
    c: Coincident(g30,g24)
    c: Coincident(g31,g6)
    c: Coincident(g31,g30)
    c: Horizontal(g31)
    c: Block(g31)
    c: Block(g30)
FEATURE [Part::Extrusion] Extrude062  label="bottom014"
  Base = -> Sketch071
  Dir = (0,0,1)
  DirMode = 2
  FaceMakerClass = Part::FaceMakerBullseye
  LengthFwd = 71.4
  LengthRev = 0
  Placement = pos=(0,0,0.3) rot=(0,0,1;0rad)
  Solid = true
  Symmetric = false
FEATURE [Part::Fillet] Fillet054
  Base = -> Extrude062
  Edges = 1 edges r=2.4: [Edge17]
FEATURE [Part::Fillet] Fillet055  label="bottom015"
  Base = -> Fillet054
  Edges = 1 edges r=2.4: [Edge36]
FEATURE [Part::Cylinder] Cylinder055
  Angle = 360
  AttacherType = Attacher::AttachEngine3D
  Height = 10
  Placement = pos=(0,0,36.15) rot=(0,0,1;0rad)
  Radius = 4
FEATURE [Part::MultiFuse] Fusion131  label="removeToCreateHoleForPlugHousing002"
  Placement = pos=(70,19,36.15) rot=(0,1,0;1.5708rad)
  Shapes = -> [Cylinder054,Cylinder055]
FEATURE [Part::Cut] Cut056  label="Bottom001"
  Base = -> Fillet055
  Placement = pos=(9,0,0) rot=(0,0,1;0rad)
  Tool = -> Fusion131
FEATURE [Part::Cut] Cut057
  Base = -> Cut055
  Tool = -> Cut056
FEATURE [Sketcher::SketchObject] Sketch072  label="topSketch021"
  FullyConstrained = true
  sketch-geometry (4):
    g0: ArcOfCircle CenterX=105 CenterY=19 CenterZ=0 NormalX=0 NormalY=0 NormalZ=1 AngleXU=0 Radius=20.6155 StartAngle=5.54125 EndAngle=6.28319
    g1: ArcOfCircle CenterX=105 CenterY=19 CenterZ=0 NormalX=0 NormalY=0 NormalZ=1 AngleXU=0 Radius=13 StartAngle=5.54125 EndAngle=6.28319
    g2: LineSegment StartX=118 StartY=19 StartZ=0 EndX=125.616 EndY=19 EndZ=0
    g3: LineSegment StartX=114.583 StartY=10.2157 StartZ=0 EndX=120.197 EndY=5.06982 EndZ=0
  constraints (7):
    c: Block(g0)
    c: Block(g1)
    c: Coincident(g2,g1)
    c: Coincident(g2,g0)
    c: Horizontal(g2)
    c: Coincident(g3,g1)
    c: Coincident(g3,g0)
FEATURE [Part::Extrusion] Extrude063  label="bottomPlugHousingBit003"
  Base = -> Sketch072
  Dir = (0,0,1)
  DirMode = 2
  FaceMakerClass = Part::FaceMakerBullseye
  LengthFwd = 72
  LengthRev = 0
  Solid = true
  Symmetric = false
FEATURE [Part::Cylinder] Cylinder056
  Angle = 360
  AttacherType = Attacher::AttachEngine3D
  Height = 20
  Placement = pos=(0,0,36.15) rot=(0,0,1;0rad)
  Radius = 14.3
FEATURE [Part::Cylinder] Cylinder057
  Angle = 360
  AttacherType = Attacher::AttachEngine3D
  Height = 10
  Placement = pos=(0,0,36.15) rot=(0,0,1;0rad)
  Radius = 4
FEATURE [Part::Box] Box034  label="removeToCreteHoleForPlugHousing047"
  AttacherType = Attacher::AttachEngine3D
  Height = 28.6
  Length = 20
  Placement = pos=(106.15,0,21.7) rot=(0,0,1;0rad)
  Width = 19
FEATURE [Part::Cylinder] Cylinder058
  Angle = 360
  AttacherType = Attacher::AttachEngine3D
  Height = 20
  Placement = pos=(0,0,36.15) rot=(0,0,1;0rad)
  Radius = 14.3
FEATURE [Part::Cylinder] Cylinder059
  Angle = 360
  AttacherType = Attacher::AttachEngine3D
  Height = 10
  Placement = pos=(0,0,36.15) rot=(0,0,1;0rad)
  Radius = 4
FEATURE [Part::MultiFuse] Fusion134  label="removeToCreteHoleForPlugHousing046"
  Placement = pos=(70,19,36) rot=(0,1,0;1.5708rad)
  Shapes = -> [Cylinder058,Cylinder059]
FEATURE [Part::Cylinder] Cylinder060
  Angle = 360
  AttacherType = Attacher::AttachEngine3D
  Height = 20
  Placement = pos=(0,0,36.15) rot=(0,0,1;0rad)
  Radius = 14
FEATURE [Part::Cylinder] Cylinder061
  Angle = 360
  AttacherType = Attacher::AttachEngine3D
  Height = 10
  Placement = pos=(0,0,36.15) rot=(0,0,1;0rad)
  Radius = 4
FEATURE [Part::MultiFuse] Fusion135  label="removeToCreteHoleForPlugHousing048"
  Placement = pos=(70,19,36) rot=(0,1,0;1.5708rad)
  Shapes = -> [Cylinder060,Cylinder061]
FEATURE [Part::Box] Box035  label="removeToCreteHoleForPlugHousing049"
  AttacherType = Attacher::AttachEngine3D
  Height = 28.6
  Length = 20
  Placement = pos=(106.15,0,21.7) rot=(0,0,1;0rad)
  Width = 19
FEATURE [Part::MultiFuse] Fusion133  label="removeToCreteHoleForPlugHousing045"
  Placement = pos=(0,0,-28.3) rot=(0,0,1;0rad)
  Shapes = -> [Box035,Fusion134]
FEATURE [Part::MultiFuse] Fusion138  label="removeToCreteHoleForPlugHousing051"
  Placement = pos=(70,19,36) rot=(0,1,0;1.5708rad)
  Shapes = -> [Cylinder056,Cylinder057]
FEATURE [Part::MultiFuse] Fusion137  label="removeToCreteHoleForPlugHousing050"
  Placement = pos=(0,0,28.3) rot=(0,0,1;0rad)
  Shapes = -> [Box034,Fusion138]
FEATURE [Part::MultiFuse] Fusion132  label="removeToCreatePlugHousingBottomBit002"
  Shapes = -> [Fusion133,Fusion137]
FEATURE [Part::MultiFuse] Fusion136  label="removeToCreatePlugHousingBottomBit003"
  Shapes = -> [Fusion135,Fusion132]
FEATURE [Part::Cut] Cut058  label="bottomPlugHousingBit002"
  Base = -> Extrude063
  Placement = pos=(-0.09,0,0) rot=(0,0,1;0rad)
  Tool = -> Fusion136
FEATURE [Sketcher::SketchObject] Sketch073  label="bottomSketch003"
  FullyConstrained = true
  sketch-geometry (45):
    g0: LineSegment StartX=6.29999 StartY=8 StartZ=0 EndX=3.29999 EndY=8 EndZ=0
    g1: LineSegment StartX=3.29999 StartY=8 StartZ=0 EndX=3.29999 EndY=-6.03275e-07 EndZ=0
    g2: ArcOfCircle CenterX=8.29999 CenterY=5 CenterZ=0 NormalX=0 NormalY=0 NormalZ=1 AngleXU=0 Radius=2 StartAngle=3.14159 EndAngle=4.71239
    g3: LineSegment StartX=6.29999 StartY=8 StartZ=0 EndX=6.29999 EndY=5 EndZ=0
    g4: ArcOfCircle CenterX=105 CenterY=19 CenterZ=0 NormalX=0 NormalY=0 NormalZ=1 AngleXU=0 Radius=12.7 StartAngle=4.71239 EndAngle=5.94289
    g5-g11: Circle x7 (B-spline internal-alignment scaffolding for g12; pole/knot coordinates omitted)
    g12: BSplineCurve PolesCount=7 KnotsCount=5 Degree=3 IsPeriodic=0
    g13-g17: GeomPoint x5 (B-spline internal-alignment scaffolding for g12; pole/knot coordinates omitted)
    g18: ArcOfCircle CenterX=105 CenterY=19 CenterZ=0 NormalX=0 NormalY=0 NormalZ=1 AngleXU=0 Radius=15.7 StartAngle=5.81226 EndAngle=6.28319
    g19: BSplineCurve PolesCount=5 KnotsCount=3 Degree=3 IsPeriodic=0
    g20: LineSegment StartX=8.29999 StartY=3 StartZ=0 EndX=101.7 EndY=3 EndZ=0
    g21: LineSegment StartX=3.29999 StartY=-6.03275e-07 StartZ=0 EndX=105 EndY=-6.03275e-07 EndZ=0
    g22: LineSegment StartX=120.974 StartY=8.71251 StartZ=0 EndX=122.332 EndY=7.83778 EndZ=0
    g23: LineSegment StartX=105 StartY=-6.03274e-07 StartZ=0 EndX=113 EndY=-6.03274e-07 EndZ=0
    g24: ArcOfCircle CenterX=105 CenterY=19 CenterZ=0 NormalX=0 NormalY=0 NormalZ=1 AngleXU=0 Radius=20.6155 StartAngle=5.11091 EndAngle=5.71103
    g25: ArcOfCircle CenterX=117.7 CenterY=19 CenterZ=0 NormalX=0 NormalY=0 NormalZ=1 AngleXU=0 Radius=3 StartAngle=1.2e-15 EndAngle=2.10468
    g26: Circle CenterX=116.345 CenterY=16.3232 CenterZ=0 NormalX=0 NormalY=0 NormalZ=1 AngleXU=0 Radius=1
    g27: Circle CenterX=117.24 CenterY=15.7584 CenterZ=0 NormalX=0 NormalY=0 NormalZ=1 AngleXU=0 Radius=1
    g28: Circle CenterX=116.972 CenterY=14.7612 CenterZ=0 NormalX=0 NormalY=0 NormalZ=1 AngleXU=0 Radius=1
    g29: BSplineCurve PolesCount=3 KnotsCount=2 Degree=2 IsPeriodic=0
    g30: GeomPoint X=116.345 Y=16.3232 Z=0
    g31: GeomPoint X=116.972 Y=14.7612 Z=0
    g32: Circle CenterX=115.828 CenterY=17.157 CenterZ=0 NormalX=0 NormalY=0 NormalZ=1 AngleXU=0 Radius=1
    g33: Circle CenterX=115.841 CenterY=16.639 CenterZ=0 NormalX=0 NormalY=0 NormalZ=1 AngleXU=0 Radius=1
    g34: Circle CenterX=116.345 CenterY=16.3232 CenterZ=0 NormalX=0 NormalY=0 NormalZ=1 AngleXU=0 Radius=1
    g35: BSplineCurve PolesCount=3 KnotsCount=2 Degree=2 IsPeriodic=0
    g36: GeomPoint X=115.828 Y=17.157 Z=0
    g37: GeomPoint X=116.345 Y=16.3232 Z=0
    g38: LineSegment StartX=115.828 StartY=17.157 StartZ=0 EndX=115.828 EndY=20.8307 EndZ=0
    g39: Circle CenterX=115.828 CenterY=20.8307 CenterZ=0 NormalX=0 NormalY=0 NormalZ=1 AngleXU=0 Radius=1
    g40: Circle CenterX=115.831 CenterY=21.3396 CenterZ=0 NormalX=0 NormalY=0 NormalZ=1 AngleXU=0 Radius=1
    g41: Circle CenterX=116.173 CenterY=21.5825 CenterZ=0 NormalX=0 NormalY=0 NormalZ=1 AngleXU=0 Radius=1
    g42: BSplineCurve PolesCount=3 KnotsCount=2 Degree=2 IsPeriodic=0
    g43: GeomPoint X=115.828 Y=20.8307 Z=0
    g44: GeomPoint X=116.173 Y=21.5825 Z=0
  constraints (70):
    c: Horizontal(g0)
    c: Distance(g0) = 3
    c: Coincident(g1,g0)
    c: Vertical(g1)
    c: Block(g2)
    c: Block(g0)
    c: Coincident(g3,g0)
    c: Coincident(g3,g2)
    c: Vertical(g3)
    c: Block(g1)
    c: Block(g4)
    c: Coincident(g19,g4)
    c: Block(g19)
    c: Equal(g5, g6-g11) x6
    c: InternalAlignment(g5-g11 -> g12) x7
    c: InternalAlignment(g13-g17 -> g12) x5
    c: Block(g12)
    c: Coincident(g18,g12)
    c: Block(g18)
    c: Coincident(g20,g2)
    c: Coincident(g20,g19)
    c: Horizontal(g20)
    c: Distance(g20) = 93.4
    c: Coincident(g21,g1)
    c: Horizontal(g21)
    c: Distance(g21) = 101.7
    c: Horizontal(g23)
    c: Distance(g23) = 8
    c: Coincident(g24,g23)
    c: Block(g23)
    c: Coincident(g22,g24)
    c: Block(g24)
    c: Block(g22)
    c: Distance(g22) = 1.61553
    c: Coincident(g25,g18)
    c: Block(g25)
    c: Weight(g26) = 1
    c: Equal(g26,g27)
    c: Equal(g26,g28)
    c: Coincident(g29,g4)
    c: InternalAlignment(g26,g29)
    c: InternalAlignment(g27,g29)
    c: InternalAlignment(g28,g29)
    c: InternalAlignment(g30,g29)
    c: InternalAlignment(g31,g29)
    c: Block(g29)
    c: Weight(g32) = 1
    c: Equal(g32,g33)
    c: Equal(g32,g34)
    c: Coincident(g35,g29)
    c: InternalAlignment(g32,g35)
    c: InternalAlignment(g33,g35)
    c: InternalAlignment(g34,g35)
    c: InternalAlignment(g36,g35)
    c: InternalAlignment(g37,g35)
    c: Block(g35)
    c: Coincident(g38,g35)
    c: Vertical(g38)
    c: Block(g38)
    c: Coincident(g42,g38)
    c: Weight(g39) = 1
    c: Equal(g39,g40)
    c: Equal(g39,g41)
    c: Coincident(g42,g25)
    c: InternalAlignment(g39,g42)
    c: InternalAlignment(g40,g42)
    c: InternalAlignment(g41,g42)
    c: InternalAlignment(g43,g42)
    c: InternalAlignment(g44,g42)
    c: Block(g42)
FEATURE [Part::Extrusion] Extrude064  label="bottom016"
  Base = -> Sketch073
  Dir = (0,0,1)
  DirMode = 2
  FaceMakerClass = Part::FaceMakerBullseye
  LengthFwd = 71.4
  LengthRev = 0
  Placement = pos=(0,0,0.3) rot=(0,0,1;0rad)
  Solid = true
  Symmetric = false
FEATURE [Part::Revolution] Revolve157  label="removeToCreateScrewAndThreadedInsertHole063"
  Angle = 360
  Axis = (0,1,0)
  Base = (0,0,0)
  FaceMakerClass = Part::FaceMakerBullseye
  Placement = pos=(12.5,0,10) rot=(0,0,1;0rad)
  Solid = false
  Source = -> Face141
  Symmetric = false
FEATURE [Sketcher::SketchObject] Sketch074
  FullyConstrained = true
  Placement = pos=(117,19,0) rot=(0.57735,0.57735,0.57735;2.0944rad)
  sketch-geometry (48):
    g0: LineSegment StartX=-49.19 StartY=69.25 StartZ=0 EndX=-49.19 EndY=66.25 EndZ=0
    g1: LineSegment StartX=-49.19 StartY=63.5 StartZ=0 EndX=-49.19 EndY=60.5 EndZ=0
    g2: LineSegment StartX=-49.19 StartY=57.75 StartZ=0 EndX=-49.19 EndY=54.75 EndZ=0
    g3: LineSegment StartX=-49.19 StartY=52 StartZ=0 EndX=-49.19 EndY=49 EndZ=0
    g4: LineSegment StartX=-49.19 StartY=46.25 StartZ=0 EndX=-49.19 EndY=43.25 EndZ=0
    g5: LineSegment StartX=-49.19 StartY=40.5 StartZ=0 EndX=-49.19 EndY=37.5 EndZ=0
    g6: LineSegment StartX=-49.19 StartY=34.5 StartZ=0 EndX=-49.19 EndY=31.5 EndZ=0
    g7: LineSegment StartX=-49.19 StartY=28.75 StartZ=0 EndX=-49.19 EndY=25.75 EndZ=0
    g8: LineSegment StartX=-49.19 StartY=23 StartZ=0 EndX=-49.19 EndY=20 EndZ=0
    g9: LineSegment StartX=-49.19 StartY=17.25 StartZ=0 EndX=-49.19 EndY=14.25 EndZ=0
    g10: LineSegment StartX=-49.19 StartY=11.5 StartZ=0 EndX=-49.19 EndY=8.5 EndZ=0
    g11: LineSegment StartX=-49.19 StartY=5.75 StartZ=0 EndX=-49.19 EndY=2.75 EndZ=0
    g12: ArcOfCircle CenterX=-1.5 CenterY=67.75 CenterZ=0 NormalX=0 NormalY=0 NormalZ=1 AngleXU=0 Radius=1.5 StartAngle=4.71239 EndAngle=7.85398
    g13: ArcOfCircle CenterX=-1.5 CenterY=62 CenterZ=0 NormalX=0 NormalY=0 NormalZ=1 AngleXU=0 Radius=1.5 StartAngle=4.71239 EndAngle=7.85398
    g14: ArcOfCircle CenterX=-1.5 CenterY=56.25 CenterZ=0 NormalX=0 NormalY=0 NormalZ=1 AngleXU=0 Radius=1.5 StartAngle=4.71239 EndAngle=7.85398
    g15: ArcOfCircle CenterX=-11.49 CenterY=50.5 CenterZ=0 NormalX=0 NormalY=0 NormalZ=1 AngleXU=0 Radius=1.5 StartAngle=4.71239 EndAngle=7.85398
    g16: ArcOfCircle CenterX=-16.28 CenterY=44.75 CenterZ=0 NormalX=0 NormalY=0 NormalZ=1 AngleXU=0 Radius=1.5 StartAngle=4.71239 EndAngle=7.85398
    g17: ArcOfCircle CenterX=-18.2337 CenterY=39 CenterZ=0 NormalX=0 NormalY=0 NormalZ=1 AngleXU=0 Radius=1.5 StartAngle=4.71485 EndAngle=7.85398
    g18: ArcOfCircle CenterX=-16.2837 CenterY=27.25 CenterZ=0 NormalX=0 NormalY=0 NormalZ=1 AngleXU=0 Radius=1.5 StartAngle=4.71485 EndAngle=7.85398
    g19: ArcOfCircle CenterX=-18.2337 CenterY=33 CenterZ=0 NormalX=0 NormalY=0 NormalZ=1 AngleXU=0 Radius=1.5 StartAngle=4.71485 EndAngle=7.85398
    g20: ArcOfCircle CenterX=-11.49 CenterY=21.5 CenterZ=0 NormalX=0 NormalY=0 NormalZ=1 AngleXU=0 Radius=1.5 StartAngle=4.71239 EndAngle=7.85398
    g21: ArcOfCircle CenterX=-1.5 CenterY=4.25 CenterZ=0 NormalX=0 NormalY=0 NormalZ=1 AngleXU=0 Radius=1.5 StartAngle=4.71239 EndAngle=7.85398
    g22: ArcOfCircle CenterX=-1.5 CenterY=10 CenterZ=0 NormalX=0 NormalY=0 NormalZ=1 AngleXU=0 Radius=1.5 StartAngle=4.71239 EndAngle=7.85398
    g23: ArcOfCircle CenterX=-1.5 CenterY=15.75 CenterZ=0 NormalX=0 NormalY=0 NormalZ=1 AngleXU=0 Radius=1.5 StartAngle=4.71239 EndAngle=7.85398
    g24: LineSegment StartX=-49.19 StartY=69.25 StartZ=0 EndX=-1.5 EndY=69.25 EndZ=0
    g25: LineSegment StartX=-49.19 StartY=66.25 StartZ=0 EndX=-1.5 EndY=66.25 EndZ=0
    g26: LineSegment StartX=-49.19 StartY=63.5 StartZ=0 EndX=-1.5 EndY=63.5 EndZ=0
    g27: LineSegment StartX=-49.19 StartY=60.5 StartZ=0 EndX=-1.5 EndY=60.5 EndZ=0
    g28: LineSegment StartX=-49.19 StartY=57.75 StartZ=0 EndX=-1.5 EndY=57.75 EndZ=0
    g29: LineSegment StartX=-49.19 StartY=54.75 StartZ=0 EndX=-1.5 EndY=54.75 EndZ=0
    g30: LineSegment StartX=-49.19 StartY=52 StartZ=0 EndX=-11.49 EndY=52 EndZ=0
    g31: LineSegment StartX=-49.19 StartY=49 StartZ=0 EndX=-11.49 EndY=49 EndZ=0
    g32: LineSegment StartX=-49.19 StartY=46.25 StartZ=0 EndX=-16.28 EndY=46.25 EndZ=0
    g33: LineSegment StartX=-49.19 StartY=43.25 StartZ=0 EndX=-16.28 EndY=43.25 EndZ=0
    g34: LineSegment StartX=-49.19 StartY=40.5 StartZ=0 EndX=-18.2337 EndY=40.5 EndZ=0
    g35: LineSegment StartX=-49.19 StartY=37.5 StartZ=0 EndX=-18.23 EndY=37.5 EndZ=0
    g36: LineSegment StartX=-49.19 StartY=34.5 StartZ=0 EndX=-18.2337 EndY=34.5 EndZ=0
    g37: LineSegment StartX=-49.19 StartY=31.5 StartZ=0 EndX=-18.23 EndY=31.5 EndZ=0
    g38: LineSegment StartX=-49.19 StartY=28.75 StartZ=0 EndX=-16.2837 EndY=28.75 EndZ=0
    g39: LineSegment StartX=-49.19 StartY=25.75 StartZ=0 EndX=-16.28 EndY=25.75 EndZ=0
    g40: LineSegment StartX=-49.19 StartY=23 StartZ=0 EndX=-11.49 EndY=23 EndZ=0
    g41: LineSegment StartX=-49.19 StartY=20 StartZ=0 EndX=-11.49 EndY=20 EndZ=0
    g42: LineSegment StartX=-49.19 StartY=17.25 StartZ=0 EndX=-1.5 EndY=17.25 EndZ=0
    g43: LineSegment StartX=-49.19 StartY=14.25 StartZ=0 EndX=-1.5 EndY=14.25 EndZ=0
    g44: LineSegment StartX=-49.19 StartY=11.5 StartZ=0 EndX=-1.5 EndY=11.5 EndZ=0
    g45: LineSegment StartX=-49.19 StartY=8.5 StartZ=0 EndX=-1.5 EndY=8.5 EndZ=0
    g46: LineSegment StartX=-49.19 StartY=5.75 StartZ=0 EndX=-1.5 EndY=5.75 EndZ=0
    g47: LineSegment StartX=-49.19 StartY=2.75 StartZ=0 EndX=-1.5 EndY=2.75 EndZ=0
  constraints (120):
    c: Vertical(g0)
    c: Distance(g0) = 3
    c: Block(g0)
    c: Vertical(g1)
    c: Distance(g1) = 3
    c: Vertical(g2)
    c: Equal(g0,g2) = 3
    c: Block(g2)
    c: Vertical(g3)
    c: Equal(g1,g3) = 3
    c: Vertical(g4)
    c: Equal(g0,g4) = 3
    c: Block(g4)
    c: Vertical(g5)
    c: Equal(g1,g5) = 3
    c: Vertical(g6)
    c: Equal(g0,g6) = 3
    c: Block(g6)
    c: Vertical(g7)
    c: Equal(g1,g7) = 3
    c: Vertical(g8)
    c: Equal(g0,g8) = 3
    c: Block(g8)
    c: Vertical(g9)
    c: Equal(g1,g9) = 3
    c: Vertical(g10)
    c: Equal(g0,g10) = 3
    c: Block(g10)
    c: Vertical(g11)
    c: Equal(g1,g11) = 3
    c: Block(g12)
    c: Block(g13)
    c: Block(g14)
    c: Block(g15)
    c: Block(g16)
    c: Block(g17)
    c: Block(g18)
    c: Block(g19)
    c: Block(g20)
    c: Block(g21)
    c: Block(g22)
    c: Block(g23)
    c: Block(g11)
    c: Block(g9)
    c: Block(g7)
    c: Block(g5)
    c: Block(g3)
    c: Block(g1)
    c: Coincident(g24,g0)
    c: Coincident(g24,g12)
    c: Horizontal(g24)
    c: Coincident(g25,g0)
    c: Coincident(g25,g12)
    c: Horizontal(g25)
    c: Coincident(g26,g1)
    c: Coincident(g26,g13)
    c: Horizontal(g26)
    c: Coincident(g27,g1)
    c: Coincident(g27,g13)
    c: Horizontal(g27)
    c: Coincident(g28,g2)
    c: Coincident(g28,g14)
    c: Horizontal(g28)
    c: Coincident(g29,g2)
    c: Coincident(g29,g14)
    c: Horizontal(g29)
    c: Coincident(g30,g3)
    c: Coincident(g30,g15)
    c: Horizontal(g30)
    c: Coincident(g31,g3)
    c: Coincident(g31,g15)
    c: Horizontal(g31)
    c: Coincident(g32,g4)
    c: Coincident(g32,g16)
    c: Horizontal(g32)
    c: Coincident(g33,g4)
    c: Coincident(g33,g16)
    c: Horizontal(g33)
    c: Coincident(g34,g5)
    c: Coincident(g34,g17)
    c: Horizontal(g34)
    c: Coincident(g35,g5)
    c: Coincident(g35,g17)
    c: Horizontal(g35)
    c: Coincident(g36,g6)
    c: Coincident(g36,g19)
    c: Horizontal(g36)
    c: Coincident(g37,g6)
    c: Coincident(g37,g19)
    c: Horizontal(g37)
    c: Coincident(g38,g7)
    c: Coincident(g38,g18)
    c: Horizontal(g38)
    c: Coincident(g39,g7)
    c: Coincident(g39,g18)
    c: Horizontal(g39)
    c: Coincident(g40,g8)
    c: Coincident(g40,g20)
    c: Horizontal(g40)
    c: Coincident(g41,g8)
    c: Coincident(g41,g20)
    c: Horizontal(g41)
    c: Coincident(g42,g9)
    c: Coincident(g42,g23)
    c: Horizontal(g42)
    c: Coincident(g43,g9)
    c: Coincident(g43,g23)
    c: Horizontal(g43)
    c: Coincident(g44,g10)
    c: Coincident(g44,g22)
    c: Horizontal(g44)
    c: Coincident(g45,g10)
    c: Coincident(g45,g22)
    c: Horizontal(g45)
    c: Coincident(g46,g11)
    c: Coincident(g46,g21)
    c: Horizontal(g46)
    c: Coincident(g47,g11)
    c: Coincident(g47,g21)
    c: Horizontal(g47)
FEATURE [Part::Extrusion] Extrude065
  Base = -> Sketch074
  Dir = (1,0,0)
  DirMode = 2
  FaceMakerClass = Part::FaceMakerBullseye
  LengthFwd = 23
  LengthRev = 0
  Placement = pos=(-19,0,0) rot=(0,0,1;0rad)
  Solid = true
  Symmetric = false
FEATURE [Part::Fillet] Fillet056  label="removeToCreateVentalationHoles003"
  Base = -> Extrude065
  Edges = <same value as first occurrence — deduplicated (x6 in doc)>
  Placement = pos=(7,0.02,0) rot=(0,0,1;0rad)
FEATURE [Part::Revolution] Revolve158  label="removeToCreateScrewAndThreadedInsertHole065"
  Angle = 360
  Axis = (0,1,0)
  Base = (0,0,0)
  FaceMakerClass = Part::FaceMakerBullseye
  Placement = pos=(12.5,0,62) rot=(0,0,1;0rad)
  Solid = false
  Source = -> Face146
  Symmetric = false
FEATURE [Part::Revolution] Revolve159  label="removeToCreateScrewAndThreadedInsertHole066"
  Angle = 360
  Axis = (0,1,0)
  Base = (0,0,0)
  FaceMakerClass = Part::FaceMakerBullseye
  Placement = pos=(89.5,0,68.5) rot=(0,0,1;0rad)
  Solid = false
  Source = -> Face143
  Symmetric = false
FEATURE [Part::Revolution] Revolve160  label="removeToCreateScrewAndThreadedInsertHole067"
  Angle = 360
  Axis = (0,1,0)
  Base = (0,0,0)
  FaceMakerClass = Part::FaceMakerBullseye
  Placement = pos=(89.5,0,3.5) rot=(0,0,1;0rad)
  Solid = false
  Source = -> Face142
  Symmetric = false
FEATURE [Part::Revolution] Revolve161  label="removeToCreateScrewAndThreadedInsertHole068"
  Angle = 360
  Axis = (0,1,0)
  Base = (0,0,0)
  FaceMakerClass = Part::FaceMakerBullseye
  Placement = pos=(109.5,4.7,3.5) rot=(0,0,1;0rad)
  Solid = false
  Source = -> Face145
  Symmetric = false
FEATURE [Part::Revolution] Revolve162  label="removeToCreateScrewAndThreadedInsertHole069"
  Angle = 360
  Axis = (0,1,0)
  Base = (0,0,0)
  FaceMakerClass = Part::FaceMakerBullseye
  Placement = pos=(109.5,4.7,68.5) rot=(0,0,1;0rad)
  Solid = false
  Source = -> Face144
  Symmetric = false
FEATURE [Part::MultiFuse] Fusion141  label="removeToCreateScrewAndThreadedInsertHole064"
  Shapes = -> [Revolve162,Revolve161,Revolve160,Revolve159,Revolve158,Revolve157]
FEATURE [Part::Cylinder] Cylinder062
  Angle = 360
  AttacherType = Attacher::AttachEngine3D
  Height = 20
  Placement = pos=(0,0,36.15) rot=(0,0,1;0rad)
  Radius = 14
FEATURE [Part::Cylinder] Cylinder063
  Angle = 360
  AttacherType = Attacher::AttachEngine3D
  Height = 10
  Placement = pos=(0,0,36.15) rot=(0,0,1;0rad)
  Radius = 4
FEATURE [Part::MultiFuse] Fusion139  label="removeToCreteHoleForPlugHousing052"
  Placement = pos=(70,19,36) rot=(0,1,0;1.5708rad)
  Shapes = -> [Cylinder062,Cylinder063]
FEATURE [Part::Cut] Cut060  label="bottom017"
  Base = -> Extrude064
  Tool = -> Fusion139
FEATURE [Part::Cut] Cut061  label="bottom019"
  Base = -> Cut060
  Tool = -> Fusion141
FEATURE [Part::MultiFuse] Fusion140  label="bottom018"
  Shapes = -> [Cut061,Cut058]
FEATURE [Part::Cut] Cut059  label="bottom020"
  Base = -> Fusion140
  Tool = -> Fillet056
FEATURE [Part::Box] Box036  label="Cube021"
  AttacherType = Attacher::AttachEngine3D
  Height = 80
  Length = 26
  Placement = pos=(0,-1,-5) rot=(0,0,1;0rad)
  Width = 11
FEATURE [Part::Cut] Cut062  label="removeFromBottom002"
  Base = -> Cut057
  Tool = -> Box036
FEATURE [Part::Cut] Cut063
  Base = -> Cut059
  Tool = -> Cut062
FEATURE [Part::Cut] Cut064  label="pcbStands"
  Base = -> Fusion095
  Tool = -> Fusion127
FEATURE [Sketcher::SketchObject] Sketch075  label="topSketch022"
  FullyConstrained = true
  sketch-geometry (6):
    g0: LineSegment StartX=19 StartY=38 StartZ=0 EndX=117 EndY=38 EndZ=0
    g1: ArcOfCircle CenterX=19 CenterY=19 CenterZ=0 NormalX=0 NormalY=0 NormalZ=1 AngleXU=0 Radius=19 StartAngle=1.5708 EndAngle=3.14159
    g2: LineSegment StartX=117 StartY=38 StartZ=0 EndX=117 EndY=19 EndZ=0
    g3: LineSegment StartX=98 StartY=1.0161e-12 StartZ=0 EndX=5.22862e-06 EndY=1.0161e-12 EndZ=0
    g4: LineSegment StartX=5.22862e-06 StartY=19 StartZ=0 EndX=5.22862e-06 EndY=1.0161e-12 EndZ=0
    g5: ArcOfCircle CenterX=98 CenterY=19 CenterZ=0 NormalX=0 NormalY=0 NormalZ=1 AngleXU=0 Radius=19 StartAngle=4.71239 EndAngle=6.28319
  constraints (16):
    c: Horizontal(g0)
    c: Distance(g0) = 98
    c: Coincident(g1,g0)
    c: Block(g1)
    c: Coincident(g2,g0)
    c: Vertical(g2)
    c: Distance(g2) = 19
    c: Horizontal(g3)
    c: Coincident(g4,g1)
    c: Vertical(g4)
    c: Coincident(g3,g4)
    c: Block(g3)
    c: Coincident(g5,g2)
    c: Coincident(g5,g3)
    c: Block(g0)
    c: Block(g5)
FEATURE [Part::Extrusion] Extrude067  label="sideB003"
  Base = -> Sketch075
  Dir = (0,0,1)
  DirMode = 2
  FaceMakerClass = Part::FaceMakerBullseye
  LengthFwd = 3
  LengthRev = 0
  Placement = pos=(0,0,71.7) rot=(0,0,1;0rad)
  Solid = true
  Symmetric = false
FEATURE [Sketcher::SketchObject] Sketch076  label="topSketch023"
  FullyConstrained = true
  sketch-geometry (6):
    g0: LineSegment StartX=19 StartY=38 StartZ=0 EndX=117 EndY=38 EndZ=0
    g1: ArcOfCircle CenterX=19 CenterY=19 CenterZ=0 NormalX=0 NormalY=0 NormalZ=1 AngleXU=0 Radius=19 StartAngle=1.5708 EndAngle=3.14159
    g2: LineSegment StartX=117 StartY=38 StartZ=0 EndX=117 EndY=19 EndZ=0
    g3: LineSegment StartX=98 StartY=1.0161e-12 StartZ=0 EndX=5.22862e-06 EndY=1.0161e-12 EndZ=0
    g4: LineSegment StartX=5.22862e-06 StartY=19 StartZ=0 EndX=5.22862e-06 EndY=1.0161e-12 EndZ=0
    g5: ArcOfCircle CenterX=98 CenterY=19 CenterZ=0 NormalX=0 NormalY=0 NormalZ=1 AngleXU=0 Radius=19 StartAngle=4.71239 EndAngle=6.28319
  constraints (16):
    c: Horizontal(g0)
    c: Distance(g0) = 98
    c: Coincident(g1,g0)
    c: Block(g1)
    c: Coincident(g2,g0)
    c: Vertical(g2)
    c: Distance(g2) = 19
    c: Horizontal(g3)
    c: Coincident(g4,g1)
    c: Vertical(g4)
    c: Coincident(g3,g4)
    c: Block(g3)
    c: Coincident(g5,g2)
    c: Coincident(g5,g3)
    c: Block(g0)
    c: Block(g5)
FEATURE [Part::Extrusion] Extrude066  label="sideA003"
  Base = -> Sketch076
  Dir = (0,0,1)
  DirMode = 2
  FaceMakerClass = Part::FaceMakerBullseye
  LengthFwd = 3
  LengthRev = 0
  Placement = pos=(0,0,-2.7) rot=(0,0,1;0rad)
  Solid = true
  Symmetric = false
FEATURE [Part::MultiFuse] Fusion142  label="removeFromBottom003"
  Placement = pos=(2,0,0) rot=(0,0,1;0rad)
  Shapes = -> [Extrude066,Extrude067]
FEATURE [Part::Cut] Cut065  label="screwRetainers002"
  Base = -> Fusion096
  Tool = -> Fusion142
FEATURE [Sketcher::SketchObject] Sketch077
  FullyConstrained = true
  Placement = pos=(117,19,0) rot=(0.57735,0.57735,0.57735;2.0944rad)
  sketch-geometry (8):
    g0: LineSegment StartX=-49.19 StartY=63.5 StartZ=0 EndX=-49.19 EndY=60.5 EndZ=0
    g1: LineSegment StartX=-49.19 StartY=11.5 StartZ=0 EndX=-49.19 EndY=8.5 EndZ=0
    g2: ArcOfCircle CenterX=-1.5 CenterY=62 CenterZ=0 NormalX=0 NormalY=0 NormalZ=1 AngleXU=0 Radius=1.5 StartAngle=4.71239 EndAngle=7.85398
    g3: ArcOfCircle CenterX=-1.5 CenterY=10 CenterZ=0 NormalX=0 NormalY=0 NormalZ=1 AngleXU=0 Radius=1.5 StartAngle=4.71239 EndAngle=7.85398
    g4: LineSegment StartX=-49.19 StartY=63.5 StartZ=0 EndX=-1.5 EndY=63.5 EndZ=0
    g5: LineSegment StartX=-49.19 StartY=60.5 StartZ=0 EndX=-1.5 EndY=60.5 EndZ=0
    g6: LineSegment StartX=-49.19 StartY=11.5 StartZ=0 EndX=-1.5 EndY=11.5 EndZ=0
    g7: LineSegment StartX=-49.19 StartY=8.5 StartZ=0 EndX=-1.5 EndY=8.5 EndZ=0
  constraints (19):
    c: Vertical(g0)
    c: Distance(g0) = 3
    c: Vertical(g1)
    c: Block(g1)
    c: Block(g2)
    c: Block(g3)
    c: Block(g0)
    c: Coincident(g4,g0)
    c: Coincident(g4,g2)
    c: Horizontal(g4)
    c: Coincident(g5,g0)
    c: Coincident(g5,g2)
    c: Horizontal(g5)
    c: Coincident(g6,g1)
    c: Coincident(g6,g3)
    c: Horizontal(g6)
    c: Coincident(g7,g1)
    c: Coincident(g7,g3)
    c: Horizontal(g7)
FEATURE [Part::Extrusion] Extrude068
  Base = -> Sketch077
  Dir = (1,0,0)
  DirMode = 2
  FaceMakerClass = Part::FaceMakerBullseye
  LengthFwd = 10
  LengthRev = 0
  Solid = true
  Symmetric = false
FEATURE [Part::Fillet] Fillet057  label="removeFromtMoreFrontCaseScrewRetainers002"
  Base = -> Extrude068
  Edges = 4 edges r=1.49: [Edge6,Edge11,Edge18,Edge23]
  Placement = pos=(-12,0,0) rot=(0,0,1;0rad)
FEATURE [Sketcher::SketchObject] Sketch078
  FullyConstrained = true
  Placement = pos=(117,19,0) rot=(0.57735,0.57735,0.57735;2.0944rad)
  sketch-geometry (8):
    g0: LineSegment StartX=-49.19 StartY=69.25 StartZ=0 EndX=-49.19 EndY=66.25 EndZ=0
    g1: LineSegment StartX=-49.19 StartY=5.75 StartZ=0 EndX=-49.19 EndY=2.75 EndZ=0
    g2: ArcOfCircle CenterX=-1.5 CenterY=67.75 CenterZ=0 NormalX=0 NormalY=0 NormalZ=1 AngleXU=0 Radius=1.5 StartAngle=4.71239 EndAngle=7.85398
    g3: ArcOfCircle CenterX=-1.5 CenterY=4.25 CenterZ=0 NormalX=0 NormalY=0 NormalZ=1 AngleXU=0 Radius=1.5 StartAngle=4.71239 EndAngle=7.85398
    g4: LineSegment StartX=-49.19 StartY=69.25 StartZ=0 EndX=-1.5 EndY=69.25 EndZ=0
    g5: LineSegment StartX=-49.19 StartY=66.25 StartZ=0 EndX=-1.5 EndY=66.25 EndZ=0
    g6: LineSegment StartX=-49.19 StartY=5.75 StartZ=0 EndX=-1.5 EndY=5.75 EndZ=0
    g7: LineSegment StartX=-49.19 StartY=2.75 StartZ=0 EndX=-1.5 EndY=2.75 EndZ=0
  constraints (19):
    c: Vertical(g0)
    c: Distance(g0) = 3
    c: Block(g0)
    c: Vertical(g1)
    c: Block(g2)
    c: Block(g3)
    c: Block(g1)
    c: Coincident(g4,g0)
    c: Coincident(g4,g2)
    c: Horizontal(g4)
    c: Coincident(g5,g0)
    c: Coincident(g5,g2)
    c: Horizontal(g5)
    c: Coincident(g6,g1)
    c: Coincident(g6,g3)
    c: Horizontal(g6)
    c: Coincident(g7,g1)
    c: Coincident(g7,g3)
    c: Horizontal(g7)
FEATURE [Part::Extrusion] Extrude069
  Base = -> Sketch078
  Dir = (1,0,0)
  DirMode = 2
  FaceMakerClass = Part::FaceMakerBullseye
  LengthFwd = 10
  LengthRev = 0
  Solid = true
  Symmetric = false
FEATURE [Part::Fillet] Fillet058  label="removeFromtMoreFrontCaseScrewRetainers003"
  Base = -> Extrude069
  Edges = 4 edges r=1.49: [Edge6,Edge11,Edge18,Edge23]
  Placement = pos=(-4,0,0) rot=(0,0,1;0rad)
FEATURE [Part::Cut] Cut066
  Base = -> Cut065
  Tool = -> Fillet058
FEATURE [Part::Cut] Cut067  label="screwPillars"
  Base = -> Cut066
  Tool = -> Fillet057
FEATURE [Part::MultiFuse] Fusion143  label="bottom021"
  Shapes = -> [Cut031,Cut063]
FEATURE [Part::Cylinder] Cylinder
  Angle = 360
  AttacherType = Attacher::AttachEngine3D
  Height = 10
  Placement = pos=(20.65,12,4.68) rot=(1,0,0;1.5708rad)
  Radius = 2
FEATURE [Part::Cylinder] Cylinder064
  Angle = 360
  AttacherType = Attacher::AttachEngine3D
  Height = 10
  Placement = pos=(20.65,12,67.38) rot=(1,0,0;1.5708rad)
  Radius = 2
FEATURE [Part::Cylinder] Cylinder065
  Angle = 360
  AttacherType = Attacher::AttachEngine3D
  Height = 10
  Placement = pos=(77.15,12,67.38) rot=(1,0,0;1.5708rad)
  Radius = 2
FEATURE [Part::Cylinder] Cylinder066
  Angle = 360
  AttacherType = Attacher::AttachEngine3D
  Height = 10
  Placement = pos=(77.15,12,4.68) rot=(1,0,0;1.5708rad)
  Radius = 2
FEATURE [Part::MultiFuse] Fusion144  label="removeFromThreadedInsertHousing"
  Shapes = -> [Cylinder065,Cylinder064,Cylinder,Cylinder066]
FEATURE [Part::Cut] Cut068  label="pcbStands001"
  Base = -> Cut064
  Tool = -> Fusion144
FEATURE [Part::MultiFuse] Fusion145
  Shapes = -> [Cut068,Fusion143]
FEATURE [Part::MultiFuse] Fusion146
  Shapes = -> [Fusion145]
FEATURE [Part::MultiFuse] Fusion147  label="bottom022"
  Shapes = -> [Cut067,Fusion146]
FEATURE [Part::MultiFuse] Fusion148  label="casePillars005"
  Shapes = -> [Cut047,Fusion092]
FEATURE [Part::MultiFuse] Fusion149  label="bottom023"
  Shapes = -> [Fusion124,Fusion113,Fusion147]
FEATURE [Part::MultiFuse] Fusion150  label="topBits"
  Shapes = -> [Cut025,Fusion148,Cut030,Fillet034]
FEATURE [Part::Feature] Face149 .. Face152  x4 (patterned run collapsed; names and placements below)
  shape: bbox 3.2 x 1.5 x 2e-07 mm, 1 faces, 0 solids (baked)
FEATURE [Part::Feature] Face153
  shape: bbox 3.6 x 3.2 x 2e-07 mm, 1 faces, 0 solids (baked)
FEATURE [Part::Feature] Face154
  shape: bbox 3.6 x 3.2 x 2e-07 mm, 1 faces, 0 solids (baked)
FEATURE [Sketcher::SketchObject] Sketch079  label="topSketch024"
  FullyConstrained = true
  sketch-geometry (6):
    g0: LineSegment StartX=19 StartY=38 StartZ=0 EndX=117 EndY=38 EndZ=0
    g1: ArcOfCircle CenterX=19 CenterY=19 CenterZ=0 NormalX=0 NormalY=0 NormalZ=1 AngleXU=0 Radius=19 StartAngle=1.5708 EndAngle=3.14159
    g2: LineSegment StartX=117 StartY=38 StartZ=0 EndX=117 EndY=19 EndZ=0
    g3: LineSegment StartX=98 StartY=1.0161e-12 StartZ=0 EndX=5.22862e-06 EndY=1.0161e-12 EndZ=0
    g4: LineSegment StartX=5.22862e-06 StartY=19 StartZ=0 EndX=5.22862e-06 EndY=1.0161e-12 EndZ=0
    g5: ArcOfCircle CenterX=98 CenterY=19 CenterZ=0 NormalX=0 NormalY=0 NormalZ=1 AngleXU=0 Radius=19 StartAngle=4.71239 EndAngle=6.28319
  constraints (16):
    c: Horizontal(g0)
    c: Distance(g0) = 98
    c: Coincident(g1,g0)
    c: Block(g1)
    c: Coincident(g2,g0)
    c: Vertical(g2)
    c: Distance(g2) = 19
    c: Horizontal(g3)
    c: Coincident(g4,g1)
    c: Vertical(g4)
    c: Coincident(g3,g4)
    c: Block(g3)
    c: Coincident(g5,g2)
    c: Coincident(g5,g3)
    c: Block(g0)
    c: Block(g5)
FEATURE [Sketcher::SketchObject] Sketch080  label="topSketch025"
  FullyConstrained = true
  sketch-geometry (6):
    g0: LineSegment StartX=19 StartY=38 StartZ=0 EndX=117 EndY=38 EndZ=0
    g1: ArcOfCircle CenterX=19 CenterY=19 CenterZ=0 NormalX=0 NormalY=0 NormalZ=1 AngleXU=0 Radius=19 StartAngle=1.5708 EndAngle=3.14159
    g2: LineSegment StartX=117 StartY=38 StartZ=0 EndX=117 EndY=19 EndZ=0
    g3: LineSegment StartX=98 StartY=1.0161e-12 StartZ=0 EndX=5.22862e-06 EndY=1.0161e-12 EndZ=0
    g4: LineSegment StartX=5.22862e-06 StartY=19 StartZ=0 EndX=5.22862e-06 EndY=1.0161e-12 EndZ=0
    g5: ArcOfCircle CenterX=98 CenterY=19 CenterZ=0 NormalX=0 NormalY=0 NormalZ=1 AngleXU=0 Radius=19 StartAngle=4.71239 EndAngle=6.28319
  constraints (16):
    c: Horizontal(g0)
    c: Distance(g0) = 98
    c: Coincident(g1,g0)
    c: Block(g1)
    c: Coincident(g2,g0)
    c: Vertical(g2)
    c: Distance(g2) = 19
    c: Horizontal(g3)
    c: Coincident(g4,g1)
    c: Vertical(g4)
    c: Coincident(g3,g4)
    c: Block(g3)
    c: Coincident(g5,g2)
    c: Coincident(g5,g3)
    c: Block(g0)
    c: Block(g5)
FEATURE [Part::Extrusion] Extrude070  label="sideA004"
  Base = -> Sketch080
  Dir = (0,0,1)
  DirMode = 2
  FaceMakerClass = Part::FaceMakerBullseye
  LengthFwd = 3
  LengthRev = 0
  Placement = pos=(0,0,-2.7) rot=(0,0,1;0rad)
  Solid = true
  Symmetric = false
FEATURE [Sketcher::SketchObject] Sketch081
  FullyConstrained = true
  Placement = pos=(117,19,0) rot=(0.57735,0.57735,0.57735;2.0944rad)
  sketch-geometry (8):
    g0: LineSegment StartX=-49.19 StartY=63.5 StartZ=0 EndX=-49.19 EndY=60.5 EndZ=0
    g1: LineSegment StartX=-49.19 StartY=11.5 StartZ=0 EndX=-49.19 EndY=8.5 EndZ=0
    g2: ArcOfCircle CenterX=-1.5 CenterY=62 CenterZ=0 NormalX=0 NormalY=0 NormalZ=1 AngleXU=0 Radius=1.5 StartAngle=4.71239 EndAngle=7.85398
    g3: ArcOfCircle CenterX=-1.5 CenterY=10 CenterZ=0 NormalX=0 NormalY=0 NormalZ=1 AngleXU=0 Radius=1.5 StartAngle=4.71239 EndAngle=7.85398
    g4: LineSegment StartX=-49.19 StartY=63.5 StartZ=0 EndX=-1.5 EndY=63.5 EndZ=0
    g5: LineSegment StartX=-49.19 StartY=60.5 StartZ=0 EndX=-1.5 EndY=60.5 EndZ=0
    g6: LineSegment StartX=-49.19 StartY=11.5 StartZ=0 EndX=-1.5 EndY=11.5 EndZ=0
    g7: LineSegment StartX=-49.19 StartY=8.5 StartZ=0 EndX=-1.5 EndY=8.5 EndZ=0
  constraints (19):
    c: Vertical(g0)
    c: Distance(g0) = 3
    c: Vertical(g1)
    c: Block(g1)
    c: Block(g2)
    c: Block(g3)
    c: Block(g0)
    c: Coincident(g4,g0)
    c: Coincident(g4,g2)
    c: Horizontal(g4)
    c: Coincident(g5,g0)
    c: Coincident(g5,g2)
    c: Horizontal(g5)
    c: Coincident(g6,g1)
    c: Coincident(g6,g3)
    c: Horizontal(g6)
    c: Coincident(g7,g1)
    c: Coincident(g7,g3)
    c: Horizontal(g7)
FEATURE [Part::Extrusion] Extrude071  label="sideB004"
  Base = -> Sketch079
  Dir = (0,0,1)
  DirMode = 2
  FaceMakerClass = Part::FaceMakerBullseye
  LengthFwd = 3
  LengthRev = 0
  Placement = pos=(0,0,71.7) rot=(0,0,1;0rad)
  Solid = true
  Symmetric = false
FEATURE [Part::MultiFuse] Fusion152  label="removeFromBottom004"
  Placement = pos=(2,0,0) rot=(0,0,1;0rad)
  Shapes = -> [Extrude070,Extrude071]
FEATURE [Part::Extrusion] Extrude072
  Base = -> Sketch081
  Dir = (1,0,0)
  DirMode = 2
  FaceMakerClass = Part::FaceMakerBullseye
  LengthFwd = 10
  LengthRev = 0
  Solid = true
  Symmetric = false
FEATURE [Part::Fillet] Fillet059  label="removeFromtMoreFrontCaseScrewRetainers004"
  Base = -> Extrude072
  Edges = 4 edges r=1.49: [Edge6,Edge11,Edge18,Edge23]
  Placement = pos=(-12,0,0) rot=(0,0,1;0rad)
FEATURE [Sketcher::SketchObject] Sketch082
  FullyConstrained = true
  Placement = pos=(117,19,0) rot=(0.57735,0.57735,0.57735;2.0944rad)
  sketch-geometry (8):
    g0: LineSegment StartX=-49.19 StartY=69.25 StartZ=0 EndX=-49.19 EndY=66.25 EndZ=0
    g1: LineSegment StartX=-49.19 StartY=5.75 StartZ=0 EndX=-49.19 EndY=2.75 EndZ=0
    g2: ArcOfCircle CenterX=-1.5 CenterY=67.75 CenterZ=0 NormalX=0 NormalY=0 NormalZ=1 AngleXU=0 Radius=1.5 StartAngle=4.71239 EndAngle=7.85398
    g3: ArcOfCircle CenterX=-1.5 CenterY=4.25 CenterZ=0 NormalX=0 NormalY=0 NormalZ=1 AngleXU=0 Radius=1.5 StartAngle=4.71239 EndAngle=7.85398
    g4: LineSegment StartX=-49.19 StartY=69.25 StartZ=0 EndX=-1.5 EndY=69.25 EndZ=0
    g5: LineSegment StartX=-49.19 StartY=66.25 StartZ=0 EndX=-1.5 EndY=66.25 EndZ=0
    g6: LineSegment StartX=-49.19 StartY=5.75 StartZ=0 EndX=-1.5 EndY=5.75 EndZ=0
    g7: LineSegment StartX=-49.19 StartY=2.75 StartZ=0 EndX=-1.5 EndY=2.75 EndZ=0
  constraints (19):
    c: Vertical(g0)
    c: Distance(g0) = 3
    c: Block(g0)
    c: Vertical(g1)
    c: Block(g2)
    c: Block(g3)
    c: Block(g1)
    c: Coincident(g4,g0)
    c: Coincident(g4,g2)
    c: Horizontal(g4)
    c: Coincident(g5,g0)
    c: Coincident(g5,g2)
    c: Horizontal(g5)
    c: Coincident(g6,g1)
    c: Coincident(g6,g3)
    c: Horizontal(g6)
    c: Coincident(g7,g1)
    c: Coincident(g7,g3)
    c: Horizontal(g7)
FEATURE [Part::Extrusion] Extrude073
  Base = -> Sketch082
  Dir = (1,0,0)
  DirMode = 2
  FaceMakerClass = Part::FaceMakerBullseye
  LengthFwd = 10
  LengthRev = 0
  Solid = true
  Symmetric = false
FEATURE [Part::Fillet] Fillet060  label="removeFromtMoreFrontCaseScrewRetainers005"
  Base = -> Extrude073
  Edges = 4 edges r=1.49: [Edge6,Edge11,Edge18,Edge23]
  Placement = pos=(-4,0,0) rot=(0,0,1;0rad)
FEATURE [Part::Revolution] Revolve163  label="backCaseScrewRetainer004"
  Angle = 360
  Axis = (0,1,0)
  Base = (0,0,0)
  FaceMakerClass = Part::FaceMakerBullseye
  Placement = pos=(12.5,3,62) rot=(0,0,1;0rad)
  Solid = false
  Source = -> Face149
  Symmetric = false
FEATURE [Part::Revolution] Revolve164  label="frontCaseScrewRetainer006"
  Angle = 360
  Axis = (0,1,0)
  Base = (0,0,0)
  FaceMakerClass = Part::FaceMakerBullseye
  Placement = pos=(89.5,3,68.5) rot=(0,0,1;0rad)
  Solid = false
  Source = -> Face151
  Symmetric = false
FEATURE [Part::Revolution] Revolve165  label="frontCaseScrewRetainer007"
  Angle = 360
  Axis = (0,1,0)
  Base = (0,0,0)
  FaceMakerClass = Part::FaceMakerBullseye
  Placement = pos=(89.5,3,3.5) rot=(0,0,1;0rad)
  Solid = false
  Source = -> Face152
  Symmetric = false
FEATURE [Part::Revolution] Revolve166  label="backCaseScrewRetainer005"
  Angle = 360
  Axis = (0,1,0)
  Base = (0,0,0)
  FaceMakerClass = Part::FaceMakerBullseye
  Placement = pos=(12.5,3,10) rot=(0,0,1;0rad)
  Solid = false
  Source = -> Face150
  Symmetric = false
FEATURE [Part::Revolution] Revolve167  label="moreFrontCaseScrewRetainer006"
  Angle = 360
  Axis = (0,1,0)
  Base = (0,0,0)
  FaceMakerClass = Part::FaceMakerBullseye
  Placement = pos=(109.5,4.5,68.5) rot=(0,0,1;0rad)
  Solid = false
  Source = -> Face153
  Symmetric = false
FEATURE [Part::Revolution] Revolve168  label="moreFrontCaseScrewRetainer007"
  Angle = 360
  Axis = (0,1,0)
  Base = (0,0,0)
  FaceMakerClass = Part::FaceMakerBullseye
  Placement = pos=(109.5,4.5,3.5) rot=(0,0,1;0rad)
  Solid = false
  Source = -> Face154
  Symmetric = false
FEATURE [Part::MultiFuse] Fusion151  label="screwRetainers003"
  Shapes = -> [Revolve168,Revolve167,Revolve166,Revolve165,Revolve164,Revolve163]
FEATURE [Part::Cut] Cut069  label="screwRetainers004"
  Base = -> Fusion151
  Tool = -> Fusion152
FEATURE [Part::Cut] Cut070
  Base = -> Cut069
  Tool = -> Fillet060
FEATURE [Part::Cut] Cut071  label="screwPillars001"
  Base = -> Cut070
  Tool = -> Fillet059
FEATURE [Part::MultiFuse] Fusion153  label="bottom024"
  Shapes = -> [Fusion149,Cut071]
FEATURE [Part::Cylinder] Cylinder067
  Angle = 360
  AttacherType = Attacher::AttachEngine3D
  Height = 10
  Placement = pos=(20.65,12,4.68) rot=(1,0,0;1.5708rad)
  Radius = 2
FEATURE [Part::Cylinder] Cylinder068
  Angle = 360
  AttacherType = Attacher::AttachEngine3D
  Height = 10
  Placement = pos=(20.65,12,67.38) rot=(1,0,0;1.5708rad)
  Radius = 2
FEATURE [Part::Cylinder] Cylinder069
  Angle = 360
  AttacherType = Attacher::AttachEngine3D
  Height = 10
  Placement = pos=(77.15,12,67.38) rot=(1,0,0;1.5708rad)
  Radius = 2
FEATURE [Part::Cylinder] Cylinder070
  Angle = 360
  AttacherType = Attacher::AttachEngine3D
  Height = 10
  Placement = pos=(77.15,12,4.68) rot=(1,0,0;1.5708rad)
  Radius = 2
FEATURE [Part::MultiFuse] Fusion154  label="removeFromThreadedInsertHousing001"
  Shapes = -> [Cylinder069,Cylinder068,Cylinder067,Cylinder070]
FEATURE [Part::Cut] Cut072  label="bottom025"
  Base = -> Fusion153
  Tool = -> Fusion154
FEATURE [Image::ImagePlane] ImagePlane
  XSize = 339
  YSize = 72
FEATURE [Sketcher::SketchObject] Sketch083
  FullyConstrained = true
  MapMode = 5
  Support = -> [XY_Plane]
  sketch-geometry (189):
    g0: LineSegment StartX=-151.619 StartY=28.8932 StartZ=0 EndX=-140.819 EndY=28.8932 EndZ=0
    g1: LineSegment StartX=-151.619 StartY=24.0313 StartZ=0 EndX=-151.619 EndY=28.8932 EndZ=0
    g2: LineSegment StartX=-140.819 StartY=17.7713 StartZ=0 EndX=-151.619 EndY=17.7713 EndZ=0
    g3: LineSegment StartX=-151.619 StartY=17.7713 StartZ=0 EndX=-151.619 EndY=22.6313 EndZ=0
    g4: LineSegment StartX=-151.619 StartY=22.6313 StartZ=0 EndX=-145.128 EndY=22.6313 EndZ=0
    g5: LineSegment StartX=-145.128 StartY=24.0313 StartZ=0 EndX=-140.819 EndY=28.8932 EndZ=0
    g6: LineSegment StartX=-145.128 StartY=22.6313 StartZ=0 EndX=-140.819 EndY=17.7713 EndZ=0
    g7: ArcOfCircle CenterX=-155.157 CenterY=23.3323 CenterZ=0 NormalX=0 NormalY=0 NormalZ=1 AngleXU=0 Radius=6.92354 StartAngle=1.03434 EndAngle=5.24885
    g8: ArcOfCircle CenterX=-155.157 CenterY=23.3323 CenterZ=0 NormalX=0 NormalY=0 NormalZ=1 AngleXU=0 Radius=12.6269 StartAngle=1.28675 EndAngle=4.99643
    g9: LineSegment StartX=-151.619 StartY=35.4532 StartZ=0 EndX=-151.619 EndY=29.2832 EndZ=0
    g10: LineSegment StartX=-151.619 StartY=17.3813 StartZ=0 EndX=-151.619 EndY=11.2113 EndZ=0
    g11-g21: Circle x11 (B-spline internal-alignment scaffolding for g22; pole/knot coordinates omitted)
    g22: BSplineCurve PolesCount=11 KnotsCount=9 Degree=3 IsPeriodic=0
    g23-g31: GeomPoint x9 (B-spline internal-alignment scaffolding for g22; pole/knot coordinates omitted)
    g32-g49: Circle x18 (B-spline internal-alignment scaffolding for g50; pole/knot coordinates omitted)
    g50: BSplineCurve PolesCount=18 KnotsCount=16 Degree=3 IsPeriodic=0
    g51-g66: GeomPoint x16 (B-spline internal-alignment scaffolding for g50; pole/knot coordinates omitted)
    g67: LineSegment StartX=-117.124 StartY=30.093 StartZ=0 EndX=-117.603 EndY=26.5272 EndZ=0
    g68: LineSegment StartX=-117.603 StartY=17.8472 StartZ=0 EndX=-117.124 EndY=14.2659 EndZ=0
    g69: Ellipse CenterX=-109.671 CenterY=20.025 CenterZ=0 NormalX=0 NormalY=0 NormalZ=1 MajorRadius=3.34798 MinorRadius=2.71052 AngleXU=-1.56793
    g70: GeomPoint X=-109.666 Y=18.0598 Z=0
    g71: GeomPoint X=-109.677 Y=21.9902 Z=0
    g72: Ellipse CenterX=-109.671 CenterY=20.0123 CenterZ=0 NormalX=0 NormalY=0 NormalZ=1 MajorRadius=6.93002 MinorRadius=6.36273 AngleXU=-3.13976
    g73: GeomPoint X=-112.417 Y=20.0073 Z=0
    g74: GeomPoint X=-106.925 Y=20.0173 Z=0
    g75: Ellipse CenterX=-51.7682 CenterY=20.1463 CenterZ=0 NormalX=0 NormalY=0 NormalZ=1 MajorRadius=3.19279 MinorRadius=2.71052 AngleXU=-1.52774
    g76: GeomPoint X=-51.6955 Y=18.4606 Z=0
    g77: GeomPoint X=-51.8408 Y=21.832 Z=0
    g78: GeomPoint X=-54.5142 Y=20.1413 Z=0
    g79: GeomPoint X=-49.0221 Y=20.1513 Z=0
    g80: Ellipse CenterX=-51.7682 CenterY=20.1463 CenterZ=0 NormalX=0 NormalY=0 NormalZ=1 MajorRadius=6.93002 MinorRadius=6.36273 AngleXU=-3.13976
    g81: Ellipse CenterX=-22.8436 CenterY=20.1783 CenterZ=0 NormalX=0 NormalY=0 NormalZ=1 MajorRadius=3.31512 MinorRadius=2.71052 AngleXU=-1.60214
    g82: GeomPoint X=-22.9034 Y=18.2706 Z=0
    g83: GeomPoint X=-22.7838 Y=22.0861 Z=0
    g84: GeomPoint X=-25.5897 Y=20.1733 Z=0
    g85: GeomPoint X=-20.0976 Y=20.1833 Z=0
    g86: Ellipse CenterX=-22.8436 CenterY=20.1783 CenterZ=0 NormalX=0 NormalY=0 NormalZ=1 MajorRadius=6.93002 MinorRadius=6.36273 AngleXU=-3.13976
    g87: LineSegment StartX=-101.889 StartY=14.1107 StartZ=0 EndX=-97.7455 EndY=14.1107 EndZ=0
    g88: LineSegment StartX=-93.8155 StartY=14.1107 StartZ=0 EndX=-89.6755 EndY=14.1107 EndZ=0
    g89: LineSegment StartX=-85.7455 StartY=14.1107 StartZ=0 EndX=-81.6055 EndY=14.1107 EndZ=0
    g90: LineSegment StartX=-101.889 StartY=14.1107 StartZ=0 EndX=-101.889 EndY=25.9907 EndZ=0
    g91: LineSegment StartX=-101.889 StartY=25.9907 StartZ=0 EndX=-97.8594 EndY=25.9907 EndZ=0
    g92: LineSegment StartX=-97.8594 StartY=25.9907 StartZ=0 EndX=-97.8594 EndY=24.0907 EndZ=0
    g93: LineSegment StartX=-97.7455 StartY=14.1107 StartZ=0 EndX=-97.7455 EndY=19.9107 EndZ=0
    g94: LineSegment StartX=-89.6755 StartY=14.1107 StartZ=0 EndX=-89.6755 EndY=19.9107 EndZ=0
    g95: LineSegment StartX=-93.8155 StartY=14.1107 StartZ=0 EndX=-93.8155 EndY=21.0107 EndZ=0
    g96-g106: Circle x11 (B-spline internal-alignment scaffolding for g107; pole/knot coordinates omitted)
    g107: BSplineCurve PolesCount=11 KnotsCount=9 Degree=3 IsPeriodic=0
    g108-g116: GeomPoint x9 (B-spline internal-alignment scaffolding for g107; pole/knot coordinates omitted)
    g117: BSplineCurve PolesCount=11 KnotsCount=9 Degree=3 IsPeriodic=0
    g118-g125: Circle x8 (B-spline internal-alignment scaffolding for g126; pole/knot coordinates omitted)
    g126: BSplineCurve PolesCount=8 KnotsCount=6 Degree=3 IsPeriodic=0
    g127-g132: GeomPoint x6 (B-spline internal-alignment scaffolding for g126; pole/knot coordinates omitted)
    g133: BSplineCurve PolesCount=8 KnotsCount=6 Degree=3 IsPeriodic=0
    g134: LineSegment StartX=-85.7455 StartY=21.0107 StartZ=0 EndX=-85.7455 EndY=14.1107 EndZ=0
    g135: LineSegment StartX=-80.0879 StartY=14.1107 StartZ=0 EndX=-75.944 EndY=14.1107 EndZ=0
    g136: LineSegment StartX=-72.014 StartY=14.1107 StartZ=0 EndX=-67.874 EndY=14.1107 EndZ=0
    g137: LineSegment StartX=-63.944 StartY=14.1107 StartZ=0 EndX=-59.804 EndY=14.1107 EndZ=0
    g138: LineSegment StartX=-80.0879 StartY=14.1107 StartZ=0 EndX=-80.0879 EndY=25.9907 EndZ=0
    g139: LineSegment StartX=-80.0879 StartY=25.9907 StartZ=0 EndX=-76.0579 EndY=25.9907 EndZ=0
    g140: LineSegment StartX=-76.0579 StartY=25.9907 StartZ=0 EndX=-76.0579 EndY=24.0907 EndZ=0
    g141: LineSegment StartX=-75.944 StartY=14.1107 StartZ=0 EndX=-75.944 EndY=19.9107 EndZ=0
    g142: LineSegment StartX=-67.874 StartY=14.1107 StartZ=0 EndX=-67.874 EndY=19.9107 EndZ=0
    g143: LineSegment StartX=-72.014 StartY=14.1107 StartZ=0 EndX=-72.014 EndY=21.0107 EndZ=0
    g144-g148: Circle x5 (B-spline internal-alignment scaffolding for g149; pole/knot coordinates omitted)
    g149: BSplineCurve PolesCount=11 KnotsCount=9 Degree=3 IsPeriodic=0
    g150-g158: GeomPoint x9 (B-spline internal-alignment scaffolding for g149; pole/knot coordinates omitted)
    g159: BSplineCurve PolesCount=11 KnotsCount=9 Degree=3 IsPeriodic=0
    g160-g167: Circle x8 (B-spline internal-alignment scaffolding for g168; pole/knot coordinates omitted)
    g168: BSplineCurve PolesCount=8 KnotsCount=6 Degree=3 IsPeriodic=0
    g169-g174: GeomPoint x6 (B-spline internal-alignment scaffolding for g168; pole/knot coordinates omitted)
    g175: BSplineCurve PolesCount=8 KnotsCount=6 Degree=3 IsPeriodic=0
    g176: LineSegment StartX=-63.944 StartY=21.0107 StartZ=0 EndX=-63.944 EndY=14.1107 EndZ=0
    g177: LineSegment StartX=-59.804 StartY=14.1107 StartZ=0 EndX=-59.804 EndY=21.5868 EndZ=0
    g178: BSplineCurve PolesCount=4 KnotsCount=2 Degree=3 IsPeriodic=0
    g179: GeomPoint X=-59.804 Y=21.5868 Z=0
    g180: GeomPoint X=-60.2379 Y=24.0907 Z=0
    g181: LineSegment StartX=-81.6055 StartY=14.1107 StartZ=0 EndX=-81.6055 EndY=21.5868 EndZ=0
    g182: LineSegment StartX=-151.619 StartY=24.0313 StartZ=0 EndX=-145.128 EndY=24.0313 EndZ=0
    g183: Circle CenterX=-82.0394 CenterY=24.0907 CenterZ=0 NormalX=0 NormalY=0 NormalZ=1 AngleXU=0 Radius=1
    g184: Circle CenterX=-81.7131 CenterY=23.2736 CenterZ=0 NormalX=0 NormalY=0 NormalZ=1 AngleXU=0 Radius=1
    g185: Circle CenterX=-81.6055 CenterY=21.5868 CenterZ=0 NormalX=0 NormalY=0 NormalZ=1 AngleXU=0 Radius=1
    g186: BSplineCurve PolesCount=3 KnotsCount=2 Degree=2 IsPeriodic=0
    g187: GeomPoint X=-82.0394 Y=24.0907 Z=0
    g188: GeomPoint X=-81.6055 Y=21.5868 Z=0
  constraints (172):
    c: Coincident(g1,g0)
    c: Horizontal(g0)
    c: Vertical(g1)
    c: Coincident(g2,g3)
    c: Coincident(g3,g4)
    c: Horizontal(g4)
    c: Horizontal(g2)
    c: Vertical(g3)
    c: Block(g1)
    c: Distance(g3) = 4.86
    c: Block(g4)
    c: Distance(g0) = 10.8
    c: Distance(g2) = 10.8
    c: Coincident(g5,g0)
    c: Coincident(g6,g4)
    c: Coincident(g6,g2)
    c: Block(g8)
    c: Block(g7)
    c: Coincident(g9,g8)
    c: Coincident(g9,g7)
    c: Vertical(g9)
    c: Coincident(g10,g7)
    c: Coincident(g10,g8)
    c: Vertical(g10)
    c: Weight(g11) = 1
    c: Equal(g11, g12-g21) x10
    c: InternalAlignment(g11-g21 -> g22) x11
    c: InternalAlignment(g23-g31 -> g22) x9
    c: Block(g22)
    c: Weight(g32) = 1
    c: Equal(g32, g33-g49) x17
    c: InternalAlignment(g32-g49 -> g50) x18
    c: InternalAlignment(g51-g66 -> g50) x16
    c: Block(g50)
    c: Coincident(g67,g50)
    c: Coincident(g67,g22)
    c: Coincident(g68,g22)
    c: Coincident(g68,g50)
    c: InternalAlignment(g70,g69)
    c: InternalAlignment(g71,g69)
    c: Block(g69)
    c: InternalAlignment(g73,g72)
    c: InternalAlignment(g74,g72)
    c: Block(g72)
    c: InternalAlignment(g76,g75)
    c: InternalAlignment(g77,g75)
    c: InternalAlignment(g78,g80)
    c: InternalAlignment(g79,g80)
    c: Block(g80)
    c: Coincident(g75,g80)
    c: Block(g75)
    c: InternalAlignment(g82,g81)
    c: InternalAlignment(g83,g81)
    c: InternalAlignment(g84,g86)
    c: InternalAlignment(g85,g86)
    c: Block(g86)
    c: Coincident(g81,g86)
    c: Block(g81)
    c: Horizontal(g87)
    c: Block(g87)
    c: Horizontal(g88)
    c: Distance(g88) = 4.14
    c: Horizontal(g89)
    c: Equal(g88,g89) = 4.14
    c: Block(g89)
    c: Block(g88)
    c: Coincident(g90,g87)
    c: Vertical(g90)
    c: Distance(g90) = 11.88
    c: Coincident(g91,g90)
    c: Horizontal(g91)
    c: Coincident(g92,g91)
    c: Vertical(g92)
    c: Distance(g91) = 4.03
    c: Distance(g92) = 1.9
    c: Coincident(g93,g87)
    c: Vertical(g93)
    c: Vertical(g94)
    c: Coincident(g94,g88)
    c: Distance(g93) = 5.8
    c: Distance(g94) = 5.8
    c: Vertical(g95)
    c: Coincident(g95,g88)
    c: Distance(g95) = 6.9
    c: Coincident(g107,g92)
    c: Weight(g96) = 1
    c: Equal(g96, g97-g106) x10
    c: InternalAlignment(g96-g106 -> g107) x11
    c: InternalAlignment(g108-g116 -> g107) x9
    c: Block(g107)
    c: Block(g117)
    c: Coincident(g126,g93)
    c: Weight(g118) = 1
    c: Equal(g118, g119-g125) x7
    c: Coincident(g126,g95)
    c: InternalAlignment(g118-g125 -> g126) x8
    c: InternalAlignment(g127-g132 -> g126) x6
    c: Coincident(g133,g94)
    c: Block(g126)
    c: Block(g133)
    c: Coincident(g134,g133)
    c: Coincident(g134,g89)
    c: Vertical(g134)
    c: Horizontal(g135)
    c: Block(g135)
    c: Horizontal(g136)
    c: Equal(g88,g136) = 4.14
    c: Horizontal(g137)
    c: Equal(g136,g137) = 4.14
    c: Block(g137)
    c: Block(g136)
    c: Coincident(g138,g135)
    c: Vertical(g138)
    c: Equal(g90,g138) = 11.88
    c: Coincident(g139,g138)
    c: Horizontal(g139)
    c: Coincident(g140,g139)
    c: Vertical(g140)
    c: Equal(g91,g139) = 4.03
    c: Equal(g92,g140) = 1.9
    c: Coincident(g141,g135)
    c: Vertical(g141)
    c: Vertical(g142)
    c: Coincident(g142,g136)
    c: Equal(g93,g141) = 5.8
    c: Equal(g94,g142) = 5.8
    c: Vertical(g143)
    c: Coincident(g143,g136)
    c: Equal(g95,g143) = 6.9
    c: Coincident(g149,g140)
    c: Equal(g96,g144) = 1
    c: Equal(g144, g145-g148) x4
    c: InternalAlignment(g144-g148 -> g149) x5
    c: InternalAlignment(g150-g158 -> g149) x9
    c: Block(g149)
    c: Block(g159)
    c: Coincident(g168,g141)
    c: Equal(g118,g160) = 1
    c: Equal(g160, g161-g167) x7
    c: Coincident(g168,g143)
    c: InternalAlignment(g160-g167 -> g168) x8
    c: InternalAlignment(g169-g174 -> g168) x6
    c: Coincident(g175,g142)
    c: Block(g168)
    c: Block(g175)
    c: Coincident(g176,g175)
    c: Coincident(g176,g137)
    c: Vertical(g176)
    c: Coincident(g177,g137)
    c: Vertical(g177)
    c: Coincident(g178,g177)
    c: Coincident(g178,g159)
    c: InternalAlignment(g179,g178)
    c: InternalAlignment(g180,g178)
    c: Block(g178)
    c: Vertical(g181)
    c: Coincident(g181,g89)
    c: Block(g5)
    c: Coincident(g182,g1)
    c: Coincident(g182,g5)
    c: Horizontal(g182)
    c: Coincident(g186,g117)
    c: Weight(g183) = 1
    c: Equal(g183,g184)
    c: Equal(g183,g185)
    c: Coincident(g186,g181)
    c: InternalAlignment(g183,g186)
    c: InternalAlignment(g184,g186)
    c: InternalAlignment(g185,g186)
    c: InternalAlignment(g187,g186)
    c: InternalAlignment(g188,g186)
    c: Block(g186)
FEATURE [PartDesign::Body] Body
  Group = -> [Sketch083]
  Origin = -> Origin
FEATURE [Sketcher::SketchObject] Sketch084
  FullyConstrained = true
  MapMode = 5
  Support = -> [XY_Plane001]
FEATURE [PartDesign::Body] Body001
  Group = -> [Sketch084]
  Origin = -> Origin001
